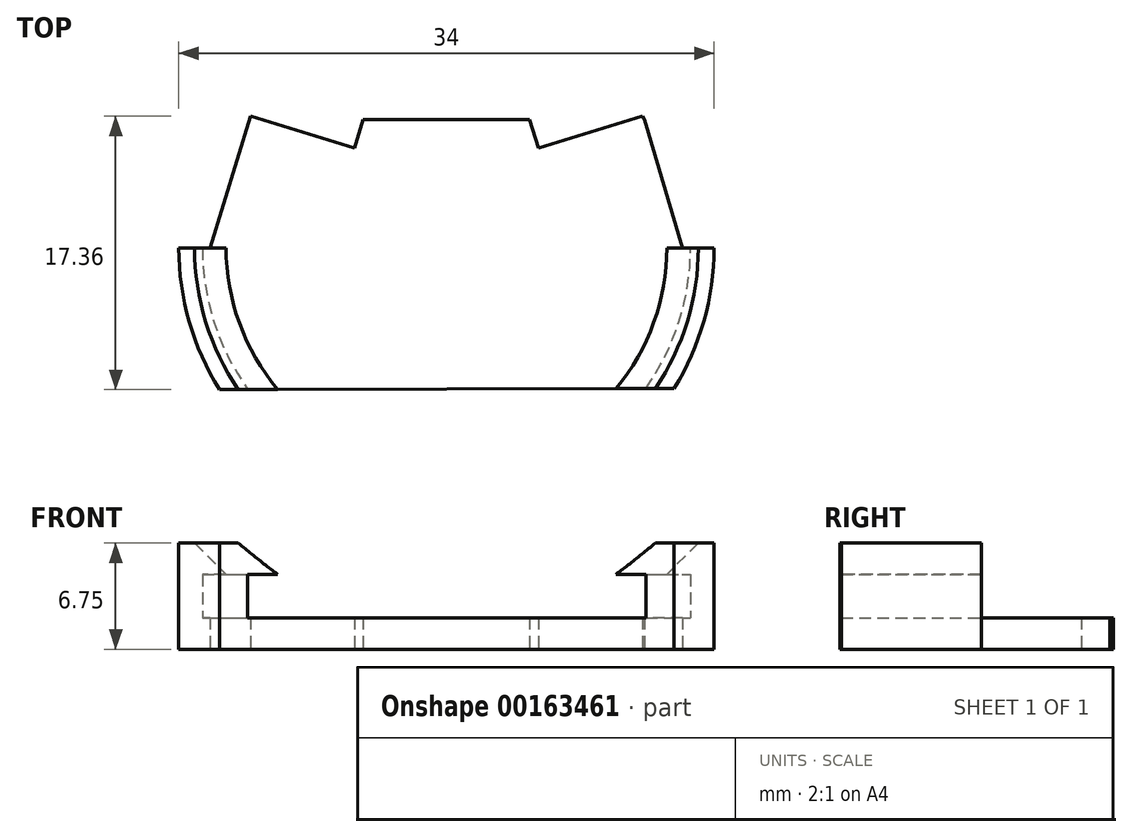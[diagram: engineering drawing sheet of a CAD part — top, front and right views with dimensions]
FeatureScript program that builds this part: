
annotation { "Feature Type Name" : "Feature", "Feature Type Description" : "" }
export const myFeature = defineFeature(function(context is Context, id is Id, definition is map)
    precondition{}
    {
        {
            var Q0;
            Q0=qCreatedBy(makeId("Top.planeOp"),FACE);
            var sketch = newSketch(context, id + "F0", { "sketchPlane" : qUnion([Q0])});
            skLineSegment(sketch, "E0", {"start": v(30.22, 5.42) * mm, "end": v(30.18, 5.6) * mm});
            skLineSegment(sketch, "E1", {"start": v(30.18, 5.6) * mm, "end": v(29.1, 8.94) * mm});
            skLineSegment(sketch, "E2", {"start": v(29.1, 8.94) * mm, "end": v(29.03, 9.1) * mm});
            skLineSegment(sketch, "E3", {"start": v(29.03, 9.1) * mm, "end": v(28.93, 9.25) * mm});
            skLineSegment(sketch, "E4", {"start": v(28.93, 9.25) * mm, "end": v(28.81, 9.38) * mm});
            skLineSegment(sketch, "E5", {"start": v(28.81, 9.38) * mm, "end": v(28.67, 9.48) * mm});
            skLineSegment(sketch, "E6", {"start": v(28.67, 9.48) * mm, "end": v(28.52, 9.56) * mm});
            skLineSegment(sketch, "E7", {"start": v(28.52, 9.56) * mm, "end": v(28.36, 9.6) * mm});
            skLineSegment(sketch, "E8", {"start": v(28.36, 9.6) * mm, "end": v(28.18, 9.63) * mm});
            skLineSegment(sketch, "E9", {"start": v(28.18, 9.63) * mm, "end": v(28, 9.62) * mm});
            skLineSegment(sketch, "E10", {"start": v(28, 9.62) * mm, "end": v(22.92, 8.87) * mm});
            skLineSegment(sketch, "E11", {"start": v(22.92, 8.87) * mm, "end": v(21.71, 8.48) * mm});
            skLineSegment(sketch, "E12", {"start": v(21.71, 8.48) * mm, "end": v(21.66, 8.46) * mm});
            skLineSegment(sketch, "E13", {"start": v(21.66, 8.46) * mm, "end": v(21.62, 8.44) * mm});
            skLineSegment(sketch, "E14", {"start": v(21.62, 8.44) * mm, "end": v(21.58, 8.4) * mm});
            skLineSegment(sketch, "E15", {"start": v(21.58, 8.4) * mm, "end": v(21.54, 8.38) * mm});
            skLineSegment(sketch, "E16", {"start": v(21.54, 8.38) * mm, "end": v(21.5, 8.34) * mm});
            skLineSegment(sketch, "E17", {"start": v(21.5, 8.34) * mm, "end": v(21.47, 8.3) * mm});
            skLineSegment(sketch, "E18", {"start": v(21.47, 8.3) * mm, "end": v(21.44, 8.26) * mm});
            skLineSegment(sketch, "E19", {"start": v(21.44, 8.26) * mm, "end": v(21.32, 8.03) * mm});
            skLineSegment(sketch, "E20", {"start": v(21.32, 8.03) * mm, "end": v(21.2, 7.86) * mm});
            skLineSegment(sketch, "E21", {"start": v(21.2, 7.86) * mm, "end": v(21.07, 7.7) * mm});
            skLineSegment(sketch, "E22", {"start": v(21.07, 7.7) * mm, "end": v(20.92, 7.56) * mm});
            skLineSegment(sketch, "E23", {"start": v(20.92, 7.56) * mm, "end": v(20.77, 7.43) * mm});
            skLineSegment(sketch, "E24", {"start": v(20.77, 7.43) * mm, "end": v(20.6, 7.32) * mm});
            skLineSegment(sketch, "E25", {"start": v(20.6, 7.32) * mm, "end": v(20.4, 7.22) * mm});
            skLineSegment(sketch, "E26", {"start": v(20.4, 7.22) * mm, "end": v(20.22, 7.15) * mm});
            skLineSegment(sketch, "E27", {"start": v(20.22, 7.15) * mm, "end": v(20.02, 7.1) * mm});
            skLineSegment(sketch, "E28", {"start": v(20.02, 7.1) * mm, "end": v(19.81, 7.06) * mm});
            skLineSegment(sketch, "E29", {"start": v(19.81, 7.06) * mm, "end": v(19.6, 7.05) * mm});
            skLineSegment(sketch, "E30", {"start": v(19.6, 7.05) * mm, "end": v(19.4, 7.06) * mm});
            skLineSegment(sketch, "E31", {"start": v(19.4, 7.06) * mm, "end": v(19.2, 7.1) * mm});
            skLineSegment(sketch, "E32", {"start": v(19.2, 7.1) * mm, "end": v(19, 7.14) * mm});
            skLineSegment(sketch, "E33", {"start": v(19, 7.14) * mm, "end": v(18.8, 7.21) * mm});
            skLineSegment(sketch, "E34", {"start": v(18.8, 7.21) * mm, "end": v(18.58, 7.33) * mm});
            skLineSegment(sketch, "E35", {"start": v(18.58, 7.33) * mm, "end": v(18.53, 7.35) * mm});
            skLineSegment(sketch, "E36", {"start": v(18.53, 7.35) * mm, "end": v(18.48, 7.36) * mm});
            skLineSegment(sketch, "E37", {"start": v(18.48, 7.36) * mm, "end": v(18.43, 7.37) * mm});
            skLineSegment(sketch, "E38", {"start": v(18.43, 7.37) * mm, "end": v(18.38, 7.37) * mm});
            skLineSegment(sketch, "E39", {"start": v(18.38, 7.37) * mm, "end": v(18.33, 7.37) * mm});
            skLineSegment(sketch, "E40", {"start": v(18.33, 7.37) * mm, "end": v(18.28, 7.36) * mm});
            skLineSegment(sketch, "E41", {"start": v(18.28, 7.36) * mm, "end": v(18.23, 7.34) * mm});
            skLineSegment(sketch, "E42", {"start": v(18.23, 7.34) * mm, "end": v(13.03, 5.66) * mm});
            skLineSegment(sketch, "E43", {"start": v(13.03, 5.66) * mm, "end": v(13, 5.65) * mm});
            skLineSegment(sketch, "E44", {"start": v(13, 5.65) * mm, "end": v(12.96, 5.65) * mm});
            skLineSegment(sketch, "E45", {"start": v(12.96, 5.65) * mm, "end": v(12.92, 5.64) * mm});
            skLineSegment(sketch, "E46", {"start": v(12.92, 5.64) * mm, "end": v(12.88, 5.64) * mm});
            skLineSegment(sketch, "E47", {"start": v(12.88, 5.64) * mm, "end": v(12.83, 5.64) * mm});
            skLineSegment(sketch, "E48", {"start": v(12.83, 5.64) * mm, "end": v(12.8, 5.64) * mm});
            skLineSegment(sketch, "E49", {"start": v(12.8, 5.64) * mm, "end": v(12.76, 5.65) * mm});
            skLineSegment(sketch, "E50", {"start": v(12.76, 5.65) * mm, "end": v(12.73, 5.66) * mm});
            skLineSegment(sketch, "E51", {"start": v(12.73, 5.66) * mm, "end": v(12.7, 5.68) * mm});
            skLineSegment(sketch, "E52", {"start": v(12.7, 5.68) * mm, "end": v(12.67, 5.7) * mm});
            skLineSegment(sketch, "E53", {"start": v(12.67, 5.7) * mm, "end": v(12.65, 5.72) * mm});
            skLineSegment(sketch, "E54", {"start": v(12.65, 5.72) * mm, "end": v(12.63, 5.74) * mm});
            skLineSegment(sketch, "E55", {"start": v(12.63, 5.74) * mm, "end": v(12.6, 5.77) * mm});
            skLineSegment(sketch, "E56", {"start": v(12.6, 5.77) * mm, "end": v(12.59, 5.8) * mm});
            skLineSegment(sketch, "E57", {"start": v(12.59, 5.8) * mm, "end": v(12.4, 6.07) * mm});
            skLineSegment(sketch, "E58", {"start": v(12.4, 6.07) * mm, "end": v(12.1, 6.48) * mm});
            skLineSegment(sketch, "E59", {"start": v(12.1, 6.48) * mm, "end": v(12.1, 6.5) * mm});
            skLineSegment(sketch, "E60", {"start": v(12.1, 6.5) * mm, "end": v(12.09, 6.52) * mm});
            skLineSegment(sketch, "E61", {"start": v(12.09, 6.52) * mm, "end": v(12.08, 6.54) * mm});
            skLineSegment(sketch, "E62", {"start": v(12.08, 6.54) * mm, "end": v(12.07, 6.56) * mm});
            skLineSegment(sketch, "E63", {"start": v(12.07, 6.56) * mm, "end": v(12.06, 6.58) * mm});
            skLineSegment(sketch, "E64", {"start": v(12.06, 6.58) * mm, "end": v(12.06, 6.6) * mm});
            skLineSegment(sketch, "E65", {"start": v(12.06, 6.6) * mm, "end": v(12.06, 6.63) * mm});
            skLineSegment(sketch, "E66", {"start": v(12.06, 6.63) * mm, "end": v(12.05, 6.65) * mm});
            skLineSegment(sketch, "E67", {"start": v(12.05, 6.65) * mm, "end": v(12.05, 6.67) * mm});
            skLineSegment(sketch, "E68", {"start": v(12.05, 6.67) * mm, "end": v(12.06, 6.7) * mm});
            skLineSegment(sketch, "E69", {"start": v(12.06, 6.7) * mm, "end": v(12.06, 6.71) * mm});
            skLineSegment(sketch, "E70", {"start": v(12.06, 6.71) * mm, "end": v(12.06, 6.73) * mm});
            skLineSegment(sketch, "E71", {"start": v(12.06, 6.73) * mm, "end": v(12.06, 6.73) * mm});
            skLineSegment(sketch, "E72", {"start": v(12.06, 6.73) * mm, "end": v(12.09, 6.78) * mm});
            skLineSegment(sketch, "E73", {"start": v(12.09, 6.78) * mm, "end": v(12.2, 7.09) * mm});
            skLineSegment(sketch, "E74", {"start": v(12.2, 7.09) * mm, "end": v(12.28, 7.42) * mm});
            skLineSegment(sketch, "E75", {"start": v(12.28, 7.42) * mm, "end": v(12.34, 7.75) * mm});
            skLineSegment(sketch, "E76", {"start": v(12.34, 7.75) * mm, "end": v(12.35, 8.1) * mm});
            skLineSegment(sketch, "E77", {"start": v(12.35, 8.1) * mm, "end": v(12.34, 8.45) * mm});
            skLineSegment(sketch, "E78", {"start": v(12.34, 8.45) * mm, "end": v(12.28, 8.79) * mm});
            skLineSegment(sketch, "E79", {"start": v(12.28, 8.79) * mm, "end": v(12.2, 9.11) * mm});
            skLineSegment(sketch, "E80", {"start": v(12.2, 9.11) * mm, "end": v(12.09, 9.42) * mm});
            skLineSegment(sketch, "E81", {"start": v(12.09, 9.42) * mm, "end": v(11.94, 9.72) * mm});
            skLineSegment(sketch, "E82", {"start": v(11.94, 9.72) * mm, "end": v(11.77, 10) * mm});
            skLineSegment(sketch, "E83", {"start": v(11.77, 10) * mm, "end": v(11.58, 10.26) * mm});
            skLineSegment(sketch, "E84", {"start": v(11.58, 10.26) * mm, "end": v(11.36, 10.5) * mm});
            skLineSegment(sketch, "E85", {"start": v(11.36, 10.5) * mm, "end": v(11.12, 10.72) * mm});
            skLineSegment(sketch, "E86", {"start": v(11.12, 10.72) * mm, "end": v(10.85, 10.92) * mm});
            skLineSegment(sketch, "E87", {"start": v(10.85, 10.92) * mm, "end": v(10.57, 11.09) * mm});
            skLineSegment(sketch, "E88", {"start": v(10.57, 11.09) * mm, "end": v(10.28, 11.23) * mm});
            skLineSegment(sketch, "E89", {"start": v(10.28, 11.23) * mm, "end": v(9.96, 11.35) * mm});
            skLineSegment(sketch, "E90", {"start": v(9.96, 11.35) * mm, "end": v(9.64, 11.43) * mm});
            skLineSegment(sketch, "E91", {"start": v(9.64, 11.43) * mm, "end": v(9.3, 11.48) * mm});
            skLineSegment(sketch, "E92", {"start": v(9.3, 11.48) * mm, "end": v(8.95, 11.5) * mm});
            skLineSegment(sketch, "E93", {"start": v(8.95, 11.5) * mm, "end": v(8.6, 11.48) * mm});
            skLineSegment(sketch, "E94", {"start": v(8.6, 11.48) * mm, "end": v(8.27, 11.43) * mm});
            skLineSegment(sketch, "E95", {"start": v(8.27, 11.43) * mm, "end": v(7.94, 11.35) * mm});
            skLineSegment(sketch, "E96", {"start": v(7.94, 11.35) * mm, "end": v(7.63, 11.23) * mm});
            skLineSegment(sketch, "E97", {"start": v(7.63, 11.23) * mm, "end": v(7.33, 11.1) * mm});
            skLineSegment(sketch, "E98", {"start": v(7.33, 11.1) * mm, "end": v(7.05, 10.92) * mm});
            skLineSegment(sketch, "E99", {"start": v(7.05, 10.92) * mm, "end": v(6.8, 10.72) * mm});
            skLineSegment(sketch, "E100", {"start": v(6.8, 10.72) * mm, "end": v(6.63, 10.58) * mm});
            skLineSegment(sketch, "E101", {"start": v(6.63, 10.58) * mm, "end": v(6.55, 10.51) * mm});
            skLineSegment(sketch, "E102", {"start": v(6.55, 10.51) * mm, "end": v(6.47, 10.47) * mm});
            skLineSegment(sketch, "E103", {"start": v(6.47, 10.47) * mm, "end": v(6.37, 10.44) * mm});
            skLineSegment(sketch, "E104", {"start": v(6.37, 10.44) * mm, "end": v(6.27, 10.43) * mm});
            skLineSegment(sketch, "E105", {"start": v(6.27, 10.43) * mm, "end": v(6.17, 10.44) * mm});
            skLineSegment(sketch, "E106", {"start": v(6.17, 10.44) * mm, "end": v(6.08, 10.47) * mm});
            skLineSegment(sketch, "E107", {"start": v(6.08, 10.47) * mm, "end": v(6.02, 10.5) * mm});
            skLineSegment(sketch, "E108", {"start": v(6.02, 10.5) * mm, "end": v(5.84, 10.58) * mm});
            skLineSegment(sketch, "E109", {"start": v(5.84, 10.58) * mm, "end": v(5.53, 10.72) * mm});
            skLineSegment(sketch, "E110", {"start": v(5.53, 10.72) * mm, "end": v(5.2, 10.85) * mm});
            skLineSegment(sketch, "E111", {"start": v(5.2, 10.85) * mm, "end": v(4.88, 10.97) * mm});
            skLineSegment(sketch, "E112", {"start": v(4.88, 10.97) * mm, "end": v(4.56, 11.1) * mm});
            skLineSegment(sketch, "E113", {"start": v(4.56, 11.1) * mm, "end": v(4.22, 11.2) * mm});
            skLineSegment(sketch, "E114", {"start": v(4.22, 11.2) * mm, "end": v(4.02, 11.26) * mm});
            skLineSegment(sketch, "E115", {"start": v(4.02, 11.26) * mm, "end": v(3.9, 11.29) * mm});
            skLineSegment(sketch, "E116", {"start": v(3.9, 11.29) * mm, "end": v(3.82, 11.34) * mm});
            skLineSegment(sketch, "E117", {"start": v(3.82, 11.34) * mm, "end": v(3.75, 11.4) * mm});
            skLineSegment(sketch, "E118", {"start": v(3.75, 11.4) * mm, "end": v(3.68, 11.47) * mm});
            skLineSegment(sketch, "E119", {"start": v(3.68, 11.47) * mm, "end": v(3.64, 11.56) * mm});
            skLineSegment(sketch, "E120", {"start": v(3.64, 11.56) * mm, "end": v(3.6, 11.65) * mm});
            skLineSegment(sketch, "E121", {"start": v(3.6, 11.65) * mm, "end": v(3.6, 11.76) * mm});
            skLineSegment(sketch, "E122", {"start": v(3.6, 11.76) * mm, "end": v(3.6, 17.97) * mm});
            skLineSegment(sketch, "E123", {"start": v(3.6, 17.97) * mm, "end": v(3.6, 18.02) * mm});
            skLineSegment(sketch, "E124", {"start": v(3.6, 18.02) * mm, "end": v(3.59, 18.07) * mm});
            skLineSegment(sketch, "E125", {"start": v(3.59, 18.07) * mm, "end": v(3.58, 18.12) * mm});
            skLineSegment(sketch, "E126", {"start": v(3.58, 18.12) * mm, "end": v(3.56, 18.17) * mm});
            skLineSegment(sketch, "E127", {"start": v(3.56, 18.17) * mm, "end": v(3.54, 18.21) * mm});
            skLineSegment(sketch, "E128", {"start": v(3.54, 18.21) * mm, "end": v(3.5, 18.26) * mm});
            skLineSegment(sketch, "E129", {"start": v(3.5, 18.26) * mm, "end": v(3.48, 18.3) * mm});
            skLineSegment(sketch, "E130", {"start": v(3.48, 18.3) * mm, "end": v(3.3, 18.48) * mm});
            skLineSegment(sketch, "E131", {"start": v(3.3, 18.48) * mm, "end": v(3.17, 18.65) * mm});
            skLineSegment(sketch, "E132", {"start": v(3.17, 18.65) * mm, "end": v(3.06, 18.82) * mm});
            skLineSegment(sketch, "E133", {"start": v(3.06, 18.82) * mm, "end": v(2.97, 19) * mm});
            skLineSegment(sketch, "E134", {"start": v(2.97, 19) * mm, "end": v(2.9, 19.2) * mm});
            skLineSegment(sketch, "E135", {"start": v(2.9, 19.2) * mm, "end": v(2.84, 19.4) * mm});
            skLineSegment(sketch, "E136", {"start": v(2.84, 19.4) * mm, "end": v(2.81, 19.6) * mm});
            skLineSegment(sketch, "E137", {"start": v(2.81, 19.6) * mm, "end": v(2.8, 19.8) * mm});
            skLineSegment(sketch, "E138", {"start": v(2.8, 19.8) * mm, "end": v(2.81, 20) * mm});
            skLineSegment(sketch, "E139", {"start": v(2.81, 20) * mm, "end": v(2.84, 20.21) * mm});
            skLineSegment(sketch, "E140", {"start": v(2.84, 20.21) * mm, "end": v(2.9, 20.41) * mm});
            skLineSegment(sketch, "E141", {"start": v(2.9, 20.41) * mm, "end": v(2.97, 20.6) * mm});
            skLineSegment(sketch, "E142", {"start": v(2.97, 20.6) * mm, "end": v(3.06, 20.78) * mm});
            skLineSegment(sketch, "E143", {"start": v(3.06, 20.78) * mm, "end": v(3.17, 20.96) * mm});
            skLineSegment(sketch, "E144", {"start": v(3.17, 20.96) * mm, "end": v(3.3, 21.12) * mm});
            skLineSegment(sketch, "E145", {"start": v(3.3, 21.12) * mm, "end": v(3.48, 21.3) * mm});
            skLineSegment(sketch, "E146", {"start": v(3.48, 21.3) * mm, "end": v(3.5, 21.35) * mm});
            skLineSegment(sketch, "E147", {"start": v(3.5, 21.35) * mm, "end": v(3.54, 21.39) * mm});
            skLineSegment(sketch, "E148", {"start": v(3.54, 21.39) * mm, "end": v(3.56, 21.44) * mm});
            skLineSegment(sketch, "E149", {"start": v(3.56, 21.44) * mm, "end": v(3.58, 21.48) * mm});
            skLineSegment(sketch, "E150", {"start": v(3.58, 21.48) * mm, "end": v(3.59, 21.53) * mm});
            skLineSegment(sketch, "E151", {"start": v(3.59, 21.53) * mm, "end": v(3.6, 21.58) * mm});
            skLineSegment(sketch, "E152", {"start": v(3.6, 21.58) * mm, "end": v(3.6, 21.63) * mm});
            skLineSegment(sketch, "E153", {"start": v(3.6, 21.63) * mm, "end": v(3.6, 22.9) * mm});
            skLineSegment(sketch, "E154", {"start": v(3.6, 22.9) * mm, "end": v(2.74, 27.97) * mm});
            skLineSegment(sketch, "E155", {"start": v(2.74, 27.97) * mm, "end": v(2.7, 28.14) * mm});
            skLineSegment(sketch, "E156", {"start": v(2.7, 28.14) * mm, "end": v(2.62, 28.3) * mm});
            skLineSegment(sketch, "E157", {"start": v(2.62, 28.3) * mm, "end": v(2.52, 28.44) * mm});
            skLineSegment(sketch, "E158", {"start": v(2.52, 28.44) * mm, "end": v(2.4, 28.57) * mm});
            skLineSegment(sketch, "E159", {"start": v(2.4, 28.57) * mm, "end": v(2.26, 28.67) * mm});
            skLineSegment(sketch, "E160", {"start": v(2.26, 28.67) * mm, "end": v(2.1, 28.74) * mm});
            skLineSegment(sketch, "E161", {"start": v(2.1, 28.74) * mm, "end": v(1.93, 28.79) * mm});
            skLineSegment(sketch, "E162", {"start": v(1.93, 28.79) * mm, "end": v(1.76, 28.8) * mm});
            skLineSegment(sketch, "E163", {"start": v(1.76, 28.8) * mm, "end": v(-1.4, 28.8) * mm});
            skLineSegment(sketch, "E164", {"start": v(-1.4, 28.8) * mm, "end": v(1.6, 28.8) * mm});
            skLineSegment(sketch, "E165", {"start": v(-1.4, 28.8) * mm, "end": v(-1.7, 28.8) * mm});
            skLineSegment(sketch, "E166", {"start": v(-1.7, 28.8) * mm, "end": v(-1.76, 28.8) * mm});
            skLineSegment(sketch, "E167", {"start": v(-1.76, 28.8) * mm, "end": v(-1.93, 28.79) * mm});
            skLineSegment(sketch, "E168", {"start": v(-1.93, 28.79) * mm, "end": v(-2.1, 28.74) * mm});
            skLineSegment(sketch, "E169", {"start": v(-2.1, 28.74) * mm, "end": v(-2.26, 28.67) * mm});
            skLineSegment(sketch, "E170", {"start": v(-2.26, 28.67) * mm, "end": v(-2.4, 28.57) * mm});
            skLineSegment(sketch, "E171", {"start": v(-2.4, 28.57) * mm, "end": v(-2.52, 28.44) * mm});
            skLineSegment(sketch, "E172", {"start": v(-2.52, 28.44) * mm, "end": v(-2.62, 28.3) * mm});
            skLineSegment(sketch, "E173", {"start": v(-2.62, 28.3) * mm, "end": v(-2.7, 28.14) * mm});
            skLineSegment(sketch, "E174", {"start": v(-2.7, 28.14) * mm, "end": v(-2.74, 27.97) * mm});
            skLineSegment(sketch, "E175", {"start": v(-2.74, 27.97) * mm, "end": v(-3.6, 22.9) * mm});
            skLineSegment(sketch, "E176", {"start": v(-3.6, 22.9) * mm, "end": v(-3.6, 21.63) * mm});
            skLineSegment(sketch, "E177", {"start": v(-3.6, 21.63) * mm, "end": v(-3.6, 21.58) * mm});
            skLineSegment(sketch, "E178", {"start": v(-3.6, 21.58) * mm, "end": v(-3.59, 21.53) * mm});
            skLineSegment(sketch, "E179", {"start": v(-3.59, 21.53) * mm, "end": v(-3.58, 21.48) * mm});
            skLineSegment(sketch, "E180", {"start": v(-3.58, 21.48) * mm, "end": v(-3.56, 21.44) * mm});
            skLineSegment(sketch, "E181", {"start": v(-3.56, 21.44) * mm, "end": v(-3.53, 21.39) * mm});
            skLineSegment(sketch, "E182", {"start": v(-3.53, 21.39) * mm, "end": v(-3.5, 21.35) * mm});
            skLineSegment(sketch, "E183", {"start": v(-3.5, 21.35) * mm, "end": v(-3.48, 21.3) * mm});
            skLineSegment(sketch, "E184", {"start": v(-3.48, 21.3) * mm, "end": v(-3.3, 21.12) * mm});
            skLineSegment(sketch, "E185", {"start": v(-3.3, 21.12) * mm, "end": v(-3.17, 20.96) * mm});
            skLineSegment(sketch, "E186", {"start": v(-3.17, 20.96) * mm, "end": v(-3.06, 20.78) * mm});
            skLineSegment(sketch, "E187", {"start": v(-3.06, 20.78) * mm, "end": v(-2.97, 20.6) * mm});
            skLineSegment(sketch, "E188", {"start": v(-2.97, 20.6) * mm, "end": v(-2.9, 20.41) * mm});
            skLineSegment(sketch, "E189", {"start": v(-2.9, 20.41) * mm, "end": v(-2.84, 20.21) * mm});
            skLineSegment(sketch, "E190", {"start": v(-2.84, 20.21) * mm, "end": v(-2.8, 20) * mm});
            skLineSegment(sketch, "E191", {"start": v(-2.8, 20) * mm, "end": v(-2.8, 19.8) * mm});
            skLineSegment(sketch, "E192", {"start": v(-2.8, 19.8) * mm, "end": v(-2.8, 19.6) * mm});
            skLineSegment(sketch, "E193", {"start": v(-2.8, 19.6) * mm, "end": v(-2.84, 19.4) * mm});
            skLineSegment(sketch, "E194", {"start": v(-2.84, 19.4) * mm, "end": v(-2.9, 19.2) * mm});
            skLineSegment(sketch, "E195", {"start": v(-2.9, 19.2) * mm, "end": v(-2.97, 19) * mm});
            skLineSegment(sketch, "E196", {"start": v(-2.97, 19) * mm, "end": v(-3.06, 18.82) * mm});
            skLineSegment(sketch, "E197", {"start": v(-3.06, 18.82) * mm, "end": v(-3.17, 18.65) * mm});
            skLineSegment(sketch, "E198", {"start": v(-3.17, 18.65) * mm, "end": v(-3.3, 18.48) * mm});
            skLineSegment(sketch, "E199", {"start": v(-3.3, 18.48) * mm, "end": v(-3.48, 18.3) * mm});
            skLineSegment(sketch, "E200", {"start": v(-3.48, 18.3) * mm, "end": v(-3.5, 18.26) * mm});
            skLineSegment(sketch, "E201", {"start": v(-3.5, 18.26) * mm, "end": v(-3.53, 18.21) * mm});
            skLineSegment(sketch, "E202", {"start": v(-3.53, 18.21) * mm, "end": v(-3.56, 18.17) * mm});
            skLineSegment(sketch, "E203", {"start": v(-3.56, 18.17) * mm, "end": v(-3.58, 18.12) * mm});
            skLineSegment(sketch, "E204", {"start": v(-3.58, 18.12) * mm, "end": v(-3.59, 18.07) * mm});
            skLineSegment(sketch, "E205", {"start": v(-3.59, 18.07) * mm, "end": v(-3.6, 18.02) * mm});
            skLineSegment(sketch, "E206", {"start": v(-3.6, 18.02) * mm, "end": v(-3.6, 17.97) * mm});
            skLineSegment(sketch, "E207", {"start": v(-3.6, 17.97) * mm, "end": v(-3.6, 11.83) * mm});
            skLineSegment(sketch, "E208", {"start": v(-3.6, 11.83) * mm, "end": v(-3.6, 11.66) * mm});
            skLineSegment(sketch, "E209", {"start": v(-3.6, 11.66) * mm, "end": v(-3.63, 11.56) * mm});
            skLineSegment(sketch, "E210", {"start": v(-3.63, 11.56) * mm, "end": v(-3.68, 11.48) * mm});
            skLineSegment(sketch, "E211", {"start": v(-3.68, 11.48) * mm, "end": v(-3.74, 11.4) * mm});
            skLineSegment(sketch, "E212", {"start": v(-3.74, 11.4) * mm, "end": v(-3.81, 11.34) * mm});
            skLineSegment(sketch, "E213", {"start": v(-3.81, 11.34) * mm, "end": v(-3.9, 11.3) * mm});
            skLineSegment(sketch, "E214", {"start": v(-3.9, 11.3) * mm, "end": v(-3.94, 11.28) * mm});
            skLineSegment(sketch, "E215", {"start": v(-3.94, 11.28) * mm, "end": v(-3.94, 11.28) * mm});
            skLineSegment(sketch, "E216", {"start": v(-3.94, 11.28) * mm, "end": v(-4, 11.27) * mm});
            skLineSegment(sketch, "E217", {"start": v(-4, 11.27) * mm, "end": v(-4.22, 11.2) * mm});
            skLineSegment(sketch, "E218", {"start": v(-4.22, 11.2) * mm, "end": v(-4.55, 11.1) * mm});
            skLineSegment(sketch, "E219", {"start": v(-4.55, 11.1) * mm, "end": v(-4.88, 10.97) * mm});
            skLineSegment(sketch, "E220", {"start": v(-4.88, 10.97) * mm, "end": v(-5.2, 10.85) * mm});
            skLineSegment(sketch, "E221", {"start": v(-5.2, 10.85) * mm, "end": v(-5.53, 10.72) * mm});
            skLineSegment(sketch, "E222", {"start": v(-5.53, 10.72) * mm, "end": v(-5.84, 10.58) * mm});
            skLineSegment(sketch, "E223", {"start": v(-5.84, 10.58) * mm, "end": v(-6.12, 10.45) * mm});
            skLineSegment(sketch, "E224", {"start": v(-6.12, 10.45) * mm, "end": v(-6.12, 10.45) * mm});
            skLineSegment(sketch, "E225", {"start": v(-6.12, 10.45) * mm, "end": v(-6.22, 10.42) * mm});
            skLineSegment(sketch, "E226", {"start": v(-6.22, 10.42) * mm, "end": v(-6.32, 10.41) * mm});
            skLineSegment(sketch, "E227", {"start": v(-6.32, 10.41) * mm, "end": v(-6.42, 10.42) * mm});
            skLineSegment(sketch, "E228", {"start": v(-6.42, 10.42) * mm, "end": v(-6.51, 10.45) * mm});
            skLineSegment(sketch, "E229", {"start": v(-6.51, 10.45) * mm, "end": v(-6.6, 10.5) * mm});
            skLineSegment(sketch, "E230", {"start": v(-6.6, 10.5) * mm, "end": v(-6.66, 10.55) * mm});
            skLineSegment(sketch, "E231", {"start": v(-6.66, 10.55) * mm, "end": v(-6.66, 10.55) * mm});
            skLineSegment(sketch, "E232", {"start": v(-6.66, 10.55) * mm, "end": v(-6.85, 10.72) * mm});
            skLineSegment(sketch, "E233", {"start": v(-6.85, 10.72) * mm, "end": v(-7.12, 10.92) * mm});
            skLineSegment(sketch, "E234", {"start": v(-7.12, 10.92) * mm, "end": v(-7.4, 11.09) * mm});
            skLineSegment(sketch, "E235", {"start": v(-7.4, 11.09) * mm, "end": v(-7.7, 11.23) * mm});
            skLineSegment(sketch, "E236", {"start": v(-7.7, 11.23) * mm, "end": v(-8, 11.35) * mm});
            skLineSegment(sketch, "E237", {"start": v(-8, 11.35) * mm, "end": v(-8.33, 11.43) * mm});
            skLineSegment(sketch, "E238", {"start": v(-8.33, 11.43) * mm, "end": v(-8.67, 11.48) * mm});
            skLineSegment(sketch, "E239", {"start": v(-8.67, 11.48) * mm, "end": v(-9.02, 11.5) * mm});
            skLineSegment(sketch, "E240", {"start": v(-9.02, 11.5) * mm, "end": v(-9.36, 11.48) * mm});
            skLineSegment(sketch, "E241", {"start": v(-9.36, 11.48) * mm, "end": v(-9.7, 11.43) * mm});
            skLineSegment(sketch, "E242", {"start": v(-9.7, 11.43) * mm, "end": v(-10.03, 11.35) * mm});
            skLineSegment(sketch, "E243", {"start": v(-10.03, 11.35) * mm, "end": v(-10.34, 11.23) * mm});
            skLineSegment(sketch, "E244", {"start": v(-10.34, 11.23) * mm, "end": v(-10.64, 11.09) * mm});
            skLineSegment(sketch, "E245", {"start": v(-10.64, 11.09) * mm, "end": v(-10.92, 10.92) * mm});
            skLineSegment(sketch, "E246", {"start": v(-10.92, 10.92) * mm, "end": v(-11.18, 10.72) * mm});
            skLineSegment(sketch, "E247", {"start": v(-11.18, 10.72) * mm, "end": v(-11.42, 10.5) * mm});
            skLineSegment(sketch, "E248", {"start": v(-11.42, 10.5) * mm, "end": v(-11.64, 10.26) * mm});
            skLineSegment(sketch, "E249", {"start": v(-11.64, 10.26) * mm, "end": v(-11.84, 10) * mm});
            skLineSegment(sketch, "E250", {"start": v(-11.84, 10) * mm, "end": v(-12, 9.72) * mm});
            skLineSegment(sketch, "E251", {"start": v(-12, 9.72) * mm, "end": v(-12.15, 9.42) * mm});
            skLineSegment(sketch, "E252", {"start": v(-12.15, 9.42) * mm, "end": v(-12.26, 9.11) * mm});
            skLineSegment(sketch, "E253", {"start": v(-12.26, 9.11) * mm, "end": v(-12.35, 8.79) * mm});
            skLineSegment(sketch, "E254", {"start": v(-12.35, 8.79) * mm, "end": v(-12.4, 8.45) * mm});
            skLineSegment(sketch, "E255", {"start": v(-12.4, 8.45) * mm, "end": v(-12.42, 8.1) * mm});
            skLineSegment(sketch, "E256", {"start": v(-12.42, 8.1) * mm, "end": v(-12.4, 7.75) * mm});
            skLineSegment(sketch, "E257", {"start": v(-12.4, 7.75) * mm, "end": v(-12.35, 7.42) * mm});
            skLineSegment(sketch, "E258", {"start": v(-12.35, 7.42) * mm, "end": v(-12.26, 7.09) * mm});
            skLineSegment(sketch, "E259", {"start": v(-12.26, 7.09) * mm, "end": v(-12.15, 6.78) * mm});
            skLineSegment(sketch, "E260", {"start": v(-12.15, 6.78) * mm, "end": v(-12.1, 6.67) * mm});
            skLineSegment(sketch, "E261", {"start": v(-12.1, 6.67) * mm, "end": v(-12.1, 6.67) * mm});
            skLineSegment(sketch, "E262", {"start": v(-12.1, 6.67) * mm, "end": v(-12.1, 6.64) * mm});
            skLineSegment(sketch, "E263", {"start": v(-12.1, 6.64) * mm, "end": v(-12.1, 6.61) * mm});
            skLineSegment(sketch, "E264", {"start": v(-12.1, 6.61) * mm, "end": v(-12.1, 6.58) * mm});
            skLineSegment(sketch, "E265", {"start": v(-12.1, 6.58) * mm, "end": v(-12.1, 6.56) * mm});
            skLineSegment(sketch, "E266", {"start": v(-12.1, 6.56) * mm, "end": v(-12.1, 6.53) * mm});
            skLineSegment(sketch, "E267", {"start": v(-12.1, 6.53) * mm, "end": v(-12.1, 6.51) * mm});
            skLineSegment(sketch, "E268", {"start": v(-12.1, 6.51) * mm, "end": v(-12.11, 6.5) * mm});
            skLineSegment(sketch, "E269", {"start": v(-12.11, 6.5) * mm, "end": v(-12.12, 6.47) * mm});
            skLineSegment(sketch, "E270", {"start": v(-12.12, 6.47) * mm, "end": v(-12.13, 6.45) * mm});
            skLineSegment(sketch, "E271", {"start": v(-12.13, 6.45) * mm, "end": v(-12.15, 6.43) * mm});
            skLineSegment(sketch, "E272", {"start": v(-12.15, 6.43) * mm, "end": v(-12.44, 6) * mm});
            skLineSegment(sketch, "E273", {"start": v(-12.44, 6) * mm, "end": v(-12.56, 5.83) * mm});
            skLineSegment(sketch, "E274", {"start": v(-12.56, 5.83) * mm, "end": v(-12.58, 5.8) * mm});
            skLineSegment(sketch, "E275", {"start": v(-12.58, 5.8) * mm, "end": v(-12.6, 5.77) * mm});
            skLineSegment(sketch, "E276", {"start": v(-12.6, 5.77) * mm, "end": v(-12.63, 5.74) * mm});
            skLineSegment(sketch, "E277", {"start": v(-12.63, 5.74) * mm, "end": v(-12.66, 5.71) * mm});
            skLineSegment(sketch, "E278", {"start": v(-12.66, 5.71) * mm, "end": v(-12.69, 5.7) * mm});
            skLineSegment(sketch, "E279", {"start": v(-12.69, 5.7) * mm, "end": v(-12.72, 5.67) * mm});
            skLineSegment(sketch, "E280", {"start": v(-12.72, 5.67) * mm, "end": v(-12.76, 5.66) * mm});
            skLineSegment(sketch, "E281", {"start": v(-12.76, 5.66) * mm, "end": v(-12.8, 5.65) * mm});
            skLineSegment(sketch, "E282", {"start": v(-12.8, 5.65) * mm, "end": v(-12.84, 5.64) * mm});
            skLineSegment(sketch, "E283", {"start": v(-12.84, 5.64) * mm, "end": v(-12.88, 5.64) * mm});
            skLineSegment(sketch, "E284", {"start": v(-12.88, 5.64) * mm, "end": v(-12.93, 5.65) * mm});
            skLineSegment(sketch, "E285", {"start": v(-12.93, 5.65) * mm, "end": v(-13, 5.65) * mm});
            skLineSegment(sketch, "E286", {"start": v(-13, 5.65) * mm, "end": v(-13.03, 5.66) * mm});
            skLineSegment(sketch, "E287", {"start": v(-13.03, 5.66) * mm, "end": v(-18.23, 7.34) * mm});
            skLineSegment(sketch, "E288", {"start": v(-18.23, 7.34) * mm, "end": v(-18.28, 7.36) * mm});
            skLineSegment(sketch, "E289", {"start": v(-18.28, 7.36) * mm, "end": v(-18.33, 7.37) * mm});
            skLineSegment(sketch, "E290", {"start": v(-18.33, 7.37) * mm, "end": v(-18.38, 7.37) * mm});
            skLineSegment(sketch, "E291", {"start": v(-18.38, 7.37) * mm, "end": v(-18.43, 7.37) * mm});
            skLineSegment(sketch, "E292", {"start": v(-18.43, 7.37) * mm, "end": v(-18.48, 7.36) * mm});
            skLineSegment(sketch, "E293", {"start": v(-18.48, 7.36) * mm, "end": v(-18.53, 7.35) * mm});
            skLineSegment(sketch, "E294", {"start": v(-18.53, 7.35) * mm, "end": v(-18.58, 7.33) * mm});
            skLineSegment(sketch, "E295", {"start": v(-18.58, 7.33) * mm, "end": v(-18.8, 7.21) * mm});
            skLineSegment(sketch, "E296", {"start": v(-18.8, 7.21) * mm, "end": v(-19, 7.14) * mm});
            skLineSegment(sketch, "E297", {"start": v(-19, 7.14) * mm, "end": v(-19.2, 7.1) * mm});
            skLineSegment(sketch, "E298", {"start": v(-19.2, 7.1) * mm, "end": v(-19.4, 7.06) * mm});
            skLineSegment(sketch, "E299", {"start": v(-19.4, 7.06) * mm, "end": v(-19.6, 7.05) * mm});
            skLineSegment(sketch, "E300", {"start": v(-19.6, 7.05) * mm, "end": v(-19.81, 7.06) * mm});
            skLineSegment(sketch, "E301", {"start": v(-19.81, 7.06) * mm, "end": v(-20.02, 7.1) * mm});
            skLineSegment(sketch, "E302", {"start": v(-20.02, 7.1) * mm, "end": v(-20.22, 7.15) * mm});
            skLineSegment(sketch, "E303", {"start": v(-20.22, 7.15) * mm, "end": v(-20.4, 7.22) * mm});
            skLineSegment(sketch, "E304", {"start": v(-20.4, 7.22) * mm, "end": v(-20.6, 7.32) * mm});
            skLineSegment(sketch, "E305", {"start": v(-20.6, 7.32) * mm, "end": v(-20.77, 7.43) * mm});
            skLineSegment(sketch, "E306", {"start": v(-20.77, 7.43) * mm, "end": v(-20.92, 7.56) * mm});
            skLineSegment(sketch, "E307", {"start": v(-20.92, 7.56) * mm, "end": v(-21.07, 7.7) * mm});
            skLineSegment(sketch, "E308", {"start": v(-21.07, 7.7) * mm, "end": v(-21.2, 7.86) * mm});
            skLineSegment(sketch, "E309", {"start": v(-21.2, 7.86) * mm, "end": v(-21.32, 8.03) * mm});
            skLineSegment(sketch, "E310", {"start": v(-21.32, 8.03) * mm, "end": v(-21.44, 8.26) * mm});
            skLineSegment(sketch, "E311", {"start": v(-21.44, 8.26) * mm, "end": v(-21.47, 8.3) * mm});
            skLineSegment(sketch, "E312", {"start": v(-21.47, 8.3) * mm, "end": v(-21.5, 8.34) * mm});
            skLineSegment(sketch, "E313", {"start": v(-21.5, 8.34) * mm, "end": v(-21.53, 8.38) * mm});
            skLineSegment(sketch, "E314", {"start": v(-21.53, 8.38) * mm, "end": v(-21.57, 8.4) * mm});
            skLineSegment(sketch, "E315", {"start": v(-21.57, 8.4) * mm, "end": v(-21.62, 8.44) * mm});
            skLineSegment(sketch, "E316", {"start": v(-21.62, 8.44) * mm, "end": v(-21.66, 8.46) * mm});
            skLineSegment(sketch, "E317", {"start": v(-21.66, 8.46) * mm, "end": v(-21.71, 8.48) * mm});
            skLineSegment(sketch, "E318", {"start": v(-21.71, 8.48) * mm, "end": v(-22.92, 8.87) * mm});
            skLineSegment(sketch, "E319", {"start": v(-22.92, 8.87) * mm, "end": v(-28, 9.62) * mm});
            skLineSegment(sketch, "E320", {"start": v(-28, 9.62) * mm, "end": v(-28.18, 9.63) * mm});
            skLineSegment(sketch, "E321", {"start": v(-28.18, 9.63) * mm, "end": v(-28.36, 9.6) * mm});
            skLineSegment(sketch, "E322", {"start": v(-28.36, 9.6) * mm, "end": v(-28.52, 9.56) * mm});
            skLineSegment(sketch, "E323", {"start": v(-28.52, 9.56) * mm, "end": v(-28.67, 9.48) * mm});
            skLineSegment(sketch, "E324", {"start": v(-28.67, 9.48) * mm, "end": v(-28.81, 9.37) * mm});
            skLineSegment(sketch, "E325", {"start": v(-28.81, 9.37) * mm, "end": v(-28.93, 9.25) * mm});
            skLineSegment(sketch, "E326", {"start": v(-28.93, 9.25) * mm, "end": v(-29.03, 9.1) * mm});
            skLineSegment(sketch, "E327", {"start": v(-29.03, 9.1) * mm, "end": v(-29.1, 8.94) * mm});
            skLineSegment(sketch, "E328", {"start": v(-29.1, 8.94) * mm, "end": v(-30.18, 5.6) * mm});
            skLineSegment(sketch, "E329", {"start": v(-30.18, 5.6) * mm, "end": v(-30.22, 5.42) * mm});
            skLineSegment(sketch, "E330", {"start": v(-30.22, 5.42) * mm, "end": v(-30.23, 5.25) * mm});
            skLineSegment(sketch, "E331", {"start": v(-30.23, 5.25) * mm, "end": v(-30.2, 5.08) * mm});
            skLineSegment(sketch, "E332", {"start": v(-30.2, 5.08) * mm, "end": v(-30.16, 4.91) * mm});
            skLineSegment(sketch, "E333", {"start": v(-30.16, 4.91) * mm, "end": v(-30.08, 4.76) * mm});
            skLineSegment(sketch, "E334", {"start": v(-30.08, 4.76) * mm, "end": v(-29.98, 4.62) * mm});
            skLineSegment(sketch, "E335", {"start": v(-29.98, 4.62) * mm, "end": v(-29.85, 4.5) * mm});
            skLineSegment(sketch, "E336", {"start": v(-29.85, 4.5) * mm, "end": v(-29.7, 4.4) * mm});
            skLineSegment(sketch, "E337", {"start": v(-29.7, 4.4) * mm, "end": v(-25.14, 2.02) * mm});
            skLineSegment(sketch, "E338", {"start": v(-25.14, 2.02) * mm, "end": v(-23.94, 1.63) * mm});
            skLineSegment(sketch, "E339", {"start": v(-23.94, 1.63) * mm, "end": v(-23.89, 1.62) * mm});
            skLineSegment(sketch, "E340", {"start": v(-23.89, 1.62) * mm, "end": v(-23.84, 1.6) * mm});
            skLineSegment(sketch, "E341", {"start": v(-23.84, 1.6) * mm, "end": v(-23.79, 1.6) * mm});
            skLineSegment(sketch, "E342", {"start": v(-23.79, 1.6) * mm, "end": v(-23.73, 1.6) * mm});
            skLineSegment(sketch, "E343", {"start": v(-23.73, 1.6) * mm, "end": v(-23.68, 1.61) * mm});
            skLineSegment(sketch, "E344", {"start": v(-23.68, 1.61) * mm, "end": v(-23.63, 1.63) * mm});
            skLineSegment(sketch, "E345", {"start": v(-23.63, 1.63) * mm, "end": v(-23.59, 1.65) * mm});
            skLineSegment(sketch, "E346", {"start": v(-23.59, 1.65) * mm, "end": v(-23.35, 1.76) * mm});
            skLineSegment(sketch, "E347", {"start": v(-23.35, 1.76) * mm, "end": v(-23.16, 1.83) * mm});
            skLineSegment(sketch, "E348", {"start": v(-23.16, 1.83) * mm, "end": v(-22.96, 1.88) * mm});
            skLineSegment(sketch, "E349", {"start": v(-22.96, 1.88) * mm, "end": v(-22.76, 1.91) * mm});
            skLineSegment(sketch, "E350", {"start": v(-22.76, 1.91) * mm, "end": v(-22.55, 1.92) * mm});
            skLineSegment(sketch, "E351", {"start": v(-22.55, 1.92) * mm, "end": v(-22.35, 1.91) * mm});
            skLineSegment(sketch, "E352", {"start": v(-22.35, 1.91) * mm, "end": v(-22.15, 1.88) * mm});
            skLineSegment(sketch, "E353", {"start": v(-22.15, 1.88) * mm, "end": v(-21.95, 1.82) * mm});
            skLineSegment(sketch, "E354", {"start": v(-21.95, 1.82) * mm, "end": v(-21.75, 1.75) * mm});
            skLineSegment(sketch, "E355", {"start": v(-21.75, 1.75) * mm, "end": v(-21.57, 1.66) * mm});
            skLineSegment(sketch, "E356", {"start": v(-21.57, 1.66) * mm, "end": v(-21.4, 1.55) * mm});
            skLineSegment(sketch, "E357", {"start": v(-21.4, 1.55) * mm, "end": v(-21.24, 1.42) * mm});
            skLineSegment(sketch, "E358", {"start": v(-21.24, 1.42) * mm, "end": v(-21.1, 1.27) * mm});
            skLineSegment(sketch, "E359", {"start": v(-21.1, 1.27) * mm, "end": v(-20.96, 1.12) * mm});
            skLineSegment(sketch, "E360", {"start": v(-20.96, 1.12) * mm, "end": v(-20.85, 0.95) * mm});
            skLineSegment(sketch, "E361", {"start": v(-20.85, 0.95) * mm, "end": v(-20.72, 0.72) * mm});
            skLineSegment(sketch, "E362", {"start": v(-20.72, 0.72) * mm, "end": v(-20.7, 0.67) * mm});
            skLineSegment(sketch, "E363", {"start": v(-20.7, 0.67) * mm, "end": v(-20.66, 0.63) * mm});
            skLineSegment(sketch, "E364", {"start": v(-20.66, 0.63) * mm, "end": v(-20.63, 0.6) * mm});
            skLineSegment(sketch, "E365", {"start": v(-20.63, 0.6) * mm, "end": v(-20.59, 0.57) * mm});
            skLineSegment(sketch, "E366", {"start": v(-20.59, 0.57) * mm, "end": v(-20.54, 0.54) * mm});
            skLineSegment(sketch, "E367", {"start": v(-20.54, 0.54) * mm, "end": v(-20.5, 0.52) * mm});
            skLineSegment(sketch, "E368", {"start": v(-20.5, 0.52) * mm, "end": v(-20.45, 0.5) * mm});
            skLineSegment(sketch, "E369", {"start": v(-20.45, 0.5) * mm, "end": v(-15.32, -1.17) * mm});
            skLineSegment(sketch, "E370", {"start": v(-15.32, -1.17) * mm, "end": v(-15.3, -1.18) * mm});
            skLineSegment(sketch, "E371", {"start": v(-15.3, -1.18) * mm, "end": v(-15.25, -1.2) * mm});
            skLineSegment(sketch, "E372", {"start": v(-15.25, -1.2) * mm, "end": v(-15.21, -1.21) * mm});
            skLineSegment(sketch, "E373", {"start": v(-15.21, -1.21) * mm, "end": v(-15.16, -1.23) * mm});
            skLineSegment(sketch, "E374", {"start": v(-15.16, -1.23) * mm, "end": v(-15.12, -1.26) * mm});
            skLineSegment(sketch, "E375", {"start": v(-15.12, -1.26) * mm, "end": v(-15.08, -1.29) * mm});
            skLineSegment(sketch, "E376", {"start": v(-15.08, -1.29) * mm, "end": v(-15.05, -1.32) * mm});
            skLineSegment(sketch, "E377", {"start": v(-15.05, -1.32) * mm, "end": v(-15.03, -1.35) * mm});
            skLineSegment(sketch, "E378", {"start": v(-15.03, -1.35) * mm, "end": v(-15.01, -1.39) * mm});
            skLineSegment(sketch, "E379", {"start": v(-15.01, -1.39) * mm, "end": v(-15, -1.43) * mm});
            skLineSegment(sketch, "E380", {"start": v(-15, -1.43) * mm, "end": v(-14.99, -1.46) * mm});
            skLineSegment(sketch, "E381", {"start": v(-14.99, -1.46) * mm, "end": v(-14.98, -1.5) * mm});
            skLineSegment(sketch, "E382", {"start": v(-14.98, -1.5) * mm, "end": v(-14.98, -1.54) * mm});
            skLineSegment(sketch, "E383", {"start": v(-14.98, -1.54) * mm, "end": v(-14.98, -1.58) * mm});
            skLineSegment(sketch, "E384", {"start": v(-14.98, -1.58) * mm, "end": v(-15, -2.18) * mm});
            skLineSegment(sketch, "E385", {"start": v(-15, -2.18) * mm, "end": v(-15, -2.36) * mm});
            skLineSegment(sketch, "E386", {"start": v(-15, -2.36) * mm, "end": v(-14.94, -3.7) * mm});
            skLineSegment(sketch, "E387", {"start": v(-14.94, -3.7) * mm, "end": v(-14.77, -5) * mm});
            skLineSegment(sketch, "E388", {"start": v(-14.77, -5) * mm, "end": v(-14.49, -6.26) * mm});
            skLineSegment(sketch, "E389", {"start": v(-14.49, -6.26) * mm, "end": v(-14.1, -7.48) * mm});
            skLineSegment(sketch, "E390", {"start": v(-14.1, -7.48) * mm, "end": v(-13.62, -8.65) * mm});
            skLineSegment(sketch, "E391", {"start": v(-13.62, -8.65) * mm, "end": v(-13.04, -9.77) * mm});
            skLineSegment(sketch, "E392", {"start": v(-13.04, -9.77) * mm, "end": v(-12.38, -10.84) * mm});
            skLineSegment(sketch, "E393", {"start": v(-12.38, -10.84) * mm, "end": v(-11.6, -11.86) * mm});
            skLineSegment(sketch, "E394", {"start": v(-11.6, -11.86) * mm, "end": v(-11.6, -11.88) * mm});
            skLineSegment(sketch, "E395", {"start": v(-11.6, -11.88) * mm, "end": v(-11.59, -11.9) * mm});
            skLineSegment(sketch, "E396", {"start": v(-11.59, -11.9) * mm, "end": v(-11.58, -11.93) * mm});
            skLineSegment(sketch, "E397", {"start": v(-11.58, -11.93) * mm, "end": v(-11.57, -11.95) * mm});
            skLineSegment(sketch, "E398", {"start": v(-11.57, -11.95) * mm, "end": v(-11.57, -11.98) * mm});
            skLineSegment(sketch, "E399", {"start": v(-11.57, -11.98) * mm, "end": v(-11.57, -12) * mm});
            skLineSegment(sketch, "E400", {"start": v(-11.57, -12) * mm, "end": v(-11.57, -12.03) * mm});
            skLineSegment(sketch, "E401", {"start": v(-11.57, -12.03) * mm, "end": v(-11.57, -12.06) * mm});
            skLineSegment(sketch, "E402", {"start": v(-11.57, -12.06) * mm, "end": v(-11.58, -12.1) * mm});
            skLineSegment(sketch, "E403", {"start": v(-11.58, -12.1) * mm, "end": v(-11.6, -12.14) * mm});
            skLineSegment(sketch, "E404", {"start": v(-11.6, -12.14) * mm, "end": v(-11.6, -12.18) * mm});
            skLineSegment(sketch, "E405", {"start": v(-11.6, -12.18) * mm, "end": v(-11.62, -12.22) * mm});
            skLineSegment(sketch, "E406", {"start": v(-11.62, -12.22) * mm, "end": v(-11.65, -12.27) * mm});
            skLineSegment(sketch, "E407", {"start": v(-11.65, -12.27) * mm, "end": v(-11.65, -12.28) * mm});
            skLineSegment(sketch, "E408", {"start": v(-11.65, -12.28) * mm, "end": v(-14.87, -16.7) * mm});
            skLineSegment(sketch, "E409", {"start": v(-14.87, -16.7) * mm, "end": v(-14.9, -16.75) * mm});
            skLineSegment(sketch, "E410", {"start": v(-14.9, -16.75) * mm, "end": v(-14.92, -16.8) * mm});
            skLineSegment(sketch, "E411", {"start": v(-14.92, -16.8) * mm, "end": v(-14.94, -16.84) * mm});
            skLineSegment(sketch, "E412", {"start": v(-14.94, -16.84) * mm, "end": v(-14.95, -16.89) * mm});
            skLineSegment(sketch, "E413", {"start": v(-14.95, -16.89) * mm, "end": v(-14.96, -16.94) * mm});
            skLineSegment(sketch, "E414", {"start": v(-14.96, -16.94) * mm, "end": v(-14.96, -16.99) * mm});
            skLineSegment(sketch, "E415", {"start": v(-14.96, -16.99) * mm, "end": v(-14.96, -17.04) * mm});
            skLineSegment(sketch, "E416", {"start": v(-14.96, -17.04) * mm, "end": v(-14.92, -17.3) * mm});
            skLineSegment(sketch, "E417", {"start": v(-14.92, -17.3) * mm, "end": v(-14.92, -17.5) * mm});
            skLineSegment(sketch, "E418", {"start": v(-14.92, -17.5) * mm, "end": v(-14.93, -17.7) * mm});
            skLineSegment(sketch, "E419", {"start": v(-14.93, -17.7) * mm, "end": v(-14.96, -17.9) * mm});
            skLineSegment(sketch, "E420", {"start": v(-14.96, -17.9) * mm, "end": v(-15.02, -18.1) * mm});
            skLineSegment(sketch, "E421", {"start": v(-15.02, -18.1) * mm, "end": v(-15.1, -18.3) * mm});
            skLineSegment(sketch, "E422", {"start": v(-15.1, -18.3) * mm, "end": v(-15.18, -18.48) * mm});
            skLineSegment(sketch, "E423", {"start": v(-15.18, -18.48) * mm, "end": v(-15.3, -18.65) * mm});
            skLineSegment(sketch, "E424", {"start": v(-15.3, -18.65) * mm, "end": v(-15.43, -18.82) * mm});
            skLineSegment(sketch, "E425", {"start": v(-15.43, -18.82) * mm, "end": v(-15.57, -18.96) * mm});
            skLineSegment(sketch, "E426", {"start": v(-15.57, -18.96) * mm, "end": v(-15.73, -19.1) * mm});
            skLineSegment(sketch, "E427", {"start": v(-15.73, -19.1) * mm, "end": v(-15.9, -19.2) * mm});
            skLineSegment(sketch, "E428", {"start": v(-15.9, -19.2) * mm, "end": v(-16.08, -19.3) * mm});
            skLineSegment(sketch, "E429", {"start": v(-16.08, -19.3) * mm, "end": v(-16.27, -19.37) * mm});
            skLineSegment(sketch, "E430", {"start": v(-16.27, -19.37) * mm, "end": v(-16.47, -19.43) * mm});
            skLineSegment(sketch, "E431", {"start": v(-16.47, -19.43) * mm, "end": v(-16.73, -19.47) * mm});
            skLineSegment(sketch, "E432", {"start": v(-16.73, -19.47) * mm, "end": v(-16.78, -19.49) * mm});
            skLineSegment(sketch, "E433", {"start": v(-16.78, -19.49) * mm, "end": v(-16.83, -19.5) * mm});
            skLineSegment(sketch, "E434", {"start": v(-16.83, -19.5) * mm, "end": v(-16.87, -19.53) * mm});
            skLineSegment(sketch, "E435", {"start": v(-16.87, -19.53) * mm, "end": v(-16.91, -19.56) * mm});
            skLineSegment(sketch, "E436", {"start": v(-16.91, -19.56) * mm, "end": v(-16.95, -19.6) * mm});
            skLineSegment(sketch, "E437", {"start": v(-16.95, -19.6) * mm, "end": v(-16.99, -19.63) * mm});
            skLineSegment(sketch, "E438", {"start": v(-16.99, -19.63) * mm, "end": v(-17.02, -19.67) * mm});
            skLineSegment(sketch, "E439", {"start": v(-17.02, -19.67) * mm, "end": v(-17.77, -20.7) * mm});
            skLineSegment(sketch, "E440", {"start": v(-17.77, -20.7) * mm, "end": v(-20.05, -25.3) * mm});
            skLineSegment(sketch, "E441", {"start": v(-20.05, -25.3) * mm, "end": v(-20.12, -25.46) * mm});
            skLineSegment(sketch, "E442", {"start": v(-20.12, -25.46) * mm, "end": v(-20.15, -25.64) * mm});
            skLineSegment(sketch, "E443", {"start": v(-20.15, -25.64) * mm, "end": v(-20.15, -25.8) * mm});
            skLineSegment(sketch, "E444", {"start": v(-20.15, -25.8) * mm, "end": v(-20.13, -25.98) * mm});
            skLineSegment(sketch, "E445", {"start": v(-20.13, -25.98) * mm, "end": v(-20.07, -26.14) * mm});
            skLineSegment(sketch, "E446", {"start": v(-20.07, -26.14) * mm, "end": v(-19.99, -26.3) * mm});
            skLineSegment(sketch, "E447", {"start": v(-19.99, -26.3) * mm, "end": v(-19.88, -26.43) * mm});
            skLineSegment(sketch, "E448", {"start": v(-19.88, -26.43) * mm, "end": v(-19.74, -26.55) * mm});
            skLineSegment(sketch, "E449", {"start": v(-19.74, -26.55) * mm, "end": v(-16.9, -28.61) * mm});
            skLineSegment(sketch, "E450", {"start": v(-16.9, -28.61) * mm, "end": v(-16.75, -28.7) * mm});
            skLineSegment(sketch, "E451", {"start": v(-16.75, -28.7) * mm, "end": v(-16.58, -28.77) * mm});
            skLineSegment(sketch, "E452", {"start": v(-16.58, -28.77) * mm, "end": v(-16.41, -28.8) * mm});
            skLineSegment(sketch, "E453", {"start": v(-16.41, -28.8) * mm, "end": v(-16.24, -28.8) * mm});
            skLineSegment(sketch, "E454", {"start": v(-16.24, -28.8) * mm, "end": v(-16.07, -28.78) * mm});
            skLineSegment(sketch, "E455", {"start": v(-16.07, -28.78) * mm, "end": v(-15.9, -28.72) * mm});
            skLineSegment(sketch, "E456", {"start": v(-15.9, -28.72) * mm, "end": v(-15.75, -28.63) * mm});
            skLineSegment(sketch, "E457", {"start": v(-15.75, -28.63) * mm, "end": v(-15.61, -28.52) * mm});
            skLineSegment(sketch, "E458", {"start": v(-15.61, -28.52) * mm, "end": v(-11.94, -24.92) * mm});
            skLineSegment(sketch, "E459", {"start": v(-11.94, -24.92) * mm, "end": v(-11.2, -23.9) * mm});
            skLineSegment(sketch, "E460", {"start": v(-11.2, -23.9) * mm, "end": v(-11.17, -23.86) * mm});
            skLineSegment(sketch, "E461", {"start": v(-11.17, -23.86) * mm, "end": v(-11.15, -23.81) * mm});
            skLineSegment(sketch, "E462", {"start": v(-11.15, -23.81) * mm, "end": v(-11.13, -23.76) * mm});
            skLineSegment(sketch, "E463", {"start": v(-11.13, -23.76) * mm, "end": v(-11.11, -23.71) * mm});
            skLineSegment(sketch, "E464", {"start": v(-11.11, -23.71) * mm, "end": v(-11.1, -23.66) * mm});
            skLineSegment(sketch, "E465", {"start": v(-11.1, -23.66) * mm, "end": v(-11.1, -23.61) * mm});
            skLineSegment(sketch, "E466", {"start": v(-11.1, -23.61) * mm, "end": v(-11.1, -23.56) * mm});
            skLineSegment(sketch, "E467", {"start": v(-11.1, -23.56) * mm, "end": v(-11.14, -23.3) * mm});
            skLineSegment(sketch, "E468", {"start": v(-11.14, -23.3) * mm, "end": v(-11.15, -23.1) * mm});
            skLineSegment(sketch, "E469", {"start": v(-11.15, -23.1) * mm, "end": v(-11.14, -22.9) * mm});
            skLineSegment(sketch, "E470", {"start": v(-11.14, -22.9) * mm, "end": v(-11.1, -22.7) * mm});
            skLineSegment(sketch, "E471", {"start": v(-11.1, -22.7) * mm, "end": v(-11.05, -22.5) * mm});
            skLineSegment(sketch, "E472", {"start": v(-11.05, -22.5) * mm, "end": v(-10.97, -22.3) * mm});
            skLineSegment(sketch, "E473", {"start": v(-10.97, -22.3) * mm, "end": v(-10.88, -22.12) * mm});
            skLineSegment(sketch, "E474", {"start": v(-10.88, -22.12) * mm, "end": v(-10.77, -21.95) * mm});
            skLineSegment(sketch, "E475", {"start": v(-10.77, -21.95) * mm, "end": v(-10.64, -21.78) * mm});
            skLineSegment(sketch, "E476", {"start": v(-10.64, -21.78) * mm, "end": v(-10.5, -21.64) * mm});
            skLineSegment(sketch, "E477", {"start": v(-10.5, -21.64) * mm, "end": v(-10.33, -21.51) * mm});
            skLineSegment(sketch, "E478", {"start": v(-10.33, -21.51) * mm, "end": v(-10.16, -21.4) * mm});
            skLineSegment(sketch, "E479", {"start": v(-10.16, -21.4) * mm, "end": v(-9.98, -21.3) * mm});
            skLineSegment(sketch, "E480", {"start": v(-9.98, -21.3) * mm, "end": v(-9.79, -21.23) * mm});
            skLineSegment(sketch, "E481", {"start": v(-9.79, -21.23) * mm, "end": v(-9.6, -21.17) * mm});
            skLineSegment(sketch, "E482", {"start": v(-9.6, -21.17) * mm, "end": v(-9.34, -21.13) * mm});
            skLineSegment(sketch, "E483", {"start": v(-9.34, -21.13) * mm, "end": v(-9.29, -21.11) * mm});
            skLineSegment(sketch, "E484", {"start": v(-9.29, -21.11) * mm, "end": v(-9.24, -21.1) * mm});
            skLineSegment(sketch, "E485", {"start": v(-9.24, -21.1) * mm, "end": v(-9.2, -21.07) * mm});
            skLineSegment(sketch, "E486", {"start": v(-9.2, -21.07) * mm, "end": v(-9.15, -21.04) * mm});
            skLineSegment(sketch, "E487", {"start": v(-9.15, -21.04) * mm, "end": v(-9.11, -21.01) * mm});
            skLineSegment(sketch, "E488", {"start": v(-9.11, -21.01) * mm, "end": v(-9.07, -20.97) * mm});
            skLineSegment(sketch, "E489", {"start": v(-9.07, -20.97) * mm, "end": v(-9.04, -20.93) * mm});
            skLineSegment(sketch, "E490", {"start": v(-9.04, -20.93) * mm, "end": v(-6.75, -17.8) * mm});
            skLineSegment(sketch, "E491", {"start": v(-6.75, -17.8) * mm, "end": v(-6.7, -17.7) * mm});
            skLineSegment(sketch, "E492", {"start": v(-6.7, -17.7) * mm, "end": v(-6.67, -17.6) * mm});
            skLineSegment(sketch, "E493", {"start": v(-6.67, -17.6) * mm, "end": v(-6.66, -17.52) * mm});
            skLineSegment(sketch, "E494", {"start": v(-6.66, -17.52) * mm, "end": v(-6.66, -17.02) * mm});
            skLineSegment(sketch, "E495", {"start": v(-6.66, -17.02) * mm, "end": v(-6.65, -16.9) * mm});
            skLineSegment(sketch, "E496", {"start": v(-6.65, -16.9) * mm, "end": v(-6.62, -16.8) * mm});
            skLineSegment(sketch, "E497", {"start": v(-6.62, -16.8) * mm, "end": v(-6.58, -16.72) * mm});
            skLineSegment(sketch, "E498", {"start": v(-6.58, -16.72) * mm, "end": v(-6.52, -16.65) * mm});
            skLineSegment(sketch, "E499", {"start": v(-6.52, -16.65) * mm, "end": v(-6.44, -16.59) * mm});
            skLineSegment(sketch, "E500", {"start": v(-6.44, -16.59) * mm, "end": v(-6.36, -16.54) * mm});
            skLineSegment(sketch, "E501", {"start": v(-6.36, -16.54) * mm, "end": v(-6.26, -16.51) * mm});
            skLineSegment(sketch, "E502", {"start": v(-6.26, -16.51) * mm, "end": v(-6.18, -16.5) * mm});
            skLineSegment(sketch, "E503", {"start": v(-6.18, -16.5) * mm, "end": v(-4.7, -16.5) * mm});
            skLineSegment(sketch, "E504", {"start": v(-4.7, -16.5) * mm, "end": v(-4.7, -16.5) * mm});
            skLineSegment(sketch, "E505", {"start": v(-4.7, -16.5) * mm, "end": v(-4.6, -16.51) * mm});
            skLineSegment(sketch, "E506", {"start": v(-4.6, -16.51) * mm, "end": v(-4.51, -16.54) * mm});
            skLineSegment(sketch, "E507", {"start": v(-4.51, -16.54) * mm, "end": v(-4.43, -16.59) * mm});
            skLineSegment(sketch, "E508", {"start": v(-4.43, -16.59) * mm, "end": v(-4.35, -16.65) * mm});
            skLineSegment(sketch, "E509", {"start": v(-4.35, -16.65) * mm, "end": v(-4.3, -16.72) * mm});
            skLineSegment(sketch, "E510", {"start": v(-4.3, -16.72) * mm, "end": v(-4.24, -16.8) * mm});
            skLineSegment(sketch, "E511", {"start": v(-4.24, -16.8) * mm, "end": v(-4.21, -16.9) * mm});
            skLineSegment(sketch, "E512", {"start": v(-4.21, -16.9) * mm, "end": v(-4.2, -17.05) * mm});
            skLineSegment(sketch, "E513", {"start": v(-4.2, -17.05) * mm, "end": v(-4.2, -17.37) * mm});
            skLineSegment(sketch, "E514", {"start": v(-4.2, -17.37) * mm, "end": v(-4.2, -17.5) * mm});
            skLineSegment(sketch, "E515", {"start": v(-4.2, -17.5) * mm, "end": v(-4.17, -17.59) * mm});
            skLineSegment(sketch, "E516", {"start": v(-4.17, -17.59) * mm, "end": v(-4.12, -17.67) * mm});
            skLineSegment(sketch, "E517", {"start": v(-4.12, -17.67) * mm, "end": v(-4.06, -17.75) * mm});
            skLineSegment(sketch, "E518", {"start": v(-4.06, -17.75) * mm, "end": v(-3.99, -17.8) * mm});
            skLineSegment(sketch, "E519", {"start": v(-3.99, -17.8) * mm, "end": v(-3.9, -17.85) * mm});
            skLineSegment(sketch, "E520", {"start": v(-3.9, -17.85) * mm, "end": v(-3.8, -17.88) * mm});
            skLineSegment(sketch, "E521", {"start": v(-3.8, -17.88) * mm, "end": v(-3.7, -17.9) * mm});
            skLineSegment(sketch, "E522", {"start": v(-3.7, -17.9) * mm, "end": v(3.71, -17.9) * mm});
            skLineSegment(sketch, "E523", {"start": v(3.71, -17.9) * mm, "end": v(3.81, -17.89) * mm});
            skLineSegment(sketch, "E524", {"start": v(3.81, -17.89) * mm, "end": v(3.9, -17.86) * mm});
            skLineSegment(sketch, "E525", {"start": v(3.9, -17.86) * mm, "end": v(4, -17.81) * mm});
            skLineSegment(sketch, "E526", {"start": v(4, -17.81) * mm, "end": v(4.06, -17.75) * mm});
            skLineSegment(sketch, "E527", {"start": v(4.06, -17.75) * mm, "end": v(4.13, -17.68) * mm});
            skLineSegment(sketch, "E528", {"start": v(4.13, -17.68) * mm, "end": v(4.17, -17.6) * mm});
            skLineSegment(sketch, "E529", {"start": v(4.17, -17.6) * mm, "end": v(4.2, -17.5) * mm});
            skLineSegment(sketch, "E530", {"start": v(4.2, -17.5) * mm, "end": v(4.21, -17.37) * mm});
            skLineSegment(sketch, "E531", {"start": v(4.21, -17.37) * mm, "end": v(4.21, -17) * mm});
            skLineSegment(sketch, "E532", {"start": v(4.21, -17) * mm, "end": v(4.22, -16.9) * mm});
            skLineSegment(sketch, "E533", {"start": v(4.22, -16.9) * mm, "end": v(4.25, -16.8) * mm});
            skLineSegment(sketch, "E534", {"start": v(4.25, -16.8) * mm, "end": v(4.3, -16.72) * mm});
            skLineSegment(sketch, "E535", {"start": v(4.3, -16.72) * mm, "end": v(4.36, -16.64) * mm});
            skLineSegment(sketch, "E536", {"start": v(4.36, -16.64) * mm, "end": v(4.43, -16.58) * mm});
            skLineSegment(sketch, "E537", {"start": v(4.43, -16.58) * mm, "end": v(4.52, -16.54) * mm});
            skLineSegment(sketch, "E538", {"start": v(4.52, -16.54) * mm, "end": v(4.6, -16.5) * mm});
            skLineSegment(sketch, "E539", {"start": v(4.6, -16.5) * mm, "end": v(4.71, -16.5) * mm});
            skLineSegment(sketch, "E540", {"start": v(4.71, -16.5) * mm, "end": v(4.71, -16.5) * mm});
            skLineSegment(sketch, "E541", {"start": v(4.71, -16.5) * mm, "end": v(6.16, -16.5) * mm});
            skLineSegment(sketch, "E542", {"start": v(6.16, -16.5) * mm, "end": v(6.16, -16.5) * mm});
            skLineSegment(sketch, "E543", {"start": v(6.16, -16.5) * mm, "end": v(6.26, -16.5) * mm});
            skLineSegment(sketch, "E544", {"start": v(6.26, -16.5) * mm, "end": v(6.35, -16.54) * mm});
            skLineSegment(sketch, "E545", {"start": v(6.35, -16.54) * mm, "end": v(6.44, -16.58) * mm});
            skLineSegment(sketch, "E546", {"start": v(6.44, -16.58) * mm, "end": v(6.51, -16.64) * mm});
            skLineSegment(sketch, "E547", {"start": v(6.51, -16.64) * mm, "end": v(6.57, -16.72) * mm});
            skLineSegment(sketch, "E548", {"start": v(6.57, -16.72) * mm, "end": v(6.62, -16.8) * mm});
            skLineSegment(sketch, "E549", {"start": v(6.62, -16.8) * mm, "end": v(6.65, -16.9) * mm});
            skLineSegment(sketch, "E550", {"start": v(6.65, -16.9) * mm, "end": v(6.66, -17) * mm});
            skLineSegment(sketch, "E551", {"start": v(6.66, -17) * mm, "end": v(6.66, -17) * mm});
            skLineSegment(sketch, "E552", {"start": v(6.66, -17) * mm, "end": v(6.66, -17.52) * mm});
            skLineSegment(sketch, "E553", {"start": v(6.66, -17.52) * mm, "end": v(6.67, -17.6) * mm});
            skLineSegment(sketch, "E554", {"start": v(6.67, -17.6) * mm, "end": v(6.7, -17.7) * mm});
            skLineSegment(sketch, "E555", {"start": v(6.7, -17.7) * mm, "end": v(6.75, -17.79) * mm});
            skLineSegment(sketch, "E556", {"start": v(6.75, -17.79) * mm, "end": v(6.76, -17.8) * mm});
            skLineSegment(sketch, "E557", {"start": v(6.76, -17.8) * mm, "end": v(9.04, -20.93) * mm});
            skLineSegment(sketch, "E558", {"start": v(9.04, -20.93) * mm, "end": v(9.07, -20.97) * mm});
            skLineSegment(sketch, "E559", {"start": v(9.07, -20.97) * mm, "end": v(9.1, -21) * mm});
            skLineSegment(sketch, "E560", {"start": v(9.1, -21) * mm, "end": v(9.15, -21.04) * mm});
            skLineSegment(sketch, "E561", {"start": v(9.15, -21.04) * mm, "end": v(9.2, -21.07) * mm});
            skLineSegment(sketch, "E562", {"start": v(9.2, -21.07) * mm, "end": v(9.24, -21.1) * mm});
            skLineSegment(sketch, "E563", {"start": v(9.24, -21.1) * mm, "end": v(9.29, -21.1) * mm});
            skLineSegment(sketch, "E564", {"start": v(9.29, -21.1) * mm, "end": v(9.33, -21.12) * mm});
            skLineSegment(sketch, "E565", {"start": v(9.33, -21.12) * mm, "end": v(9.59, -21.17) * mm});
            skLineSegment(sketch, "E566", {"start": v(9.59, -21.17) * mm, "end": v(9.79, -21.22) * mm});
            skLineSegment(sketch, "E567", {"start": v(9.79, -21.22) * mm, "end": v(9.98, -21.3) * mm});
            skLineSegment(sketch, "E568", {"start": v(9.98, -21.3) * mm, "end": v(10.16, -21.4) * mm});
            skLineSegment(sketch, "E569", {"start": v(10.16, -21.4) * mm, "end": v(10.33, -21.5) * mm});
            skLineSegment(sketch, "E570", {"start": v(10.33, -21.5) * mm, "end": v(10.49, -21.64) * mm});
            skLineSegment(sketch, "E571", {"start": v(10.49, -21.64) * mm, "end": v(10.63, -21.78) * mm});
            skLineSegment(sketch, "E572", {"start": v(10.63, -21.78) * mm, "end": v(10.77, -21.94) * mm});
            skLineSegment(sketch, "E573", {"start": v(10.77, -21.94) * mm, "end": v(10.88, -22.12) * mm});
            skLineSegment(sketch, "E574", {"start": v(10.88, -22.12) * mm, "end": v(10.97, -22.3) * mm});
            skLineSegment(sketch, "E575", {"start": v(10.97, -22.3) * mm, "end": v(11.05, -22.5) * mm});
            skLineSegment(sketch, "E576", {"start": v(11.05, -22.5) * mm, "end": v(11.1, -22.69) * mm});
            skLineSegment(sketch, "E577", {"start": v(11.1, -22.69) * mm, "end": v(11.13, -22.89) * mm});
            skLineSegment(sketch, "E578", {"start": v(11.13, -22.89) * mm, "end": v(11.15, -23.1) * mm});
            skLineSegment(sketch, "E579", {"start": v(11.15, -23.1) * mm, "end": v(11.14, -23.3) * mm});
            skLineSegment(sketch, "E580", {"start": v(11.14, -23.3) * mm, "end": v(11.1, -23.56) * mm});
            skLineSegment(sketch, "E581", {"start": v(11.1, -23.56) * mm, "end": v(11.1, -23.6) * mm});
            skLineSegment(sketch, "E582", {"start": v(11.1, -23.6) * mm, "end": v(11.1, -23.66) * mm});
            skLineSegment(sketch, "E583", {"start": v(11.1, -23.66) * mm, "end": v(11.11, -23.7) * mm});
            skLineSegment(sketch, "E584", {"start": v(11.11, -23.7) * mm, "end": v(11.13, -23.76) * mm});
            skLineSegment(sketch, "E585", {"start": v(11.13, -23.76) * mm, "end": v(11.14, -23.8) * mm});
            skLineSegment(sketch, "E586", {"start": v(11.14, -23.8) * mm, "end": v(11.17, -23.85) * mm});
            skLineSegment(sketch, "E587", {"start": v(11.17, -23.85) * mm, "end": v(11.2, -23.9) * mm});
            skLineSegment(sketch, "E588", {"start": v(11.2, -23.9) * mm, "end": v(11.94, -24.92) * mm});
            skLineSegment(sketch, "E589", {"start": v(11.94, -24.92) * mm, "end": v(15.61, -28.51) * mm});
            skLineSegment(sketch, "E590", {"start": v(15.61, -28.51) * mm, "end": v(15.75, -28.63) * mm});
            skLineSegment(sketch, "E591", {"start": v(15.75, -28.63) * mm, "end": v(15.9, -28.71) * mm});
            skLineSegment(sketch, "E592", {"start": v(15.9, -28.71) * mm, "end": v(16.07, -28.77) * mm});
            skLineSegment(sketch, "E593", {"start": v(16.07, -28.77) * mm, "end": v(16.24, -28.8) * mm});
            skLineSegment(sketch, "E594", {"start": v(16.24, -28.8) * mm, "end": v(16.41, -28.8) * mm});
            skLineSegment(sketch, "E595", {"start": v(16.41, -28.8) * mm, "end": v(16.58, -28.76) * mm});
            skLineSegment(sketch, "E596", {"start": v(16.58, -28.76) * mm, "end": v(16.75, -28.7) * mm});
            skLineSegment(sketch, "E597", {"start": v(16.75, -28.7) * mm, "end": v(16.9, -28.6) * mm});
            skLineSegment(sketch, "E598", {"start": v(16.9, -28.6) * mm, "end": v(19.74, -26.55) * mm});
            skLineSegment(sketch, "E599", {"start": v(19.74, -26.55) * mm, "end": v(19.88, -26.43) * mm});
            skLineSegment(sketch, "E600", {"start": v(19.88, -26.43) * mm, "end": v(19.99, -26.3) * mm});
            skLineSegment(sketch, "E601", {"start": v(19.99, -26.3) * mm, "end": v(20.07, -26.14) * mm});
            skLineSegment(sketch, "E602", {"start": v(20.07, -26.14) * mm, "end": v(20.12, -25.97) * mm});
            skLineSegment(sketch, "E603", {"start": v(20.12, -25.97) * mm, "end": v(20.15, -25.8) * mm});
            skLineSegment(sketch, "E604", {"start": v(20.15, -25.8) * mm, "end": v(20.15, -25.63) * mm});
            skLineSegment(sketch, "E605", {"start": v(20.15, -25.63) * mm, "end": v(20.11, -25.46) * mm});
            skLineSegment(sketch, "E606", {"start": v(20.11, -25.46) * mm, "end": v(20.05, -25.3) * mm});
            skLineSegment(sketch, "E607", {"start": v(20.05, -25.3) * mm, "end": v(17.76, -20.69) * mm});
            skLineSegment(sketch, "E608", {"start": v(17.76, -20.69) * mm, "end": v(17.02, -19.66) * mm});
            skLineSegment(sketch, "E609", {"start": v(17.02, -19.66) * mm, "end": v(16.99, -19.62) * mm});
            skLineSegment(sketch, "E610", {"start": v(16.99, -19.62) * mm, "end": v(16.95, -19.59) * mm});
            skLineSegment(sketch, "E611", {"start": v(16.95, -19.59) * mm, "end": v(16.91, -19.55) * mm});
            skLineSegment(sketch, "E612", {"start": v(16.91, -19.55) * mm, "end": v(16.87, -19.53) * mm});
            skLineSegment(sketch, "E613", {"start": v(16.87, -19.53) * mm, "end": v(16.82, -19.5) * mm});
            skLineSegment(sketch, "E614", {"start": v(16.82, -19.5) * mm, "end": v(16.78, -19.48) * mm});
            skLineSegment(sketch, "E615", {"start": v(16.78, -19.48) * mm, "end": v(16.73, -19.47) * mm});
            skLineSegment(sketch, "E616", {"start": v(16.73, -19.47) * mm, "end": v(16.47, -19.42) * mm});
            skLineSegment(sketch, "E617", {"start": v(16.47, -19.42) * mm, "end": v(16.27, -19.37) * mm});
            skLineSegment(sketch, "E618", {"start": v(16.27, -19.37) * mm, "end": v(16.08, -19.3) * mm});
            skLineSegment(sketch, "E619", {"start": v(16.08, -19.3) * mm, "end": v(15.9, -19.2) * mm});
            skLineSegment(sketch, "E620", {"start": v(15.9, -19.2) * mm, "end": v(15.73, -19.09) * mm});
            skLineSegment(sketch, "E621", {"start": v(15.73, -19.09) * mm, "end": v(15.57, -18.96) * mm});
            skLineSegment(sketch, "E622", {"start": v(15.57, -18.96) * mm, "end": v(15.43, -18.81) * mm});
            skLineSegment(sketch, "E623", {"start": v(15.43, -18.81) * mm, "end": v(15.3, -18.65) * mm});
            skLineSegment(sketch, "E624", {"start": v(15.3, -18.65) * mm, "end": v(15.18, -18.48) * mm});
            skLineSegment(sketch, "E625", {"start": v(15.18, -18.48) * mm, "end": v(15.09, -18.3) * mm});
            skLineSegment(sketch, "E626", {"start": v(15.09, -18.3) * mm, "end": v(15.01, -18.1) * mm});
            skLineSegment(sketch, "E627", {"start": v(15.01, -18.1) * mm, "end": v(14.96, -17.9) * mm});
            skLineSegment(sketch, "E628", {"start": v(14.96, -17.9) * mm, "end": v(14.93, -17.7) * mm});
            skLineSegment(sketch, "E629", {"start": v(14.93, -17.7) * mm, "end": v(14.91, -17.5) * mm});
            skLineSegment(sketch, "E630", {"start": v(14.91, -17.5) * mm, "end": v(14.92, -17.3) * mm});
            skLineSegment(sketch, "E631", {"start": v(14.92, -17.3) * mm, "end": v(14.96, -17.04) * mm});
            skLineSegment(sketch, "E632", {"start": v(14.96, -17.04) * mm, "end": v(14.96, -16.98) * mm});
            skLineSegment(sketch, "E633", {"start": v(14.96, -16.98) * mm, "end": v(14.96, -16.93) * mm});
            skLineSegment(sketch, "E634", {"start": v(14.96, -16.93) * mm, "end": v(14.95, -16.88) * mm});
            skLineSegment(sketch, "E635", {"start": v(14.95, -16.88) * mm, "end": v(14.94, -16.83) * mm});
            skLineSegment(sketch, "E636", {"start": v(14.94, -16.83) * mm, "end": v(14.92, -16.79) * mm});
            skLineSegment(sketch, "E637", {"start": v(14.92, -16.79) * mm, "end": v(14.9, -16.74) * mm});
            skLineSegment(sketch, "E638", {"start": v(14.9, -16.74) * mm, "end": v(14.87, -16.7) * mm});
            skLineSegment(sketch, "E639", {"start": v(14.87, -16.7) * mm, "end": v(11.63, -12.24) * mm});
            skLineSegment(sketch, "E640", {"start": v(11.63, -12.24) * mm, "end": v(11.6, -12.2) * mm});
            skLineSegment(sketch, "E641", {"start": v(11.6, -12.2) * mm, "end": v(11.6, -12.16) * mm});
            skLineSegment(sketch, "E642", {"start": v(11.6, -12.16) * mm, "end": v(11.58, -12.13) * mm});
            skLineSegment(sketch, "E643", {"start": v(11.58, -12.13) * mm, "end": v(11.57, -12.1) * mm});
            skLineSegment(sketch, "E644", {"start": v(11.57, -12.1) * mm, "end": v(11.57, -12.06) * mm});
            skLineSegment(sketch, "E645", {"start": v(11.57, -12.06) * mm, "end": v(11.57, -12.04) * mm});
            skLineSegment(sketch, "E646", {"start": v(11.57, -12.04) * mm, "end": v(11.57, -12) * mm});
            skLineSegment(sketch, "E647", {"start": v(11.57, -12) * mm, "end": v(11.57, -11.96) * mm});
            skLineSegment(sketch, "E648", {"start": v(11.57, -11.96) * mm, "end": v(11.58, -11.93) * mm});
            skLineSegment(sketch, "E649", {"start": v(11.58, -11.93) * mm, "end": v(11.6, -11.9) * mm});
            skLineSegment(sketch, "E650", {"start": v(11.6, -11.9) * mm, "end": v(11.6, -11.87) * mm});
            skLineSegment(sketch, "E651", {"start": v(11.6, -11.87) * mm, "end": v(11.63, -11.84) * mm});
            skLineSegment(sketch, "E652", {"start": v(11.63, -11.84) * mm, "end": v(11.65, -11.81) * mm});
            skLineSegment(sketch, "E653", {"start": v(11.65, -11.81) * mm, "end": v(11.67, -11.78) * mm});
            skLineSegment(sketch, "E654", {"start": v(11.67, -11.78) * mm, "end": v(12.41, -10.79) * mm});
            skLineSegment(sketch, "E655", {"start": v(12.41, -10.79) * mm, "end": v(13.07, -9.73) * mm});
            skLineSegment(sketch, "E656", {"start": v(13.07, -9.73) * mm, "end": v(13.64, -8.61) * mm});
            skLineSegment(sketch, "E657", {"start": v(13.64, -8.61) * mm, "end": v(14.12, -7.45) * mm});
            skLineSegment(sketch, "E658", {"start": v(14.12, -7.45) * mm, "end": v(14.5, -6.23) * mm});
            skLineSegment(sketch, "E659", {"start": v(14.5, -6.23) * mm, "end": v(14.77, -4.98) * mm});
            skLineSegment(sketch, "E660", {"start": v(14.77, -4.98) * mm, "end": v(14.94, -3.69) * mm});
            skLineSegment(sketch, "E661", {"start": v(14.94, -3.69) * mm, "end": v(15, -2.36) * mm});
            skLineSegment(sketch, "E662", {"start": v(15, -2.36) * mm, "end": v(15, -2) * mm});
            skLineSegment(sketch, "E663", {"start": v(15, -2) * mm, "end": v(14.98, -1.58) * mm});
            skLineSegment(sketch, "E664", {"start": v(14.98, -1.58) * mm, "end": v(14.98, -1.55) * mm});
            skLineSegment(sketch, "E665", {"start": v(14.98, -1.55) * mm, "end": v(14.98, -1.5) * mm});
            skLineSegment(sketch, "E666", {"start": v(14.98, -1.5) * mm, "end": v(14.99, -1.47) * mm});
            skLineSegment(sketch, "E667", {"start": v(14.99, -1.47) * mm, "end": v(15, -1.43) * mm});
            skLineSegment(sketch, "E668", {"start": v(15, -1.43) * mm, "end": v(15, -1.4) * mm});
            skLineSegment(sketch, "E669", {"start": v(15, -1.4) * mm, "end": v(15.02, -1.36) * mm});
            skLineSegment(sketch, "E670", {"start": v(15.02, -1.36) * mm, "end": v(15.04, -1.33) * mm});
            skLineSegment(sketch, "E671", {"start": v(15.04, -1.33) * mm, "end": v(15.06, -1.3) * mm});
            skLineSegment(sketch, "E672", {"start": v(15.06, -1.3) * mm, "end": v(15.1, -1.28) * mm});
            skLineSegment(sketch, "E673", {"start": v(15.1, -1.28) * mm, "end": v(15.12, -1.26) * mm});
            skLineSegment(sketch, "E674", {"start": v(15.12, -1.26) * mm, "end": v(15.15, -1.24) * mm});
            skLineSegment(sketch, "E675", {"start": v(15.15, -1.24) * mm, "end": v(15.18, -1.22) * mm});
            skLineSegment(sketch, "E676", {"start": v(15.18, -1.22) * mm, "end": v(15.2, -1.21) * mm});
            skLineSegment(sketch, "E677", {"start": v(15.2, -1.21) * mm, "end": v(15.23, -1.2) * mm});
            skLineSegment(sketch, "E678", {"start": v(15.23, -1.2) * mm, "end": v(20.45, 0.5) * mm});
            skLineSegment(sketch, "E679", {"start": v(20.45, 0.5) * mm, "end": v(20.5, 0.52) * mm});
            skLineSegment(sketch, "E680", {"start": v(20.5, 0.52) * mm, "end": v(20.54, 0.54) * mm});
            skLineSegment(sketch, "E681", {"start": v(20.54, 0.54) * mm, "end": v(20.59, 0.57) * mm});
            skLineSegment(sketch, "E682", {"start": v(20.59, 0.57) * mm, "end": v(20.63, 0.6) * mm});
            skLineSegment(sketch, "E683", {"start": v(20.63, 0.6) * mm, "end": v(20.66, 0.63) * mm});
            skLineSegment(sketch, "E684", {"start": v(20.66, 0.63) * mm, "end": v(20.7, 0.67) * mm});
            skLineSegment(sketch, "E685", {"start": v(20.7, 0.67) * mm, "end": v(20.73, 0.72) * mm});
            skLineSegment(sketch, "E686", {"start": v(20.73, 0.72) * mm, "end": v(20.85, 0.95) * mm});
            skLineSegment(sketch, "E687", {"start": v(20.85, 0.95) * mm, "end": v(20.96, 1.12) * mm});
            skLineSegment(sketch, "E688", {"start": v(20.96, 1.12) * mm, "end": v(21.1, 1.27) * mm});
            skLineSegment(sketch, "E689", {"start": v(21.1, 1.27) * mm, "end": v(21.24, 1.42) * mm});
            skLineSegment(sketch, "E690", {"start": v(21.24, 1.42) * mm, "end": v(21.4, 1.55) * mm});
            skLineSegment(sketch, "E691", {"start": v(21.4, 1.55) * mm, "end": v(21.57, 1.66) * mm});
            skLineSegment(sketch, "E692", {"start": v(21.57, 1.66) * mm, "end": v(21.75, 1.75) * mm});
            skLineSegment(sketch, "E693", {"start": v(21.75, 1.75) * mm, "end": v(21.95, 1.82) * mm});
            skLineSegment(sketch, "E694", {"start": v(21.95, 1.82) * mm, "end": v(22.15, 1.88) * mm});
            skLineSegment(sketch, "E695", {"start": v(22.15, 1.88) * mm, "end": v(22.35, 1.91) * mm});
            skLineSegment(sketch, "E696", {"start": v(22.35, 1.91) * mm, "end": v(22.55, 1.92) * mm});
            skLineSegment(sketch, "E697", {"start": v(22.55, 1.92) * mm, "end": v(22.76, 1.91) * mm});
            skLineSegment(sketch, "E698", {"start": v(22.76, 1.91) * mm, "end": v(22.96, 1.88) * mm});
            skLineSegment(sketch, "E699", {"start": v(22.96, 1.88) * mm, "end": v(23.16, 1.83) * mm});
            skLineSegment(sketch, "E700", {"start": v(23.16, 1.83) * mm, "end": v(23.35, 1.76) * mm});
            skLineSegment(sketch, "E701", {"start": v(23.35, 1.76) * mm, "end": v(23.59, 1.65) * mm});
            skLineSegment(sketch, "E702", {"start": v(23.59, 1.65) * mm, "end": v(23.63, 1.63) * mm});
            skLineSegment(sketch, "E703", {"start": v(23.63, 1.63) * mm, "end": v(23.68, 1.61) * mm});
            skLineSegment(sketch, "E704", {"start": v(23.68, 1.61) * mm, "end": v(23.73, 1.6) * mm});
            skLineSegment(sketch, "E705", {"start": v(23.73, 1.6) * mm, "end": v(23.79, 1.6) * mm});
            skLineSegment(sketch, "E706", {"start": v(23.79, 1.6) * mm, "end": v(23.84, 1.6) * mm});
            skLineSegment(sketch, "E707", {"start": v(23.84, 1.6) * mm, "end": v(23.89, 1.62) * mm});
            skLineSegment(sketch, "E708", {"start": v(23.89, 1.62) * mm, "end": v(23.94, 1.63) * mm});
            skLineSegment(sketch, "E709", {"start": v(23.94, 1.63) * mm, "end": v(25.14, 2.02) * mm});
            skLineSegment(sketch, "E710", {"start": v(25.14, 2.02) * mm, "end": v(29.7, 4.4) * mm});
            skLineSegment(sketch, "E711", {"start": v(29.7, 4.4) * mm, "end": v(29.85, 4.5) * mm});
            skLineSegment(sketch, "E712", {"start": v(29.85, 4.5) * mm, "end": v(29.98, 4.62) * mm});
            skLineSegment(sketch, "E713", {"start": v(29.98, 4.62) * mm, "end": v(30.08, 4.76) * mm});
            skLineSegment(sketch, "E714", {"start": v(30.08, 4.76) * mm, "end": v(30.16, 4.91) * mm});
            skLineSegment(sketch, "E715", {"start": v(30.16, 4.91) * mm, "end": v(30.2, 5.08) * mm});
            skLineSegment(sketch, "E716", {"start": v(30.2, 5.08) * mm, "end": v(30.23, 5.25) * mm});
            skLineSegment(sketch, "E717", {"start": v(30.23, 5.25) * mm, "end": v(30.22, 5.42) * mm});
            skLineSegment(sketch, "E718", {"start": v(-6.23, -2.28) * mm, "end": v(-6.23, -1.51) * mm});
            skArc(sketch, "E719", {"start": v(-6.23, -1.51) * mm, "mid": v(-6.26, -1.45) * mm, "end": v(-6.31, -1.43) * mm});
            skLineSegment(sketch, "E720", {"start": v(-6.31, -1.43) * mm, "end": v(-7.19, -1.43) * mm});
            skArc(sketch, "E721", {"start": v(-7.19, -1.43) * mm, "mid": v(-7.24, -1.45) * mm, "end": v(-7.27, -1.51) * mm});
            skLineSegment(sketch, "E722", {"start": v(-7.27, -1.51) * mm, "end": v(-7.27, -2.28) * mm});
            skArc(sketch, "E723", {"start": v(-7.27, -2.28) * mm, "mid": v(-7.24, -2.34) * mm, "end": v(-7.19, -2.37) * mm});
            skLineSegment(sketch, "E724", {"start": v(-7.19, -2.37) * mm, "end": v(-6.31, -2.37) * mm});
            skArc(sketch, "E725", {"start": v(-6.31, -2.37) * mm, "mid": v(-6.26, -2.34) * mm, "end": v(-6.23, -2.28) * mm});
            skLineSegment(sketch, "E726", {"start": v(-4.53, -2.28) * mm, "end": v(-4.53, -1.51) * mm});
            skArc(sketch, "E727", {"start": v(-4.53, -1.51) * mm, "mid": v(-4.56, -1.45) * mm, "end": v(-4.61, -1.43) * mm});
            skLineSegment(sketch, "E728", {"start": v(-4.61, -1.43) * mm, "end": v(-5.49, -1.43) * mm});
            skArc(sketch, "E729", {"start": v(-5.49, -1.43) * mm, "mid": v(-5.54, -1.45) * mm, "end": v(-5.57, -1.51) * mm});
            skLineSegment(sketch, "E730", {"start": v(-5.57, -1.51) * mm, "end": v(-5.57, -2.28) * mm});
            skArc(sketch, "E731", {"start": v(-5.57, -2.28) * mm, "mid": v(-5.54, -2.34) * mm, "end": v(-5.49, -2.37) * mm});
            skLineSegment(sketch, "E732", {"start": v(-5.49, -2.37) * mm, "end": v(-4.61, -2.37) * mm});
            skArc(sketch, "E733", {"start": v(-4.61, -2.37) * mm, "mid": v(-4.56, -2.34) * mm, "end": v(-4.53, -2.28) * mm});
            skLineSegment(sketch, "E734", {"start": v(-6.27, 1.37) * mm, "end": v(-6.27, 2.14) * mm});
            skArc(sketch, "E735", {"start": v(-6.27, 2.14) * mm, "mid": v(-6.3, 2.2) * mm, "end": v(-6.35, 2.22) * mm});
            skLineSegment(sketch, "E736", {"start": v(-6.35, 2.22) * mm, "end": v(-7.23, 2.22) * mm});
            skArc(sketch, "E737", {"start": v(-7.23, 2.22) * mm, "mid": v(-7.28, 2.2) * mm, "end": v(-7.3, 2.14) * mm});
            skLineSegment(sketch, "E738", {"start": v(-7.3, 2.14) * mm, "end": v(-7.3, 1.37) * mm});
            skArc(sketch, "E739", {"start": v(-7.3, 1.37) * mm, "mid": v(-7.28, 1.3) * mm, "end": v(-7.23, 1.28) * mm});
            skLineSegment(sketch, "E740", {"start": v(-7.23, 1.28) * mm, "end": v(-6.35, 1.28) * mm});
            skArc(sketch, "E741", {"start": v(-6.35, 1.28) * mm, "mid": v(-6.3, 1.3) * mm, "end": v(-6.27, 1.37) * mm});
            skLineSegment(sketch, "E742", {"start": v(-4.57, 1.37) * mm, "end": v(-4.57, 2.14) * mm});
            skArc(sketch, "E743", {"start": v(-4.57, 2.14) * mm, "mid": v(-4.6, 2.2) * mm, "end": v(-4.65, 2.22) * mm});
            skLineSegment(sketch, "E744", {"start": v(-4.65, 2.22) * mm, "end": v(-5.53, 2.22) * mm});
            skArc(sketch, "E745", {"start": v(-5.53, 2.22) * mm, "mid": v(-5.58, 2.2) * mm, "end": v(-5.6, 2.14) * mm});
            skLineSegment(sketch, "E746", {"start": v(-5.6, 2.14) * mm, "end": v(-5.6, 1.37) * mm});
            skArc(sketch, "E747", {"start": v(-5.6, 1.37) * mm, "mid": v(-5.58, 1.3) * mm, "end": v(-5.53, 1.28) * mm});
            skLineSegment(sketch, "E748", {"start": v(-5.53, 1.28) * mm, "end": v(-4.65, 1.28) * mm});
            skArc(sketch, "E749", {"start": v(-4.65, 1.28) * mm, "mid": v(-4.6, 1.3) * mm, "end": v(-4.57, 1.37) * mm});
            skLineSegment(sketch, "E750", {"start": v(8.02, -5.3) * mm, "end": v(8.02, -6.07) * mm});
            skArc(sketch, "E751", {"start": v(8.02, -6.07) * mm, "mid": v(8.05, -6.13) * mm, "end": v(8.1, -6.16) * mm});
            skLineSegment(sketch, "E752", {"start": v(8.1, -6.16) * mm, "end": v(8.98, -6.16) * mm});
            skArc(sketch, "E753", {"start": v(8.98, -6.16) * mm, "mid": v(9.03, -6.13) * mm, "end": v(9.06, -6.07) * mm});
            skLineSegment(sketch, "E754", {"start": v(9.06, -6.07) * mm, "end": v(9.06, -5.3) * mm});
            skArc(sketch, "E755", {"start": v(9.06, -5.3) * mm, "mid": v(9.03, -5.24) * mm, "end": v(8.98, -5.22) * mm});
            skLineSegment(sketch, "E756", {"start": v(8.98, -5.22) * mm, "end": v(8.1, -5.22) * mm});
            skArc(sketch, "E757", {"start": v(8.1, -5.22) * mm, "mid": v(8.05, -5.24) * mm, "end": v(8.02, -5.3) * mm});
            skLineSegment(sketch, "E758", {"start": v(6.32, -5.3) * mm, "end": v(6.32, -6.07) * mm});
            skArc(sketch, "E759", {"start": v(6.32, -6.07) * mm, "mid": v(6.35, -6.13) * mm, "end": v(6.4, -6.16) * mm});
            skLineSegment(sketch, "E760", {"start": v(6.4, -6.16) * mm, "end": v(7.28, -6.16) * mm});
            skArc(sketch, "E761", {"start": v(7.28, -6.16) * mm, "mid": v(7.33, -6.13) * mm, "end": v(7.36, -6.07) * mm});
            skLineSegment(sketch, "E762", {"start": v(7.36, -6.07) * mm, "end": v(7.36, -5.3) * mm});
            skArc(sketch, "E763", {"start": v(7.36, -5.3) * mm, "mid": v(7.33, -5.24) * mm, "end": v(7.28, -5.22) * mm});
            skLineSegment(sketch, "E764", {"start": v(7.28, -5.22) * mm, "end": v(6.4, -5.22) * mm});
            skArc(sketch, "E765", {"start": v(6.4, -5.22) * mm, "mid": v(6.35, -5.24) * mm, "end": v(6.32, -5.3) * mm});
            skLineSegment(sketch, "E766", {"start": v(-2.19, -9.57) * mm, "end": v(-1.41, -9.57) * mm});
            skArc(sketch, "E767", {"start": v(-1.41, -9.57) * mm, "mid": v(-1.36, -9.54) * mm, "end": v(-1.33, -9.48) * mm});
            skLineSegment(sketch, "E768", {"start": v(-1.33, -9.48) * mm, "end": v(-1.33, -8.61) * mm});
            skArc(sketch, "E769", {"start": v(-1.33, -8.61) * mm, "mid": v(-1.36, -8.55) * mm, "end": v(-1.41, -8.53) * mm});
            skLineSegment(sketch, "E770", {"start": v(-1.41, -8.53) * mm, "end": v(-2.19, -8.53) * mm});
            skArc(sketch, "E771", {"start": v(-2.19, -8.53) * mm, "mid": v(-2.24, -8.55) * mm, "end": v(-2.27, -8.61) * mm});
            skLineSegment(sketch, "E772", {"start": v(-2.27, -8.61) * mm, "end": v(-2.27, -9.48) * mm});
            skArc(sketch, "E773", {"start": v(-2.27, -9.48) * mm, "mid": v(-2.24, -9.54) * mm, "end": v(-2.19, -9.57) * mm});
            skLineSegment(sketch, "E774", {"start": v(-2.19, -11.27) * mm, "end": v(-1.41, -11.27) * mm});
            skArc(sketch, "E775", {"start": v(-1.41, -11.27) * mm, "mid": v(-1.36, -11.24) * mm, "end": v(-1.33, -11.18) * mm});
            skLineSegment(sketch, "E776", {"start": v(-1.33, -11.18) * mm, "end": v(-1.33, -10.31) * mm});
            skArc(sketch, "E777", {"start": v(-1.33, -10.31) * mm, "mid": v(-1.36, -10.25) * mm, "end": v(-1.41, -10.23) * mm});
            skLineSegment(sketch, "E778", {"start": v(-1.41, -10.23) * mm, "end": v(-2.19, -10.23) * mm});
            skArc(sketch, "E779", {"start": v(-2.19, -10.23) * mm, "mid": v(-2.24, -10.25) * mm, "end": v(-2.27, -10.31) * mm});
            skLineSegment(sketch, "E780", {"start": v(-2.27, -10.31) * mm, "end": v(-2.27, -11.18) * mm});
            skArc(sketch, "E781", {"start": v(-2.27, -11.18) * mm, "mid": v(-2.24, -11.24) * mm, "end": v(-2.19, -11.27) * mm});
            skLineSegment(sketch, "E782", {"start": v(-0.37, -9.59) * mm, "end": v(0.4, -9.59) * mm});
            skArc(sketch, "E783", {"start": v(0.4, -9.59) * mm, "mid": v(0.46, -9.56) * mm, "end": v(0.49, -9.5) * mm});
            skLineSegment(sketch, "E784", {"start": v(0.49, -9.5) * mm, "end": v(0.49, -8.63) * mm});
            skArc(sketch, "E785", {"start": v(0.49, -8.63) * mm, "mid": v(0.46, -8.57) * mm, "end": v(0.4, -8.55) * mm});
            skLineSegment(sketch, "E786", {"start": v(0.4, -8.55) * mm, "end": v(-0.37, -8.55) * mm});
            skArc(sketch, "E787", {"start": v(-0.37, -8.55) * mm, "mid": v(-0.42, -8.57) * mm, "end": v(-0.45, -8.63) * mm});
            skLineSegment(sketch, "E788", {"start": v(-0.45, -8.63) * mm, "end": v(-0.45, -9.5) * mm});
            skArc(sketch, "E789", {"start": v(-0.45, -9.5) * mm, "mid": v(-0.42, -9.56) * mm, "end": v(-0.37, -9.59) * mm});
            skLineSegment(sketch, "E790", {"start": v(-0.37, -11.29) * mm, "end": v(0.4, -11.29) * mm});
            skArc(sketch, "E791", {"start": v(0.4, -11.29) * mm, "mid": v(0.46, -11.26) * mm, "end": v(0.49, -11.2) * mm});
            skLineSegment(sketch, "E792", {"start": v(0.49, -11.2) * mm, "end": v(0.49, -10.33) * mm});
            skArc(sketch, "E793", {"start": v(0.49, -10.33) * mm, "mid": v(0.46, -10.27) * mm, "end": v(0.4, -10.25) * mm});
            skLineSegment(sketch, "E794", {"start": v(0.4, -10.25) * mm, "end": v(-0.37, -10.25) * mm});
            skArc(sketch, "E795", {"start": v(-0.37, -10.25) * mm, "mid": v(-0.42, -10.27) * mm, "end": v(-0.45, -10.33) * mm});
            skLineSegment(sketch, "E796", {"start": v(-0.45, -10.33) * mm, "end": v(-0.45, -11.2) * mm});
            skArc(sketch, "E797", {"start": v(-0.45, -11.2) * mm, "mid": v(-0.42, -11.26) * mm, "end": v(-0.37, -11.29) * mm});
            skLineSegment(sketch, "E798", {"start": v(-2.25, 18.36) * mm, "end": v(-2.23, 14.76) * mm});
            skArc(sketch, "E799", {"start": v(-2.36, 14.76) * mm, "mid": v(-2.23, 14.63) * mm, "end": v(-2.1, 14.76) * mm});
            skArc(sketch, "E800", {"start": v(-2.12, 18.36) * mm, "mid": v(-2.25, 18.48) * mm, "end": v(-2.37, 18.36) * mm});
            skLineSegment(sketch, "E801", {"start": v(-2.23, 14.76) * mm, "end": v(-2.2, 14.53) * mm});
            skArc(sketch, "E802", {"start": v(-2.32, 14.51) * mm, "mid": v(-2.18, 14.4) * mm, "end": v(-2.07, 14.55) * mm});
            skArc(sketch, "E803", {"start": v(-2.1, 14.78) * mm, "mid": v(-2.25, 14.88) * mm, "end": v(-2.36, 14.74) * mm});
            skLineSegment(sketch, "E804", {"start": v(-2.2, 14.53) * mm, "end": v(-2.14, 14.32) * mm});
            skArc(sketch, "E805", {"start": v(-2.26, 14.29) * mm, "mid": v(-2.11, 14.2) * mm, "end": v(-2.02, 14.35) * mm});
            skArc(sketch, "E806", {"start": v(-2.08, 14.56) * mm, "mid": v(-2.23, 14.65) * mm, "end": v(-2.32, 14.5) * mm});
            skLineSegment(sketch, "E807", {"start": v(-2.14, 14.32) * mm, "end": v(-2.06, 14.11) * mm});
            skArc(sketch, "E808", {"start": v(-2.18, 14.07) * mm, "mid": v(-2.02, 14) * mm, "end": v(-1.95, 14.16) * mm});
            skArc(sketch, "E809", {"start": v(-2.02, 14.36) * mm, "mid": v(-2.19, 14.43) * mm, "end": v(-2.26, 14.27) * mm});
            skLineSegment(sketch, "E810", {"start": v(-2.06, 14.11) * mm, "end": v(-1.97, 13.92) * mm});
            skArc(sketch, "E811", {"start": v(-2.08, 13.86) * mm, "mid": v(-1.91, 13.8) * mm, "end": v(-1.86, 13.97) * mm});
            skArc(sketch, "E812", {"start": v(-1.95, 14.17) * mm, "mid": v(-2.12, 14.22) * mm, "end": v(-2.18, 14.06) * mm});
            skLineSegment(sketch, "E813", {"start": v(-1.97, 13.92) * mm, "end": v(-1.86, 13.73) * mm});
            skArc(sketch, "E814", {"start": v(-1.96, 13.67) * mm, "mid": v(-1.8, 13.62) * mm, "end": v(-1.75, 13.8) * mm});
            skArc(sketch, "E815", {"start": v(-1.86, 13.98) * mm, "mid": v(-2.03, 14.02) * mm, "end": v(-2.08, 13.85) * mm});
            skLineSegment(sketch, "E816", {"start": v(-1.86, 13.73) * mm, "end": v(-1.72, 13.56) * mm});
            skArc(sketch, "E817", {"start": v(-1.82, 13.48) * mm, "mid": v(-1.65, 13.46) * mm, "end": v(-1.63, 13.63) * mm});
            skArc(sketch, "E818", {"start": v(-1.76, 13.8) * mm, "mid": v(-1.93, 13.83) * mm, "end": v(-1.96, 13.66) * mm});
            skLineSegment(sketch, "E819", {"start": v(-1.72, 13.56) * mm, "end": v(-1.58, 13.4) * mm});
            skArc(sketch, "E820", {"start": v(-1.67, 13.31) * mm, "mid": v(-1.5, 13.3) * mm, "end": v(-1.49, 13.48) * mm});
            skArc(sketch, "E821", {"start": v(-1.63, 13.64) * mm, "mid": v(-1.8, 13.65) * mm, "end": v(-1.82, 13.47) * mm});
            skLineSegment(sketch, "E822", {"start": v(-1.58, 13.4) * mm, "end": v(-1.42, 13.25) * mm});
            skArc(sketch, "E823", {"start": v(-1.5, 13.16) * mm, "mid": v(-1.33, 13.17) * mm, "end": v(-1.33, 13.35) * mm});
            skArc(sketch, "E824", {"start": v(-1.5, 13.5) * mm, "mid": v(-1.67, 13.48) * mm, "end": v(-1.66, 13.3) * mm});
            skLineSegment(sketch, "E825", {"start": v(-1.42, 13.25) * mm, "end": v(-1.24, 13.13) * mm});
            skArc(sketch, "E826", {"start": v(-1.32, 13.03) * mm, "mid": v(-1.14, 13.05) * mm, "end": v(-1.17, 13.23) * mm});
            skArc(sketch, "E827", {"start": v(-1.34, 13.36) * mm, "mid": v(-1.52, 13.33) * mm, "end": v(-1.5, 13.15) * mm});
            skLineSegment(sketch, "E828", {"start": v(-1.24, 13.13) * mm, "end": v(-1.06, 13.01) * mm});
            skArc(sketch, "E829", {"start": v(-1.12, 12.9) * mm, "mid": v(-0.95, 12.95) * mm, "end": v(-1, 13.12) * mm});
            skArc(sketch, "E830", {"start": v(-1.18, 13.23) * mm, "mid": v(-1.35, 13.2) * mm, "end": v(-1.3, 13.02) * mm});
            skLineSegment(sketch, "E831", {"start": v(-1.06, 13.01) * mm, "end": v(-0.86, 12.92) * mm});
            skArc(sketch, "E832", {"start": v(-0.91, 12.8) * mm, "mid": v(-0.75, 12.87) * mm, "end": v(-0.8, 13.03) * mm});
            skArc(sketch, "E833", {"start": v(-1, 13.13) * mm, "mid": v(-1.17, 13.07) * mm, "end": v(-1.11, 12.9) * mm});
            skLineSegment(sketch, "E834", {"start": v(-0.86, 12.92) * mm, "end": v(-0.65, 12.85) * mm});
            skArc(sketch, "E835", {"start": v(-0.7, 12.73) * mm, "mid": v(-0.54, 12.8) * mm, "end": v(-0.61, 12.96) * mm});
            skArc(sketch, "E836", {"start": v(-0.82, 13.04) * mm, "mid": v(-0.98, 12.96) * mm, "end": v(-0.9, 12.8) * mm});
            skLineSegment(sketch, "E837", {"start": v(-0.65, 12.85) * mm, "end": v(-0.44, 12.8) * mm});
            skArc(sketch, "E838", {"start": v(-0.47, 12.67) * mm, "mid": v(-0.32, 12.76) * mm, "end": v(-0.4, 12.91) * mm});
            skArc(sketch, "E839", {"start": v(-0.62, 12.97) * mm, "mid": v(-0.77, 12.88) * mm, "end": v(-0.68, 12.72) * mm});
            skLineSegment(sketch, "E840", {"start": v(-0.44, 12.8) * mm, "end": v(-0.21, 12.76) * mm});
            skArc(sketch, "E841", {"start": v(-0.23, 12.64) * mm, "mid": v(-0.1, 12.74) * mm, "end": v(-0.2, 12.88) * mm});
            skArc(sketch, "E842", {"start": v(-0.42, 12.92) * mm, "mid": v(-0.56, 12.8) * mm, "end": v(-0.46, 12.67) * mm});
            skLineSegment(sketch, "E843", {"start": v(-0.21, 12.76) * mm, "end": v(0, 12.75) * mm});
            skArc(sketch, "E844", {"start": v(0, 12.62) * mm, "mid": v(0.13, 12.74) * mm, "end": v(0, 12.87) * mm});
            skArc(sketch, "E845", {"start": v(-0.2, 12.88) * mm, "mid": v(-0.34, 12.76) * mm, "end": v(-0.22, 12.63) * mm});
            skLineSegment(sketch, "E846", {"start": v(0, 12.75) * mm, "end": v(0.25, 12.76) * mm});
            skArc(sketch, "E847", {"start": v(0.25, 12.64) * mm, "mid": v(0.37, 12.77) * mm, "end": v(0.24, 12.89) * mm});
            skArc(sketch, "E848", {"start": v(0, 12.87) * mm, "mid": v(-0.12, 12.74) * mm, "end": v(0, 12.62) * mm});
            skLineSegment(sketch, "E849", {"start": v(0.25, 12.76) * mm, "end": v(0.47, 12.8) * mm});
            skArc(sketch, "E850", {"start": v(0.49, 12.67) * mm, "mid": v(0.6, 12.82) * mm, "end": v(0.45, 12.92) * mm});
            skArc(sketch, "E851", {"start": v(0.23, 12.88) * mm, "mid": v(0.12, 12.74) * mm, "end": v(0.27, 12.64) * mm});
            skLineSegment(sketch, "E852", {"start": v(0.47, 12.8) * mm, "end": v(0.69, 12.85) * mm});
            skArc(sketch, "E853", {"start": v(0.72, 12.73) * mm, "mid": v(0.8, 12.88) * mm, "end": v(0.65, 12.97) * mm});
            skArc(sketch, "E854", {"start": v(0.44, 12.92) * mm, "mid": v(0.35, 12.76) * mm, "end": v(0.5, 12.68) * mm});
            skLineSegment(sketch, "E855", {"start": v(0.69, 12.85) * mm, "end": v(0.9, 12.93) * mm});
            skArc(sketch, "E856", {"start": v(0.93, 12.81) * mm, "mid": v(1, 12.97) * mm, "end": v(0.85, 13.05) * mm});
            skArc(sketch, "E857", {"start": v(0.64, 12.97) * mm, "mid": v(0.57, 12.8) * mm, "end": v(0.73, 12.74) * mm});
            skLineSegment(sketch, "E858", {"start": v(0.9, 12.93) * mm, "end": v(1.09, 13.03) * mm});
            skArc(sketch, "E859", {"start": v(1.14, 12.91) * mm, "mid": v(1.2, 13.08) * mm, "end": v(1.03, 13.14) * mm});
            skArc(sketch, "E860", {"start": v(0.84, 13.04) * mm, "mid": v(0.78, 12.88) * mm, "end": v(0.95, 12.82) * mm});
            skLineSegment(sketch, "E861", {"start": v(1.09, 13.03) * mm, "end": v(1.27, 13.14) * mm});
            skArc(sketch, "E862", {"start": v(1.34, 13.03) * mm, "mid": v(1.38, 13.2) * mm, "end": v(1.2, 13.25) * mm});
            skArc(sketch, "E863", {"start": v(1.02, 13.13) * mm, "mid": v(0.98, 12.96) * mm, "end": v(1.15, 12.92) * mm});
            skLineSegment(sketch, "E864", {"start": v(1.27, 13.14) * mm, "end": v(1.44, 13.27) * mm});
            skArc(sketch, "E865", {"start": v(1.52, 13.17) * mm, "mid": v(1.54, 13.35) * mm, "end": v(1.37, 13.37) * mm});
            skArc(sketch, "E866", {"start": v(1.2, 13.24) * mm, "mid": v(1.17, 13.06) * mm, "end": v(1.35, 13.04) * mm});
            skLineSegment(sketch, "E867", {"start": v(1.44, 13.27) * mm, "end": v(1.6, 13.42) * mm});
            skArc(sketch, "E868", {"start": v(1.69, 13.32) * mm, "mid": v(1.7, 13.5) * mm, "end": v(1.52, 13.5) * mm});
            skArc(sketch, "E869", {"start": v(1.36, 13.36) * mm, "mid": v(1.35, 13.19) * mm, "end": v(1.53, 13.18) * mm});
            skLineSegment(sketch, "E870", {"start": v(1.6, 13.42) * mm, "end": v(1.75, 13.58) * mm});
            skArc(sketch, "E871", {"start": v(1.84, 13.5) * mm, "mid": v(1.83, 13.67) * mm, "end": v(1.65, 13.66) * mm});
            skArc(sketch, "E872", {"start": v(1.51, 13.5) * mm, "mid": v(1.52, 13.32) * mm, "end": v(1.7, 13.33) * mm});
            skLineSegment(sketch, "E873", {"start": v(1.75, 13.58) * mm, "end": v(1.88, 13.75) * mm});
            skArc(sketch, "E874", {"start": v(1.98, 13.68) * mm, "mid": v(1.95, 13.85) * mm, "end": v(1.78, 13.82) * mm});
            skArc(sketch, "E875", {"start": v(1.65, 13.65) * mm, "mid": v(1.67, 13.48) * mm, "end": v(1.85, 13.5) * mm});
            skLineSegment(sketch, "E876", {"start": v(1.88, 13.75) * mm, "end": v(1.99, 13.94) * mm});
            skArc(sketch, "E877", {"start": v(2.1, 13.87) * mm, "mid": v(2.05, 14.04) * mm, "end": v(1.88, 14) * mm});
            skArc(sketch, "E878", {"start": v(1.77, 13.81) * mm, "mid": v(1.81, 13.64) * mm, "end": v(1.98, 13.69) * mm});
            skLineSegment(sketch, "E879", {"start": v(1.99, 13.94) * mm, "end": v(2.08, 14.13) * mm});
            skArc(sketch, "E880", {"start": v(2.2, 14.08) * mm, "mid": v(2.14, 14.25) * mm, "end": v(1.97, 14.19) * mm});
            skArc(sketch, "E881", {"start": v(1.88, 14) * mm, "mid": v(1.94, 13.82) * mm, "end": v(2.1, 13.88) * mm});
            skLineSegment(sketch, "E882", {"start": v(2.08, 14.13) * mm, "end": v(2.16, 14.34) * mm});
            skArc(sketch, "E883", {"start": v(2.27, 14.3) * mm, "mid": v(2.2, 14.46) * mm, "end": v(2.04, 14.38) * mm});
            skArc(sketch, "E884", {"start": v(1.96, 14.18) * mm, "mid": v(2.04, 14.02) * mm, "end": v(2.2, 14.1) * mm});
            skLineSegment(sketch, "E885", {"start": v(2.16, 14.34) * mm, "end": v(2.21, 14.56) * mm});
            skArc(sketch, "E886", {"start": v(2.33, 14.53) * mm, "mid": v(2.24, 14.68) * mm, "end": v(2.09, 14.59) * mm});
            skArc(sketch, "E887", {"start": v(2.04, 14.37) * mm, "mid": v(2.13, 14.22) * mm, "end": v(2.28, 14.31) * mm});
            skLineSegment(sketch, "E888", {"start": v(2.21, 14.56) * mm, "end": v(2.24, 14.78) * mm});
            skArc(sketch, "E889", {"start": v(2.37, 14.76) * mm, "mid": v(2.26, 14.9) * mm, "end": v(2.12, 14.8) * mm});
            skArc(sketch, "E890", {"start": v(2.09, 14.58) * mm, "mid": v(2.2, 14.43) * mm, "end": v(2.33, 14.54) * mm});
            skLineSegment(sketch, "E891", {"start": v(2.24, 14.78) * mm, "end": v(2.25, 15.03) * mm});
            skArc(sketch, "E892", {"start": v(2.38, 15.02) * mm, "mid": v(2.26, 15.15) * mm, "end": v(2.13, 15.03) * mm});
            skArc(sketch, "E893", {"start": v(2.12, 14.79) * mm, "mid": v(2.24, 14.66) * mm, "end": v(2.37, 14.78) * mm});
            skLineSegment(sketch, "E894", {"start": v(2.25, 15.03) * mm, "end": v(2.25, 18.36) * mm});
            skArc(sketch, "E895", {"start": v(2.38, 18.36) * mm, "mid": v(2.25, 18.48) * mm, "end": v(2.13, 18.36) * mm});
            skArc(sketch, "E896", {"start": v(2.13, 15.03) * mm, "mid": v(2.25, 14.9) * mm, "end": v(2.38, 15.03) * mm});
            skLineSegment(sketch, "E897", {"start": v(2.25, 18.36) * mm, "end": v(1.53, 20.57) * mm});
            skArc(sketch, "E898", {"start": v(1.65, 20.61) * mm, "mid": v(1.5, 20.7) * mm, "end": v(1.41, 20.54) * mm});
            skArc(sketch, "E899", {"start": v(2.14, 18.32) * mm, "mid": v(2.3, 18.24) * mm, "end": v(2.37, 18.4) * mm});
            skLineSegment(sketch, "E900", {"start": v(1.53, 20.57) * mm, "end": v(0.96, 21.46) * mm});
            skArc(sketch, "E901", {"start": v(1.06, 21.53) * mm, "mid": v(0.9, 21.56) * mm, "end": v(0.85, 21.4) * mm});
            skArc(sketch, "E902", {"start": v(1.43, 20.5) * mm, "mid": v(1.6, 20.47) * mm, "end": v(1.64, 20.64) * mm});
            skLineSegment(sketch, "E903", {"start": v(0.96, 21.46) * mm, "end": v(-0.95, 21.46) * mm});
            skArc(sketch, "E904", {"start": v(-0.95, 21.58) * mm, "mid": v(-1.07, 21.46) * mm, "end": v(-0.95, 21.33) * mm});
            skArc(sketch, "E905", {"start": v(0.96, 21.33) * mm, "mid": v(1.08, 21.46) * mm, "end": v(0.96, 21.58) * mm});
            skLineSegment(sketch, "E906", {"start": v(-0.95, 21.46) * mm, "end": v(-1.52, 20.57) * mm});
            skArc(sketch, "E907", {"start": v(-1.63, 20.64) * mm, "mid": v(-1.6, 20.47) * mm, "end": v(-1.42, 20.5) * mm});
            skArc(sketch, "E908", {"start": v(-0.84, 21.4) * mm, "mid": v(-0.88, 21.56) * mm, "end": v(-1.05, 21.53) * mm});
            skLineSegment(sketch, "E909", {"start": v(-1.52, 20.57) * mm, "end": v(-2.25, 18.36) * mm});
            skArc(sketch, "E910", {"start": v(-2.36, 18.4) * mm, "mid": v(-2.28, 18.24) * mm, "end": v(-2.13, 18.32) * mm});
            skArc(sketch, "E911", {"start": v(-1.4, 20.54) * mm, "mid": v(-1.49, 20.7) * mm, "end": v(-1.64, 20.61) * mm});
            skLineSegment(sketch, "E912", {"start": v(-1.03, 13) * mm, "end": v(1.03, 13) * mm});
            skArc(sketch, "E913", {"start": v(1.03, 12.87) * mm, "mid": v(1.16, 13) * mm, "end": v(1.03, 13.12) * mm});
            skArc(sketch, "E914", {"start": v(-1.03, 13.12) * mm, "mid": v(-1.15, 13) * mm, "end": v(-1.03, 12.87) * mm});
            skLineSegment(sketch, "E915", {"start": v(-1.67, 13.5) * mm, "end": v(1.68, 13.5) * mm});
            skArc(sketch, "E916", {"start": v(1.68, 13.37) * mm, "mid": v(1.8, 13.5) * mm, "end": v(1.68, 13.62) * mm});
            skArc(sketch, "E917", {"start": v(-1.67, 13.62) * mm, "mid": v(-1.8, 13.5) * mm, "end": v(-1.67, 13.37) * mm});
            skLineSegment(sketch, "E918", {"start": v(-2, 14) * mm, "end": v(2.02, 14) * mm});
            skArc(sketch, "E919", {"start": v(2.02, 13.87) * mm, "mid": v(2.14, 14) * mm, "end": v(2.02, 14.12) * mm});
            skArc(sketch, "E920", {"start": v(-2, 14.12) * mm, "mid": v(-2.13, 14) * mm, "end": v(-2, 13.87) * mm});
            skLineSegment(sketch, "E921", {"start": v(-2.19, 14.5) * mm, "end": v(2.2, 14.5) * mm});
            skArc(sketch, "E922", {"start": v(2.2, 14.37) * mm, "mid": v(2.32, 14.5) * mm, "end": v(2.2, 14.62) * mm});
            skArc(sketch, "E923", {"start": v(-2.19, 14.62) * mm, "mid": v(-2.31, 14.5) * mm, "end": v(-2.19, 14.37) * mm});
            skLineSegment(sketch, "E924", {"start": v(-2.23, 15) * mm, "end": v(2.25, 15) * mm});
            skArc(sketch, "E925", {"start": v(2.25, 14.87) * mm, "mid": v(2.38, 15) * mm, "end": v(2.25, 15.12) * mm});
            skArc(sketch, "E926", {"start": v(-2.23, 15.12) * mm, "mid": v(-2.36, 15) * mm, "end": v(-2.23, 14.87) * mm});
            skLineSegment(sketch, "E927", {"start": v(-2.24, 15.5) * mm, "end": v(2.25, 15.5) * mm});
            skArc(sketch, "E928", {"start": v(2.25, 15.37) * mm, "mid": v(2.38, 15.5) * mm, "end": v(2.25, 15.62) * mm});
            skArc(sketch, "E929", {"start": v(-2.24, 15.62) * mm, "mid": v(-2.36, 15.5) * mm, "end": v(-2.24, 15.37) * mm});
            skLineSegment(sketch, "E930", {"start": v(-2.24, 16) * mm, "end": v(2.25, 16) * mm});
            skArc(sketch, "E931", {"start": v(2.25, 15.87) * mm, "mid": v(2.38, 16) * mm, "end": v(2.25, 16.12) * mm});
            skArc(sketch, "E932", {"start": v(-2.24, 16.12) * mm, "mid": v(-2.36, 16) * mm, "end": v(-2.24, 15.87) * mm});
            skLineSegment(sketch, "E933", {"start": v(-2.24, 16.5) * mm, "end": v(2.25, 16.5) * mm});
            skArc(sketch, "E934", {"start": v(2.25, 16.37) * mm, "mid": v(2.38, 16.5) * mm, "end": v(2.25, 16.62) * mm});
            skArc(sketch, "E935", {"start": v(-2.24, 16.62) * mm, "mid": v(-2.36, 16.5) * mm, "end": v(-2.24, 16.37) * mm});
            skLineSegment(sketch, "E936", {"start": v(-2.24, 17) * mm, "end": v(2.25, 17) * mm});
            skArc(sketch, "E937", {"start": v(2.25, 16.87) * mm, "mid": v(2.38, 17) * mm, "end": v(2.25, 17.12) * mm});
            skArc(sketch, "E938", {"start": v(-2.24, 17.12) * mm, "mid": v(-2.37, 17) * mm, "end": v(-2.24, 16.87) * mm});
            skLineSegment(sketch, "E939", {"start": v(-2.24, 17.5) * mm, "end": v(2.25, 17.5) * mm});
            skArc(sketch, "E940", {"start": v(2.25, 17.37) * mm, "mid": v(2.38, 17.5) * mm, "end": v(2.25, 17.62) * mm});
            skArc(sketch, "E941", {"start": v(-2.24, 17.62) * mm, "mid": v(-2.37, 17.5) * mm, "end": v(-2.24, 17.37) * mm});
            skLineSegment(sketch, "E942", {"start": v(-2.24, 18) * mm, "end": v(2.25, 18) * mm});
            skArc(sketch, "E943", {"start": v(2.25, 17.87) * mm, "mid": v(2.38, 18) * mm, "end": v(2.25, 18.12) * mm});
            skArc(sketch, "E944", {"start": v(-2.24, 18.12) * mm, "mid": v(-2.37, 18) * mm, "end": v(-2.24, 17.87) * mm});
            skLineSegment(sketch, "E945", {"start": v(-2.2, 18.5) * mm, "end": v(2.2, 18.5) * mm});
            skArc(sketch, "E946", {"start": v(2.2, 18.37) * mm, "mid": v(2.33, 18.5) * mm, "end": v(2.2, 18.62) * mm});
            skArc(sketch, "E947", {"start": v(-2.2, 18.62) * mm, "mid": v(-2.32, 18.5) * mm, "end": v(-2.2, 18.37) * mm});
            skLineSegment(sketch, "E948", {"start": v(-2.04, 19) * mm, "end": v(2.05, 19) * mm});
            skArc(sketch, "E949", {"start": v(2.05, 18.87) * mm, "mid": v(2.17, 19) * mm, "end": v(2.05, 19.12) * mm});
            skArc(sketch, "E950", {"start": v(-2.04, 19.12) * mm, "mid": v(-2.16, 19) * mm, "end": v(-2.04, 18.87) * mm});
            skLineSegment(sketch, "E951", {"start": v(-1.87, 19.5) * mm, "end": v(1.88, 19.5) * mm});
            skArc(sketch, "E952", {"start": v(1.88, 19.37) * mm, "mid": v(2, 19.5) * mm, "end": v(1.88, 19.62) * mm});
            skArc(sketch, "E953", {"start": v(-1.87, 19.62) * mm, "mid": v(-2, 19.5) * mm, "end": v(-1.87, 19.37) * mm});
            skLineSegment(sketch, "E954", {"start": v(-1.71, 20) * mm, "end": v(1.72, 20) * mm});
            skArc(sketch, "E955", {"start": v(1.72, 19.87) * mm, "mid": v(1.85, 20) * mm, "end": v(1.72, 20.12) * mm});
            skArc(sketch, "E956", {"start": v(-1.71, 20.12) * mm, "mid": v(-1.84, 20) * mm, "end": v(-1.71, 19.87) * mm});
            skLineSegment(sketch, "E957", {"start": v(-1.55, 20.5) * mm, "end": v(1.56, 20.5) * mm});
            skArc(sketch, "E958", {"start": v(1.56, 20.37) * mm, "mid": v(1.68, 20.5) * mm, "end": v(1.56, 20.62) * mm});
            skArc(sketch, "E959", {"start": v(-1.55, 20.62) * mm, "mid": v(-1.67, 20.5) * mm, "end": v(-1.55, 20.37) * mm});
            skLineSegment(sketch, "E960", {"start": v(-1.25, 21) * mm, "end": v(1.26, 21) * mm});
            skArc(sketch, "E961", {"start": v(1.26, 20.87) * mm, "mid": v(1.38, 21) * mm, "end": v(1.26, 21.12) * mm});
            skArc(sketch, "E962", {"start": v(-1.25, 21.12) * mm, "mid": v(-1.37, 21) * mm, "end": v(-1.25, 20.87) * mm});
            skLineSegment(sketch, "E963", {"start": v(-2.43, 28.4) * mm, "end": v(-2.33, 28.3) * mm});
            skArc(sketch, "E964", {"start": v(-2.36, 28.26) * mm, "mid": v(-2.3, 28.26) * mm, "end": v(-2.3, 28.33) * mm});
            skArc(sketch, "E965", {"start": v(-2.4, 28.43) * mm, "mid": v(-2.47, 28.43) * mm, "end": v(-2.47, 28.36) * mm});
            skLineSegment(sketch, "E966", {"start": v(-2.33, 28.3) * mm, "end": v(-2.2, 28.2) * mm});
            skArc(sketch, "E967", {"start": v(-2.23, 28.16) * mm, "mid": v(-2.16, 28.18) * mm, "end": v(-2.17, 28.25) * mm});
            skArc(sketch, "E968", {"start": v(-2.3, 28.34) * mm, "mid": v(-2.37, 28.32) * mm, "end": v(-2.36, 28.25) * mm});
            skLineSegment(sketch, "E969", {"start": v(-2.2, 28.2) * mm, "end": v(-2.06, 28.14) * mm});
            skArc(sketch, "E970", {"start": v(-2.08, 28.1) * mm, "mid": v(-2.02, 28.12) * mm, "end": v(-2.04, 28.18) * mm});
            skArc(sketch, "E971", {"start": v(-2.18, 28.25) * mm, "mid": v(-2.25, 28.23) * mm, "end": v(-2.22, 28.16) * mm});
            skLineSegment(sketch, "E972", {"start": v(-2.06, 28.14) * mm, "end": v(-1.9, 28.1) * mm});
            skArc(sketch, "E973", {"start": v(-1.92, 28.05) * mm, "mid": v(-1.86, 28.09) * mm, "end": v(-1.9, 28.15) * mm});
            skArc(sketch, "E974", {"start": v(-2.05, 28.19) * mm, "mid": v(-2.11, 28.15) * mm, "end": v(-2.07, 28.1) * mm});
            skLineSegment(sketch, "E975", {"start": v(-1.9, 28.1) * mm, "end": v(-1.83, 28.09) * mm});
            skArc(sketch, "E976", {"start": v(-1.84, 28.04) * mm, "mid": v(-1.78, 28.08) * mm, "end": v(-1.82, 28.14) * mm});
            skArc(sketch, "E977", {"start": v(-1.9, 28.15) * mm, "mid": v(-1.96, 28.1) * mm, "end": v(-1.92, 28.05) * mm});
            skLineSegment(sketch, "E978", {"start": v(-1.83, 28.09) * mm, "end": v(1.92, 28.1) * mm});
            skArc(sketch, "E979", {"start": v(1.92, 28.05) * mm, "mid": v(1.97, 28.1) * mm, "end": v(1.92, 28.15) * mm});
            skArc(sketch, "E980", {"start": v(-1.83, 28.14) * mm, "mid": v(-1.88, 28.09) * mm, "end": v(-1.83, 28.04) * mm});
            skLineSegment(sketch, "E981", {"start": v(1.92, 28.1) * mm, "end": v(2.08, 28.14) * mm});
            skArc(sketch, "E982", {"start": v(2.1, 28.1) * mm, "mid": v(2.12, 28.16) * mm, "end": v(2.06, 28.2) * mm});
            skArc(sketch, "E983", {"start": v(1.91, 28.15) * mm, "mid": v(1.88, 28.09) * mm, "end": v(1.94, 28.05) * mm});
            skLineSegment(sketch, "E984", {"start": v(2.08, 28.14) * mm, "end": v(2.22, 28.2) * mm});
            skArc(sketch, "E985", {"start": v(2.24, 28.16) * mm, "mid": v(2.26, 28.23) * mm, "end": v(2.2, 28.25) * mm});
            skArc(sketch, "E986", {"start": v(2.05, 28.19) * mm, "mid": v(2.03, 28.12) * mm, "end": v(2.1, 28.1) * mm});
            skLineSegment(sketch, "E987", {"start": v(2.22, 28.2) * mm, "end": v(2.34, 28.3) * mm});
            skArc(sketch, "E988", {"start": v(2.37, 28.26) * mm, "mid": v(2.38, 28.33) * mm, "end": v(2.31, 28.34) * mm});
            skArc(sketch, "E989", {"start": v(2.19, 28.25) * mm, "mid": v(2.18, 28.18) * mm, "end": v(2.25, 28.17) * mm});
            skLineSegment(sketch, "E990", {"start": v(2.34, 28.3) * mm, "end": v(2.44, 28.4) * mm});
            skArc(sketch, "E991", {"start": v(2.47, 28.36) * mm, "mid": v(2.47, 28.43) * mm, "end": v(2.4, 28.43) * mm});
            skArc(sketch, "E992", {"start": v(2.3, 28.34) * mm, "mid": v(2.3, 28.26) * mm, "end": v(2.38, 28.26) * mm});
            skLineSegment(sketch, "E993", {"start": v(2.44, 28.4) * mm, "end": v(2.34, 28.5) * mm});
            skArc(sketch, "E994", {"start": v(2.37, 28.53) * mm, "mid": v(2.3, 28.53) * mm, "end": v(2.3, 28.46) * mm});
            skArc(sketch, "E995", {"start": v(2.4, 28.36) * mm, "mid": v(2.47, 28.36) * mm, "end": v(2.47, 28.43) * mm});
            skLineSegment(sketch, "E996", {"start": v(2.34, 28.5) * mm, "end": v(2.2, 28.58) * mm});
            skArc(sketch, "E997", {"start": v(2.24, 28.62) * mm, "mid": v(2.17, 28.6) * mm, "end": v(2.18, 28.54) * mm});
            skArc(sketch, "E998", {"start": v(2.3, 28.45) * mm, "mid": v(2.38, 28.46) * mm, "end": v(2.36, 28.53) * mm});
            skLineSegment(sketch, "E999", {"start": v(2.2, 28.58) * mm, "end": v(2.07, 28.65) * mm});
            skArc(sketch, "E1000", {"start": v(2.09, 28.7) * mm, "mid": v(2.02, 28.67) * mm, "end": v(2.05, 28.6) * mm});
            skArc(sketch, "E1001", {"start": v(2.19, 28.54) * mm, "mid": v(2.25, 28.56) * mm, "end": v(2.23, 28.63) * mm});
            skLineSegment(sketch, "E1002", {"start": v(2.07, 28.65) * mm, "end": v(1.91, 28.69) * mm});
            skArc(sketch, "E1003", {"start": v(1.93, 28.74) * mm, "mid": v(1.87, 28.7) * mm, "end": v(1.9, 28.64) * mm});
            skArc(sketch, "E1004", {"start": v(2.05, 28.6) * mm, "mid": v(2.12, 28.63) * mm, "end": v(2.08, 28.7) * mm});
            skLineSegment(sketch, "E1005", {"start": v(1.91, 28.69) * mm, "end": v(1.84, 28.7) * mm});
            skArc(sketch, "E1006", {"start": v(1.84, 28.75) * mm, "mid": v(1.79, 28.7) * mm, "end": v(1.83, 28.65) * mm});
            skArc(sketch, "E1007", {"start": v(1.9, 28.64) * mm, "mid": v(1.96, 28.68) * mm, "end": v(1.92, 28.74) * mm});
            skLineSegment(sketch, "E1008", {"start": v(1.84, 28.7) * mm, "end": v(-1.92, 28.69) * mm});
            skArc(sketch, "E1009", {"start": v(-1.92, 28.74) * mm, "mid": v(-1.97, 28.69) * mm, "end": v(-1.92, 28.64) * mm});
            skArc(sketch, "E1010", {"start": v(1.84, 28.65) * mm, "mid": v(1.88, 28.7) * mm, "end": v(1.83, 28.75) * mm});
            skLineSegment(sketch, "E1011", {"start": v(-1.92, 28.69) * mm, "end": v(-2.07, 28.64) * mm});
            skArc(sketch, "E1012", {"start": v(-2.08, 28.7) * mm, "mid": v(-2.12, 28.63) * mm, "end": v(-2.06, 28.6) * mm});
            skArc(sketch, "E1013", {"start": v(-1.9, 28.64) * mm, "mid": v(-1.87, 28.7) * mm, "end": v(-1.93, 28.74) * mm});
            skLineSegment(sketch, "E1014", {"start": v(-2.07, 28.64) * mm, "end": v(-2.21, 28.58) * mm});
            skArc(sketch, "E1015", {"start": v(-2.23, 28.62) * mm, "mid": v(-2.26, 28.56) * mm, "end": v(-2.19, 28.53) * mm});
            skArc(sketch, "E1016", {"start": v(-2.05, 28.6) * mm, "mid": v(-2.03, 28.67) * mm, "end": v(-2.1, 28.69) * mm});
            skLineSegment(sketch, "E1017", {"start": v(-2.21, 28.58) * mm, "end": v(-2.34, 28.49) * mm});
            skArc(sketch, "E1018", {"start": v(-2.37, 28.53) * mm, "mid": v(-2.38, 28.46) * mm, "end": v(-2.3, 28.45) * mm});
            skArc(sketch, "E1019", {"start": v(-2.18, 28.54) * mm, "mid": v(-2.17, 28.6) * mm, "end": v(-2.24, 28.62) * mm});
            skLineSegment(sketch, "E1020", {"start": v(-2.34, 28.49) * mm, "end": v(-2.43, 28.4) * mm});
            skArc(sketch, "E1021", {"start": v(-2.47, 28.43) * mm, "mid": v(-2.47, 28.36) * mm, "end": v(-2.4, 28.36) * mm});
            skArc(sketch, "E1022", {"start": v(-2.3, 28.45) * mm, "mid": v(-2.3, 28.52) * mm, "end": v(-2.37, 28.52) * mm});
            skLineSegment(sketch, "E1023", {"start": v(-2.19, 28.2) * mm, "end": v(2.2, 28.2) * mm});
            skArc(sketch, "E1024", {"start": v(2.2, 28.15) * mm, "mid": v(2.24, 28.2) * mm, "end": v(2.2, 28.25) * mm});
            skArc(sketch, "E1025", {"start": v(-2.19, 28.25) * mm, "mid": v(-2.24, 28.2) * mm, "end": v(-2.19, 28.15) * mm});
            skLineSegment(sketch, "E1026", {"start": v(-2.43, 28.4) * mm, "end": v(2.43, 28.4) * mm});
            skArc(sketch, "E1027", {"start": v(2.43, 28.35) * mm, "mid": v(2.48, 28.4) * mm, "end": v(2.43, 28.45) * mm});
            skArc(sketch, "E1028", {"start": v(-2.43, 28.45) * mm, "mid": v(-2.48, 28.4) * mm, "end": v(-2.43, 28.35) * mm});
            skLineSegment(sketch, "E1029", {"start": v(-2.17, 28.6) * mm, "end": v(2.17, 28.6) * mm});
            skArc(sketch, "E1030", {"start": v(2.17, 28.55) * mm, "mid": v(2.22, 28.6) * mm, "end": v(2.17, 28.65) * mm});
            skArc(sketch, "E1031", {"start": v(-2.17, 28.65) * mm, "mid": v(-2.22, 28.6) * mm, "end": v(-2.17, 28.55) * mm});
            skCircle(sketch, "E1032", {"center": v(0, 15) * mm, "radius": 1.7 * mm});
            skArc(sketch, "E1033", {"start": v(0, 14.12) * mm, "mid": v(0.88, 15) * mm, "end": v(0, 15.87) * mm});
            skArc(sketch, "E1034", {"start": v(0, 15.87) * mm, "mid": v(-0.87, 15) * mm, "end": v(0, 14.12) * mm});
            skCircle(sketch, "E1035", {"center": v(0, 25) * mm, "radius": 1.7 * mm});
            skArc(sketch, "E1036", {"start": v(0, 24.12) * mm, "mid": v(0.88, 25) * mm, "end": v(0, 25.87) * mm});
            skArc(sketch, "E1037", {"start": v(0, 25.87) * mm, "mid": v(-0.87, 25) * mm, "end": v(0, 24.12) * mm});
            skLineSegment(sketch, "E1038", {"start": v(-3.8, 0.7) * mm, "end": v(-3.8, 0.5) * mm});
            skArc(sketch, "E1039", {"start": v(-3.8, 0.5) * mm, "mid": v(-3.78, 0.47) * mm, "end": v(-3.75, 0.45) * mm});
            skLineSegment(sketch, "E1040", {"start": v(-3.75, 0.45) * mm, "end": v(-3.05, 0.45) * mm});
            skArc(sketch, "E1041", {"start": v(-3.05, 0.45) * mm, "mid": v(-3.02, 0.47) * mm, "end": v(-3, 0.5) * mm});
            skLineSegment(sketch, "E1042", {"start": v(-3, 0.5) * mm, "end": v(-3, 0.7) * mm});
            skArc(sketch, "E1043", {"start": v(-3, 0.7) * mm, "mid": v(-3.02, 0.74) * mm, "end": v(-3.05, 0.75) * mm});
            skLineSegment(sketch, "E1044", {"start": v(-3.05, 0.75) * mm, "end": v(-3.75, 0.75) * mm});
            skArc(sketch, "E1045", {"start": v(-3.75, 0.75) * mm, "mid": v(-3.78, 0.74) * mm, "end": v(-3.8, 0.7) * mm});
            skLineSegment(sketch, "E1046", {"start": v(-3.8, 0.2) * mm, "end": v(-3.8, 0) * mm});
            skArc(sketch, "E1047", {"start": v(-3.8, 0) * mm, "mid": v(-3.78, -0.03) * mm, "end": v(-3.75, -0.05) * mm});
            skLineSegment(sketch, "E1048", {"start": v(-3.75, -0.05) * mm, "end": v(-3.05, -0.05) * mm});
            skArc(sketch, "E1049", {"start": v(-3.05, -0.05) * mm, "mid": v(-3.02, -0.03) * mm, "end": v(-3, 0) * mm});
            skLineSegment(sketch, "E1050", {"start": v(-3, 0) * mm, "end": v(-3, 0.2) * mm});
            skArc(sketch, "E1051", {"start": v(-3, 0.2) * mm, "mid": v(-3.02, 0.24) * mm, "end": v(-3.05, 0.25) * mm});
            skLineSegment(sketch, "E1052", {"start": v(-3.05, 0.25) * mm, "end": v(-3.75, 0.25) * mm});
            skArc(sketch, "E1053", {"start": v(-3.75, 0.25) * mm, "mid": v(-3.78, 0.24) * mm, "end": v(-3.8, 0.2) * mm});
            skLineSegment(sketch, "E1054", {"start": v(-3.8, -0.3) * mm, "end": v(-3.8, -0.5) * mm});
            skArc(sketch, "E1055", {"start": v(-3.8, -0.5) * mm, "mid": v(-3.78, -0.53) * mm, "end": v(-3.75, -0.55) * mm});
            skLineSegment(sketch, "E1056", {"start": v(-3.75, -0.55) * mm, "end": v(-3.05, -0.55) * mm});
            skArc(sketch, "E1057", {"start": v(-3.05, -0.55) * mm, "mid": v(-3.02, -0.53) * mm, "end": v(-3, -0.5) * mm});
            skLineSegment(sketch, "E1058", {"start": v(-3, -0.5) * mm, "end": v(-3, -0.3) * mm});
            skArc(sketch, "E1059", {"start": v(-3, -0.3) * mm, "mid": v(-3.02, -0.26) * mm, "end": v(-3.05, -0.25) * mm});
            skLineSegment(sketch, "E1060", {"start": v(-3.05, -0.25) * mm, "end": v(-3.75, -0.25) * mm});
            skArc(sketch, "E1061", {"start": v(-3.75, -0.25) * mm, "mid": v(-3.78, -0.26) * mm, "end": v(-3.8, -0.3) * mm});
            skLineSegment(sketch, "E1062", {"start": v(-3.8, -0.8) * mm, "end": v(-3.8, -1) * mm});
            skArc(sketch, "E1063", {"start": v(-3.8, -1) * mm, "mid": v(-3.78, -1.03) * mm, "end": v(-3.75, -1.05) * mm});
            skLineSegment(sketch, "E1064", {"start": v(-3.75, -1.05) * mm, "end": v(-3.05, -1.05) * mm});
            skArc(sketch, "E1065", {"start": v(-3.05, -1.05) * mm, "mid": v(-3.02, -1.03) * mm, "end": v(-3, -1) * mm});
            skLineSegment(sketch, "E1066", {"start": v(-3, -1) * mm, "end": v(-3, -0.8) * mm});
            skArc(sketch, "E1067", {"start": v(-3, -0.8) * mm, "mid": v(-3.02, -0.76) * mm, "end": v(-3.05, -0.75) * mm});
            skLineSegment(sketch, "E1068", {"start": v(-3.05, -0.75) * mm, "end": v(-3.75, -0.75) * mm});
            skArc(sketch, "E1069", {"start": v(-3.75, -0.75) * mm, "mid": v(-3.78, -0.76) * mm, "end": v(-3.8, -0.8) * mm});
            skLineSegment(sketch, "E1070", {"start": v(-3.8, -1.3) * mm, "end": v(-3.8, -1.5) * mm});
            skArc(sketch, "E1071", {"start": v(-3.8, -1.5) * mm, "mid": v(-3.78, -1.53) * mm, "end": v(-3.75, -1.55) * mm});
            skLineSegment(sketch, "E1072", {"start": v(-3.75, -1.55) * mm, "end": v(-3.05, -1.55) * mm});
            skArc(sketch, "E1073", {"start": v(-3.05, -1.55) * mm, "mid": v(-3.02, -1.53) * mm, "end": v(-3, -1.5) * mm});
            skLineSegment(sketch, "E1074", {"start": v(-3, -1.5) * mm, "end": v(-3, -1.3) * mm});
            skArc(sketch, "E1075", {"start": v(-3, -1.3) * mm, "mid": v(-3.02, -1.26) * mm, "end": v(-3.05, -1.25) * mm});
            skLineSegment(sketch, "E1076", {"start": v(-3.05, -1.25) * mm, "end": v(-3.75, -1.25) * mm});
            skArc(sketch, "E1077", {"start": v(-3.75, -1.25) * mm, "mid": v(-3.78, -1.26) * mm, "end": v(-3.8, -1.3) * mm});
            skLineSegment(sketch, "E1078", {"start": v(-3.8, -1.8) * mm, "end": v(-3.8, -2) * mm});
            skArc(sketch, "E1079", {"start": v(-3.8, -2) * mm, "mid": v(-3.78, -2.03) * mm, "end": v(-3.75, -2.05) * mm});
            skLineSegment(sketch, "E1080", {"start": v(-3.75, -2.05) * mm, "end": v(-3.05, -2.05) * mm});
            skArc(sketch, "E1081", {"start": v(-3.05, -2.05) * mm, "mid": v(-3.02, -2.03) * mm, "end": v(-3, -2) * mm});
            skLineSegment(sketch, "E1082", {"start": v(-3, -2) * mm, "end": v(-3, -1.8) * mm});
            skArc(sketch, "E1083", {"start": v(-3, -1.8) * mm, "mid": v(-3.02, -1.76) * mm, "end": v(-3.05, -1.75) * mm});
            skLineSegment(sketch, "E1084", {"start": v(-3.05, -1.75) * mm, "end": v(-3.75, -1.75) * mm});
            skArc(sketch, "E1085", {"start": v(-3.75, -1.75) * mm, "mid": v(-3.78, -1.76) * mm, "end": v(-3.8, -1.8) * mm});
            skLineSegment(sketch, "E1086", {"start": v(-3, -2.5) * mm, "end": v(-3, -2.3) * mm});
            skArc(sketch, "E1087", {"start": v(-3, -2.3) * mm, "mid": v(-3.02, -2.26) * mm, "end": v(-3.05, -2.25) * mm});
            skLineSegment(sketch, "E1088", {"start": v(-3.05, -2.25) * mm, "end": v(-3.75, -2.25) * mm});
            skArc(sketch, "E1089", {"start": v(-3.75, -2.25) * mm, "mid": v(-3.78, -2.26) * mm, "end": v(-3.8, -2.3) * mm});
            skLineSegment(sketch, "E1090", {"start": v(-3.8, -2.3) * mm, "end": v(-3.8, -2.5) * mm});
            skArc(sketch, "E1091", {"start": v(-3.8, -2.5) * mm, "mid": v(-3.78, -2.53) * mm, "end": v(-3.75, -2.55) * mm});
            skLineSegment(sketch, "E1092", {"start": v(-3.75, -2.55) * mm, "end": v(-3.05, -2.55) * mm});
            skArc(sketch, "E1093", {"start": v(-3.05, -2.55) * mm, "mid": v(-3.02, -2.53) * mm, "end": v(-3, -2.5) * mm});
            skLineSegment(sketch, "E1094", {"start": v(-3, -3) * mm, "end": v(-3, -2.8) * mm});
            skArc(sketch, "E1095", {"start": v(-3, -2.8) * mm, "mid": v(-3.02, -2.76) * mm, "end": v(-3.05, -2.75) * mm});
            skLineSegment(sketch, "E1096", {"start": v(-3.05, -2.75) * mm, "end": v(-3.75, -2.75) * mm});
            skArc(sketch, "E1097", {"start": v(-3.75, -2.75) * mm, "mid": v(-3.78, -2.76) * mm, "end": v(-3.8, -2.8) * mm});
            skLineSegment(sketch, "E1098", {"start": v(-3.8, -2.8) * mm, "end": v(-3.8, -3) * mm});
            skArc(sketch, "E1099", {"start": v(-3.8, -3) * mm, "mid": v(-3.78, -3.03) * mm, "end": v(-3.75, -3.05) * mm});
            skLineSegment(sketch, "E1100", {"start": v(-3.75, -3.05) * mm, "end": v(-3.05, -3.05) * mm});
            skArc(sketch, "E1101", {"start": v(-3.05, -3.05) * mm, "mid": v(-3.02, -3.03) * mm, "end": v(-3, -3) * mm});
            skLineSegment(sketch, "E1102", {"start": v(-3, -3.5) * mm, "end": v(-3, -3.3) * mm});
            skArc(sketch, "E1103", {"start": v(-3, -3.3) * mm, "mid": v(-3.02, -3.26) * mm, "end": v(-3.05, -3.25) * mm});
            skLineSegment(sketch, "E1104", {"start": v(-3.05, -3.25) * mm, "end": v(-3.75, -3.25) * mm});
            skArc(sketch, "E1105", {"start": v(-3.75, -3.25) * mm, "mid": v(-3.78, -3.26) * mm, "end": v(-3.8, -3.3) * mm});
            skLineSegment(sketch, "E1106", {"start": v(-3.8, -3.3) * mm, "end": v(-3.8, -3.5) * mm});
            skArc(sketch, "E1107", {"start": v(-3.8, -3.5) * mm, "mid": v(-3.78, -3.53) * mm, "end": v(-3.75, -3.55) * mm});
            skLineSegment(sketch, "E1108", {"start": v(-3.75, -3.55) * mm, "end": v(-3.05, -3.55) * mm});
            skArc(sketch, "E1109", {"start": v(-3.05, -3.55) * mm, "mid": v(-3.02, -3.53) * mm, "end": v(-3, -3.5) * mm});
            skLineSegment(sketch, "E1110", {"start": v(-3, -4) * mm, "end": v(-3, -3.8) * mm});
            skArc(sketch, "E1111", {"start": v(-3, -3.8) * mm, "mid": v(-3.02, -3.76) * mm, "end": v(-3.05, -3.75) * mm});
            skLineSegment(sketch, "E1112", {"start": v(-3.05, -3.75) * mm, "end": v(-3.75, -3.75) * mm});
            skArc(sketch, "E1113", {"start": v(-3.75, -3.75) * mm, "mid": v(-3.78, -3.76) * mm, "end": v(-3.8, -3.8) * mm});
            skLineSegment(sketch, "E1114", {"start": v(-3.8, -3.8) * mm, "end": v(-3.8, -4) * mm});
            skArc(sketch, "E1115", {"start": v(-3.8, -4) * mm, "mid": v(-3.78, -4.03) * mm, "end": v(-3.75, -4.05) * mm});
            skLineSegment(sketch, "E1116", {"start": v(-3.75, -4.05) * mm, "end": v(-3.05, -4.05) * mm});
            skArc(sketch, "E1117", {"start": v(-3.05, -4.05) * mm, "mid": v(-3.02, -4.03) * mm, "end": v(-3, -4) * mm});
            skLineSegment(sketch, "E1118", {"start": v(-3, -4.5) * mm, "end": v(-3, -4.3) * mm});
            skArc(sketch, "E1119", {"start": v(-3, -4.3) * mm, "mid": v(-3.02, -4.26) * mm, "end": v(-3.05, -4.25) * mm});
            skLineSegment(sketch, "E1120", {"start": v(-3.05, -4.25) * mm, "end": v(-3.75, -4.25) * mm});
            skArc(sketch, "E1121", {"start": v(-3.75, -4.25) * mm, "mid": v(-3.78, -4.26) * mm, "end": v(-3.8, -4.3) * mm});
            skLineSegment(sketch, "E1122", {"start": v(-3.8, -4.3) * mm, "end": v(-3.8, -4.5) * mm});
            skArc(sketch, "E1123", {"start": v(-3.8, -4.5) * mm, "mid": v(-3.78, -4.53) * mm, "end": v(-3.75, -4.55) * mm});
            skLineSegment(sketch, "E1124", {"start": v(-3.75, -4.55) * mm, "end": v(-3.05, -4.55) * mm});
            skArc(sketch, "E1125", {"start": v(-3.05, -4.55) * mm, "mid": v(-3.02, -4.53) * mm, "end": v(-3, -4.5) * mm});
            skLineSegment(sketch, "E1126", {"start": v(-2.6, -5.7) * mm, "end": v(-2.4, -5.7) * mm});
            skArc(sketch, "E1127", {"start": v(-2.4, -5.7) * mm, "mid": v(-2.37, -5.68) * mm, "end": v(-2.35, -5.65) * mm});
            skLineSegment(sketch, "E1128", {"start": v(-2.35, -5.65) * mm, "end": v(-2.35, -4.95) * mm});
            skArc(sketch, "E1129", {"start": v(-2.35, -4.95) * mm, "mid": v(-2.37, -4.91) * mm, "end": v(-2.4, -4.9) * mm});
            skLineSegment(sketch, "E1130", {"start": v(-2.4, -4.9) * mm, "end": v(-2.6, -4.9) * mm});
            skArc(sketch, "E1131", {"start": v(-2.6, -4.9) * mm, "mid": v(-2.63, -4.91) * mm, "end": v(-2.65, -4.95) * mm});
            skLineSegment(sketch, "E1132", {"start": v(-2.65, -4.95) * mm, "end": v(-2.65, -5.65) * mm});
            skArc(sketch, "E1133", {"start": v(-2.65, -5.65) * mm, "mid": v(-2.63, -5.68) * mm, "end": v(-2.6, -5.7) * mm});
            skLineSegment(sketch, "E1134", {"start": v(-2.1, -5.7) * mm, "end": v(-1.9, -5.7) * mm});
            skArc(sketch, "E1135", {"start": v(-1.9, -5.7) * mm, "mid": v(-1.87, -5.68) * mm, "end": v(-1.85, -5.65) * mm});
            skLineSegment(sketch, "E1136", {"start": v(-1.85, -5.65) * mm, "end": v(-1.85, -4.95) * mm});
            skArc(sketch, "E1137", {"start": v(-1.85, -4.95) * mm, "mid": v(-1.87, -4.91) * mm, "end": v(-1.9, -4.9) * mm});
            skLineSegment(sketch, "E1138", {"start": v(-1.9, -4.9) * mm, "end": v(-2.1, -4.9) * mm});
            skArc(sketch, "E1139", {"start": v(-2.1, -4.9) * mm, "mid": v(-2.13, -4.91) * mm, "end": v(-2.15, -4.95) * mm});
            skLineSegment(sketch, "E1140", {"start": v(-2.15, -4.95) * mm, "end": v(-2.15, -5.65) * mm});
            skArc(sketch, "E1141", {"start": v(-2.15, -5.65) * mm, "mid": v(-2.13, -5.68) * mm, "end": v(-2.1, -5.7) * mm});
            skLineSegment(sketch, "E1142", {"start": v(-1.6, -5.7) * mm, "end": v(-1.4, -5.7) * mm});
            skArc(sketch, "E1143", {"start": v(-1.4, -5.7) * mm, "mid": v(-1.37, -5.68) * mm, "end": v(-1.35, -5.65) * mm});
            skLineSegment(sketch, "E1144", {"start": v(-1.35, -5.65) * mm, "end": v(-1.35, -4.95) * mm});
            skArc(sketch, "E1145", {"start": v(-1.35, -4.95) * mm, "mid": v(-1.37, -4.91) * mm, "end": v(-1.4, -4.9) * mm});
            skLineSegment(sketch, "E1146", {"start": v(-1.4, -4.9) * mm, "end": v(-1.6, -4.9) * mm});
            skArc(sketch, "E1147", {"start": v(-1.6, -4.9) * mm, "mid": v(-1.63, -4.91) * mm, "end": v(-1.65, -4.95) * mm});
            skLineSegment(sketch, "E1148", {"start": v(-1.65, -4.95) * mm, "end": v(-1.65, -5.65) * mm});
            skArc(sketch, "E1149", {"start": v(-1.65, -5.65) * mm, "mid": v(-1.63, -5.68) * mm, "end": v(-1.6, -5.7) * mm});
            skLineSegment(sketch, "E1150", {"start": v(-1.1, -5.7) * mm, "end": v(-0.9, -5.7) * mm});
            skArc(sketch, "E1151", {"start": v(-0.9, -5.7) * mm, "mid": v(-0.87, -5.68) * mm, "end": v(-0.85, -5.65) * mm});
            skLineSegment(sketch, "E1152", {"start": v(-0.85, -5.65) * mm, "end": v(-0.85, -4.95) * mm});
            skArc(sketch, "E1153", {"start": v(-0.85, -4.95) * mm, "mid": v(-0.87, -4.91) * mm, "end": v(-0.9, -4.9) * mm});
            skLineSegment(sketch, "E1154", {"start": v(-0.9, -4.9) * mm, "end": v(-1.1, -4.9) * mm});
            skArc(sketch, "E1155", {"start": v(-1.1, -4.9) * mm, "mid": v(-1.13, -4.91) * mm, "end": v(-1.15, -4.95) * mm});
            skLineSegment(sketch, "E1156", {"start": v(-1.15, -4.95) * mm, "end": v(-1.15, -5.65) * mm});
            skArc(sketch, "E1157", {"start": v(-1.15, -5.65) * mm, "mid": v(-1.13, -5.68) * mm, "end": v(-1.1, -5.7) * mm});
            skLineSegment(sketch, "E1158", {"start": v(-0.6, -5.7) * mm, "end": v(-0.4, -5.7) * mm});
            skArc(sketch, "E1159", {"start": v(-0.4, -5.7) * mm, "mid": v(-0.37, -5.68) * mm, "end": v(-0.35, -5.65) * mm});
            skLineSegment(sketch, "E1160", {"start": v(-0.35, -5.65) * mm, "end": v(-0.35, -4.95) * mm});
            skArc(sketch, "E1161", {"start": v(-0.35, -4.95) * mm, "mid": v(-0.37, -4.91) * mm, "end": v(-0.4, -4.9) * mm});
            skLineSegment(sketch, "E1162", {"start": v(-0.4, -4.9) * mm, "end": v(-0.6, -4.9) * mm});
            skArc(sketch, "E1163", {"start": v(-0.6, -4.9) * mm, "mid": v(-0.63, -4.91) * mm, "end": v(-0.65, -4.95) * mm});
            skLineSegment(sketch, "E1164", {"start": v(-0.65, -4.95) * mm, "end": v(-0.65, -5.65) * mm});
            skArc(sketch, "E1165", {"start": v(-0.65, -5.65) * mm, "mid": v(-0.63, -5.68) * mm, "end": v(-0.6, -5.7) * mm});
            skLineSegment(sketch, "E1166", {"start": v(-0.1, -5.7) * mm, "end": v(0.1, -5.7) * mm});
            skArc(sketch, "E1167", {"start": v(0.1, -5.7) * mm, "mid": v(0.13, -5.68) * mm, "end": v(0.15, -5.65) * mm});
            skLineSegment(sketch, "E1168", {"start": v(0.15, -5.65) * mm, "end": v(0.15, -4.95) * mm});
            skArc(sketch, "E1169", {"start": v(0.15, -4.95) * mm, "mid": v(0.13, -4.91) * mm, "end": v(0.1, -4.9) * mm});
            skLineSegment(sketch, "E1170", {"start": v(0.1, -4.9) * mm, "end": v(-0.1, -4.9) * mm});
            skArc(sketch, "E1171", {"start": v(-0.1, -4.9) * mm, "mid": v(-0.13, -4.91) * mm, "end": v(-0.15, -4.95) * mm});
            skLineSegment(sketch, "E1172", {"start": v(-0.15, -4.95) * mm, "end": v(-0.15, -5.65) * mm});
            skArc(sketch, "E1173", {"start": v(-0.15, -5.65) * mm, "mid": v(-0.13, -5.68) * mm, "end": v(-0.1, -5.7) * mm});
            skLineSegment(sketch, "E1174", {"start": v(0.6, -4.9) * mm, "end": v(0.4, -4.9) * mm});
            skArc(sketch, "E1175", {"start": v(0.4, -4.9) * mm, "mid": v(0.37, -4.91) * mm, "end": v(0.35, -4.95) * mm});
            skLineSegment(sketch, "E1176", {"start": v(0.35, -4.95) * mm, "end": v(0.35, -5.65) * mm});
            skArc(sketch, "E1177", {"start": v(0.35, -5.65) * mm, "mid": v(0.37, -5.68) * mm, "end": v(0.4, -5.7) * mm});
            skLineSegment(sketch, "E1178", {"start": v(0.4, -5.7) * mm, "end": v(0.6, -5.7) * mm});
            skArc(sketch, "E1179", {"start": v(0.6, -5.7) * mm, "mid": v(0.63, -5.68) * mm, "end": v(0.65, -5.65) * mm});
            skLineSegment(sketch, "E1180", {"start": v(0.65, -5.65) * mm, "end": v(0.65, -4.95) * mm});
            skArc(sketch, "E1181", {"start": v(0.65, -4.95) * mm, "mid": v(0.63, -4.91) * mm, "end": v(0.6, -4.9) * mm});
            skLineSegment(sketch, "E1182", {"start": v(1.1, -4.9) * mm, "end": v(0.9, -4.9) * mm});
            skArc(sketch, "E1183", {"start": v(0.9, -4.9) * mm, "mid": v(0.87, -4.91) * mm, "end": v(0.85, -4.95) * mm});
            skLineSegment(sketch, "E1184", {"start": v(0.85, -4.95) * mm, "end": v(0.85, -5.65) * mm});
            skArc(sketch, "E1185", {"start": v(0.85, -5.65) * mm, "mid": v(0.87, -5.68) * mm, "end": v(0.9, -5.7) * mm});
            skLineSegment(sketch, "E1186", {"start": v(0.9, -5.7) * mm, "end": v(1.1, -5.7) * mm});
            skArc(sketch, "E1187", {"start": v(1.1, -5.7) * mm, "mid": v(1.13, -5.68) * mm, "end": v(1.15, -5.65) * mm});
            skLineSegment(sketch, "E1188", {"start": v(1.15, -5.65) * mm, "end": v(1.15, -4.95) * mm});
            skArc(sketch, "E1189", {"start": v(1.15, -4.95) * mm, "mid": v(1.13, -4.91) * mm, "end": v(1.1, -4.9) * mm});
            skLineSegment(sketch, "E1190", {"start": v(1.6, -4.9) * mm, "end": v(1.4, -4.9) * mm});
            skArc(sketch, "E1191", {"start": v(1.4, -4.9) * mm, "mid": v(1.37, -4.91) * mm, "end": v(1.35, -4.95) * mm});
            skLineSegment(sketch, "E1192", {"start": v(1.35, -4.95) * mm, "end": v(1.35, -5.65) * mm});
            skArc(sketch, "E1193", {"start": v(1.35, -5.65) * mm, "mid": v(1.37, -5.68) * mm, "end": v(1.4, -5.7) * mm});
            skLineSegment(sketch, "E1194", {"start": v(1.4, -5.7) * mm, "end": v(1.6, -5.7) * mm});
            skArc(sketch, "E1195", {"start": v(1.6, -5.7) * mm, "mid": v(1.63, -5.68) * mm, "end": v(1.65, -5.65) * mm});
            skLineSegment(sketch, "E1196", {"start": v(1.65, -5.65) * mm, "end": v(1.65, -4.95) * mm});
            skArc(sketch, "E1197", {"start": v(1.65, -4.95) * mm, "mid": v(1.63, -4.91) * mm, "end": v(1.6, -4.9) * mm});
            skLineSegment(sketch, "E1198", {"start": v(2.1, -4.9) * mm, "end": v(1.9, -4.9) * mm});
            skArc(sketch, "E1199", {"start": v(1.9, -4.9) * mm, "mid": v(1.87, -4.91) * mm, "end": v(1.85, -4.95) * mm});
            skLineSegment(sketch, "E1200", {"start": v(1.85, -4.95) * mm, "end": v(1.85, -5.65) * mm});
            skArc(sketch, "E1201", {"start": v(1.85, -5.65) * mm, "mid": v(1.87, -5.68) * mm, "end": v(1.9, -5.7) * mm});
            skLineSegment(sketch, "E1202", {"start": v(1.9, -5.7) * mm, "end": v(2.1, -5.7) * mm});
            skArc(sketch, "E1203", {"start": v(2.1, -5.7) * mm, "mid": v(2.13, -5.68) * mm, "end": v(2.15, -5.65) * mm});
            skLineSegment(sketch, "E1204", {"start": v(2.15, -5.65) * mm, "end": v(2.15, -4.95) * mm});
            skArc(sketch, "E1205", {"start": v(2.15, -4.95) * mm, "mid": v(2.13, -4.91) * mm, "end": v(2.1, -4.9) * mm});
            skLineSegment(sketch, "E1206", {"start": v(2.6, -4.9) * mm, "end": v(2.4, -4.9) * mm});
            skArc(sketch, "E1207", {"start": v(2.4, -4.9) * mm, "mid": v(2.37, -4.91) * mm, "end": v(2.35, -4.95) * mm});
            skLineSegment(sketch, "E1208", {"start": v(2.35, -4.95) * mm, "end": v(2.35, -5.65) * mm});
            skArc(sketch, "E1209", {"start": v(2.35, -5.65) * mm, "mid": v(2.37, -5.68) * mm, "end": v(2.4, -5.7) * mm});
            skLineSegment(sketch, "E1210", {"start": v(2.4, -5.7) * mm, "end": v(2.6, -5.7) * mm});
            skArc(sketch, "E1211", {"start": v(2.6, -5.7) * mm, "mid": v(2.63, -5.68) * mm, "end": v(2.65, -5.65) * mm});
            skLineSegment(sketch, "E1212", {"start": v(2.65, -5.65) * mm, "end": v(2.65, -4.95) * mm});
            skArc(sketch, "E1213", {"start": v(2.65, -4.95) * mm, "mid": v(2.63, -4.91) * mm, "end": v(2.6, -4.9) * mm});
            skLineSegment(sketch, "E1214", {"start": v(3.8, -4.5) * mm, "end": v(3.8, -4.3) * mm});
            skArc(sketch, "E1215", {"start": v(3.8, -4.3) * mm, "mid": v(3.78, -4.26) * mm, "end": v(3.75, -4.25) * mm});
            skLineSegment(sketch, "E1216", {"start": v(3.75, -4.25) * mm, "end": v(3.05, -4.25) * mm});
            skArc(sketch, "E1217", {"start": v(3.05, -4.25) * mm, "mid": v(3.02, -4.26) * mm, "end": v(3, -4.3) * mm});
            skLineSegment(sketch, "E1218", {"start": v(3, -4.3) * mm, "end": v(3, -4.5) * mm});
            skArc(sketch, "E1219", {"start": v(3, -4.5) * mm, "mid": v(3.02, -4.53) * mm, "end": v(3.05, -4.55) * mm});
            skLineSegment(sketch, "E1220", {"start": v(3.05, -4.55) * mm, "end": v(3.75, -4.55) * mm});
            skArc(sketch, "E1221", {"start": v(3.75, -4.55) * mm, "mid": v(3.78, -4.53) * mm, "end": v(3.8, -4.5) * mm});
            skLineSegment(sketch, "E1222", {"start": v(3.8, -4) * mm, "end": v(3.8, -3.8) * mm});
            skArc(sketch, "E1223", {"start": v(3.8, -3.8) * mm, "mid": v(3.78, -3.76) * mm, "end": v(3.75, -3.75) * mm});
            skLineSegment(sketch, "E1224", {"start": v(3.75, -3.75) * mm, "end": v(3.05, -3.75) * mm});
            skArc(sketch, "E1225", {"start": v(3.05, -3.75) * mm, "mid": v(3.02, -3.76) * mm, "end": v(3, -3.8) * mm});
            skLineSegment(sketch, "E1226", {"start": v(3, -3.8) * mm, "end": v(3, -4) * mm});
            skArc(sketch, "E1227", {"start": v(3, -4) * mm, "mid": v(3.02, -4.03) * mm, "end": v(3.05, -4.05) * mm});
            skLineSegment(sketch, "E1228", {"start": v(3.05, -4.05) * mm, "end": v(3.75, -4.05) * mm});
            skArc(sketch, "E1229", {"start": v(3.75, -4.05) * mm, "mid": v(3.78, -4.03) * mm, "end": v(3.8, -4) * mm});
            skLineSegment(sketch, "E1230", {"start": v(3.8, -3.5) * mm, "end": v(3.8, -3.3) * mm});
            skArc(sketch, "E1231", {"start": v(3.8, -3.3) * mm, "mid": v(3.78, -3.26) * mm, "end": v(3.75, -3.25) * mm});
            skLineSegment(sketch, "E1232", {"start": v(3.75, -3.25) * mm, "end": v(3.05, -3.25) * mm});
            skArc(sketch, "E1233", {"start": v(3.05, -3.25) * mm, "mid": v(3.02, -3.26) * mm, "end": v(3, -3.3) * mm});
            skLineSegment(sketch, "E1234", {"start": v(3, -3.3) * mm, "end": v(3, -3.5) * mm});
            skArc(sketch, "E1235", {"start": v(3, -3.5) * mm, "mid": v(3.02, -3.53) * mm, "end": v(3.05, -3.55) * mm});
            skLineSegment(sketch, "E1236", {"start": v(3.05, -3.55) * mm, "end": v(3.75, -3.55) * mm});
            skArc(sketch, "E1237", {"start": v(3.75, -3.55) * mm, "mid": v(3.78, -3.53) * mm, "end": v(3.8, -3.5) * mm});
            skLineSegment(sketch, "E1238", {"start": v(3.8, -3) * mm, "end": v(3.8, -2.8) * mm});
            skArc(sketch, "E1239", {"start": v(3.8, -2.8) * mm, "mid": v(3.78, -2.76) * mm, "end": v(3.75, -2.75) * mm});
            skLineSegment(sketch, "E1240", {"start": v(3.75, -2.75) * mm, "end": v(3.05, -2.75) * mm});
            skArc(sketch, "E1241", {"start": v(3.05, -2.75) * mm, "mid": v(3.02, -2.76) * mm, "end": v(3, -2.8) * mm});
            skLineSegment(sketch, "E1242", {"start": v(3, -2.8) * mm, "end": v(3, -3) * mm});
            skArc(sketch, "E1243", {"start": v(3, -3) * mm, "mid": v(3.02, -3.03) * mm, "end": v(3.05, -3.05) * mm});
            skLineSegment(sketch, "E1244", {"start": v(3.05, -3.05) * mm, "end": v(3.75, -3.05) * mm});
            skArc(sketch, "E1245", {"start": v(3.75, -3.05) * mm, "mid": v(3.78, -3.03) * mm, "end": v(3.8, -3) * mm});
            skLineSegment(sketch, "E1246", {"start": v(3.8, -2.5) * mm, "end": v(3.8, -2.3) * mm});
            skArc(sketch, "E1247", {"start": v(3.8, -2.3) * mm, "mid": v(3.78, -2.26) * mm, "end": v(3.75, -2.25) * mm});
            skLineSegment(sketch, "E1248", {"start": v(3.75, -2.25) * mm, "end": v(3.05, -2.25) * mm});
            skArc(sketch, "E1249", {"start": v(3.05, -2.25) * mm, "mid": v(3.02, -2.26) * mm, "end": v(3, -2.3) * mm});
            skLineSegment(sketch, "E1250", {"start": v(3, -2.3) * mm, "end": v(3, -2.5) * mm});
            skArc(sketch, "E1251", {"start": v(3, -2.5) * mm, "mid": v(3.02, -2.53) * mm, "end": v(3.05, -2.55) * mm});
            skLineSegment(sketch, "E1252", {"start": v(3.05, -2.55) * mm, "end": v(3.75, -2.55) * mm});
            skArc(sketch, "E1253", {"start": v(3.75, -2.55) * mm, "mid": v(3.78, -2.53) * mm, "end": v(3.8, -2.5) * mm});
            skLineSegment(sketch, "E1254", {"start": v(3.8, -2) * mm, "end": v(3.8, -1.8) * mm});
            skArc(sketch, "E1255", {"start": v(3.8, -1.8) * mm, "mid": v(3.78, -1.76) * mm, "end": v(3.75, -1.75) * mm});
            skLineSegment(sketch, "E1256", {"start": v(3.75, -1.75) * mm, "end": v(3.05, -1.75) * mm});
            skArc(sketch, "E1257", {"start": v(3.05, -1.75) * mm, "mid": v(3.02, -1.76) * mm, "end": v(3, -1.8) * mm});
            skLineSegment(sketch, "E1258", {"start": v(3, -1.8) * mm, "end": v(3, -2) * mm});
            skArc(sketch, "E1259", {"start": v(3, -2) * mm, "mid": v(3.02, -2.03) * mm, "end": v(3.05, -2.05) * mm});
            skLineSegment(sketch, "E1260", {"start": v(3.05, -2.05) * mm, "end": v(3.75, -2.05) * mm});
            skArc(sketch, "E1261", {"start": v(3.75, -2.05) * mm, "mid": v(3.78, -2.03) * mm, "end": v(3.8, -2) * mm});
            skLineSegment(sketch, "E1262", {"start": v(3, -1.3) * mm, "end": v(3, -1.5) * mm});
            skArc(sketch, "E1263", {"start": v(3, -1.5) * mm, "mid": v(3.02, -1.53) * mm, "end": v(3.05, -1.55) * mm});
            skLineSegment(sketch, "E1264", {"start": v(3.05, -1.55) * mm, "end": v(3.75, -1.55) * mm});
            skArc(sketch, "E1265", {"start": v(3.75, -1.55) * mm, "mid": v(3.78, -1.53) * mm, "end": v(3.8, -1.5) * mm});
            skLineSegment(sketch, "E1266", {"start": v(3.8, -1.5) * mm, "end": v(3.8, -1.3) * mm});
            skArc(sketch, "E1267", {"start": v(3.8, -1.3) * mm, "mid": v(3.78, -1.26) * mm, "end": v(3.75, -1.25) * mm});
            skLineSegment(sketch, "E1268", {"start": v(3.75, -1.25) * mm, "end": v(3.05, -1.25) * mm});
            skArc(sketch, "E1269", {"start": v(3.05, -1.25) * mm, "mid": v(3.02, -1.26) * mm, "end": v(3, -1.3) * mm});
            skLineSegment(sketch, "E1270", {"start": v(3, -0.8) * mm, "end": v(3, -1) * mm});
            skArc(sketch, "E1271", {"start": v(3, -1) * mm, "mid": v(3.02, -1.03) * mm, "end": v(3.05, -1.05) * mm});
            skLineSegment(sketch, "E1272", {"start": v(3.05, -1.05) * mm, "end": v(3.75, -1.05) * mm});
            skArc(sketch, "E1273", {"start": v(3.75, -1.05) * mm, "mid": v(3.78, -1.03) * mm, "end": v(3.8, -1) * mm});
            skLineSegment(sketch, "E1274", {"start": v(3.8, -1) * mm, "end": v(3.8, -0.8) * mm});
            skArc(sketch, "E1275", {"start": v(3.8, -0.8) * mm, "mid": v(3.78, -0.76) * mm, "end": v(3.75, -0.75) * mm});
            skLineSegment(sketch, "E1276", {"start": v(3.75, -0.75) * mm, "end": v(3.05, -0.75) * mm});
            skArc(sketch, "E1277", {"start": v(3.05, -0.75) * mm, "mid": v(3.02, -0.76) * mm, "end": v(3, -0.8) * mm});
            skLineSegment(sketch, "E1278", {"start": v(3, -0.3) * mm, "end": v(3, -0.5) * mm});
            skArc(sketch, "E1279", {"start": v(3, -0.5) * mm, "mid": v(3.02, -0.53) * mm, "end": v(3.05, -0.55) * mm});
            skLineSegment(sketch, "E1280", {"start": v(3.05, -0.55) * mm, "end": v(3.75, -0.55) * mm});
            skArc(sketch, "E1281", {"start": v(3.75, -0.55) * mm, "mid": v(3.78, -0.53) * mm, "end": v(3.8, -0.5) * mm});
            skLineSegment(sketch, "E1282", {"start": v(3.8, -0.5) * mm, "end": v(3.8, -0.3) * mm});
            skArc(sketch, "E1283", {"start": v(3.8, -0.3) * mm, "mid": v(3.78, -0.26) * mm, "end": v(3.75, -0.25) * mm});
            skLineSegment(sketch, "E1284", {"start": v(3.75, -0.25) * mm, "end": v(3.05, -0.25) * mm});
            skArc(sketch, "E1285", {"start": v(3.05, -0.25) * mm, "mid": v(3.02, -0.26) * mm, "end": v(3, -0.3) * mm});
            skLineSegment(sketch, "E1286", {"start": v(3, 0.2) * mm, "end": v(3, 0) * mm});
            skArc(sketch, "E1287", {"start": v(3, 0) * mm, "mid": v(3.02, -0.03) * mm, "end": v(3.05, -0.05) * mm});
            skLineSegment(sketch, "E1288", {"start": v(3.05, -0.05) * mm, "end": v(3.75, -0.05) * mm});
            skArc(sketch, "E1289", {"start": v(3.75, -0.05) * mm, "mid": v(3.78, -0.03) * mm, "end": v(3.8, 0) * mm});
            skLineSegment(sketch, "E1290", {"start": v(3.8, 0) * mm, "end": v(3.8, 0.2) * mm});
            skArc(sketch, "E1291", {"start": v(3.8, 0.2) * mm, "mid": v(3.78, 0.24) * mm, "end": v(3.75, 0.25) * mm});
            skLineSegment(sketch, "E1292", {"start": v(3.75, 0.25) * mm, "end": v(3.05, 0.25) * mm});
            skArc(sketch, "E1293", {"start": v(3.05, 0.25) * mm, "mid": v(3.02, 0.24) * mm, "end": v(3, 0.2) * mm});
            skLineSegment(sketch, "E1294", {"start": v(3, 0.7) * mm, "end": v(3, 0.5) * mm});
            skArc(sketch, "E1295", {"start": v(3, 0.5) * mm, "mid": v(3.02, 0.47) * mm, "end": v(3.05, 0.45) * mm});
            skLineSegment(sketch, "E1296", {"start": v(3.05, 0.45) * mm, "end": v(3.75, 0.45) * mm});
            skArc(sketch, "E1297", {"start": v(3.75, 0.45) * mm, "mid": v(3.78, 0.47) * mm, "end": v(3.8, 0.5) * mm});
            skLineSegment(sketch, "E1298", {"start": v(3.8, 0.5) * mm, "end": v(3.8, 0.7) * mm});
            skArc(sketch, "E1299", {"start": v(3.8, 0.7) * mm, "mid": v(3.78, 0.74) * mm, "end": v(3.75, 0.75) * mm});
            skLineSegment(sketch, "E1300", {"start": v(3.75, 0.75) * mm, "end": v(3.05, 0.75) * mm});
            skArc(sketch, "E1301", {"start": v(3.05, 0.75) * mm, "mid": v(3.02, 0.74) * mm, "end": v(3, 0.7) * mm});
            skLineSegment(sketch, "E1302", {"start": v(2.6, 1.9) * mm, "end": v(2.4, 1.9) * mm});
            skArc(sketch, "E1303", {"start": v(2.4, 1.9) * mm, "mid": v(2.37, 1.89) * mm, "end": v(2.35, 1.85) * mm});
            skLineSegment(sketch, "E1304", {"start": v(2.35, 1.85) * mm, "end": v(2.35, 1.15) * mm});
            skArc(sketch, "E1305", {"start": v(2.35, 1.15) * mm, "mid": v(2.37, 1.12) * mm, "end": v(2.4, 1.1) * mm});
            skLineSegment(sketch, "E1306", {"start": v(2.4, 1.1) * mm, "end": v(2.6, 1.1) * mm});
            skArc(sketch, "E1307", {"start": v(2.6, 1.1) * mm, "mid": v(2.63, 1.12) * mm, "end": v(2.65, 1.15) * mm});
            skLineSegment(sketch, "E1308", {"start": v(2.65, 1.15) * mm, "end": v(2.65, 1.85) * mm});
            skArc(sketch, "E1309", {"start": v(2.65, 1.85) * mm, "mid": v(2.63, 1.89) * mm, "end": v(2.6, 1.9) * mm});
            skLineSegment(sketch, "E1310", {"start": v(2.1, 1.9) * mm, "end": v(1.9, 1.9) * mm});
            skArc(sketch, "E1311", {"start": v(1.9, 1.9) * mm, "mid": v(1.87, 1.89) * mm, "end": v(1.85, 1.85) * mm});
            skLineSegment(sketch, "E1312", {"start": v(1.85, 1.85) * mm, "end": v(1.85, 1.15) * mm});
            skArc(sketch, "E1313", {"start": v(1.85, 1.15) * mm, "mid": v(1.87, 1.12) * mm, "end": v(1.9, 1.1) * mm});
            skLineSegment(sketch, "E1314", {"start": v(1.9, 1.1) * mm, "end": v(2.1, 1.1) * mm});
            skArc(sketch, "E1315", {"start": v(2.1, 1.1) * mm, "mid": v(2.13, 1.12) * mm, "end": v(2.15, 1.15) * mm});
            skLineSegment(sketch, "E1316", {"start": v(2.15, 1.15) * mm, "end": v(2.15, 1.85) * mm});
            skArc(sketch, "E1317", {"start": v(2.15, 1.85) * mm, "mid": v(2.13, 1.89) * mm, "end": v(2.1, 1.9) * mm});
            skLineSegment(sketch, "E1318", {"start": v(1.6, 1.9) * mm, "end": v(1.4, 1.9) * mm});
            skArc(sketch, "E1319", {"start": v(1.4, 1.9) * mm, "mid": v(1.37, 1.89) * mm, "end": v(1.35, 1.85) * mm});
            skLineSegment(sketch, "E1320", {"start": v(1.35, 1.85) * mm, "end": v(1.35, 1.15) * mm});
            skArc(sketch, "E1321", {"start": v(1.35, 1.15) * mm, "mid": v(1.37, 1.12) * mm, "end": v(1.4, 1.1) * mm});
            skLineSegment(sketch, "E1322", {"start": v(1.4, 1.1) * mm, "end": v(1.6, 1.1) * mm});
            skArc(sketch, "E1323", {"start": v(1.6, 1.1) * mm, "mid": v(1.63, 1.12) * mm, "end": v(1.65, 1.15) * mm});
            skLineSegment(sketch, "E1324", {"start": v(1.65, 1.15) * mm, "end": v(1.65, 1.85) * mm});
            skArc(sketch, "E1325", {"start": v(1.65, 1.85) * mm, "mid": v(1.63, 1.89) * mm, "end": v(1.6, 1.9) * mm});
            skLineSegment(sketch, "E1326", {"start": v(1.1, 1.9) * mm, "end": v(0.9, 1.9) * mm});
            skArc(sketch, "E1327", {"start": v(0.9, 1.9) * mm, "mid": v(0.87, 1.89) * mm, "end": v(0.85, 1.85) * mm});
            skLineSegment(sketch, "E1328", {"start": v(0.85, 1.85) * mm, "end": v(0.85, 1.15) * mm});
            skArc(sketch, "E1329", {"start": v(0.85, 1.15) * mm, "mid": v(0.87, 1.12) * mm, "end": v(0.9, 1.1) * mm});
            skLineSegment(sketch, "E1330", {"start": v(0.9, 1.1) * mm, "end": v(1.1, 1.1) * mm});
            skArc(sketch, "E1331", {"start": v(1.1, 1.1) * mm, "mid": v(1.13, 1.12) * mm, "end": v(1.15, 1.15) * mm});
            skLineSegment(sketch, "E1332", {"start": v(1.15, 1.15) * mm, "end": v(1.15, 1.85) * mm});
            skArc(sketch, "E1333", {"start": v(1.15, 1.85) * mm, "mid": v(1.13, 1.89) * mm, "end": v(1.1, 1.9) * mm});
            skLineSegment(sketch, "E1334", {"start": v(0.6, 1.9) * mm, "end": v(0.4, 1.9) * mm});
            skArc(sketch, "E1335", {"start": v(0.4, 1.9) * mm, "mid": v(0.37, 1.89) * mm, "end": v(0.35, 1.85) * mm});
            skLineSegment(sketch, "E1336", {"start": v(0.35, 1.85) * mm, "end": v(0.35, 1.15) * mm});
            skArc(sketch, "E1337", {"start": v(0.35, 1.15) * mm, "mid": v(0.37, 1.12) * mm, "end": v(0.4, 1.1) * mm});
            skLineSegment(sketch, "E1338", {"start": v(0.4, 1.1) * mm, "end": v(0.6, 1.1) * mm});
            skArc(sketch, "E1339", {"start": v(0.6, 1.1) * mm, "mid": v(0.63, 1.12) * mm, "end": v(0.65, 1.15) * mm});
            skLineSegment(sketch, "E1340", {"start": v(0.65, 1.15) * mm, "end": v(0.65, 1.85) * mm});
            skArc(sketch, "E1341", {"start": v(0.65, 1.85) * mm, "mid": v(0.63, 1.89) * mm, "end": v(0.6, 1.9) * mm});
            skLineSegment(sketch, "E1342", {"start": v(0.1, 1.9) * mm, "end": v(-0.1, 1.9) * mm});
            skArc(sketch, "E1343", {"start": v(-0.1, 1.9) * mm, "mid": v(-0.13, 1.89) * mm, "end": v(-0.15, 1.85) * mm});
            skLineSegment(sketch, "E1344", {"start": v(-0.15, 1.85) * mm, "end": v(-0.15, 1.15) * mm});
            skArc(sketch, "E1345", {"start": v(-0.15, 1.15) * mm, "mid": v(-0.13, 1.12) * mm, "end": v(-0.1, 1.1) * mm});
            skLineSegment(sketch, "E1346", {"start": v(-0.1, 1.1) * mm, "end": v(0.1, 1.1) * mm});
            skArc(sketch, "E1347", {"start": v(0.1, 1.1) * mm, "mid": v(0.13, 1.12) * mm, "end": v(0.15, 1.15) * mm});
            skLineSegment(sketch, "E1348", {"start": v(0.15, 1.15) * mm, "end": v(0.15, 1.85) * mm});
            skArc(sketch, "E1349", {"start": v(0.15, 1.85) * mm, "mid": v(0.13, 1.89) * mm, "end": v(0.1, 1.9) * mm});
            skLineSegment(sketch, "E1350", {"start": v(-0.6, 1.1) * mm, "end": v(-0.4, 1.1) * mm});
            skArc(sketch, "E1351", {"start": v(-0.4, 1.1) * mm, "mid": v(-0.37, 1.12) * mm, "end": v(-0.35, 1.15) * mm});
            skLineSegment(sketch, "E1352", {"start": v(-0.35, 1.15) * mm, "end": v(-0.35, 1.85) * mm});
            skArc(sketch, "E1353", {"start": v(-0.35, 1.85) * mm, "mid": v(-0.37, 1.89) * mm, "end": v(-0.4, 1.9) * mm});
            skLineSegment(sketch, "E1354", {"start": v(-0.4, 1.9) * mm, "end": v(-0.6, 1.9) * mm});
            skArc(sketch, "E1355", {"start": v(-0.6, 1.9) * mm, "mid": v(-0.63, 1.89) * mm, "end": v(-0.65, 1.85) * mm});
            skLineSegment(sketch, "E1356", {"start": v(-0.65, 1.85) * mm, "end": v(-0.65, 1.15) * mm});
            skArc(sketch, "E1357", {"start": v(-0.65, 1.15) * mm, "mid": v(-0.63, 1.12) * mm, "end": v(-0.6, 1.1) * mm});
            skLineSegment(sketch, "E1358", {"start": v(-1.1, 1.1) * mm, "end": v(-0.9, 1.1) * mm});
            skArc(sketch, "E1359", {"start": v(-0.9, 1.1) * mm, "mid": v(-0.87, 1.12) * mm, "end": v(-0.85, 1.15) * mm});
            skLineSegment(sketch, "E1360", {"start": v(-0.85, 1.15) * mm, "end": v(-0.85, 1.85) * mm});
            skArc(sketch, "E1361", {"start": v(-0.85, 1.85) * mm, "mid": v(-0.87, 1.89) * mm, "end": v(-0.9, 1.9) * mm});
            skLineSegment(sketch, "E1362", {"start": v(-0.9, 1.9) * mm, "end": v(-1.1, 1.9) * mm});
            skArc(sketch, "E1363", {"start": v(-1.1, 1.9) * mm, "mid": v(-1.13, 1.89) * mm, "end": v(-1.15, 1.85) * mm});
            skLineSegment(sketch, "E1364", {"start": v(-1.15, 1.85) * mm, "end": v(-1.15, 1.15) * mm});
            skArc(sketch, "E1365", {"start": v(-1.15, 1.15) * mm, "mid": v(-1.13, 1.12) * mm, "end": v(-1.1, 1.1) * mm});
            skLineSegment(sketch, "E1366", {"start": v(-1.6, 1.1) * mm, "end": v(-1.4, 1.1) * mm});
            skArc(sketch, "E1367", {"start": v(-1.4, 1.1) * mm, "mid": v(-1.37, 1.12) * mm, "end": v(-1.35, 1.15) * mm});
            skLineSegment(sketch, "E1368", {"start": v(-1.35, 1.15) * mm, "end": v(-1.35, 1.85) * mm});
            skArc(sketch, "E1369", {"start": v(-1.35, 1.85) * mm, "mid": v(-1.37, 1.89) * mm, "end": v(-1.4, 1.9) * mm});
            skLineSegment(sketch, "E1370", {"start": v(-1.4, 1.9) * mm, "end": v(-1.6, 1.9) * mm});
            skArc(sketch, "E1371", {"start": v(-1.6, 1.9) * mm, "mid": v(-1.63, 1.89) * mm, "end": v(-1.65, 1.85) * mm});
            skLineSegment(sketch, "E1372", {"start": v(-1.65, 1.85) * mm, "end": v(-1.65, 1.15) * mm});
            skArc(sketch, "E1373", {"start": v(-1.65, 1.15) * mm, "mid": v(-1.63, 1.12) * mm, "end": v(-1.6, 1.1) * mm});
            skLineSegment(sketch, "E1374", {"start": v(-2.1, 1.1) * mm, "end": v(-1.9, 1.1) * mm});
            skArc(sketch, "E1375", {"start": v(-1.9, 1.1) * mm, "mid": v(-1.87, 1.12) * mm, "end": v(-1.85, 1.15) * mm});
            skLineSegment(sketch, "E1376", {"start": v(-1.85, 1.15) * mm, "end": v(-1.85, 1.85) * mm});
            skArc(sketch, "E1377", {"start": v(-1.85, 1.85) * mm, "mid": v(-1.87, 1.89) * mm, "end": v(-1.9, 1.9) * mm});
            skLineSegment(sketch, "E1378", {"start": v(-1.9, 1.9) * mm, "end": v(-2.1, 1.9) * mm});
            skArc(sketch, "E1379", {"start": v(-2.1, 1.9) * mm, "mid": v(-2.13, 1.89) * mm, "end": v(-2.15, 1.85) * mm});
            skLineSegment(sketch, "E1380", {"start": v(-2.15, 1.85) * mm, "end": v(-2.15, 1.15) * mm});
            skArc(sketch, "E1381", {"start": v(-2.15, 1.15) * mm, "mid": v(-2.13, 1.12) * mm, "end": v(-2.1, 1.1) * mm});
            skLineSegment(sketch, "E1382", {"start": v(-2.6, 1.1) * mm, "end": v(-2.4, 1.1) * mm});
            skArc(sketch, "E1383", {"start": v(-2.4, 1.1) * mm, "mid": v(-2.37, 1.12) * mm, "end": v(-2.35, 1.15) * mm});
            skLineSegment(sketch, "E1384", {"start": v(-2.35, 1.15) * mm, "end": v(-2.35, 1.85) * mm});
            skArc(sketch, "E1385", {"start": v(-2.35, 1.85) * mm, "mid": v(-2.37, 1.89) * mm, "end": v(-2.4, 1.9) * mm});
            skLineSegment(sketch, "E1386", {"start": v(-2.4, 1.9) * mm, "end": v(-2.6, 1.9) * mm});
            skArc(sketch, "E1387", {"start": v(-2.6, 1.9) * mm, "mid": v(-2.63, 1.89) * mm, "end": v(-2.65, 1.85) * mm});
            skLineSegment(sketch, "E1388", {"start": v(-2.65, 1.85) * mm, "end": v(-2.65, 1.15) * mm});
            skArc(sketch, "E1389", {"start": v(-2.65, 1.15) * mm, "mid": v(-2.63, 1.12) * mm, "end": v(-2.6, 1.1) * mm});
            skLineSegment(sketch, "E1390", {"start": v(2.94, -8.5) * mm, "end": v(2.94, -9.6) * mm});
            skArc(sketch, "E1391", {"start": v(2.94, -9.6) * mm, "mid": v(2.96, -9.64) * mm, "end": v(3, -9.65) * mm});
            skLineSegment(sketch, "E1392", {"start": v(3, -9.65) * mm, "end": v(3.45, -9.65) * mm});
            skArc(sketch, "E1393", {"start": v(3.45, -9.65) * mm, "mid": v(3.48, -9.64) * mm, "end": v(3.5, -9.6) * mm});
            skLineSegment(sketch, "E1394", {"start": v(3.5, -9.6) * mm, "end": v(3.5, -8.5) * mm});
            skArc(sketch, "E1395", {"start": v(3.5, -8.5) * mm, "mid": v(3.48, -8.46) * mm, "end": v(3.45, -8.45) * mm});
            skLineSegment(sketch, "E1396", {"start": v(3.45, -8.45) * mm, "end": v(3, -8.45) * mm});
            skArc(sketch, "E1397", {"start": v(3, -8.45) * mm, "mid": v(2.96, -8.46) * mm, "end": v(2.94, -8.5) * mm});
            skLineSegment(sketch, "E1398", {"start": v(2, -8.5) * mm, "end": v(2, -9.6) * mm});
            skArc(sketch, "E1399", {"start": v(2, -9.6) * mm, "mid": v(2, -9.64) * mm, "end": v(2.04, -9.65) * mm});
            skLineSegment(sketch, "E1400", {"start": v(2.04, -9.65) * mm, "end": v(2.5, -9.65) * mm});
            skArc(sketch, "E1401", {"start": v(2.5, -9.65) * mm, "mid": v(2.53, -9.64) * mm, "end": v(2.55, -9.6) * mm});
            skLineSegment(sketch, "E1402", {"start": v(2.55, -9.6) * mm, "end": v(2.55, -8.5) * mm});
            skArc(sketch, "E1403", {"start": v(2.55, -8.5) * mm, "mid": v(2.53, -8.46) * mm, "end": v(2.5, -8.45) * mm});
            skLineSegment(sketch, "E1404", {"start": v(2.5, -8.45) * mm, "end": v(2.04, -8.45) * mm});
            skArc(sketch, "E1405", {"start": v(2.04, -8.45) * mm, "mid": v(2, -8.46) * mm, "end": v(2, -8.5) * mm});
            skLineSegment(sketch, "E1406", {"start": v(1.04, -8.5) * mm, "end": v(1.04, -9.6) * mm});
            skArc(sketch, "E1407", {"start": v(1.04, -9.6) * mm, "mid": v(1.06, -9.64) * mm, "end": v(1.1, -9.65) * mm});
            skLineSegment(sketch, "E1408", {"start": v(1.1, -9.65) * mm, "end": v(1.55, -9.65) * mm});
            skArc(sketch, "E1409", {"start": v(1.55, -9.65) * mm, "mid": v(1.58, -9.64) * mm, "end": v(1.6, -9.6) * mm});
            skLineSegment(sketch, "E1410", {"start": v(1.6, -9.6) * mm, "end": v(1.6, -8.5) * mm});
            skArc(sketch, "E1411", {"start": v(1.6, -8.5) * mm, "mid": v(1.58, -8.46) * mm, "end": v(1.55, -8.45) * mm});
            skLineSegment(sketch, "E1412", {"start": v(1.55, -8.45) * mm, "end": v(1.1, -8.45) * mm});
            skArc(sketch, "E1413", {"start": v(1.1, -8.45) * mm, "mid": v(1.06, -8.46) * mm, "end": v(1.04, -8.5) * mm});
            skLineSegment(sketch, "E1414", {"start": v(1.04, -11.1) * mm, "end": v(1.04, -12.2) * mm});
            skArc(sketch, "E1415", {"start": v(1.04, -12.2) * mm, "mid": v(1.06, -12.24) * mm, "end": v(1.1, -12.25) * mm});
            skLineSegment(sketch, "E1416", {"start": v(1.1, -12.25) * mm, "end": v(1.55, -12.25) * mm});
            skArc(sketch, "E1417", {"start": v(1.55, -12.25) * mm, "mid": v(1.58, -12.24) * mm, "end": v(1.6, -12.2) * mm});
            skLineSegment(sketch, "E1418", {"start": v(1.6, -12.2) * mm, "end": v(1.6, -11.1) * mm});
            skArc(sketch, "E1419", {"start": v(1.6, -11.1) * mm, "mid": v(1.58, -11.06) * mm, "end": v(1.55, -11.05) * mm});
            skLineSegment(sketch, "E1420", {"start": v(1.55, -11.05) * mm, "end": v(1.1, -11.05) * mm});
            skArc(sketch, "E1421", {"start": v(1.1, -11.05) * mm, "mid": v(1.06, -11.06) * mm, "end": v(1.04, -11.1) * mm});
            skLineSegment(sketch, "E1422", {"start": v(2.94, -11.1) * mm, "end": v(2.94, -12.2) * mm});
            skArc(sketch, "E1423", {"start": v(2.94, -12.2) * mm, "mid": v(2.96, -12.24) * mm, "end": v(3, -12.25) * mm});
            skLineSegment(sketch, "E1424", {"start": v(3, -12.25) * mm, "end": v(3.45, -12.25) * mm});
            skArc(sketch, "E1425", {"start": v(3.45, -12.25) * mm, "mid": v(3.48, -12.24) * mm, "end": v(3.5, -12.2) * mm});
            skLineSegment(sketch, "E1426", {"start": v(3.5, -12.2) * mm, "end": v(3.5, -11.1) * mm});
            skArc(sketch, "E1427", {"start": v(3.5, -11.1) * mm, "mid": v(3.48, -11.06) * mm, "end": v(3.45, -11.05) * mm});
            skLineSegment(sketch, "E1428", {"start": v(3.45, -11.05) * mm, "end": v(3, -11.05) * mm});
            skArc(sketch, "E1429", {"start": v(3, -11.05) * mm, "mid": v(2.96, -11.06) * mm, "end": v(2.94, -11.1) * mm});
            skLineSegment(sketch, "E1430", {"start": v(6.07, -8.91) * mm, "end": v(5.43, -8.91) * mm});
            skArc(sketch, "E1431", {"start": v(5.43, -8.91) * mm, "mid": v(5.39, -8.93) * mm, "end": v(5.37, -8.98) * mm});
            skLineSegment(sketch, "E1432", {"start": v(5.37, -8.98) * mm, "end": v(5.37, -9.61) * mm});
            skArc(sketch, "E1433", {"start": v(5.37, -9.61) * mm, "mid": v(5.39, -9.66) * mm, "end": v(5.43, -9.68) * mm});
            skLineSegment(sketch, "E1434", {"start": v(5.43, -9.68) * mm, "end": v(6.07, -9.68) * mm});
            skArc(sketch, "E1435", {"start": v(6.07, -9.68) * mm, "mid": v(6.11, -9.66) * mm, "end": v(6.13, -9.61) * mm});
            skLineSegment(sketch, "E1436", {"start": v(6.13, -9.61) * mm, "end": v(6.13, -8.98) * mm});
            skArc(sketch, "E1437", {"start": v(6.13, -8.98) * mm, "mid": v(6.11, -8.93) * mm, "end": v(6.07, -8.91) * mm});
            skLineSegment(sketch, "E1438", {"start": v(4.57, -8.91) * mm, "end": v(3.93, -8.91) * mm});
            skArc(sketch, "E1439", {"start": v(3.93, -8.91) * mm, "mid": v(3.89, -8.93) * mm, "end": v(3.87, -8.98) * mm});
            skLineSegment(sketch, "E1440", {"start": v(3.87, -8.98) * mm, "end": v(3.87, -9.61) * mm});
            skArc(sketch, "E1441", {"start": v(3.87, -9.61) * mm, "mid": v(3.89, -9.66) * mm, "end": v(3.93, -9.68) * mm});
            skLineSegment(sketch, "E1442", {"start": v(3.93, -9.68) * mm, "end": v(4.57, -9.68) * mm});
            skArc(sketch, "E1443", {"start": v(4.57, -9.68) * mm, "mid": v(4.61, -9.66) * mm, "end": v(4.63, -9.61) * mm});
            skLineSegment(sketch, "E1444", {"start": v(4.63, -9.61) * mm, "end": v(4.63, -8.98) * mm});
            skArc(sketch, "E1445", {"start": v(4.63, -8.98) * mm, "mid": v(4.61, -8.93) * mm, "end": v(4.57, -8.91) * mm});
            skLineSegment(sketch, "E1446", {"start": v(4.27, -7.21) * mm, "end": v(3.63, -7.21) * mm});
            skArc(sketch, "E1447", {"start": v(3.63, -7.21) * mm, "mid": v(3.59, -7.23) * mm, "end": v(3.57, -7.28) * mm});
            skLineSegment(sketch, "E1448", {"start": v(3.57, -7.28) * mm, "end": v(3.57, -7.91) * mm});
            skArc(sketch, "E1449", {"start": v(3.57, -7.91) * mm, "mid": v(3.59, -7.96) * mm, "end": v(3.63, -7.98) * mm});
            skLineSegment(sketch, "E1450", {"start": v(3.63, -7.98) * mm, "end": v(4.27, -7.98) * mm});
            skArc(sketch, "E1451", {"start": v(4.27, -7.98) * mm, "mid": v(4.31, -7.96) * mm, "end": v(4.33, -7.91) * mm});
            skLineSegment(sketch, "E1452", {"start": v(4.33, -7.91) * mm, "end": v(4.33, -7.28) * mm});
            skArc(sketch, "E1453", {"start": v(4.33, -7.28) * mm, "mid": v(4.31, -7.23) * mm, "end": v(4.27, -7.21) * mm});
            skLineSegment(sketch, "E1454", {"start": v(2.77, -7.21) * mm, "end": v(2.13, -7.21) * mm});
            skArc(sketch, "E1455", {"start": v(2.13, -7.21) * mm, "mid": v(2.09, -7.23) * mm, "end": v(2.07, -7.28) * mm});
            skLineSegment(sketch, "E1456", {"start": v(2.07, -7.28) * mm, "end": v(2.07, -7.91) * mm});
            skArc(sketch, "E1457", {"start": v(2.07, -7.91) * mm, "mid": v(2.09, -7.96) * mm, "end": v(2.13, -7.98) * mm});
            skLineSegment(sketch, "E1458", {"start": v(2.13, -7.98) * mm, "end": v(2.77, -7.98) * mm});
            skArc(sketch, "E1459", {"start": v(2.77, -7.98) * mm, "mid": v(2.81, -7.96) * mm, "end": v(2.83, -7.91) * mm});
            skLineSegment(sketch, "E1460", {"start": v(2.83, -7.91) * mm, "end": v(2.83, -7.28) * mm});
            skArc(sketch, "E1461", {"start": v(2.83, -7.28) * mm, "mid": v(2.81, -7.23) * mm, "end": v(2.77, -7.21) * mm});
            skLineSegment(sketch, "E1462", {"start": v(-4.27, -7.98) * mm, "end": v(-3.63, -7.98) * mm});
            skArc(sketch, "E1463", {"start": v(-3.63, -7.98) * mm, "mid": v(-3.59, -7.96) * mm, "end": v(-3.57, -7.91) * mm});
            skLineSegment(sketch, "E1464", {"start": v(-3.57, -7.91) * mm, "end": v(-3.57, -7.28) * mm});
            skArc(sketch, "E1465", {"start": v(-3.57, -7.28) * mm, "mid": v(-3.59, -7.23) * mm, "end": v(-3.63, -7.21) * mm});
            skLineSegment(sketch, "E1466", {"start": v(-3.63, -7.21) * mm, "end": v(-4.27, -7.21) * mm});
            skArc(sketch, "E1467", {"start": v(-4.27, -7.21) * mm, "mid": v(-4.31, -7.23) * mm, "end": v(-4.33, -7.28) * mm});
            skLineSegment(sketch, "E1468", {"start": v(-4.33, -7.28) * mm, "end": v(-4.33, -7.91) * mm});
            skArc(sketch, "E1469", {"start": v(-4.33, -7.91) * mm, "mid": v(-4.31, -7.96) * mm, "end": v(-4.27, -7.98) * mm});
            skLineSegment(sketch, "E1470", {"start": v(-2.77, -7.98) * mm, "end": v(-2.13, -7.98) * mm});
            skArc(sketch, "E1471", {"start": v(-2.13, -7.98) * mm, "mid": v(-2.09, -7.96) * mm, "end": v(-2.07, -7.91) * mm});
            skLineSegment(sketch, "E1472", {"start": v(-2.07, -7.91) * mm, "end": v(-2.07, -7.28) * mm});
            skArc(sketch, "E1473", {"start": v(-2.07, -7.28) * mm, "mid": v(-2.09, -7.23) * mm, "end": v(-2.13, -7.21) * mm});
            skLineSegment(sketch, "E1474", {"start": v(-2.13, -7.21) * mm, "end": v(-2.77, -7.21) * mm});
            skArc(sketch, "E1475", {"start": v(-2.77, -7.21) * mm, "mid": v(-2.81, -7.23) * mm, "end": v(-2.83, -7.28) * mm});
            skLineSegment(sketch, "E1476", {"start": v(-2.83, -7.28) * mm, "end": v(-2.83, -7.91) * mm});
            skArc(sketch, "E1477", {"start": v(-2.83, -7.91) * mm, "mid": v(-2.81, -7.96) * mm, "end": v(-2.77, -7.98) * mm});
            skLineSegment(sketch, "E1478", {"start": v(-5.8, 7.32) * mm, "end": v(-6.11, 6.77) * mm});
            skArc(sketch, "E1479", {"start": v(-6.11, 6.77) * mm, "mid": v(-6.12, 6.72) * mm, "end": v(-6.09, 6.68) * mm});
            skLineSegment(sketch, "E1480", {"start": v(-6.09, 6.68) * mm, "end": v(-5.54, 6.36) * mm});
            skArc(sketch, "E1481", {"start": v(-5.54, 6.36) * mm, "mid": v(-5.5, 6.36) * mm, "end": v(-5.45, 6.39) * mm});
            skLineSegment(sketch, "E1482", {"start": v(-5.45, 6.39) * mm, "end": v(-5.14, 6.93) * mm});
            skArc(sketch, "E1483", {"start": v(-5.14, 6.93) * mm, "mid": v(-5.13, 6.98) * mm, "end": v(-5.16, 7.03) * mm});
            skLineSegment(sketch, "E1484", {"start": v(-5.16, 7.03) * mm, "end": v(-5.7, 7.34) * mm});
            skArc(sketch, "E1485", {"start": v(-5.7, 7.34) * mm, "mid": v(-5.76, 7.35) * mm, "end": v(-5.8, 7.32) * mm});
            skLineSegment(sketch, "E1486", {"start": v(-6.55, 6.02) * mm, "end": v(-6.86, 5.47) * mm});
            skArc(sketch, "E1487", {"start": v(-6.86, 5.47) * mm, "mid": v(-6.87, 5.42) * mm, "end": v(-6.84, 5.38) * mm});
            skLineSegment(sketch, "E1488", {"start": v(-6.84, 5.38) * mm, "end": v(-6.3, 5.06) * mm});
            skArc(sketch, "E1489", {"start": v(-6.3, 5.06) * mm, "mid": v(-6.24, 5.06) * mm, "end": v(-6.2, 5.09) * mm});
            skLineSegment(sketch, "E1490", {"start": v(-6.2, 5.09) * mm, "end": v(-5.89, 5.63) * mm});
            skArc(sketch, "E1491", {"start": v(-5.89, 5.63) * mm, "mid": v(-5.88, 5.69) * mm, "end": v(-5.91, 5.73) * mm});
            skLineSegment(sketch, "E1492", {"start": v(-5.91, 5.73) * mm, "end": v(-6.46, 6.04) * mm});
            skArc(sketch, "E1493", {"start": v(-6.46, 6.04) * mm, "mid": v(-6.5, 6.05) * mm, "end": v(-6.55, 6.02) * mm});
            skLineSegment(sketch, "E1494", {"start": v(6.86, 5.47) * mm, "end": v(6.55, 6.02) * mm});
            skArc(sketch, "E1495", {"start": v(6.55, 6.02) * mm, "mid": v(6.5, 6.05) * mm, "end": v(6.46, 6.04) * mm});
            skLineSegment(sketch, "E1496", {"start": v(6.46, 6.04) * mm, "end": v(5.91, 5.73) * mm});
            skArc(sketch, "E1497", {"start": v(5.91, 5.73) * mm, "mid": v(5.88, 5.69) * mm, "end": v(5.89, 5.63) * mm});
            skLineSegment(sketch, "E1498", {"start": v(5.89, 5.63) * mm, "end": v(6.2, 5.09) * mm});
            skArc(sketch, "E1499", {"start": v(6.2, 5.09) * mm, "mid": v(6.24, 5.06) * mm, "end": v(6.3, 5.06) * mm});
            skLineSegment(sketch, "E1500", {"start": v(6.3, 5.06) * mm, "end": v(6.84, 5.38) * mm});
            skArc(sketch, "E1501", {"start": v(6.84, 5.38) * mm, "mid": v(6.87, 5.42) * mm, "end": v(6.86, 5.47) * mm});
            skLineSegment(sketch, "E1502", {"start": v(6.11, 6.77) * mm, "end": v(5.8, 7.32) * mm});
            skArc(sketch, "E1503", {"start": v(5.8, 7.32) * mm, "mid": v(5.76, 7.35) * mm, "end": v(5.7, 7.34) * mm});
            skLineSegment(sketch, "E1504", {"start": v(5.7, 7.34) * mm, "end": v(5.16, 7.03) * mm});
            skArc(sketch, "E1505", {"start": v(5.16, 7.03) * mm, "mid": v(5.13, 6.98) * mm, "end": v(5.14, 6.93) * mm});
            skLineSegment(sketch, "E1506", {"start": v(5.14, 6.93) * mm, "end": v(5.45, 6.39) * mm});
            skArc(sketch, "E1507", {"start": v(5.45, 6.39) * mm, "mid": v(5.5, 6.36) * mm, "end": v(5.54, 6.36) * mm});
            skLineSegment(sketch, "E1508", {"start": v(5.54, 6.36) * mm, "end": v(6.09, 6.68) * mm});
            skArc(sketch, "E1509", {"start": v(6.09, 6.68) * mm, "mid": v(6.12, 6.72) * mm, "end": v(6.11, 6.77) * mm});
            skLineSegment(sketch, "E1510", {"start": v(19.02, 6.17) * mm, "end": v(15.6, 5.05) * mm});
            skArc(sketch, "E1511", {"start": v(15.56, 5.17) * mm, "mid": v(15.48, 5) * mm, "end": v(15.64, 4.93) * mm});
            skArc(sketch, "E1512", {"start": v(19.06, 6.05) * mm, "mid": v(19.14, 6.21) * mm, "end": v(18.98, 6.3) * mm});
            skLineSegment(sketch, "E1513", {"start": v(15.6, 5.05) * mm, "end": v(15.4, 4.95) * mm});
            skArc(sketch, "E1514", {"start": v(15.34, 5.06) * mm, "mid": v(15.29, 4.89) * mm, "end": v(15.46, 4.83) * mm});
            skArc(sketch, "E1515", {"start": v(15.66, 4.94) * mm, "mid": v(15.71, 5.1) * mm, "end": v(15.55, 5.16) * mm});
            skLineSegment(sketch, "E1516", {"start": v(15.4, 4.95) * mm, "end": v(15.21, 4.83) * mm});
            skArc(sketch, "E1517", {"start": v(15.15, 4.93) * mm, "mid": v(15.1, 4.76) * mm, "end": v(15.28, 4.72) * mm});
            skArc(sketch, "E1518", {"start": v(15.47, 4.84) * mm, "mid": v(15.5, 5.01) * mm, "end": v(15.33, 5.05) * mm});
            skLineSegment(sketch, "E1519", {"start": v(15.21, 4.83) * mm, "end": v(15.04, 4.69) * mm});
            skArc(sketch, "E1520", {"start": v(14.96, 4.79) * mm, "mid": v(14.94, 4.61) * mm, "end": v(15.12, 4.6) * mm});
            skArc(sketch, "E1521", {"start": v(15.3, 4.73) * mm, "mid": v(15.31, 4.9) * mm, "end": v(15.14, 4.92) * mm});
            skLineSegment(sketch, "E1522", {"start": v(15.04, 4.69) * mm, "end": v(14.88, 4.54) * mm});
            skArc(sketch, "E1523", {"start": v(14.8, 4.63) * mm, "mid": v(14.8, 4.45) * mm, "end": v(14.97, 4.45) * mm});
            skArc(sketch, "E1524", {"start": v(15.13, 4.6) * mm, "mid": v(15.13, 4.78) * mm, "end": v(14.95, 4.78) * mm});
            skLineSegment(sketch, "E1525", {"start": v(14.88, 4.54) * mm, "end": v(14.74, 4.37) * mm});
            skArc(sketch, "E1526", {"start": v(14.65, 4.45) * mm, "mid": v(14.66, 4.28) * mm, "end": v(14.84, 4.3) * mm});
            skArc(sketch, "E1527", {"start": v(14.98, 4.46) * mm, "mid": v(14.97, 4.63) * mm, "end": v(14.79, 4.62) * mm});
            skLineSegment(sketch, "E1528", {"start": v(14.74, 4.37) * mm, "end": v(14.62, 4.2) * mm});
            skArc(sketch, "E1529", {"start": v(14.52, 4.27) * mm, "mid": v(14.55, 4.1) * mm, "end": v(14.72, 4.12) * mm});
            skArc(sketch, "E1530", {"start": v(14.85, 4.3) * mm, "mid": v(14.82, 4.47) * mm, "end": v(14.64, 4.44) * mm});
            skLineSegment(sketch, "E1531", {"start": v(14.62, 4.2) * mm, "end": v(14.51, 4) * mm});
            skArc(sketch, "E1532", {"start": v(14.4, 4.07) * mm, "mid": v(14.45, 3.9) * mm, "end": v(14.62, 3.94) * mm});
            skArc(sketch, "E1533", {"start": v(14.73, 4.13) * mm, "mid": v(14.68, 4.3) * mm, "end": v(14.51, 4.26) * mm});
            skLineSegment(sketch, "E1534", {"start": v(14.51, 4) * mm, "end": v(14.43, 3.8) * mm});
            skArc(sketch, "E1535", {"start": v(14.31, 3.86) * mm, "mid": v(14.38, 3.7) * mm, "end": v(14.54, 3.76) * mm});
            skArc(sketch, "E1536", {"start": v(14.63, 3.96) * mm, "mid": v(14.56, 4.12) * mm, "end": v(14.4, 4.06) * mm});
            skLineSegment(sketch, "E1537", {"start": v(14.43, 3.8) * mm, "end": v(14.36, 3.6) * mm});
            skArc(sketch, "E1538", {"start": v(14.24, 3.64) * mm, "mid": v(14.32, 3.48) * mm, "end": v(14.48, 3.56) * mm});
            skArc(sketch, "E1539", {"start": v(14.54, 3.77) * mm, "mid": v(14.47, 3.93) * mm, "end": v(14.3, 3.85) * mm});
            skLineSegment(sketch, "E1540", {"start": v(14.36, 3.6) * mm, "end": v(14.3, 3.4) * mm});
            skArc(sketch, "E1541", {"start": v(14.19, 3.42) * mm, "mid": v(14.28, 3.27) * mm, "end": v(14.43, 3.36) * mm});
            skArc(sketch, "E1542", {"start": v(14.48, 3.57) * mm, "mid": v(14.39, 3.72) * mm, "end": v(14.24, 3.63) * mm});
            skLineSegment(sketch, "E1543", {"start": v(14.3, 3.4) * mm, "end": v(14.28, 3.18) * mm});
            skArc(sketch, "E1544", {"start": v(14.16, 3.2) * mm, "mid": v(14.26, 3.05) * mm, "end": v(14.4, 3.16) * mm});
            skArc(sketch, "E1545", {"start": v(14.43, 3.38) * mm, "mid": v(14.32, 3.52) * mm, "end": v(14.18, 3.4) * mm});
            skLineSegment(sketch, "E1546", {"start": v(14.28, 3.18) * mm, "end": v(14.27, 2.95) * mm});
            skArc(sketch, "E1547", {"start": v(14.15, 2.96) * mm, "mid": v(14.27, 2.83) * mm, "end": v(14.4, 2.95) * mm});
            skArc(sketch, "E1548", {"start": v(14.4, 3.17) * mm, "mid": v(14.28, 3.3) * mm, "end": v(14.16, 3.18) * mm});
            skLineSegment(sketch, "E1549", {"start": v(14.27, 2.95) * mm, "end": v(14.29, 2.73) * mm});
            skArc(sketch, "E1550", {"start": v(14.16, 2.72) * mm, "mid": v(14.3, 2.6) * mm, "end": v(14.41, 2.74) * mm});
            skArc(sketch, "E1551", {"start": v(14.4, 2.96) * mm, "mid": v(14.27, 3.08) * mm, "end": v(14.15, 2.95) * mm});
            skLineSegment(sketch, "E1552", {"start": v(14.29, 2.73) * mm, "end": v(14.33, 2.5) * mm});
            skArc(sketch, "E1553", {"start": v(14.2, 2.49) * mm, "mid": v(14.35, 2.39) * mm, "end": v(14.45, 2.53) * mm});
            skArc(sketch, "E1554", {"start": v(14.41, 2.75) * mm, "mid": v(14.27, 2.86) * mm, "end": v(14.17, 2.71) * mm});
            skLineSegment(sketch, "E1555", {"start": v(14.33, 2.5) * mm, "end": v(14.38, 2.3) * mm});
            skArc(sketch, "E1556", {"start": v(14.26, 2.27) * mm, "mid": v(14.42, 2.18) * mm, "end": v(14.5, 2.33) * mm});
            skArc(sketch, "E1557", {"start": v(14.45, 2.54) * mm, "mid": v(14.3, 2.63) * mm, "end": v(14.2, 2.48) * mm});
            skLineSegment(sketch, "E1558", {"start": v(14.38, 2.3) * mm, "end": v(14.47, 2.07) * mm});
            skArc(sketch, "E1559", {"start": v(14.35, 2.03) * mm, "mid": v(14.52, 1.96) * mm, "end": v(14.59, 2.12) * mm});
            skArc(sketch, "E1560", {"start": v(14.5, 2.35) * mm, "mid": v(14.34, 2.42) * mm, "end": v(14.27, 2.26) * mm});
            skLineSegment(sketch, "E1561", {"start": v(14.47, 2.07) * mm, "end": v(14.57, 1.87) * mm});
            skArc(sketch, "E1562", {"start": v(14.46, 1.81) * mm, "mid": v(14.63, 1.76) * mm, "end": v(14.69, 1.93) * mm});
            skArc(sketch, "E1563", {"start": v(14.58, 2.13) * mm, "mid": v(14.41, 2.18) * mm, "end": v(14.36, 2.02) * mm});
            skLineSegment(sketch, "E1564", {"start": v(14.57, 1.87) * mm, "end": v(14.7, 1.68) * mm});
            skArc(sketch, "E1565", {"start": v(14.59, 1.62) * mm, "mid": v(14.76, 1.58) * mm, "end": v(14.8, 1.75) * mm});
            skArc(sketch, "E1566", {"start": v(14.68, 1.94) * mm, "mid": v(14.5, 1.98) * mm, "end": v(14.47, 1.8) * mm});
            skLineSegment(sketch, "E1567", {"start": v(14.7, 1.68) * mm, "end": v(14.83, 1.51) * mm});
            skArc(sketch, "E1568", {"start": v(14.73, 1.43) * mm, "mid": v(14.9, 1.41) * mm, "end": v(14.93, 1.6) * mm});
            skArc(sketch, "E1569", {"start": v(14.8, 1.76) * mm, "mid": v(14.62, 1.78) * mm, "end": v(14.6, 1.6) * mm});
            skLineSegment(sketch, "E1570", {"start": v(14.83, 1.51) * mm, "end": v(14.98, 1.36) * mm});
            skArc(sketch, "E1571", {"start": v(14.9, 1.27) * mm, "mid": v(15.07, 1.27) * mm, "end": v(15.07, 1.44) * mm});
            skArc(sketch, "E1572", {"start": v(14.92, 1.6) * mm, "mid": v(14.74, 1.6) * mm, "end": v(14.74, 1.43) * mm});
            skLineSegment(sketch, "E1573", {"start": v(14.98, 1.36) * mm, "end": v(15.15, 1.21) * mm});
            skArc(sketch, "E1574", {"start": v(15.07, 1.12) * mm, "mid": v(15.24, 1.13) * mm, "end": v(15.23, 1.3) * mm});
            skArc(sketch, "E1575", {"start": v(15.06, 1.45) * mm, "mid": v(14.89, 1.44) * mm, "end": v(14.9, 1.26) * mm});
            skLineSegment(sketch, "E1576", {"start": v(15.15, 1.21) * mm, "end": v(15.33, 1.1) * mm});
            skArc(sketch, "E1577", {"start": v(15.25, 0.99) * mm, "mid": v(15.43, 1.02) * mm, "end": v(15.4, 1.2) * mm});
            skArc(sketch, "E1578", {"start": v(15.22, 1.32) * mm, "mid": v(15.05, 1.29) * mm, "end": v(15.08, 1.11) * mm});
            skLineSegment(sketch, "E1579", {"start": v(15.33, 1.1) * mm, "end": v(15.51, 0.98) * mm});
            skArc(sketch, "E1580", {"start": v(15.45, 0.88) * mm, "mid": v(15.62, 0.92) * mm, "end": v(15.57, 1.1) * mm});
            skArc(sketch, "E1581", {"start": v(15.39, 1.2) * mm, "mid": v(15.22, 1.15) * mm, "end": v(15.26, 0.98) * mm});
            skLineSegment(sketch, "E1582", {"start": v(15.51, 0.98) * mm, "end": v(15.71, 0.9) * mm});
            skArc(sketch, "E1583", {"start": v(15.66, 0.78) * mm, "mid": v(15.83, 0.85) * mm, "end": v(15.76, 1.01) * mm});
            skArc(sketch, "E1584", {"start": v(15.56, 1.1) * mm, "mid": v(15.4, 1.04) * mm, "end": v(15.46, 0.87) * mm});
            skLineSegment(sketch, "E1585", {"start": v(15.71, 0.9) * mm, "end": v(15.92, 0.83) * mm});
            skArc(sketch, "E1586", {"start": v(15.88, 0.7) * mm, "mid": v(16.03, 0.79) * mm, "end": v(15.96, 0.95) * mm});
            skArc(sketch, "E1587", {"start": v(15.75, 1.02) * mm, "mid": v(15.6, 0.94) * mm, "end": v(15.67, 0.78) * mm});
            skLineSegment(sketch, "E1588", {"start": v(15.92, 0.83) * mm, "end": v(16.13, 0.78) * mm});
            skArc(sketch, "E1589", {"start": v(16.1, 0.66) * mm, "mid": v(16.25, 0.75) * mm, "end": v(16.16, 0.9) * mm});
            skArc(sketch, "E1590", {"start": v(15.94, 0.95) * mm, "mid": v(15.8, 0.86) * mm, "end": v(15.89, 0.7) * mm});
            skLineSegment(sketch, "E1591", {"start": v(16.13, 0.78) * mm, "end": v(16.34, 0.75) * mm});
            skArc(sketch, "E1592", {"start": v(16.33, 0.63) * mm, "mid": v(16.47, 0.74) * mm, "end": v(16.36, 0.88) * mm});
            skArc(sketch, "E1593", {"start": v(16.14, 0.9) * mm, "mid": v(16, 0.8) * mm, "end": v(16.11, 0.66) * mm});
            skLineSegment(sketch, "E1594", {"start": v(16.34, 0.75) * mm, "end": v(16.56, 0.74) * mm});
            skArc(sketch, "E1595", {"start": v(16.56, 0.62) * mm, "mid": v(16.69, 0.74) * mm, "end": v(16.57, 0.87) * mm});
            skArc(sketch, "E1596", {"start": v(16.35, 0.88) * mm, "mid": v(16.22, 0.76) * mm, "end": v(16.34, 0.63) * mm});
            skLineSegment(sketch, "E1597", {"start": v(16.56, 0.74) * mm, "end": v(16.79, 0.76) * mm});
            skArc(sketch, "E1598", {"start": v(16.8, 0.63) * mm, "mid": v(16.91, 0.77) * mm, "end": v(16.78, 0.88) * mm});
            skArc(sketch, "E1599", {"start": v(16.56, 0.87) * mm, "mid": v(16.44, 0.74) * mm, "end": v(16.57, 0.62) * mm});
            skLineSegment(sketch, "E1600", {"start": v(16.79, 0.76) * mm, "end": v(17, 0.8) * mm});
            skArc(sketch, "E1601", {"start": v(17.03, 0.67) * mm, "mid": v(17.13, 0.82) * mm, "end": v(16.99, 0.92) * mm});
            skArc(sketch, "E1602", {"start": v(16.77, 0.88) * mm, "mid": v(16.66, 0.74) * mm, "end": v(16.8, 0.64) * mm});
            skLineSegment(sketch, "E1603", {"start": v(17, 0.8) * mm, "end": v(17.25, 0.86) * mm});
            skArc(sketch, "E1604", {"start": v(17.28, 0.74) * mm, "mid": v(17.37, 0.9) * mm, "end": v(17.22, 0.98) * mm});
            skArc(sketch, "E1605", {"start": v(16.98, 0.92) * mm, "mid": v(16.89, 0.76) * mm, "end": v(17.04, 0.68) * mm});
            skLineSegment(sketch, "E1606", {"start": v(17.25, 0.86) * mm, "end": v(20.41, 1.9) * mm});
            skArc(sketch, "E1607", {"start": v(20.45, 1.77) * mm, "mid": v(20.53, 1.93) * mm, "end": v(20.38, 2.01) * mm});
            skArc(sketch, "E1608", {"start": v(17.2, 0.98) * mm, "mid": v(17.13, 0.82) * mm, "end": v(17.29, 0.74) * mm});
            skLineSegment(sketch, "E1609", {"start": v(20.41, 1.9) * mm, "end": v(22.3, 3.26) * mm});
            skArc(sketch, "E1610", {"start": v(22.37, 3.16) * mm, "mid": v(22.4, 3.34) * mm, "end": v(22.23, 3.36) * mm});
            skArc(sketch, "E1611", {"start": v(20.34, 2) * mm, "mid": v(20.31, 1.82) * mm, "end": v(20.49, 1.8) * mm});
            skLineSegment(sketch, "E1612", {"start": v(22.3, 3.26) * mm, "end": v(22.96, 4.08) * mm});
            skArc(sketch, "E1613", {"start": v(23.06, 4) * mm, "mid": v(23.04, 4.18) * mm, "end": v(22.87, 4.16) * mm});
            skArc(sketch, "E1614", {"start": v(22.2, 3.34) * mm, "mid": v(22.22, 3.17) * mm, "end": v(22.4, 3.18) * mm});
            skLineSegment(sketch, "E1615", {"start": v(22.96, 4.08) * mm, "end": v(22.38, 5.9) * mm});
            skArc(sketch, "E1616", {"start": v(22.5, 5.94) * mm, "mid": v(22.34, 6.02) * mm, "end": v(22.26, 5.86) * mm});
            skArc(sketch, "E1617", {"start": v(22.85, 4.05) * mm, "mid": v(23, 3.97) * mm, "end": v(23.08, 4.12) * mm});
            skLineSegment(sketch, "E1618", {"start": v(22.38, 5.9) * mm, "end": v(21.35, 6.17) * mm});
            skArc(sketch, "E1619", {"start": v(21.39, 6.3) * mm, "mid": v(21.23, 6.2) * mm, "end": v(21.32, 6.05) * mm});
            skArc(sketch, "E1620", {"start": v(22.34, 5.78) * mm, "mid": v(22.5, 5.86) * mm, "end": v(22.4, 6.02) * mm});
            skLineSegment(sketch, "E1621", {"start": v(21.35, 6.17) * mm, "end": v(19.02, 6.17) * mm});
            skArc(sketch, "E1622", {"start": v(19.02, 6.3) * mm, "mid": v(18.9, 6.17) * mm, "end": v(19.02, 6.05) * mm});
            skArc(sketch, "E1623", {"start": v(21.35, 6.05) * mm, "mid": v(21.48, 6.17) * mm, "end": v(21.35, 6.3) * mm});
            skLineSegment(sketch, "E1624", {"start": v(14.3, 3.36) * mm, "end": v(14.94, 1.4) * mm});
            skArc(sketch, "E1625", {"start": v(14.82, 1.36) * mm, "mid": v(14.98, 1.28) * mm, "end": v(15.06, 1.44) * mm});
            skArc(sketch, "E1626", {"start": v(14.42, 3.4) * mm, "mid": v(14.27, 3.48) * mm, "end": v(14.19, 3.32) * mm});
            skLineSegment(sketch, "E1627", {"start": v(14.58, 4.12) * mm, "end": v(15.62, 0.94) * mm});
            skArc(sketch, "E1628", {"start": v(15.5, 0.9) * mm, "mid": v(15.65, 0.82) * mm, "end": v(15.73, 0.98) * mm});
            skArc(sketch, "E1629", {"start": v(14.7, 4.16) * mm, "mid": v(14.54, 4.24) * mm, "end": v(14.46, 4.09) * mm});
            skLineSegment(sketch, "E1630", {"start": v(14.95, 4.6) * mm, "end": v(16.2, 0.77) * mm});
            skArc(sketch, "E1631", {"start": v(16.08, 0.73) * mm, "mid": v(16.23, 0.65) * mm, "end": v(16.32, 0.8) * mm});
            skArc(sketch, "E1632", {"start": v(15.07, 4.64) * mm, "mid": v(14.91, 4.72) * mm, "end": v(14.83, 4.56) * mm});
            skLineSegment(sketch, "E1633", {"start": v(15.37, 4.93) * mm, "end": v(16.73, 0.76) * mm});
            skArc(sketch, "E1634", {"start": v(16.6, 0.72) * mm, "mid": v(16.77, 0.64) * mm, "end": v(16.85, 0.8) * mm});
            skArc(sketch, "E1635", {"start": v(15.5, 4.97) * mm, "mid": v(15.33, 5.05) * mm, "end": v(15.25, 4.89) * mm});
            skLineSegment(sketch, "E1636", {"start": v(15.83, 5.12) * mm, "end": v(17.22, 0.86) * mm});
            skArc(sketch, "E1637", {"start": v(17.1, 0.82) * mm, "mid": v(17.26, 0.74) * mm, "end": v(17.34, 0.9) * mm});
            skArc(sketch, "E1638", {"start": v(15.95, 5.16) * mm, "mid": v(15.8, 5.24) * mm, "end": v(15.71, 5.09) * mm});
            skLineSegment(sketch, "E1639", {"start": v(16.3, 5.28) * mm, "end": v(17.7, 1) * mm});
            skArc(sketch, "E1640", {"start": v(17.58, 0.97) * mm, "mid": v(17.73, 0.89) * mm, "end": v(17.81, 1.05) * mm});
            skArc(sketch, "E1641", {"start": v(16.43, 5.32) * mm, "mid": v(16.27, 5.4) * mm, "end": v(16.19, 5.24) * mm});
            skLineSegment(sketch, "E1642", {"start": v(16.78, 5.44) * mm, "end": v(18.17, 1.16) * mm});
            skArc(sketch, "E1643", {"start": v(18.05, 1.12) * mm, "mid": v(18.21, 1.04) * mm, "end": v(18.3, 1.2) * mm});
            skArc(sketch, "E1644", {"start": v(16.9, 5.47) * mm, "mid": v(16.74, 5.55) * mm, "end": v(16.66, 5.4) * mm});
            skLineSegment(sketch, "E1645", {"start": v(17.26, 5.6) * mm, "end": v(18.65, 1.32) * mm});
            skArc(sketch, "E1646", {"start": v(18.53, 1.28) * mm, "mid": v(18.69, 1.2) * mm, "end": v(18.77, 1.36) * mm});
            skArc(sketch, "E1647", {"start": v(17.38, 5.63) * mm, "mid": v(17.22, 5.71) * mm, "end": v(17.14, 5.55) * mm});
            skLineSegment(sketch, "E1648", {"start": v(17.73, 5.75) * mm, "end": v(19.12, 1.47) * mm});
            skArc(sketch, "E1649", {"start": v(19, 1.43) * mm, "mid": v(19.16, 1.35) * mm, "end": v(19.24, 1.51) * mm});
            skArc(sketch, "E1650", {"start": v(17.85, 5.79) * mm, "mid": v(17.7, 5.87) * mm, "end": v(17.61, 5.7) * mm});
            skLineSegment(sketch, "E1651", {"start": v(18.2, 5.9) * mm, "end": v(19.6, 1.63) * mm});
            skArc(sketch, "E1652", {"start": v(19.48, 1.59) * mm, "mid": v(19.64, 1.5) * mm, "end": v(19.72, 1.67) * mm});
            skArc(sketch, "E1653", {"start": v(18.33, 5.94) * mm, "mid": v(18.17, 6.02) * mm, "end": v(18.09, 5.87) * mm});
            skLineSegment(sketch, "E1654", {"start": v(18.68, 6.06) * mm, "end": v(20.07, 1.78) * mm});
            skArc(sketch, "E1655", {"start": v(19.95, 1.74) * mm, "mid": v(20.11, 1.66) * mm, "end": v(20.2, 1.82) * mm});
            skArc(sketch, "E1656", {"start": v(18.8, 6.1) * mm, "mid": v(18.64, 6.18) * mm, "end": v(18.56, 6.02) * mm});
            skLineSegment(sketch, "E1657", {"start": v(19.17, 6.17) * mm, "end": v(20.53, 1.98) * mm});
            skArc(sketch, "E1658", {"start": v(20.42, 1.94) * mm, "mid": v(20.57, 1.86) * mm, "end": v(20.65, 2.02) * mm});
            skArc(sketch, "E1659", {"start": v(19.3, 6.21) * mm, "mid": v(19.13, 6.3) * mm, "end": v(19.05, 6.13) * mm});
            skLineSegment(sketch, "E1660", {"start": v(19.7, 6.17) * mm, "end": v(20.96, 2.29) * mm});
            skArc(sketch, "E1661", {"start": v(20.84, 2.25) * mm, "mid": v(21, 2.17) * mm, "end": v(21.08, 2.33) * mm});
            skArc(sketch, "E1662", {"start": v(19.82, 6.21) * mm, "mid": v(19.66, 6.3) * mm, "end": v(19.58, 6.13) * mm});
            skLineSegment(sketch, "E1663", {"start": v(20.22, 6.17) * mm, "end": v(21.39, 2.6) * mm});
            skArc(sketch, "E1664", {"start": v(21.27, 2.56) * mm, "mid": v(21.42, 2.48) * mm, "end": v(21.5, 2.64) * mm});
            skArc(sketch, "E1665", {"start": v(20.34, 6.2) * mm, "mid": v(20.19, 6.3) * mm, "end": v(20.1, 6.13) * mm});
            skLineSegment(sketch, "E1666", {"start": v(20.75, 6.17) * mm, "end": v(21.81, 2.9) * mm});
            skArc(sketch, "E1667", {"start": v(21.7, 2.87) * mm, "mid": v(21.85, 2.79) * mm, "end": v(21.93, 2.95) * mm});
            skArc(sketch, "E1668", {"start": v(20.87, 6.2) * mm, "mid": v(20.71, 6.29) * mm, "end": v(20.63, 6.13) * mm});
            skLineSegment(sketch, "E1669", {"start": v(21.28, 6.17) * mm, "end": v(22.24, 3.22) * mm});
            skArc(sketch, "E1670", {"start": v(22.12, 3.18) * mm, "mid": v(22.27, 3.1) * mm, "end": v(22.35, 3.26) * mm});
            skArc(sketch, "E1671", {"start": v(21.4, 6.2) * mm, "mid": v(21.24, 6.29) * mm, "end": v(21.16, 6.13) * mm});
            skLineSegment(sketch, "E1672", {"start": v(21.84, 6.04) * mm, "end": v(22.62, 3.66) * mm});
            skArc(sketch, "E1673", {"start": v(22.5, 3.62) * mm, "mid": v(22.66, 3.54) * mm, "end": v(22.74, 3.7) * mm});
            skArc(sketch, "E1674", {"start": v(21.96, 6.08) * mm, "mid": v(21.8, 6.16) * mm, "end": v(21.73, 6) * mm});
            skLineSegment(sketch, "E1675", {"start": v(28.51, 9.45) * mm, "end": v(28.45, 9.32) * mm});
            skArc(sketch, "E1676", {"start": v(28.4, 9.35) * mm, "mid": v(28.43, 9.28) * mm, "end": v(28.5, 9.3) * mm});
            skArc(sketch, "E1677", {"start": v(28.56, 9.43) * mm, "mid": v(28.53, 9.5) * mm, "end": v(28.47, 9.47) * mm});
            skLineSegment(sketch, "E1678", {"start": v(28.45, 9.32) * mm, "end": v(28.4, 9.18) * mm});
            skArc(sketch, "E1679", {"start": v(28.36, 9.19) * mm, "mid": v(28.39, 9.13) * mm, "end": v(28.45, 9.16) * mm});
            skArc(sketch, "E1680", {"start": v(28.5, 9.3) * mm, "mid": v(28.46, 9.37) * mm, "end": v(28.4, 9.34) * mm});
            skLineSegment(sketch, "E1681", {"start": v(28.4, 9.18) * mm, "end": v(28.38, 9.02) * mm});
            skArc(sketch, "E1682", {"start": v(28.33, 9.03) * mm, "mid": v(28.38, 8.97) * mm, "end": v(28.43, 9.01) * mm});
            skArc(sketch, "E1683", {"start": v(28.45, 9.17) * mm, "mid": v(28.4, 9.22) * mm, "end": v(28.35, 9.18) * mm});
            skLineSegment(sketch, "E1684", {"start": v(28.38, 9.02) * mm, "end": v(28.4, 8.86) * mm});
            skArc(sketch, "E1685", {"start": v(28.34, 8.86) * mm, "mid": v(28.4, 8.81) * mm, "end": v(28.44, 8.86) * mm});
            skArc(sketch, "E1686", {"start": v(28.43, 9.02) * mm, "mid": v(28.38, 9.07) * mm, "end": v(28.33, 9.02) * mm});
            skLineSegment(sketch, "E1687", {"start": v(28.4, 8.86) * mm, "end": v(28.4, 8.78) * mm});
            skArc(sketch, "E1688", {"start": v(28.36, 8.77) * mm, "mid": v(28.42, 8.73) * mm, "end": v(28.46, 8.8) * mm});
            skArc(sketch, "E1689", {"start": v(28.44, 8.87) * mm, "mid": v(28.38, 8.91) * mm, "end": v(28.34, 8.85) * mm});
            skLineSegment(sketch, "E1690", {"start": v(28.4, 8.78) * mm, "end": v(29.58, 5.22) * mm});
            skArc(sketch, "E1691", {"start": v(29.53, 5.2) * mm, "mid": v(29.6, 5.17) * mm, "end": v(29.63, 5.23) * mm});
            skArc(sketch, "E1692", {"start": v(28.45, 8.8) * mm, "mid": v(28.4, 8.83) * mm, "end": v(28.36, 8.77) * mm});
            skLineSegment(sketch, "E1693", {"start": v(29.58, 5.22) * mm, "end": v(29.67, 5.09) * mm});
            skArc(sketch, "E1694", {"start": v(29.62, 5.06) * mm, "mid": v(29.7, 5.04) * mm, "end": v(29.7, 5.11) * mm});
            skArc(sketch, "E1695", {"start": v(29.62, 5.24) * mm, "mid": v(29.55, 5.26) * mm, "end": v(29.54, 5.19) * mm});
            skLineSegment(sketch, "E1696", {"start": v(29.67, 5.09) * mm, "end": v(29.77, 4.97) * mm});
            skArc(sketch, "E1697", {"start": v(29.74, 4.94) * mm, "mid": v(29.8, 4.94) * mm, "end": v(29.8, 5) * mm});
            skArc(sketch, "E1698", {"start": v(29.7, 5.12) * mm, "mid": v(29.63, 5.12) * mm, "end": v(29.63, 5.05) * mm});
            skLineSegment(sketch, "E1699", {"start": v(29.77, 4.97) * mm, "end": v(29.9, 4.88) * mm});
            skArc(sketch, "E1700", {"start": v(29.87, 4.84) * mm, "mid": v(29.94, 4.85) * mm, "end": v(29.93, 4.92) * mm});
            skArc(sketch, "E1701", {"start": v(29.8, 5.01) * mm, "mid": v(29.73, 5) * mm, "end": v(29.74, 4.93) * mm});
            skLineSegment(sketch, "E1702", {"start": v(29.9, 4.88) * mm, "end": v(30.01, 4.82) * mm});
            skArc(sketch, "E1703", {"start": v(30, 4.78) * mm, "mid": v(30.06, 4.8) * mm, "end": v(30.04, 4.87) * mm});
            skArc(sketch, "E1704", {"start": v(29.92, 4.93) * mm, "mid": v(29.85, 4.9) * mm, "end": v(29.87, 4.84) * mm});
            skLineSegment(sketch, "E1705", {"start": v(30.01, 4.82) * mm, "end": v(30.08, 4.95) * mm});
            skArc(sketch, "E1706", {"start": v(30.12, 4.92) * mm, "mid": v(30.1, 5) * mm, "end": v(30.03, 4.97) * mm});
            skArc(sketch, "E1707", {"start": v(29.97, 4.84) * mm, "mid": v(30, 4.78) * mm, "end": v(30.06, 4.8) * mm});
            skLineSegment(sketch, "E1708", {"start": v(30.08, 4.95) * mm, "end": v(30.12, 5.1) * mm});
            skArc(sketch, "E1709", {"start": v(30.17, 5.08) * mm, "mid": v(30.14, 5.14) * mm, "end": v(30.08, 5.11) * mm});
            skArc(sketch, "E1710", {"start": v(30.03, 4.96) * mm, "mid": v(30.06, 4.9) * mm, "end": v(30.13, 4.93) * mm});
            skLineSegment(sketch, "E1711", {"start": v(30.12, 5.1) * mm, "end": v(30.14, 5.25) * mm});
            skArc(sketch, "E1712", {"start": v(30.2, 5.24) * mm, "mid": v(30.15, 5.3) * mm, "end": v(30.1, 5.26) * mm});
            skArc(sketch, "E1713", {"start": v(30.07, 5.1) * mm, "mid": v(30.12, 5.05) * mm, "end": v(30.17, 5.09) * mm});
            skLineSegment(sketch, "E1714", {"start": v(30.14, 5.25) * mm, "end": v(30.13, 5.4) * mm});
            skArc(sketch, "E1715", {"start": v(30.18, 5.41) * mm, "mid": v(30.13, 5.46) * mm, "end": v(30.08, 5.4) * mm});
            skArc(sketch, "E1716", {"start": v(30.1, 5.25) * mm, "mid": v(30.15, 5.2) * mm, "end": v(30.2, 5.25) * mm});
            skLineSegment(sketch, "E1717", {"start": v(30.13, 5.4) * mm, "end": v(30.12, 5.49) * mm});
            skArc(sketch, "E1718", {"start": v(30.17, 5.5) * mm, "mid": v(30.11, 5.54) * mm, "end": v(30.07, 5.48) * mm});
            skArc(sketch, "E1719", {"start": v(30.09, 5.4) * mm, "mid": v(30.14, 5.36) * mm, "end": v(30.18, 5.42) * mm});
            skLineSegment(sketch, "E1720", {"start": v(30.12, 5.49) * mm, "end": v(28.95, 9.05) * mm});
            skArc(sketch, "E1721", {"start": v(29, 9.07) * mm, "mid": v(28.93, 9.1) * mm, "end": v(28.9, 9.04) * mm});
            skArc(sketch, "E1722", {"start": v(30.07, 5.47) * mm, "mid": v(30.14, 5.44) * mm, "end": v(30.17, 5.5) * mm});
            skLineSegment(sketch, "E1723", {"start": v(28.95, 9.05) * mm, "end": v(28.86, 9.19) * mm});
            skArc(sketch, "E1724", {"start": v(28.9, 9.21) * mm, "mid": v(28.83, 9.23) * mm, "end": v(28.82, 9.16) * mm});
            skArc(sketch, "E1725", {"start": v(28.9, 9.03) * mm, "mid": v(28.98, 9.01) * mm, "end": v(29, 9.08) * mm});
            skLineSegment(sketch, "E1726", {"start": v(28.86, 9.19) * mm, "end": v(28.75, 9.3) * mm});
            skArc(sketch, "E1727", {"start": v(28.79, 9.33) * mm, "mid": v(28.72, 9.33) * mm, "end": v(28.72, 9.26) * mm});
            skArc(sketch, "E1728", {"start": v(28.82, 9.15) * mm, "mid": v(28.9, 9.15) * mm, "end": v(28.9, 9.22) * mm});
            skLineSegment(sketch, "E1729", {"start": v(28.75, 9.3) * mm, "end": v(28.63, 9.39) * mm});
            skArc(sketch, "E1730", {"start": v(28.66, 9.43) * mm, "mid": v(28.59, 9.42) * mm, "end": v(28.6, 9.35) * mm});
            skArc(sketch, "E1731", {"start": v(28.72, 9.26) * mm, "mid": v(28.8, 9.27) * mm, "end": v(28.78, 9.34) * mm});
            skLineSegment(sketch, "E1732", {"start": v(28.63, 9.39) * mm, "end": v(28.51, 9.45) * mm});
            skArc(sketch, "E1733", {"start": v(28.53, 9.5) * mm, "mid": v(28.47, 9.47) * mm, "end": v(28.49, 9.4) * mm});
            skArc(sketch, "E1734", {"start": v(28.6, 9.35) * mm, "mid": v(28.67, 9.37) * mm, "end": v(28.65, 9.43) * mm});
            skLineSegment(sketch, "E1735", {"start": v(28.4, 9.16) * mm, "end": v(29.76, 5) * mm});
            skArc(sketch, "E1736", {"start": v(29.7, 4.98) * mm, "mid": v(29.77, 4.94) * mm, "end": v(29.8, 5) * mm});
            skArc(sketch, "E1737", {"start": v(28.45, 9.18) * mm, "mid": v(28.39, 9.2) * mm, "end": v(28.35, 9.14) * mm});
            skLineSegment(sketch, "E1738", {"start": v(28.52, 9.45) * mm, "end": v(30.02, 4.83) * mm});
            skArc(sketch, "E1739", {"start": v(29.97, 4.81) * mm, "mid": v(30.03, 4.78) * mm, "end": v(30.07, 4.84) * mm});
            skArc(sketch, "E1740", {"start": v(28.57, 9.46) * mm, "mid": v(28.5, 9.5) * mm, "end": v(28.47, 9.43) * mm});
            skLineSegment(sketch, "E1741", {"start": v(28.79, 9.26) * mm, "end": v(30.13, 5.14) * mm});
            skArc(sketch, "E1742", {"start": v(30.08, 5.12) * mm, "mid": v(30.14, 5.09) * mm, "end": v(30.18, 5.15) * mm});
            skArc(sketch, "E1743", {"start": v(28.84, 9.28) * mm, "mid": v(28.77, 9.3) * mm, "end": v(28.74, 9.25) * mm});
            skCircle(sketch, "E1744", {"center": v(16.52, 3) * mm, "radius": 1.7 * mm});
            skArc(sketch, "E1745", {"start": v(16.52, 2.12) * mm, "mid": v(17.4, 3) * mm, "end": v(16.52, 3.87) * mm});
            skArc(sketch, "E1746", {"start": v(16.52, 3.87) * mm, "mid": v(15.65, 3) * mm, "end": v(16.52, 2.12) * mm});
            skCircle(sketch, "E1747", {"center": v(26.03, 6.09) * mm, "radius": 1.7 * mm});
            skArc(sketch, "E1748", {"start": v(26.03, 5.21) * mm, "mid": v(26.91, 6.09) * mm, "end": v(26.03, 6.96) * mm});
            skArc(sketch, "E1749", {"start": v(26.03, 6.96) * mm, "mid": v(25.16, 6.09) * mm, "end": v(26.03, 5.21) * mm});
            skLineSegment(sketch, "E1750", {"start": v(14.01, -17.8) * mm, "end": v(11.89, -14.9) * mm});
            skArc(sketch, "E1751", {"start": v(11.99, -14.83) * mm, "mid": v(11.81, -14.8) * mm, "end": v(11.79, -14.97) * mm});
            skArc(sketch, "E1752", {"start": v(13.91, -17.88) * mm, "mid": v(14.09, -17.9) * mm, "end": v(14.12, -17.73) * mm});
            skLineSegment(sketch, "E1753", {"start": v(11.89, -14.9) * mm, "end": v(11.73, -14.74) * mm});
            skArc(sketch, "E1754", {"start": v(11.82, -14.65) * mm, "mid": v(11.64, -14.65) * mm, "end": v(11.64, -14.83) * mm});
            skArc(sketch, "E1755", {"start": v(11.8, -14.99) * mm, "mid": v(11.98, -14.99) * mm, "end": v(11.98, -14.81) * mm});
            skLineSegment(sketch, "E1756", {"start": v(11.73, -14.74) * mm, "end": v(11.56, -14.6) * mm});
            skArc(sketch, "E1757", {"start": v(11.64, -14.5) * mm, "mid": v(11.46, -14.52) * mm, "end": v(11.48, -14.7) * mm});
            skArc(sketch, "E1758", {"start": v(11.65, -14.84) * mm, "mid": v(11.83, -14.82) * mm, "end": v(11.8, -14.64) * mm});
            skLineSegment(sketch, "E1759", {"start": v(11.56, -14.6) * mm, "end": v(11.37, -14.48) * mm});
            skArc(sketch, "E1760", {"start": v(11.44, -14.37) * mm, "mid": v(11.27, -14.4) * mm, "end": v(11.3, -14.58) * mm});
            skArc(sketch, "E1761", {"start": v(11.49, -14.7) * mm, "mid": v(11.66, -14.67) * mm, "end": v(11.63, -14.5) * mm});
            skLineSegment(sketch, "E1762", {"start": v(11.37, -14.48) * mm, "end": v(11.18, -14.38) * mm});
            skArc(sketch, "E1763", {"start": v(11.24, -14.27) * mm, "mid": v(11.07, -14.32) * mm, "end": v(11.12, -14.49) * mm});
            skArc(sketch, "E1764", {"start": v(11.31, -14.59) * mm, "mid": v(11.48, -14.54) * mm, "end": v(11.43, -14.37) * mm});
            skLineSegment(sketch, "E1765", {"start": v(11.18, -14.38) * mm, "end": v(10.98, -14.3) * mm});
            skArc(sketch, "E1766", {"start": v(11.03, -14.18) * mm, "mid": v(10.86, -14.25) * mm, "end": v(10.93, -14.4) * mm});
            skArc(sketch, "E1767", {"start": v(11.13, -14.5) * mm, "mid": v(11.3, -14.42) * mm, "end": v(11.23, -14.26) * mm});
            skLineSegment(sketch, "E1768", {"start": v(10.98, -14.3) * mm, "end": v(10.77, -14.23) * mm});
            skArc(sketch, "E1769", {"start": v(10.8, -14.11) * mm, "mid": v(10.65, -14.2) * mm, "end": v(10.74, -14.35) * mm});
            skArc(sketch, "E1770", {"start": v(10.94, -14.41) * mm, "mid": v(11.1, -14.33) * mm, "end": v(11.02, -14.17) * mm});
            skLineSegment(sketch, "E1771", {"start": v(10.77, -14.23) * mm, "end": v(10.56, -14.19) * mm});
            skArc(sketch, "E1772", {"start": v(10.59, -14.06) * mm, "mid": v(10.44, -14.16) * mm, "end": v(10.54, -14.3) * mm});
            skArc(sketch, "E1773", {"start": v(10.75, -14.35) * mm, "mid": v(10.9, -14.25) * mm, "end": v(10.8, -14.1) * mm});
            skLineSegment(sketch, "E1774", {"start": v(10.56, -14.19) * mm, "end": v(10.35, -14.16) * mm});
            skArc(sketch, "E1775", {"start": v(10.36, -14.04) * mm, "mid": v(10.22, -14.15) * mm, "end": v(10.33, -14.29) * mm});
            skArc(sketch, "E1776", {"start": v(10.55, -14.31) * mm, "mid": v(10.69, -14.2) * mm, "end": v(10.57, -14.06) * mm});
            skLineSegment(sketch, "E1777", {"start": v(10.35, -14.16) * mm, "end": v(10.13, -14.16) * mm});
            skArc(sketch, "E1778", {"start": v(10.13, -14.04) * mm, "mid": v(10, -14.16) * mm, "end": v(10.13, -14.29) * mm});
            skArc(sketch, "E1779", {"start": v(10.35, -14.29) * mm, "mid": v(10.47, -14.17) * mm, "end": v(10.35, -14.04) * mm});
            skLineSegment(sketch, "E1780", {"start": v(10.13, -14.16) * mm, "end": v(9.91, -14.18) * mm});
            skArc(sketch, "E1781", {"start": v(9.9, -14.06) * mm, "mid": v(9.79, -14.2) * mm, "end": v(9.92, -14.3) * mm});
            skArc(sketch, "E1782", {"start": v(10.14, -14.29) * mm, "mid": v(10.25, -14.15) * mm, "end": v(10.12, -14.04) * mm});
            skLineSegment(sketch, "E1783", {"start": v(9.91, -14.18) * mm, "end": v(9.7, -14.22) * mm});
            skArc(sketch, "E1784", {"start": v(9.68, -14.1) * mm, "mid": v(9.58, -14.25) * mm, "end": v(9.72, -14.34) * mm});
            skArc(sketch, "E1785", {"start": v(9.94, -14.3) * mm, "mid": v(10.04, -14.16) * mm, "end": v(9.9, -14.06) * mm});
            skLineSegment(sketch, "E1786", {"start": v(9.7, -14.22) * mm, "end": v(9.49, -14.28) * mm});
            skArc(sketch, "E1787", {"start": v(9.45, -14.16) * mm, "mid": v(9.37, -14.32) * mm, "end": v(9.52, -14.4) * mm});
            skArc(sketch, "E1788", {"start": v(9.73, -14.34) * mm, "mid": v(9.82, -14.19) * mm, "end": v(9.66, -14.1) * mm});
            skLineSegment(sketch, "E1789", {"start": v(9.49, -14.28) * mm, "end": v(9.28, -14.37) * mm});
            skArc(sketch, "E1790", {"start": v(9.23, -14.25) * mm, "mid": v(9.16, -14.41) * mm, "end": v(9.33, -14.48) * mm});
            skArc(sketch, "E1791", {"start": v(9.53, -14.4) * mm, "mid": v(9.6, -14.24) * mm, "end": v(9.44, -14.17) * mm});
            skLineSegment(sketch, "E1792", {"start": v(9.28, -14.37) * mm, "end": v(9.08, -14.47) * mm});
            skArc(sketch, "E1793", {"start": v(9.02, -14.36) * mm, "mid": v(8.97, -14.53) * mm, "end": v(9.14, -14.58) * mm});
            skArc(sketch, "E1794", {"start": v(9.34, -14.48) * mm, "mid": v(9.4, -14.3) * mm, "end": v(9.22, -14.26) * mm});
            skLineSegment(sketch, "E1795", {"start": v(9.08, -14.47) * mm, "end": v(8.9, -14.6) * mm});
            skArc(sketch, "E1796", {"start": v(8.83, -14.49) * mm, "mid": v(8.8, -14.66) * mm, "end": v(8.97, -14.7) * mm});
            skArc(sketch, "E1797", {"start": v(9.15, -14.58) * mm, "mid": v(9.18, -14.4) * mm, "end": v(9.01, -14.37) * mm});
            skLineSegment(sketch, "E1798", {"start": v(8.9, -14.6) * mm, "end": v(8.7, -14.74) * mm});
            skArc(sketch, "E1799", {"start": v(8.63, -14.65) * mm, "mid": v(8.61, -14.82) * mm, "end": v(8.79, -14.84) * mm});
            skArc(sketch, "E1800", {"start": v(8.98, -14.69) * mm, "mid": v(9, -14.51) * mm, "end": v(8.82, -14.5) * mm});
            skLineSegment(sketch, "E1801", {"start": v(8.7, -14.74) * mm, "end": v(8.55, -14.9) * mm});
            skArc(sketch, "E1802", {"start": v(8.46, -14.82) * mm, "mid": v(8.46, -15) * mm, "end": v(8.64, -15) * mm});
            skArc(sketch, "E1803", {"start": v(8.8, -14.83) * mm, "mid": v(8.8, -14.66) * mm, "end": v(8.62, -14.66) * mm});
            skLineSegment(sketch, "E1804", {"start": v(8.55, -14.9) * mm, "end": v(8.4, -15.08) * mm});
            skArc(sketch, "E1805", {"start": v(8.31, -15) * mm, "mid": v(8.33, -15.17) * mm, "end": v(8.5, -15.16) * mm});
            skArc(sketch, "E1806", {"start": v(8.65, -14.98) * mm, "mid": v(8.63, -14.8) * mm, "end": v(8.45, -14.82) * mm});
            skLineSegment(sketch, "E1807", {"start": v(8.4, -15.08) * mm, "end": v(8.29, -15.26) * mm});
            skArc(sketch, "E1808", {"start": v(8.18, -15.2) * mm, "mid": v(8.22, -15.36) * mm, "end": v(8.4, -15.33) * mm});
            skArc(sketch, "E1809", {"start": v(8.51, -15.15) * mm, "mid": v(8.48, -14.97) * mm, "end": v(8.3, -15) * mm});
            skLineSegment(sketch, "E1810", {"start": v(8.29, -15.26) * mm, "end": v(8.18, -15.45) * mm});
            skArc(sketch, "E1811", {"start": v(8.07, -15.4) * mm, "mid": v(8.13, -15.56) * mm, "end": v(8.3, -15.51) * mm});
            skArc(sketch, "E1812", {"start": v(8.4, -15.32) * mm, "mid": v(8.35, -15.15) * mm, "end": v(8.18, -15.2) * mm});
            skLineSegment(sketch, "E1813", {"start": v(8.18, -15.45) * mm, "end": v(8.1, -15.65) * mm});
            skArc(sketch, "E1814", {"start": v(7.99, -15.6) * mm, "mid": v(8.05, -15.77) * mm, "end": v(8.22, -15.7) * mm});
            skArc(sketch, "E1815", {"start": v(8.3, -15.5) * mm, "mid": v(8.23, -15.34) * mm, "end": v(8.07, -15.4) * mm});
            skLineSegment(sketch, "E1816", {"start": v(8.1, -15.65) * mm, "end": v(8.04, -15.86) * mm});
            skArc(sketch, "E1817", {"start": v(7.92, -15.82) * mm, "mid": v(8, -15.98) * mm, "end": v(8.16, -15.9) * mm});
            skArc(sketch, "E1818", {"start": v(8.22, -15.69) * mm, "mid": v(8.14, -15.53) * mm, "end": v(7.98, -15.62) * mm});
            skLineSegment(sketch, "E1819", {"start": v(8.04, -15.86) * mm, "end": v(8, -16.07) * mm});
            skArc(sketch, "E1820", {"start": v(7.87, -16.05) * mm, "mid": v(7.97, -16.2) * mm, "end": v(8.12, -16.1) * mm});
            skArc(sketch, "E1821", {"start": v(8.16, -15.88) * mm, "mid": v(8.06, -15.74) * mm, "end": v(7.92, -15.84) * mm});
            skLineSegment(sketch, "E1822", {"start": v(8, -16.07) * mm, "end": v(7.97, -16.29) * mm});
            skArc(sketch, "E1823", {"start": v(7.85, -16.27) * mm, "mid": v(7.96, -16.41) * mm, "end": v(8.1, -16.3) * mm});
            skArc(sketch, "E1824", {"start": v(8.12, -16.08) * mm, "mid": v(8, -15.95) * mm, "end": v(7.87, -16.06) * mm});
            skLineSegment(sketch, "E1825", {"start": v(7.97, -16.29) * mm, "end": v(7.97, -16.5) * mm});
            skArc(sketch, "E1826", {"start": v(7.85, -16.5) * mm, "mid": v(7.97, -16.63) * mm, "end": v(8.1, -16.5) * mm});
            skArc(sketch, "E1827", {"start": v(8.1, -16.29) * mm, "mid": v(7.98, -16.16) * mm, "end": v(7.85, -16.29) * mm});
            skLineSegment(sketch, "E1828", {"start": v(7.97, -16.5) * mm, "end": v(8, -16.72) * mm});
            skArc(sketch, "E1829", {"start": v(7.87, -16.73) * mm, "mid": v(8, -16.84) * mm, "end": v(8.12, -16.7) * mm});
            skArc(sketch, "E1830", {"start": v(8.1, -16.5) * mm, "mid": v(7.96, -16.38) * mm, "end": v(7.85, -16.51) * mm});
            skLineSegment(sketch, "E1831", {"start": v(8, -16.72) * mm, "end": v(8.03, -16.93) * mm});
            skArc(sketch, "E1832", {"start": v(7.9, -16.96) * mm, "mid": v(8.05, -17.06) * mm, "end": v(8.15, -16.91) * mm});
            skArc(sketch, "E1833", {"start": v(8.11, -16.7) * mm, "mid": v(7.97, -16.6) * mm, "end": v(7.87, -16.74) * mm});
            skLineSegment(sketch, "E1834", {"start": v(8.03, -16.93) * mm, "end": v(8.1, -17.15) * mm});
            skArc(sketch, "E1835", {"start": v(7.97, -17.18) * mm, "mid": v(8.13, -17.27) * mm, "end": v(8.21, -17.11) * mm});
            skArc(sketch, "E1836", {"start": v(8.15, -16.9) * mm, "mid": v(8, -16.81) * mm, "end": v(7.91, -16.97) * mm});
            skLineSegment(sketch, "E1837", {"start": v(8.1, -17.15) * mm, "end": v(8.18, -17.35) * mm});
            skArc(sketch, "E1838", {"start": v(8.06, -17.4) * mm, "mid": v(8.22, -17.47) * mm, "end": v(8.3, -17.3) * mm});
            skArc(sketch, "E1839", {"start": v(8.2, -17.1) * mm, "mid": v(8.05, -17.03) * mm, "end": v(7.98, -17.2) * mm});
            skLineSegment(sketch, "E1840", {"start": v(8.18, -17.35) * mm, "end": v(8.28, -17.55) * mm});
            skArc(sketch, "E1841", {"start": v(8.17, -17.6) * mm, "mid": v(8.34, -17.66) * mm, "end": v(8.4, -17.5) * mm});
            skArc(sketch, "E1842", {"start": v(8.29, -17.3) * mm, "mid": v(8.12, -17.24) * mm, "end": v(8.06, -17.4) * mm});
            skLineSegment(sketch, "E1843", {"start": v(8.28, -17.55) * mm, "end": v(8.42, -17.76) * mm});
            skArc(sketch, "E1844", {"start": v(8.31, -17.83) * mm, "mid": v(8.49, -17.86) * mm, "end": v(8.52, -17.7) * mm});
            skArc(sketch, "E1845", {"start": v(8.38, -17.48) * mm, "mid": v(8.21, -17.45) * mm, "end": v(8.18, -17.62) * mm});
            skLineSegment(sketch, "E1846", {"start": v(8.42, -17.76) * mm, "end": v(10.37, -20.45) * mm});
            skArc(sketch, "E1847", {"start": v(10.27, -20.53) * mm, "mid": v(10.45, -20.55) * mm, "end": v(10.48, -20.38) * mm});
            skArc(sketch, "E1848", {"start": v(8.52, -17.69) * mm, "mid": v(8.34, -17.66) * mm, "end": v(8.32, -17.83) * mm});
            skLineSegment(sketch, "E1849", {"start": v(10.37, -20.45) * mm, "end": v(12.26, -21.82) * mm});
            skArc(sketch, "E1850", {"start": v(12.19, -21.92) * mm, "mid": v(12.36, -21.9) * mm, "end": v(12.33, -21.72) * mm});
            skArc(sketch, "E1851", {"start": v(10.45, -20.35) * mm, "mid": v(10.27, -20.38) * mm, "end": v(10.3, -20.55) * mm});
            skLineSegment(sketch, "E1852", {"start": v(12.26, -21.82) * mm, "end": v(13.25, -22.2) * mm});
            skArc(sketch, "E1853", {"start": v(13.2, -22.32) * mm, "mid": v(13.36, -22.24) * mm, "end": v(13.3, -22.08) * mm});
            skArc(sketch, "E1854", {"start": v(12.3, -21.7) * mm, "mid": v(12.14, -21.78) * mm, "end": v(12.22, -21.94) * mm});
            skLineSegment(sketch, "E1855", {"start": v(13.25, -22.2) * mm, "end": v(14.79, -21.08) * mm});
            skArc(sketch, "E1856", {"start": v(14.86, -21.18) * mm, "mid": v(14.89, -21) * mm, "end": v(14.72, -20.98) * mm});
            skArc(sketch, "E1857", {"start": v(13.17, -22.1) * mm, "mid": v(13.15, -22.27) * mm, "end": v(13.32, -22.3) * mm});
            skLineSegment(sketch, "E1858", {"start": v(14.79, -21.08) * mm, "end": v(14.73, -20.02) * mm});
            skArc(sketch, "E1859", {"start": v(14.86, -20.02) * mm, "mid": v(14.73, -19.9) * mm, "end": v(14.6, -20.03) * mm});
            skArc(sketch, "E1860", {"start": v(14.66, -21.09) * mm, "mid": v(14.8, -21.2) * mm, "end": v(14.91, -21.07) * mm});
            skLineSegment(sketch, "E1861", {"start": v(14.73, -20.02) * mm, "end": v(14.01, -17.8) * mm});
            skArc(sketch, "E1862", {"start": v(14.13, -17.77) * mm, "mid": v(13.98, -17.69) * mm, "end": v(13.9, -17.85) * mm});
            skArc(sketch, "E1863", {"start": v(14.61, -20.06) * mm, "mid": v(14.77, -20.14) * mm, "end": v(14.85, -19.99) * mm});
            skLineSegment(sketch, "E1864", {"start": v(9.88, -14.19) * mm, "end": v(8.21, -15.4) * mm});
            skArc(sketch, "E1865", {"start": v(8.14, -15.3) * mm, "mid": v(8.11, -15.47) * mm, "end": v(8.29, -15.5) * mm});
            skArc(sketch, "E1866", {"start": v(9.95, -14.29) * mm, "mid": v(9.98, -14.11) * mm, "end": v(9.8, -14.09) * mm});
            skLineSegment(sketch, "E1867", {"start": v(10.7, -14.21) * mm, "end": v(7.98, -16.18) * mm});
            skArc(sketch, "E1868", {"start": v(7.91, -16.08) * mm, "mid": v(7.88, -16.26) * mm, "end": v(8.06, -16.28) * mm});
            skArc(sketch, "E1869", {"start": v(10.77, -14.32) * mm, "mid": v(10.8, -14.14) * mm, "end": v(10.62, -14.11) * mm});
            skLineSegment(sketch, "E1870", {"start": v(11.26, -14.42) * mm, "end": v(8, -16.79) * mm});
            skArc(sketch, "E1871", {"start": v(7.93, -16.69) * mm, "mid": v(7.9, -16.86) * mm, "end": v(8.08, -16.89) * mm});
            skArc(sketch, "E1872", {"start": v(11.34, -14.52) * mm, "mid": v(11.36, -14.35) * mm, "end": v(11.19, -14.32) * mm});
            skLineSegment(sketch, "E1873", {"start": v(11.7, -14.72) * mm, "end": v(8.15, -17.3) * mm});
            skArc(sketch, "E1874", {"start": v(8.08, -17.2) * mm, "mid": v(8.05, -17.37) * mm, "end": v(8.23, -17.4) * mm});
            skArc(sketch, "E1875", {"start": v(11.77, -14.82) * mm, "mid": v(11.8, -14.64) * mm, "end": v(11.63, -14.62) * mm});
            skLineSegment(sketch, "E1876", {"start": v(12.03, -15.1) * mm, "end": v(8.4, -17.73) * mm});
            skArc(sketch, "E1877", {"start": v(8.33, -17.63) * mm, "mid": v(8.3, -17.8) * mm, "end": v(8.47, -17.84) * mm});
            skArc(sketch, "E1878", {"start": v(12.1, -15.2) * mm, "mid": v(12.13, -15.02) * mm, "end": v(11.96, -15) * mm});
            skLineSegment(sketch, "E1879", {"start": v(12.33, -15.5) * mm, "end": v(8.7, -18.14) * mm});
            skArc(sketch, "E1880", {"start": v(8.62, -18.04) * mm, "mid": v(8.6, -18.21) * mm, "end": v(8.77, -18.24) * mm});
            skArc(sketch, "E1881", {"start": v(12.4, -15.6) * mm, "mid": v(12.43, -15.43) * mm, "end": v(12.25, -15.4) * mm});
            skLineSegment(sketch, "E1882", {"start": v(12.62, -15.9) * mm, "end": v(8.99, -18.54) * mm});
            skArc(sketch, "E1883", {"start": v(8.91, -18.44) * mm, "mid": v(8.89, -18.62) * mm, "end": v(9.06, -18.65) * mm});
            skArc(sketch, "E1884", {"start": v(12.7, -16) * mm, "mid": v(12.72, -15.83) * mm, "end": v(12.55, -15.8) * mm});
            skLineSegment(sketch, "E1885", {"start": v(12.92, -16.3) * mm, "end": v(9.28, -18.95) * mm});
            skArc(sketch, "E1886", {"start": v(9.2, -18.85) * mm, "mid": v(9.18, -19.02) * mm, "end": v(9.35, -19.05) * mm});
            skArc(sketch, "E1887", {"start": v(13, -16.4) * mm, "mid": v(13.02, -16.23) * mm, "end": v(12.84, -16.2) * mm});
            skLineSegment(sketch, "E1888", {"start": v(13.21, -16.71) * mm, "end": v(9.58, -19.35) * mm});
            skArc(sketch, "E1889", {"start": v(9.5, -19.25) * mm, "mid": v(9.47, -19.43) * mm, "end": v(9.65, -19.45) * mm});
            skArc(sketch, "E1890", {"start": v(13.29, -16.81) * mm, "mid": v(13.31, -16.64) * mm, "end": v(13.14, -16.6) * mm});
            skLineSegment(sketch, "E1891", {"start": v(13.5, -17.11) * mm, "end": v(9.87, -19.76) * mm});
            skArc(sketch, "E1892", {"start": v(9.8, -19.66) * mm, "mid": v(9.77, -19.83) * mm, "end": v(9.94, -19.86) * mm});
            skArc(sketch, "E1893", {"start": v(13.58, -17.22) * mm, "mid": v(13.6, -17.04) * mm, "end": v(13.43, -17.01) * mm});
            skLineSegment(sketch, "E1894", {"start": v(13.8, -17.52) * mm, "end": v(10.16, -20.16) * mm});
            skArc(sketch, "E1895", {"start": v(10.09, -20.06) * mm, "mid": v(10.06, -20.24) * mm, "end": v(10.24, -20.26) * mm});
            skArc(sketch, "E1896", {"start": v(13.88, -17.62) * mm, "mid": v(13.9, -17.44) * mm, "end": v(13.73, -17.42) * mm});
            skLineSegment(sketch, "E1897", {"start": v(14.06, -17.95) * mm, "end": v(10.5, -20.54) * mm});
            skArc(sketch, "E1898", {"start": v(10.42, -20.44) * mm, "mid": v(10.4, -20.61) * mm, "end": v(10.57, -20.64) * mm});
            skArc(sketch, "E1899", {"start": v(14.13, -18.05) * mm, "mid": v(14.16, -17.88) * mm, "end": v(13.99, -17.85) * mm});
            skLineSegment(sketch, "E1900", {"start": v(14.22, -18.45) * mm, "end": v(10.92, -20.85) * mm});
            skArc(sketch, "E1901", {"start": v(10.85, -20.75) * mm, "mid": v(10.82, -20.92) * mm, "end": v(11, -20.95) * mm});
            skArc(sketch, "E1902", {"start": v(14.3, -18.55) * mm, "mid": v(14.32, -18.38) * mm, "end": v(14.15, -18.35) * mm});
            skLineSegment(sketch, "E1903", {"start": v(14.38, -18.95) * mm, "end": v(11.35, -21.16) * mm});
            skArc(sketch, "E1904", {"start": v(11.27, -21.06) * mm, "mid": v(11.24, -21.23) * mm, "end": v(11.42, -21.26) * mm});
            skArc(sketch, "E1905", {"start": v(14.46, -19.05) * mm, "mid": v(14.49, -18.88) * mm, "end": v(14.31, -18.85) * mm});
            skLineSegment(sketch, "E1906", {"start": v(14.55, -19.45) * mm, "end": v(11.77, -21.47) * mm});
            skArc(sketch, "E1907", {"start": v(11.7, -21.36) * mm, "mid": v(11.67, -21.54) * mm, "end": v(11.84, -21.57) * mm});
            skArc(sketch, "E1908", {"start": v(14.62, -19.55) * mm, "mid": v(14.65, -19.38) * mm, "end": v(14.47, -19.35) * mm});
            skLineSegment(sketch, "E1909", {"start": v(14.7, -19.95) * mm, "end": v(12.2, -21.77) * mm});
            skArc(sketch, "E1910", {"start": v(12.12, -21.67) * mm, "mid": v(12.1, -21.85) * mm, "end": v(12.27, -21.88) * mm});
            skArc(sketch, "E1911", {"start": v(14.78, -20.05) * mm, "mid": v(14.81, -19.88) * mm, "end": v(14.64, -19.85) * mm});
            skLineSegment(sketch, "E1912", {"start": v(14.76, -20.53) * mm, "end": v(12.73, -22) * mm});
            skArc(sketch, "E1913", {"start": v(12.66, -21.9) * mm, "mid": v(12.63, -22.08) * mm, "end": v(12.8, -22.1) * mm});
            skArc(sketch, "E1914", {"start": v(14.83, -20.63) * mm, "mid": v(14.86, -20.46) * mm, "end": v(14.69, -20.43) * mm});
            skLineSegment(sketch, "E1915", {"start": v(20.06, -25.82) * mm, "end": v(19.92, -25.8) * mm});
            skArc(sketch, "E1916", {"start": v(19.93, -25.75) * mm, "mid": v(19.87, -25.79) * mm, "end": v(19.92, -25.85) * mm});
            skArc(sketch, "E1917", {"start": v(20.06, -25.87) * mm, "mid": v(20.11, -25.83) * mm, "end": v(20.07, -25.77) * mm});
            skLineSegment(sketch, "E1918", {"start": v(19.92, -25.8) * mm, "end": v(19.77, -25.8) * mm});
            skArc(sketch, "E1919", {"start": v(19.77, -25.75) * mm, "mid": v(19.72, -25.8) * mm, "end": v(19.77, -25.85) * mm});
            skArc(sketch, "E1920", {"start": v(19.92, -25.85) * mm, "mid": v(19.97, -25.8) * mm, "end": v(19.92, -25.75) * mm});
            skLineSegment(sketch, "E1921", {"start": v(19.77, -25.8) * mm, "end": v(19.62, -25.83) * mm});
            skArc(sketch, "E1922", {"start": v(19.6, -25.78) * mm, "mid": v(19.57, -25.84) * mm, "end": v(19.63, -25.88) * mm});
            skArc(sketch, "E1923", {"start": v(19.78, -25.85) * mm, "mid": v(19.82, -25.79) * mm, "end": v(19.76, -25.75) * mm});
            skLineSegment(sketch, "E1924", {"start": v(19.62, -25.83) * mm, "end": v(19.47, -25.88) * mm});
            skArc(sketch, "E1925", {"start": v(19.45, -25.84) * mm, "mid": v(19.42, -25.9) * mm, "end": v(19.49, -25.93) * mm});
            skArc(sketch, "E1926", {"start": v(19.63, -25.88) * mm, "mid": v(19.66, -25.81) * mm, "end": v(19.6, -25.78) * mm});
            skLineSegment(sketch, "E1927", {"start": v(19.47, -25.88) * mm, "end": v(19.4, -25.92) * mm});
            skArc(sketch, "E1928", {"start": v(19.37, -25.88) * mm, "mid": v(19.35, -25.95) * mm, "end": v(19.42, -25.97) * mm});
            skArc(sketch, "E1929", {"start": v(19.5, -25.93) * mm, "mid": v(19.51, -25.86) * mm, "end": v(19.44, -25.84) * mm});
            skLineSegment(sketch, "E1930", {"start": v(19.4, -25.92) * mm, "end": v(16.37, -28.14) * mm});
            skArc(sketch, "E1931", {"start": v(16.34, -28.1) * mm, "mid": v(16.33, -28.17) * mm, "end": v(16.4, -28.18) * mm});
            skArc(sketch, "E1932", {"start": v(19.43, -25.96) * mm, "mid": v(19.44, -25.9) * mm, "end": v(19.37, -25.88) * mm});
            skLineSegment(sketch, "E1933", {"start": v(16.37, -28.14) * mm, "end": v(16.27, -28.26) * mm});
            skArc(sketch, "E1934", {"start": v(16.23, -28.23) * mm, "mid": v(16.24, -28.3) * mm, "end": v(16.3, -28.3) * mm});
            skArc(sketch, "E1935", {"start": v(16.4, -28.17) * mm, "mid": v(16.4, -28.1) * mm, "end": v(16.33, -28.1) * mm});
            skLineSegment(sketch, "E1936", {"start": v(16.27, -28.26) * mm, "end": v(16.2, -28.4) * mm});
            skArc(sketch, "E1937", {"start": v(16.15, -28.38) * mm, "mid": v(16.17, -28.44) * mm, "end": v(16.24, -28.42) * mm});
            skArc(sketch, "E1938", {"start": v(16.31, -28.29) * mm, "mid": v(16.3, -28.22) * mm, "end": v(16.23, -28.24) * mm});
            skLineSegment(sketch, "E1939", {"start": v(16.2, -28.4) * mm, "end": v(16.15, -28.55) * mm});
            skArc(sketch, "E1940", {"start": v(16.1, -28.53) * mm, "mid": v(16.13, -28.6) * mm, "end": v(16.2, -28.56) * mm});
            skArc(sketch, "E1941", {"start": v(16.24, -28.42) * mm, "mid": v(16.21, -28.35) * mm, "end": v(16.15, -28.38) * mm});
            skLineSegment(sketch, "E1942", {"start": v(16.15, -28.55) * mm, "end": v(16.13, -28.68) * mm});
            skArc(sketch, "E1943", {"start": v(16.08, -28.67) * mm, "mid": v(16.12, -28.73) * mm, "end": v(16.18, -28.69) * mm});
            skArc(sketch, "E1944", {"start": v(16.2, -28.56) * mm, "mid": v(16.15, -28.5) * mm, "end": v(16.1, -28.54) * mm});
            skLineSegment(sketch, "E1945", {"start": v(16.13, -28.68) * mm, "end": v(16.27, -28.7) * mm});
            skArc(sketch, "E1946", {"start": v(16.26, -28.75) * mm, "mid": v(16.32, -28.7) * mm, "end": v(16.27, -28.65) * mm});
            skArc(sketch, "E1947", {"start": v(16.13, -28.63) * mm, "mid": v(16.08, -28.67) * mm, "end": v(16.12, -28.73) * mm});
            skLineSegment(sketch, "E1948", {"start": v(16.27, -28.7) * mm, "end": v(16.42, -28.7) * mm});
            skArc(sketch, "E1949", {"start": v(16.42, -28.75) * mm, "mid": v(16.47, -28.7) * mm, "end": v(16.42, -28.65) * mm});
            skArc(sketch, "E1950", {"start": v(16.26, -28.65) * mm, "mid": v(16.22, -28.7) * mm, "end": v(16.27, -28.75) * mm});
            skLineSegment(sketch, "E1951", {"start": v(16.42, -28.7) * mm, "end": v(16.57, -28.67) * mm});
            skArc(sketch, "E1952", {"start": v(16.58, -28.72) * mm, "mid": v(16.62, -28.66) * mm, "end": v(16.56, -28.62) * mm});
            skArc(sketch, "E1953", {"start": v(16.41, -28.65) * mm, "mid": v(16.37, -28.7) * mm, "end": v(16.43, -28.75) * mm});
            skLineSegment(sketch, "E1954", {"start": v(16.57, -28.67) * mm, "end": v(16.72, -28.61) * mm});
            skArc(sketch, "E1955", {"start": v(16.74, -28.66) * mm, "mid": v(16.77, -28.6) * mm, "end": v(16.7, -28.56) * mm});
            skArc(sketch, "E1956", {"start": v(16.56, -28.62) * mm, "mid": v(16.53, -28.68) * mm, "end": v(16.6, -28.71) * mm});
            skLineSegment(sketch, "E1957", {"start": v(16.72, -28.61) * mm, "end": v(16.8, -28.57) * mm});
            skArc(sketch, "E1958", {"start": v(16.82, -28.62) * mm, "mid": v(16.84, -28.55) * mm, "end": v(16.77, -28.53) * mm});
            skArc(sketch, "E1959", {"start": v(16.7, -28.57) * mm, "mid": v(16.68, -28.63) * mm, "end": v(16.75, -28.65) * mm});
            skLineSegment(sketch, "E1960", {"start": v(16.8, -28.57) * mm, "end": v(19.82, -26.36) * mm});
            skArc(sketch, "E1961", {"start": v(19.85, -26.4) * mm, "mid": v(19.86, -26.33) * mm, "end": v(19.8, -26.32) * mm});
            skArc(sketch, "E1962", {"start": v(16.76, -28.53) * mm, "mid": v(16.75, -28.6) * mm, "end": v(16.82, -28.61) * mm});
            skLineSegment(sketch, "E1963", {"start": v(19.82, -26.36) * mm, "end": v(19.92, -26.23) * mm});
            skArc(sketch, "E1964", {"start": v(19.96, -26.26) * mm, "mid": v(19.95, -26.2) * mm, "end": v(19.88, -26.2) * mm});
            skArc(sketch, "E1965", {"start": v(19.78, -26.32) * mm, "mid": v(19.8, -26.4) * mm, "end": v(19.86, -26.39) * mm});
            skLineSegment(sketch, "E1966", {"start": v(19.92, -26.23) * mm, "end": v(20, -26.1) * mm});
            skArc(sketch, "E1967", {"start": v(20.04, -26.12) * mm, "mid": v(20.02, -26.05) * mm, "end": v(19.95, -26.07) * mm});
            skArc(sketch, "E1968", {"start": v(19.88, -26.2) * mm, "mid": v(19.9, -26.28) * mm, "end": v(19.96, -26.26) * mm});
            skLineSegment(sketch, "E1969", {"start": v(20, -26.1) * mm, "end": v(20.04, -25.95) * mm});
            skArc(sketch, "E1970", {"start": v(20.1, -25.96) * mm, "mid": v(20.06, -25.9) * mm, "end": v(20, -25.93) * mm});
            skArc(sketch, "E1971", {"start": v(19.95, -26.08) * mm, "mid": v(19.98, -26.14) * mm, "end": v(20.04, -26.11) * mm});
            skLineSegment(sketch, "E1972", {"start": v(20.04, -25.95) * mm, "end": v(20.06, -25.82) * mm});
            skArc(sketch, "E1973", {"start": v(20.11, -25.83) * mm, "mid": v(20.07, -25.77) * mm, "end": v(20.01, -25.8) * mm});
            skArc(sketch, "E1974", {"start": v(20, -25.94) * mm, "mid": v(20.04, -26) * mm, "end": v(20.1, -25.96) * mm});
            skLineSegment(sketch, "E1975", {"start": v(19.75, -25.8) * mm, "end": v(16.2, -28.38) * mm});
            skArc(sketch, "E1976", {"start": v(16.18, -28.34) * mm, "mid": v(16.17, -28.4) * mm, "end": v(16.24, -28.42) * mm});
            skArc(sketch, "E1977", {"start": v(19.78, -25.84) * mm, "mid": v(19.8, -25.77) * mm, "end": v(19.72, -25.76) * mm});
            skLineSegment(sketch, "E1978", {"start": v(20.06, -25.82) * mm, "end": v(16.13, -28.68) * mm});
            skArc(sketch, "E1979", {"start": v(16.1, -28.64) * mm, "mid": v(16.1, -28.7) * mm, "end": v(16.16, -28.72) * mm});
            skArc(sketch, "E1980", {"start": v(20.1, -25.87) * mm, "mid": v(20.1, -25.8) * mm, "end": v(20.03, -25.78) * mm});
            skLineSegment(sketch, "E1981", {"start": v(19.97, -26.14) * mm, "end": v(16.46, -28.69) * mm});
            skArc(sketch, "E1982", {"start": v(16.43, -28.65) * mm, "mid": v(16.42, -28.72) * mm, "end": v(16.5, -28.73) * mm});
            skArc(sketch, "E1983", {"start": v(20, -26.18) * mm, "mid": v(20.01, -26.11) * mm, "end": v(19.94, -26.1) * mm});
            skCircle(sketch, "E1984", {"center": v(10.22, -16.41) * mm, "radius": 1.7 * mm});
            skArc(sketch, "E1985", {"start": v(10.22, -17.29) * mm, "mid": v(11.1, -16.41) * mm, "end": v(10.22, -15.54) * mm});
            skArc(sketch, "E1986", {"start": v(10.22, -15.54) * mm, "mid": v(9.35, -16.41) * mm, "end": v(10.22, -17.29) * mm});
            skCircle(sketch, "E1987", {"center": v(16.1, -24.5) * mm, "radius": 1.7 * mm});
            skArc(sketch, "E1988", {"start": v(16.1, -25.38) * mm, "mid": v(16.98, -24.5) * mm, "end": v(16.1, -23.63) * mm});
            skArc(sketch, "E1989", {"start": v(16.1, -23.63) * mm, "mid": v(15.22, -24.5) * mm, "end": v(16.1, -25.38) * mm});
            skLineSegment(sketch, "E1990", {"start": v(-4.8, -10.73) * mm, "end": v(-4.8, -10.27) * mm});
            skArc(sketch, "E1991", {"start": v(-4.8, -10.27) * mm, "mid": v(-4.8, -10.23) * mm, "end": v(-4.84, -10.22) * mm});
            skLineSegment(sketch, "E1992", {"start": v(-4.84, -10.22) * mm, "end": v(-5.24, -10.22) * mm});
            skArc(sketch, "E1993", {"start": v(-5.24, -10.22) * mm, "mid": v(-5.27, -10.23) * mm, "end": v(-5.28, -10.27) * mm});
            skLineSegment(sketch, "E1994", {"start": v(-5.28, -10.27) * mm, "end": v(-5.28, -10.73) * mm});
            skArc(sketch, "E1995", {"start": v(-5.28, -10.73) * mm, "mid": v(-5.27, -10.76) * mm, "end": v(-5.24, -10.78) * mm});
            skLineSegment(sketch, "E1996", {"start": v(-5.24, -10.78) * mm, "end": v(-4.84, -10.78) * mm});
            skArc(sketch, "E1997", {"start": v(-4.84, -10.78) * mm, "mid": v(-4.8, -10.76) * mm, "end": v(-4.8, -10.73) * mm});
            skLineSegment(sketch, "E1998", {"start": v(-3.92, -10.73) * mm, "end": v(-3.92, -10.27) * mm});
            skArc(sketch, "E1999", {"start": v(-3.92, -10.27) * mm, "mid": v(-3.93, -10.23) * mm, "end": v(-3.96, -10.22) * mm});
            skLineSegment(sketch, "E2000", {"start": v(-3.96, -10.22) * mm, "end": v(-4.36, -10.22) * mm});
            skArc(sketch, "E2001", {"start": v(-4.36, -10.22) * mm, "mid": v(-4.4, -10.23) * mm, "end": v(-4.4, -10.27) * mm});
            skLineSegment(sketch, "E2002", {"start": v(-4.4, -10.27) * mm, "end": v(-4.4, -10.73) * mm});
            skArc(sketch, "E2003", {"start": v(-4.4, -10.73) * mm, "mid": v(-4.4, -10.76) * mm, "end": v(-4.36, -10.78) * mm});
            skLineSegment(sketch, "E2004", {"start": v(-4.36, -10.78) * mm, "end": v(-3.96, -10.78) * mm});
            skArc(sketch, "E2005", {"start": v(-3.96, -10.78) * mm, "mid": v(-3.93, -10.76) * mm, "end": v(-3.92, -10.73) * mm});
            skLineSegment(sketch, "E2006", {"start": v(-4.8, -11.93) * mm, "end": v(-4.8, -11.47) * mm});
            skArc(sketch, "E2007", {"start": v(-4.8, -11.47) * mm, "mid": v(-4.8, -11.43) * mm, "end": v(-4.84, -11.42) * mm});
            skLineSegment(sketch, "E2008", {"start": v(-4.84, -11.42) * mm, "end": v(-5.24, -11.42) * mm});
            skArc(sketch, "E2009", {"start": v(-5.24, -11.42) * mm, "mid": v(-5.27, -11.43) * mm, "end": v(-5.28, -11.47) * mm});
            skLineSegment(sketch, "E2010", {"start": v(-5.28, -11.47) * mm, "end": v(-5.28, -11.93) * mm});
            skArc(sketch, "E2011", {"start": v(-5.28, -11.93) * mm, "mid": v(-5.27, -11.96) * mm, "end": v(-5.24, -11.98) * mm});
            skLineSegment(sketch, "E2012", {"start": v(-5.24, -11.98) * mm, "end": v(-4.84, -11.98) * mm});
            skArc(sketch, "E2013", {"start": v(-4.84, -11.98) * mm, "mid": v(-4.8, -11.96) * mm, "end": v(-4.8, -11.93) * mm});
            skLineSegment(sketch, "E2014", {"start": v(-3.92, -11.93) * mm, "end": v(-3.92, -11.47) * mm});
            skArc(sketch, "E2015", {"start": v(-3.92, -11.47) * mm, "mid": v(-3.93, -11.43) * mm, "end": v(-3.96, -11.42) * mm});
            skLineSegment(sketch, "E2016", {"start": v(-3.96, -11.42) * mm, "end": v(-4.36, -11.42) * mm});
            skArc(sketch, "E2017", {"start": v(-4.36, -11.42) * mm, "mid": v(-4.4, -11.43) * mm, "end": v(-4.4, -11.47) * mm});
            skLineSegment(sketch, "E2018", {"start": v(-4.4, -11.47) * mm, "end": v(-4.4, -11.93) * mm});
            skArc(sketch, "E2019", {"start": v(-4.4, -11.93) * mm, "mid": v(-4.4, -11.96) * mm, "end": v(-4.36, -11.98) * mm});
            skLineSegment(sketch, "E2020", {"start": v(-4.36, -11.98) * mm, "end": v(-3.96, -11.98) * mm});
            skArc(sketch, "E2021", {"start": v(-3.96, -11.98) * mm, "mid": v(-3.93, -11.96) * mm, "end": v(-3.92, -11.93) * mm});
            skLineSegment(sketch, "E2022", {"start": v(9.92, -10.64) * mm, "end": v(10.2, -11.02) * mm});
            skArc(sketch, "E2023", {"start": v(10.2, -11.02) * mm, "mid": v(10.23, -11.04) * mm, "end": v(10.26, -11.03) * mm});
            skLineSegment(sketch, "E2024", {"start": v(10.26, -11.03) * mm, "end": v(10.58, -10.8) * mm});
            skArc(sketch, "E2025", {"start": v(10.58, -10.8) * mm, "mid": v(10.6, -10.77) * mm, "end": v(10.6, -10.73) * mm});
            skLineSegment(sketch, "E2026", {"start": v(10.6, -10.73) * mm, "end": v(10.32, -10.36) * mm});
            skArc(sketch, "E2027", {"start": v(10.32, -10.36) * mm, "mid": v(10.29, -10.34) * mm, "end": v(10.25, -10.35) * mm});
            skLineSegment(sketch, "E2028", {"start": v(10.25, -10.35) * mm, "end": v(9.93, -10.58) * mm});
            skArc(sketch, "E2029", {"start": v(9.93, -10.58) * mm, "mid": v(9.91, -10.6) * mm, "end": v(9.92, -10.64) * mm});
            skLineSegment(sketch, "E2030", {"start": v(9.2, -11.16) * mm, "end": v(9.48, -11.54) * mm});
            skArc(sketch, "E2031", {"start": v(9.48, -11.54) * mm, "mid": v(9.51, -11.56) * mm, "end": v(9.55, -11.55) * mm});
            skLineSegment(sketch, "E2032", {"start": v(9.55, -11.55) * mm, "end": v(9.87, -11.32) * mm});
            skArc(sketch, "E2033", {"start": v(9.87, -11.32) * mm, "mid": v(9.89, -11.29) * mm, "end": v(9.88, -11.25) * mm});
            skLineSegment(sketch, "E2034", {"start": v(9.88, -11.25) * mm, "end": v(9.6, -10.87) * mm});
            skArc(sketch, "E2035", {"start": v(9.6, -10.87) * mm, "mid": v(9.57, -10.86) * mm, "end": v(9.54, -10.86) * mm});
            skLineSegment(sketch, "E2036", {"start": v(9.54, -10.86) * mm, "end": v(9.22, -11.1) * mm});
            skArc(sketch, "E2037", {"start": v(9.22, -11.1) * mm, "mid": v(9.2, -11.13) * mm, "end": v(9.2, -11.16) * mm});
            skLineSegment(sketch, "E2038", {"start": v(11.02, 4.12) * mm, "end": v(11.46, 4.26) * mm});
            skArc(sketch, "E2039", {"start": v(11.46, 4.26) * mm, "mid": v(11.49, 4.28) * mm, "end": v(11.5, 4.32) * mm});
            skLineSegment(sketch, "E2040", {"start": v(11.5, 4.32) * mm, "end": v(11.37, 4.7) * mm});
            skArc(sketch, "E2041", {"start": v(11.37, 4.7) * mm, "mid": v(11.35, 4.72) * mm, "end": v(11.3, 4.73) * mm});
            skLineSegment(sketch, "E2042", {"start": v(11.3, 4.73) * mm, "end": v(10.87, 4.58) * mm});
            skArc(sketch, "E2043", {"start": v(10.87, 4.58) * mm, "mid": v(10.84, 4.56) * mm, "end": v(10.84, 4.52) * mm});
            skLineSegment(sketch, "E2044", {"start": v(10.84, 4.52) * mm, "end": v(10.96, 4.15) * mm});
            skArc(sketch, "E2045", {"start": v(10.96, 4.15) * mm, "mid": v(10.98, 4.12) * mm, "end": v(11.02, 4.12) * mm});
            skLineSegment(sketch, "E2046", {"start": v(11.3, 3.28) * mm, "end": v(11.73, 3.42) * mm});
            skArc(sketch, "E2047", {"start": v(11.73, 3.42) * mm, "mid": v(11.76, 3.45) * mm, "end": v(11.76, 3.48) * mm});
            skLineSegment(sketch, "E2048", {"start": v(11.76, 3.48) * mm, "end": v(11.64, 3.86) * mm});
            skArc(sketch, "E2049", {"start": v(11.64, 3.86) * mm, "mid": v(11.62, 3.89) * mm, "end": v(11.58, 3.89) * mm});
            skLineSegment(sketch, "E2050", {"start": v(11.58, 3.89) * mm, "end": v(11.14, 3.74) * mm});
            skArc(sketch, "E2051", {"start": v(11.14, 3.74) * mm, "mid": v(11.11, 3.72) * mm, "end": v(11.1, 3.69) * mm});
            skLineSegment(sketch, "E2052", {"start": v(11.1, 3.69) * mm, "end": v(11.23, 3.3) * mm});
            skArc(sketch, "E2053", {"start": v(11.23, 3.3) * mm, "mid": v(11.25, 3.28) * mm, "end": v(11.3, 3.28) * mm});
            skLineSegment(sketch, "E2054", {"start": v(1.7, 5.33) * mm, "end": v(1.7, 4.87) * mm});
            skArc(sketch, "E2055", {"start": v(1.7, 4.87) * mm, "mid": v(1.7, 4.83) * mm, "end": v(1.74, 4.82) * mm});
            skLineSegment(sketch, "E2056", {"start": v(1.74, 4.82) * mm, "end": v(2.14, 4.82) * mm});
            skArc(sketch, "E2057", {"start": v(2.14, 4.82) * mm, "mid": v(2.17, 4.83) * mm, "end": v(2.18, 4.87) * mm});
            skLineSegment(sketch, "E2058", {"start": v(2.18, 4.87) * mm, "end": v(2.18, 5.33) * mm});
            skArc(sketch, "E2059", {"start": v(2.18, 5.33) * mm, "mid": v(2.17, 5.36) * mm, "end": v(2.14, 5.38) * mm});
            skLineSegment(sketch, "E2060", {"start": v(2.14, 5.38) * mm, "end": v(1.74, 5.38) * mm});
            skArc(sketch, "E2061", {"start": v(1.74, 5.38) * mm, "mid": v(1.7, 5.36) * mm, "end": v(1.7, 5.33) * mm});
            skLineSegment(sketch, "E2062", {"start": v(0.82, 5.33) * mm, "end": v(0.82, 4.87) * mm});
            skArc(sketch, "E2063", {"start": v(0.82, 4.87) * mm, "mid": v(0.83, 4.83) * mm, "end": v(0.86, 4.82) * mm});
            skLineSegment(sketch, "E2064", {"start": v(0.86, 4.82) * mm, "end": v(1.26, 4.82) * mm});
            skArc(sketch, "E2065", {"start": v(1.26, 4.82) * mm, "mid": v(1.3, 4.83) * mm, "end": v(1.3, 4.87) * mm});
            skLineSegment(sketch, "E2066", {"start": v(1.3, 4.87) * mm, "end": v(1.3, 5.33) * mm});
            skArc(sketch, "E2067", {"start": v(1.3, 5.33) * mm, "mid": v(1.3, 5.36) * mm, "end": v(1.26, 5.38) * mm});
            skLineSegment(sketch, "E2068", {"start": v(1.26, 5.38) * mm, "end": v(0.86, 5.38) * mm});
            skArc(sketch, "E2069", {"start": v(0.86, 5.38) * mm, "mid": v(0.83, 5.36) * mm, "end": v(0.82, 5.33) * mm});
            skLineSegment(sketch, "E2070", {"start": v(-11.42, 4.25) * mm, "end": v(-10.98, 4.1) * mm});
            skArc(sketch, "E2071", {"start": v(-10.98, 4.1) * mm, "mid": v(-10.94, 4.1) * mm, "end": v(-10.92, 4.14) * mm});
            skLineSegment(sketch, "E2072", {"start": v(-10.92, 4.14) * mm, "end": v(-10.8, 4.51) * mm});
            skArc(sketch, "E2073", {"start": v(-10.8, 4.51) * mm, "mid": v(-10.8, 4.55) * mm, "end": v(-10.83, 4.57) * mm});
            skLineSegment(sketch, "E2074", {"start": v(-10.83, 4.57) * mm, "end": v(-11.27, 4.72) * mm});
            skArc(sketch, "E2075", {"start": v(-11.27, 4.72) * mm, "mid": v(-11.3, 4.71) * mm, "end": v(-11.33, 4.69) * mm});
            skLineSegment(sketch, "E2076", {"start": v(-11.33, 4.69) * mm, "end": v(-11.45, 4.3) * mm});
            skArc(sketch, "E2077", {"start": v(-11.45, 4.3) * mm, "mid": v(-11.45, 4.27) * mm, "end": v(-11.42, 4.25) * mm});
            skLineSegment(sketch, "E2078", {"start": v(-11.7, 3.41) * mm, "end": v(-11.25, 3.27) * mm});
            skArc(sketch, "E2079", {"start": v(-11.25, 3.27) * mm, "mid": v(-11.21, 3.27) * mm, "end": v(-11.2, 3.3) * mm});
            skLineSegment(sketch, "E2080", {"start": v(-11.2, 3.3) * mm, "end": v(-11.07, 3.68) * mm});
            skArc(sketch, "E2081", {"start": v(-11.07, 3.68) * mm, "mid": v(-11.07, 3.71) * mm, "end": v(-11.1, 3.73) * mm});
            skLineSegment(sketch, "E2082", {"start": v(-11.1, 3.73) * mm, "end": v(-11.54, 3.88) * mm});
            skArc(sketch, "E2083", {"start": v(-11.54, 3.88) * mm, "mid": v(-11.58, 3.88) * mm, "end": v(-11.6, 3.85) * mm});
            skLineSegment(sketch, "E2084", {"start": v(-11.6, 3.85) * mm, "end": v(-11.72, 3.47) * mm});
            skArc(sketch, "E2085", {"start": v(-11.72, 3.47) * mm, "mid": v(-11.72, 3.44) * mm, "end": v(-11.7, 3.41) * mm});
            skLineSegment(sketch, "E2086", {"start": v(-10.05, -11.12) * mm, "end": v(-9.77, -10.74) * mm});
            skArc(sketch, "E2087", {"start": v(-9.77, -10.74) * mm, "mid": v(-9.76, -10.7) * mm, "end": v(-9.78, -10.68) * mm});
            skLineSegment(sketch, "E2088", {"start": v(-9.78, -10.68) * mm, "end": v(-10.1, -10.45) * mm});
            skArc(sketch, "E2089", {"start": v(-10.1, -10.45) * mm, "mid": v(-10.14, -10.44) * mm, "end": v(-10.17, -10.46) * mm});
            skLineSegment(sketch, "E2090", {"start": v(-10.17, -10.46) * mm, "end": v(-10.44, -10.83) * mm});
            skArc(sketch, "E2091", {"start": v(-10.44, -10.83) * mm, "mid": v(-10.45, -10.87) * mm, "end": v(-10.43, -10.9) * mm});
            skLineSegment(sketch, "E2092", {"start": v(-10.43, -10.9) * mm, "end": v(-10.11, -11.13) * mm});
            skArc(sketch, "E2093", {"start": v(-10.11, -11.13) * mm, "mid": v(-10.08, -11.14) * mm, "end": v(-10.05, -11.12) * mm});
            skLineSegment(sketch, "E2094", {"start": v(-9.33, -11.64) * mm, "end": v(-9.06, -11.26) * mm});
            skArc(sketch, "E2095", {"start": v(-9.06, -11.26) * mm, "mid": v(-9.05, -11.23) * mm, "end": v(-9.07, -11.2) * mm});
            skLineSegment(sketch, "E2096", {"start": v(-9.07, -11.2) * mm, "end": v(-9.39, -10.96) * mm});
            skArc(sketch, "E2097", {"start": v(-9.39, -10.96) * mm, "mid": v(-9.42, -10.96) * mm, "end": v(-9.45, -10.97) * mm});
            skLineSegment(sketch, "E2098", {"start": v(-9.45, -10.97) * mm, "end": v(-9.73, -11.35) * mm});
            skArc(sketch, "E2099", {"start": v(-9.73, -11.35) * mm, "mid": v(-9.74, -11.39) * mm, "end": v(-9.72, -11.42) * mm});
            skLineSegment(sketch, "E2100", {"start": v(-9.72, -11.42) * mm, "end": v(-9.4, -11.65) * mm});
            skArc(sketch, "E2101", {"start": v(-9.4, -11.65) * mm, "mid": v(-9.36, -11.66) * mm, "end": v(-9.33, -11.64) * mm});
            skLineSegment(sketch, "E2102", {"start": v(7.82, -12.14) * mm, "end": v(8.1, -12.52) * mm});
            skArc(sketch, "E2103", {"start": v(8.1, -12.52) * mm, "mid": v(8.13, -12.54) * mm, "end": v(8.16, -12.53) * mm});
            skLineSegment(sketch, "E2104", {"start": v(8.16, -12.53) * mm, "end": v(8.48, -12.3) * mm});
            skArc(sketch, "E2105", {"start": v(8.48, -12.3) * mm, "mid": v(8.5, -12.27) * mm, "end": v(8.5, -12.23) * mm});
            skLineSegment(sketch, "E2106", {"start": v(8.5, -12.23) * mm, "end": v(8.22, -11.86) * mm});
            skArc(sketch, "E2107", {"start": v(8.22, -11.86) * mm, "mid": v(8.19, -11.84) * mm, "end": v(8.15, -11.85) * mm});
            skLineSegment(sketch, "E2108", {"start": v(8.15, -11.85) * mm, "end": v(7.83, -12.08) * mm});
            skArc(sketch, "E2109", {"start": v(7.83, -12.08) * mm, "mid": v(7.81, -12.1) * mm, "end": v(7.82, -12.14) * mm});
            skLineSegment(sketch, "E2110", {"start": v(7.1, -12.66) * mm, "end": v(7.38, -13.04) * mm});
            skArc(sketch, "E2111", {"start": v(7.38, -13.04) * mm, "mid": v(7.41, -13.06) * mm, "end": v(7.45, -13.05) * mm});
            skLineSegment(sketch, "E2112", {"start": v(7.45, -13.05) * mm, "end": v(7.77, -12.82) * mm});
            skArc(sketch, "E2113", {"start": v(7.77, -12.82) * mm, "mid": v(7.79, -12.79) * mm, "end": v(7.78, -12.75) * mm});
            skLineSegment(sketch, "E2114", {"start": v(7.78, -12.75) * mm, "end": v(7.5, -12.37) * mm});
            skArc(sketch, "E2115", {"start": v(7.5, -12.37) * mm, "mid": v(7.47, -12.36) * mm, "end": v(7.44, -12.36) * mm});
            skLineSegment(sketch, "E2116", {"start": v(7.44, -12.36) * mm, "end": v(7.12, -12.6) * mm});
            skArc(sketch, "E2117", {"start": v(7.12, -12.6) * mm, "mid": v(7.1, -12.63) * mm, "end": v(7.1, -12.66) * mm});
            skLineSegment(sketch, "E2118", {"start": v(11.85, 1.72) * mm, "end": v(12.3, 1.86) * mm});
            skArc(sketch, "E2119", {"start": v(12.3, 1.86) * mm, "mid": v(12.32, 1.88) * mm, "end": v(12.32, 1.92) * mm});
            skLineSegment(sketch, "E2120", {"start": v(12.32, 1.92) * mm, "end": v(12.2, 2.3) * mm});
            skArc(sketch, "E2121", {"start": v(12.2, 2.3) * mm, "mid": v(12.18, 2.32) * mm, "end": v(12.14, 2.33) * mm});
            skLineSegment(sketch, "E2122", {"start": v(12.14, 2.33) * mm, "end": v(11.7, 2.18) * mm});
            skArc(sketch, "E2123", {"start": v(11.7, 2.18) * mm, "mid": v(11.67, 2.16) * mm, "end": v(11.67, 2.12) * mm});
            skLineSegment(sketch, "E2124", {"start": v(11.67, 2.12) * mm, "end": v(11.79, 1.75) * mm});
            skArc(sketch, "E2125", {"start": v(11.79, 1.75) * mm, "mid": v(11.81, 1.72) * mm, "end": v(11.85, 1.72) * mm});
            skLineSegment(sketch, "E2126", {"start": v(12.12, 0.88) * mm, "end": v(12.56, 1.02) * mm});
            skArc(sketch, "E2127", {"start": v(12.56, 1.02) * mm, "mid": v(12.59, 1.05) * mm, "end": v(12.6, 1.08) * mm});
            skLineSegment(sketch, "E2128", {"start": v(12.6, 1.08) * mm, "end": v(12.47, 1.46) * mm});
            skArc(sketch, "E2129", {"start": v(12.47, 1.46) * mm, "mid": v(12.45, 1.49) * mm, "end": v(12.41, 1.49) * mm});
            skLineSegment(sketch, "E2130", {"start": v(12.41, 1.49) * mm, "end": v(11.97, 1.34) * mm});
            skArc(sketch, "E2131", {"start": v(11.97, 1.34) * mm, "mid": v(11.94, 1.32) * mm, "end": v(11.94, 1.29) * mm});
            skLineSegment(sketch, "E2132", {"start": v(11.94, 1.29) * mm, "end": v(12.06, 0.9) * mm});
            skArc(sketch, "E2133", {"start": v(12.06, 0.9) * mm, "mid": v(12.08, 0.88) * mm, "end": v(12.12, 0.88) * mm});
            skLineSegment(sketch, "E2134", {"start": v(-1.3, 5.33) * mm, "end": v(-1.3, 4.87) * mm});
            skArc(sketch, "E2135", {"start": v(-1.3, 4.87) * mm, "mid": v(-1.3, 4.83) * mm, "end": v(-1.26, 4.82) * mm});
            skLineSegment(sketch, "E2136", {"start": v(-1.26, 4.82) * mm, "end": v(-0.86, 4.82) * mm});
            skArc(sketch, "E2137", {"start": v(-0.86, 4.82) * mm, "mid": v(-0.83, 4.83) * mm, "end": v(-0.82, 4.87) * mm});
            skLineSegment(sketch, "E2138", {"start": v(-0.82, 4.87) * mm, "end": v(-0.82, 5.33) * mm});
            skArc(sketch, "E2139", {"start": v(-0.82, 5.33) * mm, "mid": v(-0.83, 5.36) * mm, "end": v(-0.86, 5.38) * mm});
            skLineSegment(sketch, "E2140", {"start": v(-0.86, 5.38) * mm, "end": v(-1.26, 5.38) * mm});
            skArc(sketch, "E2141", {"start": v(-1.26, 5.38) * mm, "mid": v(-1.3, 5.36) * mm, "end": v(-1.3, 5.33) * mm});
            skLineSegment(sketch, "E2142", {"start": v(-2.18, 5.33) * mm, "end": v(-2.18, 4.87) * mm});
            skArc(sketch, "E2143", {"start": v(-2.18, 4.87) * mm, "mid": v(-2.17, 4.83) * mm, "end": v(-2.14, 4.82) * mm});
            skLineSegment(sketch, "E2144", {"start": v(-2.14, 4.82) * mm, "end": v(-1.74, 4.82) * mm});
            skArc(sketch, "E2145", {"start": v(-1.74, 4.82) * mm, "mid": v(-1.7, 4.83) * mm, "end": v(-1.7, 4.87) * mm});
            skLineSegment(sketch, "E2146", {"start": v(-1.7, 4.87) * mm, "end": v(-1.7, 5.33) * mm});
            skArc(sketch, "E2147", {"start": v(-1.7, 5.33) * mm, "mid": v(-1.7, 5.36) * mm, "end": v(-1.74, 5.38) * mm});
            skLineSegment(sketch, "E2148", {"start": v(-1.74, 5.38) * mm, "end": v(-2.14, 5.38) * mm});
            skArc(sketch, "E2149", {"start": v(-2.14, 5.38) * mm, "mid": v(-2.17, 5.36) * mm, "end": v(-2.18, 5.33) * mm});
            skLineSegment(sketch, "E2150", {"start": v(-12.16, 1.86) * mm, "end": v(-11.72, 1.72) * mm});
            skArc(sketch, "E2151", {"start": v(-11.72, 1.72) * mm, "mid": v(-11.68, 1.72) * mm, "end": v(-11.66, 1.75) * mm});
            skLineSegment(sketch, "E2152", {"start": v(-11.66, 1.75) * mm, "end": v(-11.54, 2.12) * mm});
            skArc(sketch, "E2153", {"start": v(-11.54, 2.12) * mm, "mid": v(-11.54, 2.16) * mm, "end": v(-11.57, 2.18) * mm});
            skLineSegment(sketch, "E2154", {"start": v(-11.57, 2.18) * mm, "end": v(-12, 2.33) * mm});
            skArc(sketch, "E2155", {"start": v(-12, 2.33) * mm, "mid": v(-12.05, 2.32) * mm, "end": v(-12.07, 2.3) * mm});
            skLineSegment(sketch, "E2156", {"start": v(-12.07, 2.3) * mm, "end": v(-12.2, 1.92) * mm});
            skArc(sketch, "E2157", {"start": v(-12.2, 1.92) * mm, "mid": v(-12.19, 1.88) * mm, "end": v(-12.16, 1.86) * mm});
            skLineSegment(sketch, "E2158", {"start": v(-12.43, 1.02) * mm, "end": v(-12, 0.88) * mm});
            skArc(sketch, "E2159", {"start": v(-12, 0.88) * mm, "mid": v(-11.95, 0.88) * mm, "end": v(-11.93, 0.9) * mm});
            skLineSegment(sketch, "E2160", {"start": v(-11.93, 0.9) * mm, "end": v(-11.8, 1.29) * mm});
            skArc(sketch, "E2161", {"start": v(-11.8, 1.29) * mm, "mid": v(-11.81, 1.32) * mm, "end": v(-11.84, 1.34) * mm});
            skLineSegment(sketch, "E2162", {"start": v(-11.84, 1.34) * mm, "end": v(-12.28, 1.49) * mm});
            skArc(sketch, "E2163", {"start": v(-12.28, 1.49) * mm, "mid": v(-12.32, 1.49) * mm, "end": v(-12.34, 1.46) * mm});
            skLineSegment(sketch, "E2164", {"start": v(-12.34, 1.46) * mm, "end": v(-12.46, 1.08) * mm});
            skArc(sketch, "E2165", {"start": v(-12.46, 1.08) * mm, "mid": v(-12.46, 1.05) * mm, "end": v(-12.43, 1.02) * mm});
            skLineSegment(sketch, "E2166", {"start": v(-8.05, -12.52) * mm, "end": v(-7.77, -12.14) * mm});
            skArc(sketch, "E2167", {"start": v(-7.77, -12.14) * mm, "mid": v(-7.76, -12.1) * mm, "end": v(-7.78, -12.08) * mm});
            skLineSegment(sketch, "E2168", {"start": v(-7.78, -12.08) * mm, "end": v(-8.1, -11.85) * mm});
            skArc(sketch, "E2169", {"start": v(-8.1, -11.85) * mm, "mid": v(-8.14, -11.84) * mm, "end": v(-8.17, -11.86) * mm});
            skLineSegment(sketch, "E2170", {"start": v(-8.17, -11.86) * mm, "end": v(-8.44, -12.23) * mm});
            skArc(sketch, "E2171", {"start": v(-8.44, -12.23) * mm, "mid": v(-8.45, -12.27) * mm, "end": v(-8.43, -12.3) * mm});
            skLineSegment(sketch, "E2172", {"start": v(-8.43, -12.3) * mm, "end": v(-8.11, -12.53) * mm});
            skArc(sketch, "E2173", {"start": v(-8.11, -12.53) * mm, "mid": v(-8.08, -12.54) * mm, "end": v(-8.05, -12.52) * mm});
            skLineSegment(sketch, "E2174", {"start": v(-7.33, -13.04) * mm, "end": v(-7.06, -12.66) * mm});
            skArc(sketch, "E2175", {"start": v(-7.06, -12.66) * mm, "mid": v(-7.05, -12.63) * mm, "end": v(-7.07, -12.6) * mm});
            skLineSegment(sketch, "E2176", {"start": v(-7.07, -12.6) * mm, "end": v(-7.39, -12.36) * mm});
            skArc(sketch, "E2177", {"start": v(-7.39, -12.36) * mm, "mid": v(-7.42, -12.36) * mm, "end": v(-7.45, -12.37) * mm});
            skLineSegment(sketch, "E2178", {"start": v(-7.45, -12.37) * mm, "end": v(-7.73, -12.75) * mm});
            skArc(sketch, "E2179", {"start": v(-7.73, -12.75) * mm, "mid": v(-7.74, -12.79) * mm, "end": v(-7.72, -12.82) * mm});
            skLineSegment(sketch, "E2180", {"start": v(-7.72, -12.82) * mm, "end": v(-7.4, -13.05) * mm});
            skArc(sketch, "E2181", {"start": v(-7.4, -13.05) * mm, "mid": v(-7.36, -13.06) * mm, "end": v(-7.33, -13.04) * mm});
            skLineSegment(sketch, "E2182", {"start": v(4.6, -10.73) * mm, "end": v(4.6, -10.27) * mm});
            skArc(sketch, "E2183", {"start": v(4.6, -10.27) * mm, "mid": v(4.6, -10.23) * mm, "end": v(4.56, -10.22) * mm});
            skLineSegment(sketch, "E2184", {"start": v(4.56, -10.22) * mm, "end": v(4.16, -10.22) * mm});
            skArc(sketch, "E2185", {"start": v(4.16, -10.22) * mm, "mid": v(4.13, -10.23) * mm, "end": v(4.12, -10.27) * mm});
            skLineSegment(sketch, "E2186", {"start": v(4.12, -10.27) * mm, "end": v(4.12, -10.73) * mm});
            skArc(sketch, "E2187", {"start": v(4.12, -10.73) * mm, "mid": v(4.13, -10.76) * mm, "end": v(4.16, -10.78) * mm});
            skLineSegment(sketch, "E2188", {"start": v(4.16, -10.78) * mm, "end": v(4.56, -10.78) * mm});
            skArc(sketch, "E2189", {"start": v(4.56, -10.78) * mm, "mid": v(4.6, -10.76) * mm, "end": v(4.6, -10.73) * mm});
            skLineSegment(sketch, "E2190", {"start": v(5.48, -10.73) * mm, "end": v(5.48, -10.27) * mm});
            skArc(sketch, "E2191", {"start": v(5.48, -10.27) * mm, "mid": v(5.47, -10.23) * mm, "end": v(5.44, -10.22) * mm});
            skLineSegment(sketch, "E2192", {"start": v(5.44, -10.22) * mm, "end": v(5.04, -10.22) * mm});
            skArc(sketch, "E2193", {"start": v(5.04, -10.22) * mm, "mid": v(5, -10.23) * mm, "end": v(5, -10.27) * mm});
            skLineSegment(sketch, "E2194", {"start": v(5, -10.27) * mm, "end": v(5, -10.73) * mm});
            skArc(sketch, "E2195", {"start": v(5, -10.73) * mm, "mid": v(5, -10.76) * mm, "end": v(5.04, -10.78) * mm});
            skLineSegment(sketch, "E2196", {"start": v(5.04, -10.78) * mm, "end": v(5.44, -10.78) * mm});
            skArc(sketch, "E2197", {"start": v(5.44, -10.78) * mm, "mid": v(5.47, -10.76) * mm, "end": v(5.48, -10.73) * mm});
            skLineSegment(sketch, "E2198", {"start": v(4.97, -7.4) * mm, "end": v(5.43, -7.4) * mm});
            skArc(sketch, "E2199", {"start": v(5.43, -7.4) * mm, "mid": v(5.47, -7.39) * mm, "end": v(5.48, -7.36) * mm});
            skLineSegment(sketch, "E2200", {"start": v(5.48, -7.36) * mm, "end": v(5.48, -6.96) * mm});
            skArc(sketch, "E2201", {"start": v(5.48, -6.96) * mm, "mid": v(5.47, -6.93) * mm, "end": v(5.43, -6.91) * mm});
            skLineSegment(sketch, "E2202", {"start": v(5.43, -6.91) * mm, "end": v(4.97, -6.91) * mm});
            skArc(sketch, "E2203", {"start": v(4.97, -6.91) * mm, "mid": v(4.93, -6.93) * mm, "end": v(4.92, -6.96) * mm});
            skLineSegment(sketch, "E2204", {"start": v(4.92, -6.96) * mm, "end": v(4.92, -7.36) * mm});
            skArc(sketch, "E2205", {"start": v(4.92, -7.36) * mm, "mid": v(4.93, -7.39) * mm, "end": v(4.97, -7.4) * mm});
            skLineSegment(sketch, "E2206", {"start": v(4.97, -8.28) * mm, "end": v(5.43, -8.28) * mm});
            skArc(sketch, "E2207", {"start": v(5.43, -8.28) * mm, "mid": v(5.47, -8.27) * mm, "end": v(5.48, -8.24) * mm});
            skLineSegment(sketch, "E2208", {"start": v(5.48, -8.24) * mm, "end": v(5.48, -7.84) * mm});
            skArc(sketch, "E2209", {"start": v(5.48, -7.84) * mm, "mid": v(5.47, -7.8) * mm, "end": v(5.43, -7.8) * mm});
            skLineSegment(sketch, "E2210", {"start": v(5.43, -7.8) * mm, "end": v(4.97, -7.8) * mm});
            skArc(sketch, "E2211", {"start": v(4.97, -7.8) * mm, "mid": v(4.93, -7.8) * mm, "end": v(4.92, -7.84) * mm});
            skLineSegment(sketch, "E2212", {"start": v(4.92, -7.84) * mm, "end": v(4.92, -8.24) * mm});
            skArc(sketch, "E2213", {"start": v(4.92, -8.24) * mm, "mid": v(4.93, -8.27) * mm, "end": v(4.97, -8.28) * mm});
            skLineSegment(sketch, "E2214", {"start": v(-7.87, -1.6) * mm, "end": v(-8.33, -1.6) * mm});
            skArc(sketch, "E2215", {"start": v(-8.33, -1.6) * mm, "mid": v(-8.37, -1.6) * mm, "end": v(-8.38, -1.64) * mm});
            skLineSegment(sketch, "E2216", {"start": v(-8.38, -1.64) * mm, "end": v(-8.38, -2.04) * mm});
            skArc(sketch, "E2217", {"start": v(-8.38, -2.04) * mm, "mid": v(-8.37, -2.07) * mm, "end": v(-8.33, -2.08) * mm});
            skLineSegment(sketch, "E2218", {"start": v(-8.33, -2.08) * mm, "end": v(-7.87, -2.08) * mm});
            skArc(sketch, "E2219", {"start": v(-7.87, -2.08) * mm, "mid": v(-7.83, -2.07) * mm, "end": v(-7.82, -2.04) * mm});
            skLineSegment(sketch, "E2220", {"start": v(-7.82, -2.04) * mm, "end": v(-7.82, -1.64) * mm});
            skArc(sketch, "E2221", {"start": v(-7.82, -1.64) * mm, "mid": v(-7.83, -1.6) * mm, "end": v(-7.87, -1.6) * mm});
            skLineSegment(sketch, "E2222", {"start": v(-7.87, -0.71) * mm, "end": v(-8.33, -0.71) * mm});
            skArc(sketch, "E2223", {"start": v(-8.33, -0.71) * mm, "mid": v(-8.37, -0.73) * mm, "end": v(-8.38, -0.76) * mm});
            skLineSegment(sketch, "E2224", {"start": v(-8.38, -0.76) * mm, "end": v(-8.38, -1.16) * mm});
            skArc(sketch, "E2225", {"start": v(-8.38, -1.16) * mm, "mid": v(-8.37, -1.19) * mm, "end": v(-8.33, -1.2) * mm});
            skLineSegment(sketch, "E2226", {"start": v(-8.33, -1.2) * mm, "end": v(-7.87, -1.2) * mm});
            skArc(sketch, "E2227", {"start": v(-7.87, -1.2) * mm, "mid": v(-7.83, -1.19) * mm, "end": v(-7.82, -1.16) * mm});
            skLineSegment(sketch, "E2228", {"start": v(-7.82, -1.16) * mm, "end": v(-7.82, -0.76) * mm});
            skArc(sketch, "E2229", {"start": v(-7.82, -0.76) * mm, "mid": v(-7.83, -0.73) * mm, "end": v(-7.87, -0.71) * mm});
            skLineSegment(sketch, "E2230", {"start": v(-5.13, 8.8) * mm, "end": v(-4.67, 8.8) * mm});
            skArc(sketch, "E2231", {"start": v(-4.67, 8.8) * mm, "mid": v(-4.63, 8.81) * mm, "end": v(-4.62, 8.84) * mm});
            skLineSegment(sketch, "E2232", {"start": v(-4.62, 8.84) * mm, "end": v(-4.62, 9.24) * mm});
            skArc(sketch, "E2233", {"start": v(-4.62, 9.24) * mm, "mid": v(-4.63, 9.27) * mm, "end": v(-4.67, 9.29) * mm});
            skLineSegment(sketch, "E2234", {"start": v(-4.67, 9.29) * mm, "end": v(-5.13, 9.29) * mm});
            skArc(sketch, "E2235", {"start": v(-5.13, 9.29) * mm, "mid": v(-5.17, 9.27) * mm, "end": v(-5.18, 9.24) * mm});
            skLineSegment(sketch, "E2236", {"start": v(-5.18, 9.24) * mm, "end": v(-5.18, 8.84) * mm});
            skArc(sketch, "E2237", {"start": v(-5.18, 8.84) * mm, "mid": v(-5.17, 8.81) * mm, "end": v(-5.13, 8.8) * mm});
            skLineSegment(sketch, "E2238", {"start": v(-5.13, 7.92) * mm, "end": v(-4.67, 7.92) * mm});
            skArc(sketch, "E2239", {"start": v(-4.67, 7.92) * mm, "mid": v(-4.63, 7.93) * mm, "end": v(-4.62, 7.96) * mm});
            skLineSegment(sketch, "E2240", {"start": v(-4.62, 7.96) * mm, "end": v(-4.62, 8.36) * mm});
            skArc(sketch, "E2241", {"start": v(-4.62, 8.36) * mm, "mid": v(-4.63, 8.4) * mm, "end": v(-4.67, 8.4) * mm});
            skLineSegment(sketch, "E2242", {"start": v(-4.67, 8.4) * mm, "end": v(-5.13, 8.4) * mm});
            skArc(sketch, "E2243", {"start": v(-5.13, 8.4) * mm, "mid": v(-5.17, 8.4) * mm, "end": v(-5.18, 8.36) * mm});
            skLineSegment(sketch, "E2244", {"start": v(-5.18, 8.36) * mm, "end": v(-5.18, 7.96) * mm});
            skArc(sketch, "E2245", {"start": v(-5.18, 7.96) * mm, "mid": v(-5.17, 7.93) * mm, "end": v(-5.13, 7.92) * mm});
            skLineSegment(sketch, "E2246", {"start": v(5.13, 8.4) * mm, "end": v(4.67, 8.4) * mm});
            skArc(sketch, "E2247", {"start": v(4.67, 8.4) * mm, "mid": v(4.63, 8.4) * mm, "end": v(4.62, 8.36) * mm});
            skLineSegment(sketch, "E2248", {"start": v(4.62, 8.36) * mm, "end": v(4.62, 7.96) * mm});
            skArc(sketch, "E2249", {"start": v(4.62, 7.96) * mm, "mid": v(4.63, 7.93) * mm, "end": v(4.67, 7.92) * mm});
            skLineSegment(sketch, "E2250", {"start": v(4.67, 7.92) * mm, "end": v(5.13, 7.92) * mm});
            skArc(sketch, "E2251", {"start": v(5.13, 7.92) * mm, "mid": v(5.17, 7.93) * mm, "end": v(5.18, 7.96) * mm});
            skLineSegment(sketch, "E2252", {"start": v(5.18, 7.96) * mm, "end": v(5.18, 8.36) * mm});
            skArc(sketch, "E2253", {"start": v(5.18, 8.36) * mm, "mid": v(5.17, 8.4) * mm, "end": v(5.13, 8.4) * mm});
            skLineSegment(sketch, "E2254", {"start": v(5.13, 9.29) * mm, "end": v(4.67, 9.29) * mm});
            skArc(sketch, "E2255", {"start": v(4.67, 9.29) * mm, "mid": v(4.63, 9.27) * mm, "end": v(4.62, 9.24) * mm});
            skLineSegment(sketch, "E2256", {"start": v(4.62, 9.24) * mm, "end": v(4.62, 8.84) * mm});
            skArc(sketch, "E2257", {"start": v(4.62, 8.84) * mm, "mid": v(4.63, 8.81) * mm, "end": v(4.67, 8.8) * mm});
            skLineSegment(sketch, "E2258", {"start": v(4.67, 8.8) * mm, "end": v(5.13, 8.8) * mm});
            skArc(sketch, "E2259", {"start": v(5.13, 8.8) * mm, "mid": v(5.17, 8.81) * mm, "end": v(5.18, 8.84) * mm});
            skLineSegment(sketch, "E2260", {"start": v(5.18, 8.84) * mm, "end": v(5.18, 9.24) * mm});
            skArc(sketch, "E2261", {"start": v(5.18, 9.24) * mm, "mid": v(5.17, 9.27) * mm, "end": v(5.13, 9.29) * mm});
            skLineSegment(sketch, "E2262", {"start": v(5, -11.47) * mm, "end": v(5, -11.93) * mm});
            skArc(sketch, "E2263", {"start": v(5, -11.93) * mm, "mid": v(5, -11.96) * mm, "end": v(5.04, -11.98) * mm});
            skLineSegment(sketch, "E2264", {"start": v(5.04, -11.98) * mm, "end": v(5.44, -11.98) * mm});
            skArc(sketch, "E2265", {"start": v(5.44, -11.98) * mm, "mid": v(5.47, -11.96) * mm, "end": v(5.48, -11.93) * mm});
            skLineSegment(sketch, "E2266", {"start": v(5.48, -11.93) * mm, "end": v(5.48, -11.47) * mm});
            skArc(sketch, "E2267", {"start": v(5.48, -11.47) * mm, "mid": v(5.47, -11.43) * mm, "end": v(5.44, -11.42) * mm});
            skLineSegment(sketch, "E2268", {"start": v(5.44, -11.42) * mm, "end": v(5.04, -11.42) * mm});
            skArc(sketch, "E2269", {"start": v(5.04, -11.42) * mm, "mid": v(5, -11.43) * mm, "end": v(5, -11.47) * mm});
            skLineSegment(sketch, "E2270", {"start": v(4.12, -11.47) * mm, "end": v(4.12, -11.93) * mm});
            skArc(sketch, "E2271", {"start": v(4.12, -11.93) * mm, "mid": v(4.13, -11.96) * mm, "end": v(4.16, -11.98) * mm});
            skLineSegment(sketch, "E2272", {"start": v(4.16, -11.98) * mm, "end": v(4.56, -11.98) * mm});
            skArc(sketch, "E2273", {"start": v(4.56, -11.98) * mm, "mid": v(4.6, -11.96) * mm, "end": v(4.6, -11.93) * mm});
            skLineSegment(sketch, "E2274", {"start": v(4.6, -11.93) * mm, "end": v(4.6, -11.47) * mm});
            skArc(sketch, "E2275", {"start": v(4.6, -11.47) * mm, "mid": v(4.6, -11.43) * mm, "end": v(4.56, -11.42) * mm});
            skLineSegment(sketch, "E2276", {"start": v(4.56, -11.42) * mm, "end": v(4.16, -11.42) * mm});
            skArc(sketch, "E2277", {"start": v(4.16, -11.42) * mm, "mid": v(4.13, -11.43) * mm, "end": v(4.12, -11.47) * mm});
            skLineSegment(sketch, "E2278", {"start": v(-5.43, -7.4) * mm, "end": v(-4.97, -7.4) * mm});
            skArc(sketch, "E2279", {"start": v(-4.97, -7.4) * mm, "mid": v(-4.93, -7.39) * mm, "end": v(-4.92, -7.36) * mm});
            skLineSegment(sketch, "E2280", {"start": v(-4.92, -7.36) * mm, "end": v(-4.92, -6.96) * mm});
            skArc(sketch, "E2281", {"start": v(-4.92, -6.96) * mm, "mid": v(-4.93, -6.93) * mm, "end": v(-4.97, -6.91) * mm});
            skLineSegment(sketch, "E2282", {"start": v(-4.97, -6.91) * mm, "end": v(-5.43, -6.91) * mm});
            skArc(sketch, "E2283", {"start": v(-5.43, -6.91) * mm, "mid": v(-5.47, -6.93) * mm, "end": v(-5.48, -6.96) * mm});
            skLineSegment(sketch, "E2284", {"start": v(-5.48, -6.96) * mm, "end": v(-5.48, -7.36) * mm});
            skArc(sketch, "E2285", {"start": v(-5.48, -7.36) * mm, "mid": v(-5.47, -7.39) * mm, "end": v(-5.43, -7.4) * mm});
            skLineSegment(sketch, "E2286", {"start": v(-5.43, -8.28) * mm, "end": v(-4.97, -8.28) * mm});
            skArc(sketch, "E2287", {"start": v(-4.97, -8.28) * mm, "mid": v(-4.93, -8.27) * mm, "end": v(-4.92, -8.24) * mm});
            skLineSegment(sketch, "E2288", {"start": v(-4.92, -8.24) * mm, "end": v(-4.92, -7.84) * mm});
            skArc(sketch, "E2289", {"start": v(-4.92, -7.84) * mm, "mid": v(-4.93, -7.8) * mm, "end": v(-4.97, -7.8) * mm});
            skLineSegment(sketch, "E2290", {"start": v(-4.97, -7.8) * mm, "end": v(-5.43, -7.8) * mm});
            skArc(sketch, "E2291", {"start": v(-5.43, -7.8) * mm, "mid": v(-5.47, -7.8) * mm, "end": v(-5.48, -7.84) * mm});
            skLineSegment(sketch, "E2292", {"start": v(-5.48, -7.84) * mm, "end": v(-5.48, -8.24) * mm});
            skArc(sketch, "E2293", {"start": v(-5.48, -8.24) * mm, "mid": v(-5.47, -8.27) * mm, "end": v(-5.43, -8.28) * mm});
            skLineSegment(sketch, "E2294", {"start": v(5.87, -13.6) * mm, "end": v(6.15, -13.97) * mm});
            skArc(sketch, "E2295", {"start": v(6.15, -13.97) * mm, "mid": v(6.18, -13.99) * mm, "end": v(6.21, -13.98) * mm});
            skLineSegment(sketch, "E2296", {"start": v(6.21, -13.98) * mm, "end": v(6.53, -13.75) * mm});
            skArc(sketch, "E2297", {"start": v(6.53, -13.75) * mm, "mid": v(6.55, -13.72) * mm, "end": v(6.54, -13.68) * mm});
            skLineSegment(sketch, "E2298", {"start": v(6.54, -13.68) * mm, "end": v(6.27, -13.3) * mm});
            skArc(sketch, "E2299", {"start": v(6.27, -13.3) * mm, "mid": v(6.24, -13.29) * mm, "end": v(6.2, -13.3) * mm});
            skLineSegment(sketch, "E2300", {"start": v(6.2, -13.3) * mm, "end": v(5.88, -13.53) * mm});
            skArc(sketch, "E2301", {"start": v(5.88, -13.53) * mm, "mid": v(5.86, -13.56) * mm, "end": v(5.87, -13.6) * mm});
            skLineSegment(sketch, "E2302", {"start": v(5.16, -14.11) * mm, "end": v(5.43, -14.49) * mm});
            skArc(sketch, "E2303", {"start": v(5.43, -14.49) * mm, "mid": v(5.46, -14.5) * mm, "end": v(5.5, -14.5) * mm});
            skLineSegment(sketch, "E2304", {"start": v(5.5, -14.5) * mm, "end": v(5.82, -14.27) * mm});
            skArc(sketch, "E2305", {"start": v(5.82, -14.27) * mm, "mid": v(5.84, -14.24) * mm, "end": v(5.83, -14.2) * mm});
            skLineSegment(sketch, "E2306", {"start": v(5.83, -14.2) * mm, "end": v(5.55, -13.82) * mm});
            skArc(sketch, "E2307", {"start": v(5.55, -13.82) * mm, "mid": v(5.52, -13.8) * mm, "end": v(5.49, -13.81) * mm});
            skLineSegment(sketch, "E2308", {"start": v(5.49, -13.81) * mm, "end": v(5.17, -14.05) * mm});
            skArc(sketch, "E2309", {"start": v(5.17, -14.05) * mm, "mid": v(5.15, -14.08) * mm, "end": v(5.16, -14.11) * mm});
            skLineSegment(sketch, "E2310", {"start": v(12.6, -0.61) * mm, "end": v(13.04, -0.47) * mm});
            skArc(sketch, "E2311", {"start": v(13.04, -0.47) * mm, "mid": v(13.07, -0.45) * mm, "end": v(13.07, -0.41) * mm});
            skLineSegment(sketch, "E2312", {"start": v(13.07, -0.41) * mm, "end": v(12.95, -0.03) * mm});
            skArc(sketch, "E2313", {"start": v(12.95, -0.03) * mm, "mid": v(12.93, 0) * mm, "end": v(12.89, 0) * mm});
            skLineSegment(sketch, "E2314", {"start": v(12.89, 0) * mm, "end": v(12.45, -0.15) * mm});
            skArc(sketch, "E2315", {"start": v(12.45, -0.15) * mm, "mid": v(12.42, -0.17) * mm, "end": v(12.42, -0.2) * mm});
            skLineSegment(sketch, "E2316", {"start": v(12.42, -0.2) * mm, "end": v(12.54, -0.58) * mm});
            skArc(sketch, "E2317", {"start": v(12.54, -0.58) * mm, "mid": v(12.56, -0.61) * mm, "end": v(12.6, -0.61) * mm});
            skLineSegment(sketch, "E2318", {"start": v(12.87, -1.45) * mm, "end": v(13.31, -1.3) * mm});
            skArc(sketch, "E2319", {"start": v(13.31, -1.3) * mm, "mid": v(13.34, -1.28) * mm, "end": v(13.34, -1.25) * mm});
            skLineSegment(sketch, "E2320", {"start": v(13.34, -1.25) * mm, "end": v(13.22, -0.87) * mm});
            skArc(sketch, "E2321", {"start": v(13.22, -0.87) * mm, "mid": v(13.2, -0.84) * mm, "end": v(13.16, -0.84) * mm});
            skLineSegment(sketch, "E2322", {"start": v(13.16, -0.84) * mm, "end": v(12.72, -0.99) * mm});
            skArc(sketch, "E2323", {"start": v(12.72, -0.99) * mm, "mid": v(12.7, -1) * mm, "end": v(12.69, -1.04) * mm});
            skLineSegment(sketch, "E2324", {"start": v(12.69, -1.04) * mm, "end": v(12.81, -1.42) * mm});
            skArc(sketch, "E2325", {"start": v(12.81, -1.42) * mm, "mid": v(12.83, -1.45) * mm, "end": v(12.87, -1.45) * mm});
            skLineSegment(sketch, "E2326", {"start": v(-3.7, 5.33) * mm, "end": v(-3.7, 4.87) * mm});
            skArc(sketch, "E2327", {"start": v(-3.7, 4.87) * mm, "mid": v(-3.7, 4.83) * mm, "end": v(-3.66, 4.82) * mm});
            skLineSegment(sketch, "E2328", {"start": v(-3.66, 4.82) * mm, "end": v(-3.26, 4.82) * mm});
            skArc(sketch, "E2329", {"start": v(-3.26, 4.82) * mm, "mid": v(-3.23, 4.83) * mm, "end": v(-3.22, 4.87) * mm});
            skLineSegment(sketch, "E2330", {"start": v(-3.22, 4.87) * mm, "end": v(-3.22, 5.33) * mm});
            skArc(sketch, "E2331", {"start": v(-3.22, 5.33) * mm, "mid": v(-3.23, 5.36) * mm, "end": v(-3.26, 5.38) * mm});
            skLineSegment(sketch, "E2332", {"start": v(-3.26, 5.38) * mm, "end": v(-3.66, 5.38) * mm});
            skArc(sketch, "E2333", {"start": v(-3.66, 5.38) * mm, "mid": v(-3.7, 5.36) * mm, "end": v(-3.7, 5.33) * mm});
            skLineSegment(sketch, "E2334", {"start": v(-4.58, 5.33) * mm, "end": v(-4.58, 4.87) * mm});
            skArc(sketch, "E2335", {"start": v(-4.58, 4.87) * mm, "mid": v(-4.57, 4.83) * mm, "end": v(-4.54, 4.82) * mm});
            skLineSegment(sketch, "E2336", {"start": v(-4.54, 4.82) * mm, "end": v(-4.14, 4.82) * mm});
            skArc(sketch, "E2337", {"start": v(-4.14, 4.82) * mm, "mid": v(-4.1, 4.83) * mm, "end": v(-4.1, 4.87) * mm});
            skLineSegment(sketch, "E2338", {"start": v(-4.1, 4.87) * mm, "end": v(-4.1, 5.33) * mm});
            skArc(sketch, "E2339", {"start": v(-4.1, 5.33) * mm, "mid": v(-4.1, 5.36) * mm, "end": v(-4.14, 5.38) * mm});
            skLineSegment(sketch, "E2340", {"start": v(-4.14, 5.38) * mm, "end": v(-4.54, 5.38) * mm});
            skArc(sketch, "E2341", {"start": v(-4.54, 5.38) * mm, "mid": v(-4.57, 5.36) * mm, "end": v(-4.58, 5.33) * mm});
            skLineSegment(sketch, "E2342", {"start": v(-12.96, -0.54) * mm, "end": v(-12.52, -0.68) * mm});
            skArc(sketch, "E2343", {"start": v(-12.52, -0.68) * mm, "mid": v(-12.48, -0.68) * mm, "end": v(-12.46, -0.65) * mm});
            skLineSegment(sketch, "E2344", {"start": v(-12.46, -0.65) * mm, "end": v(-12.34, -0.28) * mm});
            skArc(sketch, "E2345", {"start": v(-12.34, -0.28) * mm, "mid": v(-12.34, -0.24) * mm, "end": v(-12.37, -0.22) * mm});
            skLineSegment(sketch, "E2346", {"start": v(-12.37, -0.22) * mm, "end": v(-12.8, -0.07) * mm});
            skArc(sketch, "E2347", {"start": v(-12.8, -0.07) * mm, "mid": v(-12.85, -0.08) * mm, "end": v(-12.87, -0.1) * mm});
            skLineSegment(sketch, "E2348", {"start": v(-12.87, -0.1) * mm, "end": v(-13, -0.48) * mm});
            skArc(sketch, "E2349", {"start": v(-13, -0.48) * mm, "mid": v(-12.99, -0.52) * mm, "end": v(-12.96, -0.54) * mm});
            skLineSegment(sketch, "E2350", {"start": v(-13.23, -1.38) * mm, "end": v(-12.8, -1.52) * mm});
            skArc(sketch, "E2351", {"start": v(-12.8, -1.52) * mm, "mid": v(-12.75, -1.52) * mm, "end": v(-12.73, -1.5) * mm});
            skLineSegment(sketch, "E2352", {"start": v(-12.73, -1.5) * mm, "end": v(-12.6, -1.11) * mm});
            skArc(sketch, "E2353", {"start": v(-12.6, -1.11) * mm, "mid": v(-12.61, -1.08) * mm, "end": v(-12.64, -1.06) * mm});
            skLineSegment(sketch, "E2354", {"start": v(-12.64, -1.06) * mm, "end": v(-13.08, -0.91) * mm});
            skArc(sketch, "E2355", {"start": v(-13.08, -0.91) * mm, "mid": v(-13.12, -0.91) * mm, "end": v(-13.14, -0.94) * mm});
            skLineSegment(sketch, "E2356", {"start": v(-13.14, -0.94) * mm, "end": v(-13.26, -1.32) * mm});
            skArc(sketch, "E2357", {"start": v(-13.26, -1.32) * mm, "mid": v(-13.26, -1.35) * mm, "end": v(-13.23, -1.38) * mm});
            skLineSegment(sketch, "E2358", {"start": v(-6.13, -13.94) * mm, "end": v(-5.85, -13.56) * mm});
            skArc(sketch, "E2359", {"start": v(-5.85, -13.56) * mm, "mid": v(-5.84, -13.53) * mm, "end": v(-5.86, -13.5) * mm});
            skLineSegment(sketch, "E2360", {"start": v(-5.86, -13.5) * mm, "end": v(-6.18, -13.27) * mm});
            skArc(sketch, "E2361", {"start": v(-6.18, -13.27) * mm, "mid": v(-6.22, -13.26) * mm, "end": v(-6.25, -13.28) * mm});
            skLineSegment(sketch, "E2362", {"start": v(-6.25, -13.28) * mm, "end": v(-6.52, -13.65) * mm});
            skArc(sketch, "E2363", {"start": v(-6.52, -13.65) * mm, "mid": v(-6.53, -13.69) * mm, "end": v(-6.51, -13.72) * mm});
            skLineSegment(sketch, "E2364", {"start": v(-6.51, -13.72) * mm, "end": v(-6.2, -13.95) * mm});
            skArc(sketch, "E2365", {"start": v(-6.2, -13.95) * mm, "mid": v(-6.16, -13.96) * mm, "end": v(-6.13, -13.94) * mm});
            skLineSegment(sketch, "E2366", {"start": v(-5.41, -14.46) * mm, "end": v(-5.14, -14.08) * mm});
            skArc(sketch, "E2367", {"start": v(-5.14, -14.08) * mm, "mid": v(-5.13, -14.05) * mm, "end": v(-5.15, -14.02) * mm});
            skLineSegment(sketch, "E2368", {"start": v(-5.15, -14.02) * mm, "end": v(-5.47, -13.78) * mm});
            skArc(sketch, "E2369", {"start": v(-5.47, -13.78) * mm, "mid": v(-5.5, -13.78) * mm, "end": v(-5.53, -13.8) * mm});
            skLineSegment(sketch, "E2370", {"start": v(-5.53, -13.8) * mm, "end": v(-5.8, -14.17) * mm});
            skArc(sketch, "E2371", {"start": v(-5.8, -14.17) * mm, "mid": v(-5.82, -14.2) * mm, "end": v(-5.8, -14.24) * mm});
            skLineSegment(sketch, "E2372", {"start": v(-5.8, -14.24) * mm, "end": v(-5.48, -14.47) * mm});
            skArc(sketch, "E2373", {"start": v(-5.48, -14.47) * mm, "mid": v(-5.44, -14.48) * mm, "end": v(-5.41, -14.46) * mm});
            skLineSegment(sketch, "E2374", {"start": v(8.3, -2.97) * mm, "end": v(8.3, -3.43) * mm});
            skArc(sketch, "E2375", {"start": v(8.3, -3.43) * mm, "mid": v(8.3, -3.46) * mm, "end": v(8.34, -3.48) * mm});
            skLineSegment(sketch, "E2376", {"start": v(8.34, -3.48) * mm, "end": v(8.74, -3.48) * mm});
            skArc(sketch, "E2377", {"start": v(8.74, -3.48) * mm, "mid": v(8.77, -3.46) * mm, "end": v(8.78, -3.43) * mm});
            skLineSegment(sketch, "E2378", {"start": v(8.78, -3.43) * mm, "end": v(8.78, -2.97) * mm});
            skArc(sketch, "E2379", {"start": v(8.78, -2.97) * mm, "mid": v(8.77, -2.93) * mm, "end": v(8.74, -2.92) * mm});
            skLineSegment(sketch, "E2380", {"start": v(8.74, -2.92) * mm, "end": v(8.34, -2.92) * mm});
            skArc(sketch, "E2381", {"start": v(8.34, -2.92) * mm, "mid": v(8.3, -2.93) * mm, "end": v(8.3, -2.97) * mm});
            skLineSegment(sketch, "E2382", {"start": v(7.42, -2.97) * mm, "end": v(7.42, -3.43) * mm});
            skArc(sketch, "E2383", {"start": v(7.42, -3.43) * mm, "mid": v(7.43, -3.46) * mm, "end": v(7.46, -3.48) * mm});
            skLineSegment(sketch, "E2384", {"start": v(7.46, -3.48) * mm, "end": v(7.86, -3.48) * mm});
            skArc(sketch, "E2385", {"start": v(7.86, -3.48) * mm, "mid": v(7.9, -3.46) * mm, "end": v(7.9, -3.43) * mm});
            skLineSegment(sketch, "E2386", {"start": v(7.9, -3.43) * mm, "end": v(7.9, -2.97) * mm});
            skArc(sketch, "E2387", {"start": v(7.9, -2.97) * mm, "mid": v(7.9, -2.93) * mm, "end": v(7.86, -2.92) * mm});
            skLineSegment(sketch, "E2388", {"start": v(7.86, -2.92) * mm, "end": v(7.46, -2.92) * mm});
            skArc(sketch, "E2389", {"start": v(7.46, -2.92) * mm, "mid": v(7.43, -2.93) * mm, "end": v(7.42, -2.97) * mm});
            skLineSegment(sketch, "E2390", {"start": v(7.4, 1.67) * mm, "end": v(7.4, 2.13) * mm});
            skArc(sketch, "E2391", {"start": v(7.4, 2.13) * mm, "mid": v(7.4, 2.17) * mm, "end": v(7.36, 2.18) * mm});
            skLineSegment(sketch, "E2392", {"start": v(7.36, 2.18) * mm, "end": v(6.96, 2.18) * mm});
            skArc(sketch, "E2393", {"start": v(6.96, 2.18) * mm, "mid": v(6.93, 2.17) * mm, "end": v(6.92, 2.13) * mm});
            skLineSegment(sketch, "E2394", {"start": v(6.92, 2.13) * mm, "end": v(6.92, 1.67) * mm});
            skArc(sketch, "E2395", {"start": v(6.92, 1.67) * mm, "mid": v(6.93, 1.64) * mm, "end": v(6.96, 1.62) * mm});
            skLineSegment(sketch, "E2396", {"start": v(6.96, 1.62) * mm, "end": v(7.36, 1.62) * mm});
            skArc(sketch, "E2397", {"start": v(7.36, 1.62) * mm, "mid": v(7.4, 1.64) * mm, "end": v(7.4, 1.67) * mm});
            skLineSegment(sketch, "E2398", {"start": v(8.28, 1.67) * mm, "end": v(8.28, 2.13) * mm});
            skArc(sketch, "E2399", {"start": v(8.28, 2.13) * mm, "mid": v(8.27, 2.17) * mm, "end": v(8.24, 2.18) * mm});
            skLineSegment(sketch, "E2400", {"start": v(8.24, 2.18) * mm, "end": v(7.84, 2.18) * mm});
            skArc(sketch, "E2401", {"start": v(7.84, 2.18) * mm, "mid": v(7.8, 2.17) * mm, "end": v(7.8, 2.13) * mm});
            skLineSegment(sketch, "E2402", {"start": v(7.8, 2.13) * mm, "end": v(7.8, 1.67) * mm});
            skArc(sketch, "E2403", {"start": v(7.8, 1.67) * mm, "mid": v(7.8, 1.64) * mm, "end": v(7.84, 1.62) * mm});
            skLineSegment(sketch, "E2404", {"start": v(7.84, 1.62) * mm, "end": v(8.24, 1.62) * mm});
            skArc(sketch, "E2405", {"start": v(8.24, 1.62) * mm, "mid": v(8.27, 1.64) * mm, "end": v(8.28, 1.67) * mm});
            skLineSegment(sketch, "E2406", {"start": v(8.3, -1.77) * mm, "end": v(8.3, -2.23) * mm});
            skArc(sketch, "E2407", {"start": v(8.3, -2.23) * mm, "mid": v(8.3, -2.26) * mm, "end": v(8.34, -2.28) * mm});
            skLineSegment(sketch, "E2408", {"start": v(8.34, -2.28) * mm, "end": v(8.74, -2.28) * mm});
            skArc(sketch, "E2409", {"start": v(8.74, -2.28) * mm, "mid": v(8.77, -2.26) * mm, "end": v(8.78, -2.23) * mm});
            skLineSegment(sketch, "E2410", {"start": v(8.78, -2.23) * mm, "end": v(8.78, -1.77) * mm});
            skArc(sketch, "E2411", {"start": v(8.78, -1.77) * mm, "mid": v(8.77, -1.73) * mm, "end": v(8.74, -1.72) * mm});
            skLineSegment(sketch, "E2412", {"start": v(8.74, -1.72) * mm, "end": v(8.34, -1.72) * mm});
            skArc(sketch, "E2413", {"start": v(8.34, -1.72) * mm, "mid": v(8.3, -1.73) * mm, "end": v(8.3, -1.77) * mm});
            skLineSegment(sketch, "E2414", {"start": v(7.42, -1.77) * mm, "end": v(7.42, -2.23) * mm});
            skArc(sketch, "E2415", {"start": v(7.42, -2.23) * mm, "mid": v(7.43, -2.26) * mm, "end": v(7.46, -2.28) * mm});
            skLineSegment(sketch, "E2416", {"start": v(7.46, -2.28) * mm, "end": v(7.86, -2.28) * mm});
            skArc(sketch, "E2417", {"start": v(7.86, -2.28) * mm, "mid": v(7.9, -2.26) * mm, "end": v(7.9, -2.23) * mm});
            skLineSegment(sketch, "E2418", {"start": v(7.9, -2.23) * mm, "end": v(7.9, -1.77) * mm});
            skArc(sketch, "E2419", {"start": v(7.9, -1.77) * mm, "mid": v(7.9, -1.73) * mm, "end": v(7.86, -1.72) * mm});
            skLineSegment(sketch, "E2420", {"start": v(7.86, -1.72) * mm, "end": v(7.46, -1.72) * mm});
            skArc(sketch, "E2421", {"start": v(7.46, -1.72) * mm, "mid": v(7.43, -1.73) * mm, "end": v(7.42, -1.77) * mm});
            skLineSegment(sketch, "E2422", {"start": v(3.7, 4.87) * mm, "end": v(3.7, 5.33) * mm});
            skArc(sketch, "E2423", {"start": v(3.7, 5.33) * mm, "mid": v(3.7, 5.36) * mm, "end": v(3.66, 5.38) * mm});
            skLineSegment(sketch, "E2424", {"start": v(3.66, 5.38) * mm, "end": v(3.26, 5.38) * mm});
            skArc(sketch, "E2425", {"start": v(3.26, 5.38) * mm, "mid": v(3.23, 5.36) * mm, "end": v(3.22, 5.33) * mm});
            skLineSegment(sketch, "E2426", {"start": v(3.22, 5.33) * mm, "end": v(3.22, 4.87) * mm});
            skArc(sketch, "E2427", {"start": v(3.22, 4.87) * mm, "mid": v(3.23, 4.83) * mm, "end": v(3.26, 4.82) * mm});
            skLineSegment(sketch, "E2428", {"start": v(3.26, 4.82) * mm, "end": v(3.66, 4.82) * mm});
            skArc(sketch, "E2429", {"start": v(3.66, 4.82) * mm, "mid": v(3.7, 4.83) * mm, "end": v(3.7, 4.87) * mm});
            skLineSegment(sketch, "E2430", {"start": v(4.58, 4.87) * mm, "end": v(4.58, 5.33) * mm});
            skArc(sketch, "E2431", {"start": v(4.58, 5.33) * mm, "mid": v(4.57, 5.36) * mm, "end": v(4.54, 5.38) * mm});
            skLineSegment(sketch, "E2432", {"start": v(4.54, 5.38) * mm, "end": v(4.14, 5.38) * mm});
            skArc(sketch, "E2433", {"start": v(4.14, 5.38) * mm, "mid": v(4.1, 5.36) * mm, "end": v(4.1, 5.33) * mm});
            skLineSegment(sketch, "E2434", {"start": v(4.1, 5.33) * mm, "end": v(4.1, 4.87) * mm});
            skArc(sketch, "E2435", {"start": v(4.1, 4.87) * mm, "mid": v(4.1, 4.83) * mm, "end": v(4.14, 4.82) * mm});
            skLineSegment(sketch, "E2436", {"start": v(4.14, 4.82) * mm, "end": v(4.54, 4.82) * mm});
            skArc(sketch, "E2437", {"start": v(4.54, 4.82) * mm, "mid": v(4.57, 4.83) * mm, "end": v(4.58, 4.87) * mm});
            skLineSegment(sketch, "E2438", {"start": v(8.3, -4.17) * mm, "end": v(8.3, -4.63) * mm});
            skArc(sketch, "E2439", {"start": v(8.3, -4.63) * mm, "mid": v(8.3, -4.66) * mm, "end": v(8.34, -4.68) * mm});
            skLineSegment(sketch, "E2440", {"start": v(8.34, -4.68) * mm, "end": v(8.74, -4.68) * mm});
            skArc(sketch, "E2441", {"start": v(8.74, -4.68) * mm, "mid": v(8.77, -4.66) * mm, "end": v(8.78, -4.63) * mm});
            skLineSegment(sketch, "E2442", {"start": v(8.78, -4.63) * mm, "end": v(8.78, -4.17) * mm});
            skArc(sketch, "E2443", {"start": v(8.78, -4.17) * mm, "mid": v(8.77, -4.13) * mm, "end": v(8.74, -4.12) * mm});
            skLineSegment(sketch, "E2444", {"start": v(8.74, -4.12) * mm, "end": v(8.34, -4.12) * mm});
            skArc(sketch, "E2445", {"start": v(8.34, -4.12) * mm, "mid": v(8.3, -4.13) * mm, "end": v(8.3, -4.17) * mm});
            skLineSegment(sketch, "E2446", {"start": v(7.42, -4.17) * mm, "end": v(7.42, -4.63) * mm});
            skArc(sketch, "E2447", {"start": v(7.42, -4.63) * mm, "mid": v(7.43, -4.66) * mm, "end": v(7.46, -4.68) * mm});
            skLineSegment(sketch, "E2448", {"start": v(7.46, -4.68) * mm, "end": v(7.86, -4.68) * mm});
            skArc(sketch, "E2449", {"start": v(7.86, -4.68) * mm, "mid": v(7.9, -4.66) * mm, "end": v(7.9, -4.63) * mm});
            skLineSegment(sketch, "E2450", {"start": v(7.9, -4.63) * mm, "end": v(7.9, -4.17) * mm});
            skArc(sketch, "E2451", {"start": v(7.9, -4.17) * mm, "mid": v(7.9, -4.13) * mm, "end": v(7.86, -4.12) * mm});
            skLineSegment(sketch, "E2452", {"start": v(7.86, -4.12) * mm, "end": v(7.46, -4.12) * mm});
            skArc(sketch, "E2453", {"start": v(7.46, -4.12) * mm, "mid": v(7.43, -4.13) * mm, "end": v(7.42, -4.17) * mm});
            skLineSegment(sketch, "E2454", {"start": v(-20.4, 1.89) * mm, "end": v(-16.97, 0.79) * mm});
            skArc(sketch, "E2455", {"start": v(-17.01, 0.67) * mm, "mid": v(-16.85, 0.75) * mm, "end": v(-16.93, 0.9) * mm});
            skArc(sketch, "E2456", {"start": v(-20.36, 2) * mm, "mid": v(-20.52, 1.93) * mm, "end": v(-20.44, 1.77) * mm});
            skLineSegment(sketch, "E2457", {"start": v(-16.97, 0.79) * mm, "end": v(-16.75, 0.75) * mm});
            skArc(sketch, "E2458", {"start": v(-16.77, 0.63) * mm, "mid": v(-16.63, 0.73) * mm, "end": v(-16.73, 0.87) * mm});
            skArc(sketch, "E2459", {"start": v(-16.95, 0.9) * mm, "mid": v(-17.1, 0.8) * mm, "end": v(-17, 0.66) * mm});
            skLineSegment(sketch, "E2460", {"start": v(-16.75, 0.75) * mm, "end": v(-16.53, 0.74) * mm});
            skArc(sketch, "E2461", {"start": v(-16.53, 0.61) * mm, "mid": v(-16.4, 0.73) * mm, "end": v(-16.52, 0.86) * mm});
            skArc(sketch, "E2462", {"start": v(-16.74, 0.88) * mm, "mid": v(-16.87, 0.76) * mm, "end": v(-16.76, 0.63) * mm});
            skLineSegment(sketch, "E2463", {"start": v(-16.53, 0.74) * mm, "end": v(-16.3, 0.75) * mm});
            skArc(sketch, "E2464", {"start": v(-16.3, 0.62) * mm, "mid": v(-16.18, 0.75) * mm, "end": v(-16.31, 0.87) * mm});
            skArc(sketch, "E2465", {"start": v(-16.53, 0.86) * mm, "mid": v(-16.65, 0.73) * mm, "end": v(-16.52, 0.61) * mm});
            skLineSegment(sketch, "E2466", {"start": v(-16.3, 0.75) * mm, "end": v(-16.1, 0.78) * mm});
            skArc(sketch, "E2467", {"start": v(-16.07, 0.65) * mm, "mid": v(-15.97, 0.8) * mm, "end": v(-16.1, 0.9) * mm});
            skArc(sketch, "E2468", {"start": v(-16.32, 0.87) * mm, "mid": v(-16.43, 0.73) * mm, "end": v(-16.3, 0.62) * mm});
            skLineSegment(sketch, "E2469", {"start": v(-16.1, 0.78) * mm, "end": v(-15.88, 0.83) * mm});
            skArc(sketch, "E2470", {"start": v(-15.85, 0.7) * mm, "mid": v(-15.76, 0.86) * mm, "end": v(-15.91, 0.95) * mm});
            skArc(sketch, "E2471", {"start": v(-16.12, 0.9) * mm, "mid": v(-16.21, 0.75) * mm, "end": v(-16.06, 0.66) * mm});
            skLineSegment(sketch, "E2472", {"start": v(-15.88, 0.83) * mm, "end": v(-15.68, 0.9) * mm});
            skArc(sketch, "E2473", {"start": v(-15.64, 0.78) * mm, "mid": v(-15.56, 0.94) * mm, "end": v(-15.72, 1.02) * mm});
            skArc(sketch, "E2474", {"start": v(-15.92, 0.95) * mm, "mid": v(-16, 0.79) * mm, "end": v(-15.84, 0.71) * mm});
            skLineSegment(sketch, "E2475", {"start": v(-15.68, 0.9) * mm, "end": v(-15.48, 0.99) * mm});
            skArc(sketch, "E2476", {"start": v(-15.43, 0.88) * mm, "mid": v(-15.37, 1.04) * mm, "end": v(-15.53, 1.1) * mm});
            skArc(sketch, "E2477", {"start": v(-15.73, 1.01) * mm, "mid": v(-15.79, 0.85) * mm, "end": v(-15.62, 0.79) * mm});
            skLineSegment(sketch, "E2478", {"start": v(-15.48, 0.99) * mm, "end": v(-15.3, 1.1) * mm});
            skArc(sketch, "E2479", {"start": v(-15.23, 0.99) * mm, "mid": v(-15.18, 1.16) * mm, "end": v(-15.36, 1.2) * mm});
            skArc(sketch, "E2480", {"start": v(-15.54, 1.1) * mm, "mid": v(-15.59, 0.93) * mm, "end": v(-15.42, 0.88) * mm});
            skLineSegment(sketch, "E2481", {"start": v(-15.3, 1.1) * mm, "end": v(-15.12, 1.22) * mm});
            skArc(sketch, "E2482", {"start": v(-15.04, 1.12) * mm, "mid": v(-15.01, 1.3) * mm, "end": v(-15.19, 1.33) * mm});
            skArc(sketch, "E2483", {"start": v(-15.37, 1.2) * mm, "mid": v(-15.4, 1.02) * mm, "end": v(-15.22, 1) * mm});
            skLineSegment(sketch, "E2484", {"start": v(-15.12, 1.22) * mm, "end": v(-14.95, 1.37) * mm});
            skArc(sketch, "E2485", {"start": v(-14.87, 1.27) * mm, "mid": v(-14.86, 1.45) * mm, "end": v(-15.03, 1.46) * mm});
            skArc(sketch, "E2486", {"start": v(-15.2, 1.32) * mm, "mid": v(-15.21, 1.14) * mm, "end": v(-15.03, 1.13) * mm});
            skLineSegment(sketch, "E2487", {"start": v(-14.95, 1.37) * mm, "end": v(-14.8, 1.52) * mm});
            skArc(sketch, "E2488", {"start": v(-14.71, 1.44) * mm, "mid": v(-14.72, 1.62) * mm, "end": v(-14.9, 1.61) * mm});
            skArc(sketch, "E2489", {"start": v(-15.04, 1.45) * mm, "mid": v(-15.04, 1.27) * mm, "end": v(-14.86, 1.28) * mm});
            skLineSegment(sketch, "E2490", {"start": v(-14.8, 1.52) * mm, "end": v(-14.67, 1.7) * mm});
            skArc(sketch, "E2491", {"start": v(-14.57, 1.62) * mm, "mid": v(-14.6, 1.8) * mm, "end": v(-14.77, 1.77) * mm});
            skArc(sketch, "E2492", {"start": v(-14.9, 1.6) * mm, "mid": v(-14.88, 1.43) * mm, "end": v(-14.7, 1.45) * mm});
            skLineSegment(sketch, "E2493", {"start": v(-14.67, 1.7) * mm, "end": v(-14.55, 1.89) * mm});
            skArc(sketch, "E2494", {"start": v(-14.44, 1.82) * mm, "mid": v(-14.48, 2) * mm, "end": v(-14.66, 1.95) * mm});
            skArc(sketch, "E2495", {"start": v(-14.77, 1.76) * mm, "mid": v(-14.73, 1.6) * mm, "end": v(-14.56, 1.63) * mm});
            skLineSegment(sketch, "E2496", {"start": v(-14.55, 1.89) * mm, "end": v(-14.45, 2.09) * mm});
            skArc(sketch, "E2497", {"start": v(-14.34, 2.03) * mm, "mid": v(-14.4, 2.2) * mm, "end": v(-14.56, 2.15) * mm});
            skArc(sketch, "E2498", {"start": v(-14.66, 1.94) * mm, "mid": v(-14.6, 1.77) * mm, "end": v(-14.44, 1.83) * mm});
            skLineSegment(sketch, "E2499", {"start": v(-14.45, 2.09) * mm, "end": v(-14.37, 2.3) * mm});
            skArc(sketch, "E2500", {"start": v(-14.26, 2.25) * mm, "mid": v(-14.33, 2.4) * mm, "end": v(-14.49, 2.34) * mm});
            skArc(sketch, "E2501", {"start": v(-14.57, 2.13) * mm, "mid": v(-14.5, 1.97) * mm, "end": v(-14.33, 2.05) * mm});
            skLineSegment(sketch, "E2502", {"start": v(-14.37, 2.3) * mm, "end": v(-14.3, 2.53) * mm});
            skArc(sketch, "E2503", {"start": v(-14.19, 2.5) * mm, "mid": v(-14.28, 2.65) * mm, "end": v(-14.43, 2.56) * mm});
            skArc(sketch, "E2504", {"start": v(-14.5, 2.33) * mm, "mid": v(-14.4, 2.17) * mm, "end": v(-14.25, 2.26) * mm});
            skLineSegment(sketch, "E2505", {"start": v(-14.3, 2.53) * mm, "end": v(-14.27, 2.75) * mm});
            skArc(sketch, "E2506", {"start": v(-14.15, 2.73) * mm, "mid": v(-14.25, 2.88) * mm, "end": v(-14.4, 2.77) * mm});
            skArc(sketch, "E2507", {"start": v(-14.43, 2.55) * mm, "mid": v(-14.33, 2.4) * mm, "end": v(-14.19, 2.5) * mm});
            skLineSegment(sketch, "E2508", {"start": v(-14.27, 2.75) * mm, "end": v(-14.26, 2.97) * mm});
            skArc(sketch, "E2509", {"start": v(-14.14, 2.97) * mm, "mid": v(-14.25, 3.1) * mm, "end": v(-14.39, 2.98) * mm});
            skArc(sketch, "E2510", {"start": v(-14.4, 2.76) * mm, "mid": v(-14.28, 2.63) * mm, "end": v(-14.15, 2.74) * mm});
            skLineSegment(sketch, "E2511", {"start": v(-14.26, 2.97) * mm, "end": v(-14.27, 3.2) * mm});
            skArc(sketch, "E2512", {"start": v(-14.15, 3.2) * mm, "mid": v(-14.28, 3.32) * mm, "end": v(-14.4, 3.19) * mm});
            skArc(sketch, "E2513", {"start": v(-14.39, 2.97) * mm, "mid": v(-14.26, 2.85) * mm, "end": v(-14.14, 2.98) * mm});
            skLineSegment(sketch, "E2514", {"start": v(-14.27, 3.2) * mm, "end": v(-14.3, 3.4) * mm});
            skArc(sketch, "E2515", {"start": v(-14.18, 3.43) * mm, "mid": v(-14.32, 3.53) * mm, "end": v(-14.42, 3.4) * mm});
            skArc(sketch, "E2516", {"start": v(-14.4, 3.18) * mm, "mid": v(-14.25, 3.07) * mm, "end": v(-14.15, 3.21) * mm});
            skLineSegment(sketch, "E2517", {"start": v(-14.3, 3.4) * mm, "end": v(-14.35, 3.62) * mm});
            skArc(sketch, "E2518", {"start": v(-14.23, 3.65) * mm, "mid": v(-14.38, 3.74) * mm, "end": v(-14.47, 3.6) * mm});
            skArc(sketch, "E2519", {"start": v(-14.42, 3.38) * mm, "mid": v(-14.27, 3.29) * mm, "end": v(-14.18, 3.44) * mm});
            skLineSegment(sketch, "E2520", {"start": v(-14.35, 3.62) * mm, "end": v(-14.42, 3.82) * mm});
            skArc(sketch, "E2521", {"start": v(-14.3, 3.87) * mm, "mid": v(-14.46, 3.94) * mm, "end": v(-14.54, 3.78) * mm});
            skArc(sketch, "E2522", {"start": v(-14.47, 3.58) * mm, "mid": v(-14.31, 3.5) * mm, "end": v(-14.23, 3.66) * mm});
            skLineSegment(sketch, "E2523", {"start": v(-14.42, 3.82) * mm, "end": v(-14.51, 4.02) * mm});
            skArc(sketch, "E2524", {"start": v(-14.4, 4.07) * mm, "mid": v(-14.56, 4.13) * mm, "end": v(-14.63, 3.97) * mm});
            skArc(sketch, "E2525", {"start": v(-14.54, 3.77) * mm, "mid": v(-14.37, 3.71) * mm, "end": v(-14.3, 3.88) * mm});
            skLineSegment(sketch, "E2526", {"start": v(-14.51, 4.02) * mm, "end": v(-14.62, 4.2) * mm});
            skArc(sketch, "E2527", {"start": v(-14.51, 4.27) * mm, "mid": v(-14.68, 4.32) * mm, "end": v(-14.73, 4.15) * mm});
            skArc(sketch, "E2528", {"start": v(-14.62, 3.96) * mm, "mid": v(-14.45, 3.91) * mm, "end": v(-14.4, 4.08) * mm});
            skLineSegment(sketch, "E2529", {"start": v(-14.62, 4.2) * mm, "end": v(-14.75, 4.38) * mm});
            skArc(sketch, "E2530", {"start": v(-14.64, 4.46) * mm, "mid": v(-14.82, 4.49) * mm, "end": v(-14.85, 4.31) * mm});
            skArc(sketch, "E2531", {"start": v(-14.72, 4.14) * mm, "mid": v(-14.55, 4.1) * mm, "end": v(-14.52, 4.28) * mm});
            skLineSegment(sketch, "E2532", {"start": v(-14.75, 4.38) * mm, "end": v(-14.89, 4.55) * mm});
            skArc(sketch, "E2533", {"start": v(-14.8, 4.63) * mm, "mid": v(-14.97, 4.64) * mm, "end": v(-14.98, 4.47) * mm});
            skArc(sketch, "E2534", {"start": v(-14.84, 4.3) * mm, "mid": v(-14.66, 4.29) * mm, "end": v(-14.65, 4.47) * mm});
            skLineSegment(sketch, "E2535", {"start": v(-14.89, 4.55) * mm, "end": v(-15.05, 4.7) * mm});
            skArc(sketch, "E2536", {"start": v(-14.96, 4.79) * mm, "mid": v(-15.14, 4.78) * mm, "end": v(-15.13, 4.6) * mm});
            skArc(sketch, "E2537", {"start": v(-14.97, 4.46) * mm, "mid": v(-14.8, 4.46) * mm, "end": v(-14.8, 4.64) * mm});
            skLineSegment(sketch, "E2538", {"start": v(-15.05, 4.7) * mm, "end": v(-15.22, 4.83) * mm});
            skArc(sketch, "E2539", {"start": v(-15.14, 4.93) * mm, "mid": v(-15.32, 4.9) * mm, "end": v(-15.3, 4.73) * mm});
            skArc(sketch, "E2540", {"start": v(-15.12, 4.6) * mm, "mid": v(-14.95, 4.62) * mm, "end": v(-14.97, 4.8) * mm});
            skLineSegment(sketch, "E2541", {"start": v(-15.22, 4.83) * mm, "end": v(-15.41, 4.95) * mm});
            skArc(sketch, "E2542", {"start": v(-15.34, 5.06) * mm, "mid": v(-15.52, 5.02) * mm, "end": v(-15.48, 4.85) * mm});
            skArc(sketch, "E2543", {"start": v(-15.29, 4.73) * mm, "mid": v(-15.12, 4.77) * mm, "end": v(-15.16, 4.94) * mm});
            skLineSegment(sketch, "E2544", {"start": v(-15.41, 4.95) * mm, "end": v(-15.61, 5.05) * mm});
            skArc(sketch, "E2545", {"start": v(-15.56, 5.16) * mm, "mid": v(-15.72, 5.1) * mm, "end": v(-15.67, 4.94) * mm});
            skArc(sketch, "E2546", {"start": v(-15.47, 4.84) * mm, "mid": v(-15.3, 4.9) * mm, "end": v(-15.35, 5.06) * mm});
            skLineSegment(sketch, "E2547", {"start": v(-15.61, 5.05) * mm, "end": v(-15.84, 5.14) * mm});
            skArc(sketch, "E2548", {"start": v(-15.8, 5.26) * mm, "mid": v(-15.96, 5.18) * mm, "end": v(-15.89, 5.02) * mm});
            skArc(sketch, "E2549", {"start": v(-15.66, 4.93) * mm, "mid": v(-15.5, 5) * mm, "end": v(-15.57, 5.17) * mm});
            skLineSegment(sketch, "E2550", {"start": v(-15.84, 5.14) * mm, "end": v(-19.01, 6.17) * mm});
            skArc(sketch, "E2551", {"start": v(-18.97, 6.29) * mm, "mid": v(-19.13, 6.2) * mm, "end": v(-19.05, 6.05) * mm});
            skArc(sketch, "E2552", {"start": v(-15.88, 5.02) * mm, "mid": v(-15.73, 5.1) * mm, "end": v(-15.8, 5.26) * mm});
            skLineSegment(sketch, "E2553", {"start": v(-19.01, 6.17) * mm, "end": v(-21.34, 6.17) * mm});
            skArc(sketch, "E2554", {"start": v(-21.34, 6.3) * mm, "mid": v(-21.47, 6.17) * mm, "end": v(-21.34, 6.04) * mm});
            skArc(sketch, "E2555", {"start": v(-19.01, 6.04) * mm, "mid": v(-18.89, 6.17) * mm, "end": v(-19.01, 6.3) * mm});
            skLineSegment(sketch, "E2556", {"start": v(-21.34, 6.17) * mm, "end": v(-22.36, 5.9) * mm});
            skArc(sketch, "E2557", {"start": v(-22.4, 6.01) * mm, "mid": v(-22.48, 5.86) * mm, "end": v(-22.33, 5.77) * mm});
            skArc(sketch, "E2558", {"start": v(-21.3, 6.05) * mm, "mid": v(-21.22, 6.2) * mm, "end": v(-21.37, 6.29) * mm});
            skLineSegment(sketch, "E2559", {"start": v(-22.36, 5.9) * mm, "end": v(-22.95, 4.08) * mm});
            skArc(sketch, "E2560", {"start": v(-23.07, 4.12) * mm, "mid": v(-22.99, 3.96) * mm, "end": v(-22.83, 4.04) * mm});
            skArc(sketch, "E2561", {"start": v(-22.24, 5.85) * mm, "mid": v(-22.32, 6.01) * mm, "end": v(-22.48, 5.93) * mm});
            skLineSegment(sketch, "E2562", {"start": v(-22.95, 4.08) * mm, "end": v(-22.29, 3.26) * mm});
            skArc(sketch, "E2563", {"start": v(-22.38, 3.18) * mm, "mid": v(-22.2, 3.16) * mm, "end": v(-22.19, 3.34) * mm});
            skArc(sketch, "E2564", {"start": v(-22.85, 4.16) * mm, "mid": v(-23.03, 4.18) * mm, "end": v(-23.05, 4) * mm});
            skLineSegment(sketch, "E2565", {"start": v(-22.29, 3.26) * mm, "end": v(-20.4, 1.89) * mm});
            skArc(sketch, "E2566", {"start": v(-20.47, 1.79) * mm, "mid": v(-20.3, 1.81) * mm, "end": v(-20.33, 1.99) * mm});
            skArc(sketch, "E2567", {"start": v(-22.21, 3.36) * mm, "mid": v(-22.39, 3.33) * mm, "end": v(-22.36, 3.16) * mm});
            skLineSegment(sketch, "E2568", {"start": v(-14.93, 1.4) * mm, "end": v(-14.3, 3.35) * mm});
            skArc(sketch, "E2569", {"start": v(-14.17, 3.31) * mm, "mid": v(-14.25, 3.47) * mm, "end": v(-14.41, 3.39) * mm});
            skArc(sketch, "E2570", {"start": v(-15.05, 1.43) * mm, "mid": v(-14.97, 1.27) * mm, "end": v(-14.8, 1.35) * mm});
            skLineSegment(sketch, "E2571", {"start": v(-15.6, 0.93) * mm, "end": v(-14.57, 4.12) * mm});
            skArc(sketch, "E2572", {"start": v(-14.45, 4.08) * mm, "mid": v(-14.53, 4.24) * mm, "end": v(-14.69, 4.16) * mm});
            skArc(sketch, "E2573", {"start": v(-15.72, 0.97) * mm, "mid": v(-15.64, 0.81) * mm, "end": v(-15.48, 0.9) * mm});
            skLineSegment(sketch, "E2574", {"start": v(-16.18, 0.76) * mm, "end": v(-14.94, 4.6) * mm});
            skArc(sketch, "E2575", {"start": v(-14.82, 4.56) * mm, "mid": v(-14.9, 4.71) * mm, "end": v(-15.06, 4.63) * mm});
            skArc(sketch, "E2576", {"start": v(-16.3, 0.8) * mm, "mid": v(-16.22, 0.65) * mm, "end": v(-16.06, 0.73) * mm});
            skLineSegment(sketch, "E2577", {"start": v(-16.71, 0.75) * mm, "end": v(-15.36, 4.92) * mm});
            skArc(sketch, "E2578", {"start": v(-15.24, 4.88) * mm, "mid": v(-15.32, 5.04) * mm, "end": v(-15.48, 4.96) * mm});
            skArc(sketch, "E2579", {"start": v(-16.83, 0.79) * mm, "mid": v(-16.75, 0.63) * mm, "end": v(-16.6, 0.7) * mm});
            skLineSegment(sketch, "E2580", {"start": v(-17.2, 0.86) * mm, "end": v(-15.82, 5.13) * mm});
            skArc(sketch, "E2581", {"start": v(-15.7, 5.09) * mm, "mid": v(-15.78, 5.25) * mm, "end": v(-15.94, 5.17) * mm});
            skArc(sketch, "E2582", {"start": v(-17.32, 0.9) * mm, "mid": v(-17.24, 0.74) * mm, "end": v(-17.09, 0.82) * mm});
            skLineSegment(sketch, "E2583", {"start": v(-17.68, 1.01) * mm, "end": v(-16.3, 5.28) * mm});
            skArc(sketch, "E2584", {"start": v(-16.17, 5.25) * mm, "mid": v(-16.25, 5.4) * mm, "end": v(-16.41, 5.32) * mm});
            skArc(sketch, "E2585", {"start": v(-17.8, 1.05) * mm, "mid": v(-17.72, 0.9) * mm, "end": v(-17.56, 0.97) * mm});
            skLineSegment(sketch, "E2586", {"start": v(-18.16, 1.17) * mm, "end": v(-16.77, 5.44) * mm});
            skArc(sketch, "E2587", {"start": v(-16.65, 5.4) * mm, "mid": v(-16.73, 5.56) * mm, "end": v(-16.89, 5.48) * mm});
            skArc(sketch, "E2588", {"start": v(-18.27, 1.2) * mm, "mid": v(-18.2, 1.05) * mm, "end": v(-18.04, 1.13) * mm});
            skLineSegment(sketch, "E2589", {"start": v(-18.63, 1.32) * mm, "end": v(-17.24, 5.6) * mm});
            skArc(sketch, "E2590", {"start": v(-17.12, 5.55) * mm, "mid": v(-17.2, 5.71) * mm, "end": v(-17.36, 5.63) * mm});
            skArc(sketch, "E2591", {"start": v(-18.75, 1.36) * mm, "mid": v(-18.67, 1.2) * mm, "end": v(-18.51, 1.28) * mm});
            skLineSegment(sketch, "E2592", {"start": v(-19.1, 1.47) * mm, "end": v(-17.72, 5.75) * mm});
            skArc(sketch, "E2593", {"start": v(-17.6, 5.7) * mm, "mid": v(-17.68, 5.87) * mm, "end": v(-17.84, 5.79) * mm});
            skArc(sketch, "E2594", {"start": v(-19.23, 1.51) * mm, "mid": v(-19.15, 1.35) * mm, "end": v(-18.99, 1.43) * mm});
            skLineSegment(sketch, "E2595", {"start": v(-19.58, 1.63) * mm, "end": v(-18.2, 5.9) * mm});
            skArc(sketch, "E2596", {"start": v(-18.08, 5.86) * mm, "mid": v(-18.16, 6.02) * mm, "end": v(-18.31, 5.94) * mm});
            skArc(sketch, "E2597", {"start": v(-19.7, 1.66) * mm, "mid": v(-19.62, 1.5) * mm, "end": v(-19.47, 1.59) * mm});
            skLineSegment(sketch, "E2598", {"start": v(-20.06, 1.78) * mm, "end": v(-18.67, 6.06) * mm});
            skArc(sketch, "E2599", {"start": v(-18.55, 6.02) * mm, "mid": v(-18.63, 6.18) * mm, "end": v(-18.79, 6.1) * mm});
            skArc(sketch, "E2600", {"start": v(-20.18, 1.82) * mm, "mid": v(-20.1, 1.66) * mm, "end": v(-19.94, 1.74) * mm});
            skLineSegment(sketch, "E2601", {"start": v(-20.52, 1.98) * mm, "end": v(-19.16, 6.17) * mm});
            skArc(sketch, "E2602", {"start": v(-19.04, 6.13) * mm, "mid": v(-19.12, 6.29) * mm, "end": v(-19.28, 6.2) * mm});
            skArc(sketch, "E2603", {"start": v(-20.64, 2.01) * mm, "mid": v(-20.56, 1.86) * mm, "end": v(-20.4, 1.94) * mm});
            skLineSegment(sketch, "E2604", {"start": v(-20.95, 2.28) * mm, "end": v(-19.69, 6.17) * mm});
            skArc(sketch, "E2605", {"start": v(-19.57, 6.13) * mm, "mid": v(-19.65, 6.29) * mm, "end": v(-19.8, 6.2) * mm});
            skArc(sketch, "E2606", {"start": v(-21.07, 2.32) * mm, "mid": v(-20.99, 2.17) * mm, "end": v(-20.83, 2.25) * mm});
            skLineSegment(sketch, "E2607", {"start": v(-21.37, 2.6) * mm, "end": v(-20.21, 6.17) * mm});
            skArc(sketch, "E2608", {"start": v(-20.1, 6.13) * mm, "mid": v(-20.17, 6.29) * mm, "end": v(-20.33, 6.2) * mm});
            skArc(sketch, "E2609", {"start": v(-21.5, 2.63) * mm, "mid": v(-21.41, 2.48) * mm, "end": v(-21.25, 2.56) * mm});
            skLineSegment(sketch, "E2610", {"start": v(-21.8, 2.9) * mm, "end": v(-20.74, 6.17) * mm});
            skArc(sketch, "E2611", {"start": v(-20.62, 6.13) * mm, "mid": v(-20.7, 6.29) * mm, "end": v(-20.86, 6.2) * mm});
            skArc(sketch, "E2612", {"start": v(-21.92, 2.94) * mm, "mid": v(-21.84, 2.78) * mm, "end": v(-21.68, 2.86) * mm});
            skLineSegment(sketch, "E2613", {"start": v(-22.22, 3.21) * mm, "end": v(-21.26, 6.17) * mm});
            skArc(sketch, "E2614", {"start": v(-21.14, 6.13) * mm, "mid": v(-21.22, 6.29) * mm, "end": v(-21.38, 6.2) * mm});
            skArc(sketch, "E2615", {"start": v(-22.34, 3.25) * mm, "mid": v(-22.26, 3.1) * mm, "end": v(-22.1, 3.17) * mm});
            skLineSegment(sketch, "E2616", {"start": v(-22.6, 3.65) * mm, "end": v(-21.83, 6.04) * mm});
            skArc(sketch, "E2617", {"start": v(-21.71, 6) * mm, "mid": v(-21.8, 6.15) * mm, "end": v(-21.95, 6.07) * mm});
            skArc(sketch, "E2618", {"start": v(-22.72, 3.7) * mm, "mid": v(-22.64, 3.53) * mm, "end": v(-22.49, 3.61) * mm});
            skLineSegment(sketch, "E2619", {"start": v(-30, 4.81) * mm, "end": v(-29.88, 4.88) * mm});
            skArc(sketch, "E2620", {"start": v(-29.86, 4.83) * mm, "mid": v(-29.83, 4.9) * mm, "end": v(-29.9, 4.92) * mm});
            skArc(sketch, "E2621", {"start": v(-30.03, 4.86) * mm, "mid": v(-30.05, 4.79) * mm, "end": v(-29.98, 4.77) * mm});
            skLineSegment(sketch, "E2622", {"start": v(-29.88, 4.88) * mm, "end": v(-29.75, 4.97) * mm});
            skArc(sketch, "E2623", {"start": v(-29.72, 4.93) * mm, "mid": v(-29.71, 5) * mm, "end": v(-29.78, 5.01) * mm});
            skArc(sketch, "E2624", {"start": v(-29.9, 4.92) * mm, "mid": v(-29.92, 4.85) * mm, "end": v(-29.85, 4.84) * mm});
            skLineSegment(sketch, "E2625", {"start": v(-29.75, 4.97) * mm, "end": v(-29.65, 5.08) * mm});
            skArc(sketch, "E2626", {"start": v(-29.61, 5.05) * mm, "mid": v(-29.61, 5.12) * mm, "end": v(-29.68, 5.12) * mm});
            skArc(sketch, "E2627", {"start": v(-29.8, 5) * mm, "mid": v(-29.79, 4.93) * mm, "end": v(-29.72, 4.94) * mm});
            skLineSegment(sketch, "E2628", {"start": v(-29.65, 5.08) * mm, "end": v(-29.56, 5.22) * mm});
            skArc(sketch, "E2629", {"start": v(-29.52, 5.2) * mm, "mid": v(-29.53, 5.26) * mm, "end": v(-29.6, 5.24) * mm});
            skArc(sketch, "E2630", {"start": v(-29.69, 5.11) * mm, "mid": v(-29.68, 5.04) * mm, "end": v(-29.6, 5.06) * mm});
            skLineSegment(sketch, "E2631", {"start": v(-29.56, 5.22) * mm, "end": v(-29.53, 5.29) * mm});
            skArc(sketch, "E2632", {"start": v(-29.48, 5.27) * mm, "mid": v(-29.5, 5.34) * mm, "end": v(-29.57, 5.31) * mm});
            skArc(sketch, "E2633", {"start": v(-29.6, 5.24) * mm, "mid": v(-29.58, 5.17) * mm, "end": v(-29.52, 5.2) * mm});
            skLineSegment(sketch, "E2634", {"start": v(-29.53, 5.29) * mm, "end": v(-28.38, 8.86) * mm});
            skArc(sketch, "E2635", {"start": v(-28.33, 8.85) * mm, "mid": v(-28.36, 8.91) * mm, "end": v(-28.43, 8.88) * mm});
            skArc(sketch, "E2636", {"start": v(-29.57, 5.3) * mm, "mid": v(-29.54, 5.24) * mm, "end": v(-29.48, 5.27) * mm});
            skLineSegment(sketch, "E2637", {"start": v(-28.38, 8.86) * mm, "end": v(-28.37, 9.02) * mm});
            skArc(sketch, "E2638", {"start": v(-28.32, 9.02) * mm, "mid": v(-28.37, 9.07) * mm, "end": v(-28.42, 9.02) * mm});
            skArc(sketch, "E2639", {"start": v(-28.43, 8.87) * mm, "mid": v(-28.38, 8.81) * mm, "end": v(-28.33, 8.86) * mm});
            skLineSegment(sketch, "E2640", {"start": v(-28.37, 9.02) * mm, "end": v(-28.4, 9.18) * mm});
            skArc(sketch, "E2641", {"start": v(-28.34, 9.18) * mm, "mid": v(-28.4, 9.23) * mm, "end": v(-28.44, 9.17) * mm});
            skArc(sketch, "E2642", {"start": v(-28.42, 9.01) * mm, "mid": v(-28.37, 8.97) * mm, "end": v(-28.32, 9.03) * mm});
            skLineSegment(sketch, "E2643", {"start": v(-28.4, 9.18) * mm, "end": v(-28.44, 9.32) * mm});
            skArc(sketch, "E2644", {"start": v(-28.4, 9.34) * mm, "mid": v(-28.45, 9.37) * mm, "end": v(-28.49, 9.3) * mm});
            skArc(sketch, "E2645", {"start": v(-28.44, 9.16) * mm, "mid": v(-28.38, 9.13) * mm, "end": v(-28.35, 9.2) * mm});
            skLineSegment(sketch, "E2646", {"start": v(-28.44, 9.32) * mm, "end": v(-28.5, 9.44) * mm});
            skArc(sketch, "E2647", {"start": v(-28.45, 9.46) * mm, "mid": v(-28.52, 9.49) * mm, "end": v(-28.54, 9.42) * mm});
            skArc(sketch, "E2648", {"start": v(-28.48, 9.3) * mm, "mid": v(-28.42, 9.28) * mm, "end": v(-28.4, 9.35) * mm});
            skLineSegment(sketch, "E2649", {"start": v(-28.5, 9.44) * mm, "end": v(-28.62, 9.38) * mm});
            skArc(sketch, "E2650", {"start": v(-28.65, 9.42) * mm, "mid": v(-28.67, 9.35) * mm, "end": v(-28.6, 9.33) * mm});
            skArc(sketch, "E2651", {"start": v(-28.48, 9.4) * mm, "mid": v(-28.45, 9.46) * mm, "end": v(-28.52, 9.49) * mm});
            skLineSegment(sketch, "E2652", {"start": v(-28.62, 9.38) * mm, "end": v(-28.75, 9.28) * mm});
            skArc(sketch, "E2653", {"start": v(-28.78, 9.32) * mm, "mid": v(-28.79, 9.25) * mm, "end": v(-28.72, 9.24) * mm});
            skArc(sketch, "E2654", {"start": v(-28.6, 9.34) * mm, "mid": v(-28.58, 9.4) * mm, "end": v(-28.65, 9.42) * mm});
            skLineSegment(sketch, "E2655", {"start": v(-28.75, 9.28) * mm, "end": v(-28.86, 9.17) * mm});
            skArc(sketch, "E2656", {"start": v(-28.9, 9.2) * mm, "mid": v(-28.89, 9.13) * mm, "end": v(-28.82, 9.13) * mm});
            skArc(sketch, "E2657", {"start": v(-28.71, 9.25) * mm, "mid": v(-28.71, 9.32) * mm, "end": v(-28.79, 9.32) * mm});
            skLineSegment(sketch, "E2658", {"start": v(-28.86, 9.17) * mm, "end": v(-28.94, 9.04) * mm});
            skArc(sketch, "E2659", {"start": v(-28.98, 9.06) * mm, "mid": v(-28.97, 9) * mm, "end": v(-28.9, 9) * mm});
            skArc(sketch, "E2660", {"start": v(-28.81, 9.14) * mm, "mid": v(-28.83, 9.21) * mm, "end": v(-28.9, 9.2) * mm});
            skLineSegment(sketch, "E2661", {"start": v(-28.94, 9.04) * mm, "end": v(-28.98, 8.96) * mm});
            skArc(sketch, "E2662", {"start": v(-29.02, 8.99) * mm, "mid": v(-29, 8.92) * mm, "end": v(-28.93, 8.94) * mm});
            skArc(sketch, "E2663", {"start": v(-28.9, 9.01) * mm, "mid": v(-28.92, 9.08) * mm, "end": v(-28.99, 9.06) * mm});
            skLineSegment(sketch, "E2664", {"start": v(-28.98, 8.96) * mm, "end": v(-30.12, 5.39) * mm});
            skArc(sketch, "E2665", {"start": v(-30.17, 5.4) * mm, "mid": v(-30.14, 5.34) * mm, "end": v(-30.08, 5.37) * mm});
            skArc(sketch, "E2666", {"start": v(-28.93, 8.95) * mm, "mid": v(-28.96, 9.01) * mm, "end": v(-29.02, 8.98) * mm});
            skLineSegment(sketch, "E2667", {"start": v(-30.12, 5.39) * mm, "end": v(-30.13, 5.23) * mm});
            skArc(sketch, "E2668", {"start": v(-30.18, 5.23) * mm, "mid": v(-30.13, 5.18) * mm, "end": v(-30.08, 5.23) * mm});
            skArc(sketch, "E2669", {"start": v(-30.07, 5.39) * mm, "mid": v(-30.12, 5.44) * mm, "end": v(-30.17, 5.4) * mm});
            skLineSegment(sketch, "E2670", {"start": v(-30.13, 5.23) * mm, "end": v(-30.11, 5.08) * mm});
            skArc(sketch, "E2671", {"start": v(-30.16, 5.07) * mm, "mid": v(-30.1, 5.03) * mm, "end": v(-30.06, 5.08) * mm});
            skArc(sketch, "E2672", {"start": v(-30.08, 5.24) * mm, "mid": v(-30.14, 5.28) * mm, "end": v(-30.18, 5.23) * mm});
            skLineSegment(sketch, "E2673", {"start": v(-30.11, 5.08) * mm, "end": v(-30.06, 4.93) * mm});
            skArc(sketch, "E2674", {"start": v(-30.11, 4.92) * mm, "mid": v(-30.05, 4.88) * mm, "end": v(-30.02, 4.95) * mm});
            skArc(sketch, "E2675", {"start": v(-30.06, 5.1) * mm, "mid": v(-30.13, 5.13) * mm, "end": v(-30.16, 5.06) * mm});
            skLineSegment(sketch, "E2676", {"start": v(-30.06, 4.93) * mm, "end": v(-30, 4.81) * mm});
            skArc(sketch, "E2677", {"start": v(-30.05, 4.8) * mm, "mid": v(-29.98, 4.77) * mm, "end": v(-29.96, 4.84) * mm});
            skArc(sketch, "E2678", {"start": v(-30.02, 4.95) * mm, "mid": v(-30.09, 4.97) * mm, "end": v(-30.1, 4.9) * mm});
            skLineSegment(sketch, "E2679", {"start": v(-29.74, 4.98) * mm, "end": v(-28.39, 9.15) * mm});
            skArc(sketch, "E2680", {"start": v(-28.34, 9.14) * mm, "mid": v(-28.37, 9.2) * mm, "end": v(-28.44, 9.17) * mm});
            skArc(sketch, "E2681", {"start": v(-29.8, 5) * mm, "mid": v(-29.76, 4.93) * mm, "end": v(-29.7, 4.97) * mm});
            skLineSegment(sketch, "E2682", {"start": v(-30, 4.82) * mm, "end": v(-28.5, 9.44) * mm});
            skArc(sketch, "E2683", {"start": v(-28.46, 9.42) * mm, "mid": v(-28.5, 9.48) * mm, "end": v(-28.55, 9.45) * mm});
            skArc(sketch, "E2684", {"start": v(-30.05, 4.83) * mm, "mid": v(-30.02, 4.77) * mm, "end": v(-29.96, 4.8) * mm});
            skLineSegment(sketch, "E2685", {"start": v(-30.12, 5.13) * mm, "end": v(-28.78, 9.25) * mm});
            skArc(sketch, "E2686", {"start": v(-28.73, 9.24) * mm, "mid": v(-28.76, 9.3) * mm, "end": v(-28.82, 9.27) * mm});
            skArc(sketch, "E2687", {"start": v(-30.16, 5.14) * mm, "mid": v(-30.13, 5.08) * mm, "end": v(-30.07, 5.11) * mm});
            skCircle(sketch, "E2688", {"center": v(-16.51, 2.99) * mm, "radius": 1.7 * mm});
            skArc(sketch, "E2689", {"start": v(-16.51, 2.11) * mm, "mid": v(-15.64, 2.99) * mm, "end": v(-16.51, 3.86) * mm});
            skArc(sketch, "E2690", {"start": v(-16.51, 3.86) * mm, "mid": v(-17.39, 2.99) * mm, "end": v(-16.51, 2.11) * mm});
            skCircle(sketch, "E2691", {"center": v(-26.02, 6.08) * mm, "radius": 1.7 * mm});
            skArc(sketch, "E2692", {"start": v(-26.02, 5.2) * mm, "mid": v(-25.15, 6.08) * mm, "end": v(-26.02, 6.95) * mm});
            skArc(sketch, "E2693", {"start": v(-26.02, 6.95) * mm, "mid": v(-26.9, 6.08) * mm, "end": v(-26.02, 5.2) * mm});
            skLineSegment(sketch, "E2694", {"start": v(-10.35, -20.46) * mm, "end": v(-8.24, -17.54) * mm});
            skArc(sketch, "E2695", {"start": v(-8.14, -17.62) * mm, "mid": v(-8.17, -17.44) * mm, "end": v(-8.34, -17.47) * mm});
            skArc(sketch, "E2696", {"start": v(-10.45, -20.39) * mm, "mid": v(-10.42, -20.56) * mm, "end": v(-10.25, -20.54) * mm});
            skLineSegment(sketch, "E2697", {"start": v(-8.24, -17.54) * mm, "end": v(-8.14, -17.34) * mm});
            skArc(sketch, "E2698", {"start": v(-8.03, -17.4) * mm, "mid": v(-8.08, -17.23) * mm, "end": v(-8.25, -17.28) * mm});
            skArc(sketch, "E2699", {"start": v(-8.35, -17.49) * mm, "mid": v(-8.3, -17.65) * mm, "end": v(-8.13, -17.6) * mm});
            skLineSegment(sketch, "E2700", {"start": v(-8.14, -17.34) * mm, "end": v(-8.06, -17.13) * mm});
            skArc(sketch, "E2701", {"start": v(-7.94, -17.18) * mm, "mid": v(-8.01, -17.02) * mm, "end": v(-8.18, -17.09) * mm});
            skArc(sketch, "E2702", {"start": v(-8.26, -17.3) * mm, "mid": v(-8.19, -17.46) * mm, "end": v(-8.02, -17.39) * mm});
            skLineSegment(sketch, "E2703", {"start": v(-8.06, -17.13) * mm, "end": v(-8, -16.92) * mm});
            skArc(sketch, "E2704", {"start": v(-7.88, -16.96) * mm, "mid": v(-7.97, -16.8) * mm, "end": v(-8.12, -16.89) * mm});
            skArc(sketch, "E2705", {"start": v(-8.18, -17.1) * mm, "mid": v(-8.1, -17.25) * mm, "end": v(-7.94, -17.17) * mm});
            skLineSegment(sketch, "E2706", {"start": v(-8, -16.92) * mm, "end": v(-7.96, -16.7) * mm});
            skArc(sketch, "E2707", {"start": v(-7.84, -16.73) * mm, "mid": v(-7.94, -16.58) * mm, "end": v(-8.09, -16.69) * mm});
            skArc(sketch, "E2708", {"start": v(-8.12, -16.9) * mm, "mid": v(-8.02, -17.05) * mm, "end": v(-7.88, -16.94) * mm});
            skLineSegment(sketch, "E2709", {"start": v(-7.96, -16.7) * mm, "end": v(-7.95, -16.5) * mm});
            skArc(sketch, "E2710", {"start": v(-7.82, -16.5) * mm, "mid": v(-7.94, -16.37) * mm, "end": v(-8.07, -16.48) * mm});
            skArc(sketch, "E2711", {"start": v(-8.09, -16.7) * mm, "mid": v(-7.97, -16.83) * mm, "end": v(-7.84, -16.72) * mm});
            skLineSegment(sketch, "E2712", {"start": v(-7.95, -16.5) * mm, "end": v(-7.95, -16.27) * mm});
            skArc(sketch, "E2713", {"start": v(-7.82, -16.27) * mm, "mid": v(-7.95, -16.15) * mm, "end": v(-8.07, -16.28) * mm});
            skArc(sketch, "E2714", {"start": v(-8.07, -16.5) * mm, "mid": v(-7.94, -16.62) * mm, "end": v(-7.82, -16.49) * mm});
            skLineSegment(sketch, "E2715", {"start": v(-7.95, -16.27) * mm, "end": v(-7.97, -16.06) * mm});
            skArc(sketch, "E2716", {"start": v(-7.85, -16.05) * mm, "mid": v(-7.99, -15.94) * mm, "end": v(-8.1, -16.07) * mm});
            skArc(sketch, "E2717", {"start": v(-8.07, -16.29) * mm, "mid": v(-7.94, -16.4) * mm, "end": v(-7.83, -16.26) * mm});
            skLineSegment(sketch, "E2718", {"start": v(-7.97, -16.06) * mm, "end": v(-8.02, -15.85) * mm});
            skArc(sketch, "E2719", {"start": v(-7.9, -15.82) * mm, "mid": v(-8.05, -15.73) * mm, "end": v(-8.14, -15.87) * mm});
            skArc(sketch, "E2720", {"start": v(-8.1, -16.09) * mm, "mid": v(-7.95, -16.18) * mm, "end": v(-7.85, -16.03) * mm});
            skLineSegment(sketch, "E2721", {"start": v(-8.02, -15.85) * mm, "end": v(-8.08, -15.64) * mm});
            skArc(sketch, "E2722", {"start": v(-7.97, -15.6) * mm, "mid": v(-8.12, -15.52) * mm, "end": v(-8.2, -15.68) * mm});
            skArc(sketch, "E2723", {"start": v(-8.14, -15.89) * mm, "mid": v(-7.98, -15.97) * mm, "end": v(-7.9, -15.81) * mm});
            skLineSegment(sketch, "E2724", {"start": v(-8.08, -15.64) * mm, "end": v(-8.17, -15.44) * mm});
            skArc(sketch, "E2725", {"start": v(-8.05, -15.4) * mm, "mid": v(-8.22, -15.33) * mm, "end": v(-8.28, -15.5) * mm});
            skArc(sketch, "E2726", {"start": v(-8.2, -15.7) * mm, "mid": v(-8.04, -15.76) * mm, "end": v(-7.97, -15.6) * mm});
            skLineSegment(sketch, "E2727", {"start": v(-8.17, -15.44) * mm, "end": v(-8.27, -15.25) * mm});
            skArc(sketch, "E2728", {"start": v(-8.16, -15.2) * mm, "mid": v(-8.33, -15.14) * mm, "end": v(-8.38, -15.31) * mm});
            skArc(sketch, "E2729", {"start": v(-8.28, -15.5) * mm, "mid": v(-8.1, -15.55) * mm, "end": v(-8.06, -15.38) * mm});
            skLineSegment(sketch, "E2730", {"start": v(-8.27, -15.25) * mm, "end": v(-8.4, -15.07) * mm});
            skArc(sketch, "E2731", {"start": v(-8.3, -15) * mm, "mid": v(-8.47, -14.96) * mm, "end": v(-8.5, -15.14) * mm});
            skArc(sketch, "E2732", {"start": v(-8.38, -15.32) * mm, "mid": v(-8.2, -15.35) * mm, "end": v(-8.17, -15.18) * mm});
            skLineSegment(sketch, "E2733", {"start": v(-8.4, -15.07) * mm, "end": v(-8.54, -14.9) * mm});
            skArc(sketch, "E2734", {"start": v(-8.44, -14.82) * mm, "mid": v(-8.62, -14.8) * mm, "end": v(-8.64, -14.98) * mm});
            skArc(sketch, "E2735", {"start": v(-8.5, -15.15) * mm, "mid": v(-8.32, -15.16) * mm, "end": v(-8.3, -14.99) * mm});
            skLineSegment(sketch, "E2736", {"start": v(-8.54, -14.9) * mm, "end": v(-8.7, -14.74) * mm});
            skArc(sketch, "E2737", {"start": v(-8.62, -14.65) * mm, "mid": v(-8.8, -14.65) * mm, "end": v(-8.79, -14.83) * mm});
            skArc(sketch, "E2738", {"start": v(-8.63, -14.99) * mm, "mid": v(-8.45, -14.99) * mm, "end": v(-8.45, -14.8) * mm});
            skLineSegment(sketch, "E2739", {"start": v(-8.7, -14.74) * mm, "end": v(-8.87, -14.6) * mm});
            skArc(sketch, "E2740", {"start": v(-8.8, -14.5) * mm, "mid": v(-8.97, -14.53) * mm, "end": v(-8.95, -14.7) * mm});
            skArc(sketch, "E2741", {"start": v(-8.78, -14.84) * mm, "mid": v(-8.6, -14.82) * mm, "end": v(-8.62, -14.64) * mm});
            skLineSegment(sketch, "E2742", {"start": v(-8.87, -14.6) * mm, "end": v(-9.08, -14.47) * mm});
            skArc(sketch, "E2743", {"start": v(-9, -14.37) * mm, "mid": v(-9.18, -14.4) * mm, "end": v(-9.15, -14.58) * mm});
            skArc(sketch, "E2744", {"start": v(-8.94, -14.7) * mm, "mid": v(-8.77, -14.67) * mm, "end": v(-8.8, -14.5) * mm});
            skLineSegment(sketch, "E2745", {"start": v(-9.08, -14.47) * mm, "end": v(-9.28, -14.37) * mm});
            skArc(sketch, "E2746", {"start": v(-9.22, -14.26) * mm, "mid": v(-9.39, -14.31) * mm, "end": v(-9.33, -14.48) * mm});
            skArc(sketch, "E2747", {"start": v(-9.13, -14.58) * mm, "mid": v(-8.97, -14.53) * mm, "end": v(-9.02, -14.36) * mm});
            skLineSegment(sketch, "E2748", {"start": v(-9.28, -14.37) * mm, "end": v(-9.49, -14.29) * mm});
            skArc(sketch, "E2749", {"start": v(-9.44, -14.17) * mm, "mid": v(-9.6, -14.24) * mm, "end": v(-9.53, -14.4) * mm});
            skArc(sketch, "E2750", {"start": v(-9.32, -14.48) * mm, "mid": v(-9.16, -14.41) * mm, "end": v(-9.23, -14.25) * mm});
            skLineSegment(sketch, "E2751", {"start": v(-9.49, -14.29) * mm, "end": v(-9.7, -14.23) * mm});
            skArc(sketch, "E2752", {"start": v(-9.66, -14.1) * mm, "mid": v(-9.82, -14.2) * mm, "end": v(-9.73, -14.35) * mm});
            skArc(sketch, "E2753", {"start": v(-9.52, -14.4) * mm, "mid": v(-9.36, -14.32) * mm, "end": v(-9.45, -14.17) * mm});
            skLineSegment(sketch, "E2754", {"start": v(-9.7, -14.23) * mm, "end": v(-9.91, -14.2) * mm});
            skArc(sketch, "E2755", {"start": v(-9.9, -14.07) * mm, "mid": v(-10.03, -14.17) * mm, "end": v(-9.93, -14.31) * mm});
            skArc(sketch, "E2756", {"start": v(-9.72, -14.35) * mm, "mid": v(-9.57, -14.25) * mm, "end": v(-9.67, -14.1) * mm});
            skLineSegment(sketch, "E2757", {"start": v(-9.91, -14.2) * mm, "end": v(-10.13, -14.17) * mm});
            skArc(sketch, "E2758", {"start": v(-10.12, -14.05) * mm, "mid": v(-10.25, -14.16) * mm, "end": v(-10.14, -14.3) * mm});
            skArc(sketch, "E2759", {"start": v(-9.92, -14.32) * mm, "mid": v(-9.79, -14.2) * mm, "end": v(-9.9, -14.07) * mm});
            skLineSegment(sketch, "E2760", {"start": v(-10.13, -14.17) * mm, "end": v(-10.34, -14.18) * mm});
            skArc(sketch, "E2761", {"start": v(-10.35, -14.05) * mm, "mid": v(-10.47, -14.18) * mm, "end": v(-10.34, -14.3) * mm});
            skArc(sketch, "E2762", {"start": v(-10.13, -14.3) * mm, "mid": v(-10, -14.17) * mm, "end": v(-10.13, -14.05) * mm});
            skLineSegment(sketch, "E2763", {"start": v(-10.34, -14.18) * mm, "end": v(-10.56, -14.2) * mm});
            skArc(sketch, "E2764", {"start": v(-10.57, -14.08) * mm, "mid": v(-10.68, -14.22) * mm, "end": v(-10.54, -14.33) * mm});
            skArc(sketch, "E2765", {"start": v(-10.33, -14.3) * mm, "mid": v(-10.22, -14.16) * mm, "end": v(-10.36, -14.05) * mm});
            skLineSegment(sketch, "E2766", {"start": v(-10.56, -14.2) * mm, "end": v(-10.77, -14.25) * mm});
            skArc(sketch, "E2767", {"start": v(-10.8, -14.13) * mm, "mid": v(-10.9, -14.27) * mm, "end": v(-10.74, -14.37) * mm});
            skArc(sketch, "E2768", {"start": v(-10.53, -14.33) * mm, "mid": v(-10.44, -14.18) * mm, "end": v(-10.59, -14.08) * mm});
            skLineSegment(sketch, "E2769", {"start": v(-10.77, -14.25) * mm, "end": v(-10.98, -14.31) * mm});
            skArc(sketch, "E2770", {"start": v(-11.01, -14.2) * mm, "mid": v(-11.1, -14.35) * mm, "end": v(-10.94, -14.43) * mm});
            skArc(sketch, "E2771", {"start": v(-10.73, -14.37) * mm, "mid": v(-10.65, -14.21) * mm, "end": v(-10.8, -14.13) * mm});
            skLineSegment(sketch, "E2772", {"start": v(-10.98, -14.31) * mm, "end": v(-11.18, -14.4) * mm});
            skArc(sketch, "E2773", {"start": v(-11.23, -14.28) * mm, "mid": v(-11.3, -14.45) * mm, "end": v(-11.13, -14.51) * mm});
            skArc(sketch, "E2774", {"start": v(-10.93, -14.43) * mm, "mid": v(-10.86, -14.26) * mm, "end": v(-11.03, -14.2) * mm});
            skLineSegment(sketch, "E2775", {"start": v(-11.18, -14.4) * mm, "end": v(-11.37, -14.5) * mm});
            skArc(sketch, "E2776", {"start": v(-11.43, -14.4) * mm, "mid": v(-11.48, -14.56) * mm, "end": v(-11.3, -14.61) * mm});
            skArc(sketch, "E2777", {"start": v(-11.12, -14.5) * mm, "mid": v(-11.07, -14.34) * mm, "end": v(-11.24, -14.29) * mm});
            skLineSegment(sketch, "E2778", {"start": v(-11.37, -14.5) * mm, "end": v(-11.55, -14.63) * mm});
            skArc(sketch, "E2779", {"start": v(-11.62, -14.52) * mm, "mid": v(-11.65, -14.7) * mm, "end": v(-11.48, -14.73) * mm});
            skArc(sketch, "E2780", {"start": v(-11.3, -14.6) * mm, "mid": v(-11.26, -14.43) * mm, "end": v(-11.44, -14.4) * mm});
            skLineSegment(sketch, "E2781", {"start": v(-11.55, -14.63) * mm, "end": v(-11.72, -14.77) * mm});
            skArc(sketch, "E2782", {"start": v(-11.8, -14.67) * mm, "mid": v(-11.82, -14.85) * mm, "end": v(-11.64, -14.87) * mm});
            skArc(sketch, "E2783", {"start": v(-11.47, -14.72) * mm, "mid": v(-11.45, -14.55) * mm, "end": v(-11.63, -14.53) * mm});
            skLineSegment(sketch, "E2784", {"start": v(-11.72, -14.77) * mm, "end": v(-11.88, -14.93) * mm});
            skArc(sketch, "E2785", {"start": v(-11.97, -14.84) * mm, "mid": v(-11.97, -15.02) * mm, "end": v(-11.8, -15.02) * mm});
            skArc(sketch, "E2786", {"start": v(-11.63, -14.86) * mm, "mid": v(-11.63, -14.68) * mm, "end": v(-11.81, -14.68) * mm});
            skLineSegment(sketch, "E2787", {"start": v(-11.88, -14.93) * mm, "end": v(-12.03, -15.12) * mm});
            skArc(sketch, "E2788", {"start": v(-12.13, -15.05) * mm, "mid": v(-12.11, -15.22) * mm, "end": v(-11.94, -15.2) * mm});
            skArc(sketch, "E2789", {"start": v(-11.78, -15) * mm, "mid": v(-11.8, -14.83) * mm, "end": v(-11.98, -14.85) * mm});
            skLineSegment(sketch, "E2790", {"start": v(-12.03, -15.12) * mm, "end": v(-14, -17.82) * mm});
            skArc(sketch, "E2791", {"start": v(-14.1, -17.74) * mm, "mid": v(-14.06, -17.92) * mm, "end": v(-13.89, -17.9) * mm});
            skArc(sketch, "E2792", {"start": v(-11.93, -15.2) * mm, "mid": v(-11.96, -15.02) * mm, "end": v(-12.14, -15.05) * mm});
            skLineSegment(sketch, "E2793", {"start": v(-14, -17.82) * mm, "end": v(-14.7, -20.04) * mm});
            skArc(sketch, "E2794", {"start": v(-14.83, -20) * mm, "mid": v(-14.75, -20.15) * mm, "end": v(-14.6, -20.07) * mm});
            skArc(sketch, "E2795", {"start": v(-13.87, -17.86) * mm, "mid": v(-13.95, -17.7) * mm, "end": v(-14.1, -17.78) * mm});
            skLineSegment(sketch, "E2796", {"start": v(-14.7, -20.04) * mm, "end": v(-14.77, -21.1) * mm});
            skArc(sketch, "E2797", {"start": v(-14.89, -21.08) * mm, "mid": v(-14.77, -21.21) * mm, "end": v(-14.64, -21.1) * mm});
            skArc(sketch, "E2798", {"start": v(-14.59, -20.04) * mm, "mid": v(-14.7, -19.91) * mm, "end": v(-14.83, -20.03) * mm});
            skLineSegment(sketch, "E2799", {"start": v(-14.77, -21.1) * mm, "end": v(-13.22, -22.21) * mm});
            skArc(sketch, "E2800", {"start": v(-13.3, -22.31) * mm, "mid": v(-13.12, -22.28) * mm, "end": v(-13.15, -22.1) * mm});
            skArc(sketch, "E2801", {"start": v(-14.7, -20.99) * mm, "mid": v(-14.87, -21.02) * mm, "end": v(-14.84, -21.2) * mm});
            skLineSegment(sketch, "E2802", {"start": v(-13.22, -22.21) * mm, "end": v(-12.24, -21.83) * mm});
            skArc(sketch, "E2803", {"start": v(-12.2, -21.95) * mm, "mid": v(-12.12, -21.79) * mm, "end": v(-12.28, -21.72) * mm});
            skArc(sketch, "E2804", {"start": v(-13.27, -22.1) * mm, "mid": v(-13.34, -22.26) * mm, "end": v(-13.18, -22.33) * mm});
            skLineSegment(sketch, "E2805", {"start": v(-12.24, -21.83) * mm, "end": v(-10.35, -20.46) * mm});
            skArc(sketch, "E2806", {"start": v(-10.28, -20.56) * mm, "mid": v(-10.25, -20.39) * mm, "end": v(-10.42, -20.36) * mm});
            skArc(sketch, "E2807", {"start": v(-12.31, -21.73) * mm, "mid": v(-12.34, -21.9) * mm, "end": v(-12.16, -21.93) * mm});
            skLineSegment(sketch, "E2808", {"start": v(-8.19, -15.41) * mm, "end": v(-9.85, -14.2) * mm});
            skArc(sketch, "E2809", {"start": v(-9.78, -14.1) * mm, "mid": v(-9.95, -14.13) * mm, "end": v(-9.93, -14.3) * mm});
            skArc(sketch, "E2810", {"start": v(-8.26, -15.51) * mm, "mid": v(-8.09, -15.49) * mm, "end": v(-8.11, -15.31) * mm});
            skLineSegment(sketch, "E2811", {"start": v(-7.96, -16.2) * mm, "end": v(-10.67, -14.23) * mm});
            skArc(sketch, "E2812", {"start": v(-10.6, -14.13) * mm, "mid": v(-10.77, -14.15) * mm, "end": v(-10.74, -14.33) * mm});
            skArc(sketch, "E2813", {"start": v(-8.03, -16.3) * mm, "mid": v(-7.86, -16.27) * mm, "end": v(-7.89, -16.1) * mm});
            skLineSegment(sketch, "E2814", {"start": v(-7.98, -16.8) * mm, "end": v(-11.24, -14.43) * mm});
            skArc(sketch, "E2815", {"start": v(-11.16, -14.33) * mm, "mid": v(-11.34, -14.36) * mm, "end": v(-11.31, -14.53) * mm});
            skArc(sketch, "E2816", {"start": v(-8.05, -16.9) * mm, "mid": v(-7.88, -16.87) * mm, "end": v(-7.9, -16.7) * mm});
            skLineSegment(sketch, "E2817", {"start": v(-8.13, -17.3) * mm, "end": v(-11.68, -14.73) * mm});
            skArc(sketch, "E2818", {"start": v(-11.6, -14.63) * mm, "mid": v(-11.78, -14.66) * mm, "end": v(-11.75, -14.83) * mm});
            skArc(sketch, "E2819", {"start": v(-8.2, -17.4) * mm, "mid": v(-8.03, -17.38) * mm, "end": v(-8.05, -17.2) * mm});
            skLineSegment(sketch, "E2820", {"start": v(-8.38, -17.74) * mm, "end": v(-12.02, -15.1) * mm});
            skArc(sketch, "E2821", {"start": v(-11.94, -15) * mm, "mid": v(-12.12, -15.03) * mm, "end": v(-12.09, -15.2) * mm});
            skArc(sketch, "E2822", {"start": v(-8.46, -17.84) * mm, "mid": v(-8.28, -17.81) * mm, "end": v(-8.31, -17.64) * mm});
            skLineSegment(sketch, "E2823", {"start": v(-8.68, -18.15) * mm, "end": v(-12.31, -15.5) * mm});
            skArc(sketch, "E2824", {"start": v(-12.24, -15.4) * mm, "mid": v(-12.41, -15.43) * mm, "end": v(-12.38, -15.6) * mm});
            skArc(sketch, "E2825", {"start": v(-8.75, -18.25) * mm, "mid": v(-8.58, -18.22) * mm, "end": v(-8.6, -18.04) * mm});
            skLineSegment(sketch, "E2826", {"start": v(-8.97, -18.55) * mm, "end": v(-12.6, -15.9) * mm});
            skArc(sketch, "E2827", {"start": v(-12.53, -15.8) * mm, "mid": v(-12.7, -15.84) * mm, "end": v(-12.68, -16.01) * mm});
            skArc(sketch, "E2828", {"start": v(-9.04, -18.65) * mm, "mid": v(-8.87, -18.62) * mm, "end": v(-8.9, -18.45) * mm});
            skLineSegment(sketch, "E2829", {"start": v(-9.26, -18.96) * mm, "end": v(-12.9, -16.31) * mm});
            skArc(sketch, "E2830", {"start": v(-12.82, -16.21) * mm, "mid": v(-13, -16.24) * mm, "end": v(-12.97, -16.42) * mm});
            skArc(sketch, "E2831", {"start": v(-9.34, -19.06) * mm, "mid": v(-9.16, -19.03) * mm, "end": v(-9.19, -18.85) * mm});
            skLineSegment(sketch, "E2832", {"start": v(-9.56, -19.36) * mm, "end": v(-13.2, -16.72) * mm});
            skArc(sketch, "E2833", {"start": v(-13.12, -16.62) * mm, "mid": v(-13.3, -16.65) * mm, "end": v(-13.27, -16.82) * mm});
            skArc(sketch, "E2834", {"start": v(-9.63, -19.46) * mm, "mid": v(-9.45, -19.43) * mm, "end": v(-9.48, -19.26) * mm});
            skLineSegment(sketch, "E2835", {"start": v(-9.85, -19.77) * mm, "end": v(-13.49, -17.12) * mm});
            skArc(sketch, "E2836", {"start": v(-13.41, -17.02) * mm, "mid": v(-13.59, -17.05) * mm, "end": v(-13.56, -17.22) * mm});
            skArc(sketch, "E2837", {"start": v(-9.92, -19.87) * mm, "mid": v(-9.75, -19.84) * mm, "end": v(-9.77, -19.67) * mm});
            skLineSegment(sketch, "E2838", {"start": v(-10.14, -20.17) * mm, "end": v(-13.78, -17.53) * mm});
            skArc(sketch, "E2839", {"start": v(-13.7, -17.43) * mm, "mid": v(-13.88, -17.45) * mm, "end": v(-13.85, -17.63) * mm});
            skArc(sketch, "E2840", {"start": v(-10.21, -20.27) * mm, "mid": v(-10.04, -20.25) * mm, "end": v(-10.07, -20.07) * mm});
            skLineSegment(sketch, "E2841", {"start": v(-10.47, -20.55) * mm, "end": v(-14.04, -17.96) * mm});
            skArc(sketch, "E2842", {"start": v(-13.96, -17.86) * mm, "mid": v(-14.14, -17.89) * mm, "end": v(-14.11, -18.06) * mm});
            skArc(sketch, "E2843", {"start": v(-10.54, -20.65) * mm, "mid": v(-10.37, -20.62) * mm, "end": v(-10.4, -20.45) * mm});
            skLineSegment(sketch, "E2844", {"start": v(-10.9, -20.86) * mm, "end": v(-14.2, -18.46) * mm});
            skArc(sketch, "E2845", {"start": v(-14.13, -18.36) * mm, "mid": v(-14.3, -18.39) * mm, "end": v(-14.27, -18.56) * mm});
            skArc(sketch, "E2846", {"start": v(-10.97, -20.96) * mm, "mid": v(-10.8, -20.93) * mm, "end": v(-10.82, -20.76) * mm});
            skLineSegment(sketch, "E2847", {"start": v(-11.32, -21.17) * mm, "end": v(-14.36, -18.96) * mm});
            skArc(sketch, "E2848", {"start": v(-14.29, -18.86) * mm, "mid": v(-14.46, -18.89) * mm, "end": v(-14.43, -19.06) * mm});
            skArc(sketch, "E2849", {"start": v(-11.4, -21.27) * mm, "mid": v(-11.22, -21.24) * mm, "end": v(-11.25, -21.07) * mm});
            skLineSegment(sketch, "E2850", {"start": v(-11.75, -21.48) * mm, "end": v(-14.52, -19.46) * mm});
            skArc(sketch, "E2851", {"start": v(-14.45, -19.36) * mm, "mid": v(-14.62, -19.39) * mm, "end": v(-14.6, -19.56) * mm});
            skArc(sketch, "E2852", {"start": v(-11.82, -21.58) * mm, "mid": v(-11.65, -21.55) * mm, "end": v(-11.67, -21.38) * mm});
            skLineSegment(sketch, "E2853", {"start": v(-12.17, -21.79) * mm, "end": v(-14.69, -19.96) * mm});
            skArc(sketch, "E2854", {"start": v(-14.61, -19.86) * mm, "mid": v(-14.79, -19.89) * mm, "end": v(-14.76, -20.06) * mm});
            skArc(sketch, "E2855", {"start": v(-12.25, -21.89) * mm, "mid": v(-12.07, -21.86) * mm, "end": v(-12.1, -21.68) * mm});
            skLineSegment(sketch, "E2856", {"start": v(-12.7, -22.01) * mm, "end": v(-14.74, -20.54) * mm});
            skArc(sketch, "E2857", {"start": v(-14.66, -20.44) * mm, "mid": v(-14.84, -20.47) * mm, "end": v(-14.8, -20.64) * mm});
            skArc(sketch, "E2858", {"start": v(-12.78, -22.11) * mm, "mid": v(-12.6, -22.09) * mm, "end": v(-12.64, -21.91) * mm});
            skLineSegment(sketch, "E2859", {"start": v(-16.1, -28.7) * mm, "end": v(-16.12, -28.55) * mm});
            skArc(sketch, "E2860", {"start": v(-16.07, -28.54) * mm, "mid": v(-16.13, -28.5) * mm, "end": v(-16.17, -28.56) * mm});
            skArc(sketch, "E2861", {"start": v(-16.15, -28.7) * mm, "mid": v(-16.1, -28.74) * mm, "end": v(-16.05, -28.68) * mm});
            skLineSegment(sketch, "E2862", {"start": v(-16.12, -28.55) * mm, "end": v(-16.17, -28.4) * mm});
            skArc(sketch, "E2863", {"start": v(-16.13, -28.39) * mm, "mid": v(-16.19, -28.36) * mm, "end": v(-16.22, -28.42) * mm});
            skArc(sketch, "E2864", {"start": v(-16.17, -28.57) * mm, "mid": v(-16.1, -28.6) * mm, "end": v(-16.08, -28.54) * mm});
            skLineSegment(sketch, "E2865", {"start": v(-16.17, -28.4) * mm, "end": v(-16.25, -28.27) * mm});
            skArc(sketch, "E2866", {"start": v(-16.2, -28.24) * mm, "mid": v(-16.27, -28.23) * mm, "end": v(-16.3, -28.3) * mm});
            skArc(sketch, "E2867", {"start": v(-16.22, -28.43) * mm, "mid": v(-16.15, -28.45) * mm, "end": v(-16.13, -28.38) * mm});
            skLineSegment(sketch, "E2868", {"start": v(-16.25, -28.27) * mm, "end": v(-16.35, -28.15) * mm});
            skArc(sketch, "E2869", {"start": v(-16.3, -28.11) * mm, "mid": v(-16.38, -28.1) * mm, "end": v(-16.39, -28.18) * mm});
            skArc(sketch, "E2870", {"start": v(-16.29, -28.3) * mm, "mid": v(-16.22, -28.3) * mm, "end": v(-16.2, -28.24) * mm});
            skLineSegment(sketch, "E2871", {"start": v(-16.35, -28.15) * mm, "end": v(-16.4, -28.1) * mm});
            skArc(sketch, "E2872", {"start": v(-16.37, -28.05) * mm, "mid": v(-16.44, -28.06) * mm, "end": v(-16.44, -28.13) * mm});
            skArc(sketch, "E2873", {"start": v(-16.38, -28.18) * mm, "mid": v(-16.31, -28.18) * mm, "end": v(-16.31, -28.1) * mm});
            skLineSegment(sketch, "E2874", {"start": v(-16.4, -28.1) * mm, "end": v(-19.45, -25.9) * mm});
            skArc(sketch, "E2875", {"start": v(-19.42, -25.85) * mm, "mid": v(-19.5, -25.86) * mm, "end": v(-19.48, -25.93) * mm});
            skArc(sketch, "E2876", {"start": v(-16.43, -28.13) * mm, "mid": v(-16.37, -28.12) * mm, "end": v(-16.38, -28.05) * mm});
            skLineSegment(sketch, "E2877", {"start": v(-19.45, -25.9) * mm, "end": v(-19.6, -25.84) * mm});
            skArc(sketch, "E2878", {"start": v(-19.58, -25.8) * mm, "mid": v(-19.64, -25.82) * mm, "end": v(-19.62, -25.89) * mm});
            skArc(sketch, "E2879", {"start": v(-19.47, -25.94) * mm, "mid": v(-19.4, -25.91) * mm, "end": v(-19.43, -25.85) * mm});
            skLineSegment(sketch, "E2880", {"start": v(-19.6, -25.84) * mm, "end": v(-19.75, -25.81) * mm});
            skArc(sketch, "E2881", {"start": v(-19.74, -25.76) * mm, "mid": v(-19.8, -25.8) * mm, "end": v(-19.76, -25.86) * mm});
            skArc(sketch, "E2882", {"start": v(-19.6, -25.89) * mm, "mid": v(-19.55, -25.85) * mm, "end": v(-19.59, -25.79) * mm});
            skLineSegment(sketch, "E2883", {"start": v(-19.75, -25.81) * mm, "end": v(-19.9, -25.8) * mm});
            skArc(sketch, "E2884", {"start": v(-19.9, -25.76) * mm, "mid": v(-19.96, -25.8) * mm, "end": v(-19.9, -25.86) * mm});
            skArc(sketch, "E2885", {"start": v(-19.75, -25.86) * mm, "mid": v(-19.7, -25.81) * mm, "end": v(-19.75, -25.76) * mm});
            skLineSegment(sketch, "E2886", {"start": v(-19.9, -25.8) * mm, "end": v(-20.04, -25.83) * mm});
            skArc(sketch, "E2887", {"start": v(-20.04, -25.78) * mm, "mid": v(-20.09, -25.84) * mm, "end": v(-20.03, -25.88) * mm});
            skArc(sketch, "E2888", {"start": v(-19.9, -25.86) * mm, "mid": v(-19.86, -25.8) * mm, "end": v(-19.91, -25.76) * mm});
            skLineSegment(sketch, "E2889", {"start": v(-20.04, -25.83) * mm, "end": v(-20.01, -25.97) * mm});
            skArc(sketch, "E2890", {"start": v(-20.06, -25.98) * mm, "mid": v(-20, -26.02) * mm, "end": v(-19.96, -25.96) * mm});
            skArc(sketch, "E2891", {"start": v(-19.99, -25.82) * mm, "mid": v(-20.04, -25.78) * mm, "end": v(-20.09, -25.84) * mm});
            skLineSegment(sketch, "E2892", {"start": v(-20.01, -25.97) * mm, "end": v(-19.96, -26.12) * mm});
            skArc(sketch, "E2893", {"start": v(-20, -26.13) * mm, "mid": v(-19.95, -26.16) * mm, "end": v(-19.92, -26.1) * mm});
            skArc(sketch, "E2894", {"start": v(-19.97, -25.95) * mm, "mid": v(-20.03, -25.92) * mm, "end": v(-20.06, -25.99) * mm});
            skLineSegment(sketch, "E2895", {"start": v(-19.96, -26.12) * mm, "end": v(-19.89, -26.25) * mm});
            skArc(sketch, "E2896", {"start": v(-19.93, -26.28) * mm, "mid": v(-19.86, -26.3) * mm, "end": v(-19.84, -26.23) * mm});
            skArc(sketch, "E2897", {"start": v(-19.92, -26.1) * mm, "mid": v(-19.99, -26.07) * mm, "end": v(-20, -26.14) * mm});
            skLineSegment(sketch, "E2898", {"start": v(-19.89, -26.25) * mm, "end": v(-19.79, -26.38) * mm});
            skArc(sketch, "E2899", {"start": v(-19.83, -26.4) * mm, "mid": v(-19.76, -26.42) * mm, "end": v(-19.75, -26.34) * mm});
            skArc(sketch, "E2900", {"start": v(-19.85, -26.22) * mm, "mid": v(-19.92, -26.21) * mm, "end": v(-19.93, -26.28) * mm});
            skLineSegment(sketch, "E2901", {"start": v(-19.79, -26.38) * mm, "end": v(-19.73, -26.43) * mm});
            skArc(sketch, "E2902", {"start": v(-19.76, -26.47) * mm, "mid": v(-19.7, -26.47) * mm, "end": v(-19.7, -26.4) * mm});
            skArc(sketch, "E2903", {"start": v(-19.75, -26.34) * mm, "mid": v(-19.82, -26.34) * mm, "end": v(-19.82, -26.41) * mm});
            skLineSegment(sketch, "E2904", {"start": v(-19.73, -26.43) * mm, "end": v(-16.69, -28.63) * mm});
            skArc(sketch, "E2905", {"start": v(-16.71, -28.67) * mm, "mid": v(-16.64, -28.66) * mm, "end": v(-16.66, -28.59) * mm});
            skArc(sketch, "E2906", {"start": v(-19.7, -26.4) * mm, "mid": v(-19.77, -26.4) * mm, "end": v(-19.76, -26.47) * mm});
            skLineSegment(sketch, "E2907", {"start": v(-16.69, -28.63) * mm, "end": v(-16.54, -28.68) * mm});
            skArc(sketch, "E2908", {"start": v(-16.55, -28.73) * mm, "mid": v(-16.5, -28.7) * mm, "end": v(-16.52, -28.64) * mm});
            skArc(sketch, "E2909", {"start": v(-16.67, -28.58) * mm, "mid": v(-16.73, -28.61) * mm, "end": v(-16.7, -28.68) * mm});
            skLineSegment(sketch, "E2910", {"start": v(-16.54, -28.68) * mm, "end": v(-16.38, -28.71) * mm});
            skArc(sketch, "E2911", {"start": v(-16.4, -28.76) * mm, "mid": v(-16.34, -28.72) * mm, "end": v(-16.38, -28.66) * mm});
            skArc(sketch, "E2912", {"start": v(-16.53, -28.63) * mm, "mid": v(-16.59, -28.67) * mm, "end": v(-16.55, -28.73) * mm});
            skLineSegment(sketch, "E2913", {"start": v(-16.38, -28.71) * mm, "end": v(-16.23, -28.71) * mm});
            skArc(sketch, "E2914", {"start": v(-16.23, -28.76) * mm, "mid": v(-16.18, -28.71) * mm, "end": v(-16.23, -28.66) * mm});
            skArc(sketch, "E2915", {"start": v(-16.38, -28.66) * mm, "mid": v(-16.43, -28.71) * mm, "end": v(-16.38, -28.76) * mm});
            skLineSegment(sketch, "E2916", {"start": v(-16.23, -28.71) * mm, "end": v(-16.1, -28.7) * mm});
            skArc(sketch, "E2917", {"start": v(-16.1, -28.74) * mm, "mid": v(-16.05, -28.68) * mm, "end": v(-16.1, -28.64) * mm});
            skArc(sketch, "E2918", {"start": v(-16.24, -28.66) * mm, "mid": v(-16.28, -28.72) * mm, "end": v(-16.22, -28.76) * mm});
            skLineSegment(sketch, "E2919", {"start": v(-16.18, -28.4) * mm, "end": v(-19.73, -25.82) * mm});
            skArc(sketch, "E2920", {"start": v(-19.7, -25.78) * mm, "mid": v(-19.77, -25.79) * mm, "end": v(-19.76, -25.86) * mm});
            skArc(sketch, "E2921", {"start": v(-16.2, -28.43) * mm, "mid": v(-16.14, -28.42) * mm, "end": v(-16.15, -28.35) * mm});
            skLineSegment(sketch, "E2922", {"start": v(-16.1, -28.7) * mm, "end": v(-20.03, -25.84) * mm});
            skArc(sketch, "E2923", {"start": v(-20, -25.8) * mm, "mid": v(-20.08, -25.8) * mm, "end": v(-20.06, -25.88) * mm});
            skArc(sketch, "E2924", {"start": v(-16.14, -28.73) * mm, "mid": v(-16.07, -28.72) * mm, "end": v(-16.08, -28.65) * mm});
            skLineSegment(sketch, "E2925", {"start": v(-16.43, -28.7) * mm, "end": v(-19.94, -26.15) * mm});
            skArc(sketch, "E2926", {"start": v(-19.91, -26.11) * mm, "mid": v(-19.98, -26.12) * mm, "end": v(-19.97, -26.2) * mm});
            skArc(sketch, "E2927", {"start": v(-16.46, -28.74) * mm, "mid": v(-16.4, -28.73) * mm, "end": v(-16.4, -28.66) * mm});
            skCircle(sketch, "E2928", {"center": v(-10.2, -16.42) * mm, "radius": 1.7 * mm});
            skArc(sketch, "E2929", {"start": v(-10.2, -17.3) * mm, "mid": v(-9.32, -16.42) * mm, "end": v(-10.2, -15.55) * mm});
            skArc(sketch, "E2930", {"start": v(-10.2, -15.55) * mm, "mid": v(-11.07, -16.42) * mm, "end": v(-10.2, -17.3) * mm});
            skCircle(sketch, "E2931", {"center": v(-16.07, -24.51) * mm, "radius": 1.7 * mm});
            skArc(sketch, "E2932", {"start": v(-16.07, -25.4) * mm, "mid": v(-15.2, -24.51) * mm, "end": v(-16.07, -23.64) * mm});
            skArc(sketch, "E2933", {"start": v(-16.07, -23.64) * mm, "mid": v(-16.95, -24.51) * mm, "end": v(-16.07, -25.4) * mm});
            skLineSegment(sketch, "E2934", {"start": v(4.19, 11.1) * mm, "end": v(4.19, 11.14) * mm});
            skArc(sketch, "E2935", {"start": v(4.21, 11.14) * mm, "mid": v(4.19, 11.17) * mm, "end": v(4.16, 11.14) * mm});
            skArc(sketch, "E2936", {"start": v(4.16, 11.1) * mm, "mid": v(4.19, 11.07) * mm, "end": v(4.21, 11.1) * mm});
            skLineSegment(sketch, "E2937", {"start": v(4.19, 11.14) * mm, "end": v(3.69, 11.3) * mm});
            skArc(sketch, "E2938", {"start": v(3.7, 11.32) * mm, "mid": v(3.66, 11.3) * mm, "end": v(3.68, 11.27) * mm});
            skArc(sketch, "E2939", {"start": v(4.18, 11.12) * mm, "mid": v(4.21, 11.13) * mm, "end": v(4.2, 11.17) * mm});
            skLineSegment(sketch, "E2940", {"start": v(3.69, 11.3) * mm, "end": v(3.19, 11.3) * mm});
            skArc(sketch, "E2941", {"start": v(3.19, 11.32) * mm, "mid": v(3.16, 11.3) * mm, "end": v(3.19, 11.27) * mm});
            skArc(sketch, "E2942", {"start": v(3.69, 11.27) * mm, "mid": v(3.71, 11.3) * mm, "end": v(3.69, 11.32) * mm});
            skLineSegment(sketch, "E2943", {"start": v(3.19, 11.3) * mm, "end": v(3.19, 11.1) * mm});
            skArc(sketch, "E2944", {"start": v(3.16, 11.1) * mm, "mid": v(3.19, 11.07) * mm, "end": v(3.21, 11.1) * mm});
            skArc(sketch, "E2945", {"start": v(3.21, 11.3) * mm, "mid": v(3.19, 11.32) * mm, "end": v(3.16, 11.3) * mm});
            skLineSegment(sketch, "E2946", {"start": v(3.19, 11.1) * mm, "end": v(4.19, 11.1) * mm});
            skArc(sketch, "E2947", {"start": v(4.19, 11.07) * mm, "mid": v(4.21, 11.1) * mm, "end": v(4.19, 11.12) * mm});
            skArc(sketch, "E2948", {"start": v(3.19, 11.12) * mm, "mid": v(3.16, 11.1) * mm, "end": v(3.19, 11.07) * mm});
            skLineSegment(sketch, "E2949", {"start": v(4.02, 11.2) * mm, "end": v(3.19, 11.2) * mm});
            skArc(sketch, "E2950", {"start": v(3.19, 11.22) * mm, "mid": v(3.16, 11.2) * mm, "end": v(3.19, 11.17) * mm});
            skArc(sketch, "E2951", {"start": v(4.02, 11.17) * mm, "mid": v(4.05, 11.2) * mm, "end": v(4.02, 11.22) * mm});
            skLineSegment(sketch, "E2952", {"start": v(-4.21, 11.1) * mm, "end": v(-4.21, 11.14) * mm});
            skArc(sketch, "E2953", {"start": v(-4.19, 11.14) * mm, "mid": v(-4.21, 11.17) * mm, "end": v(-4.24, 11.14) * mm});
            skArc(sketch, "E2954", {"start": v(-4.24, 11.1) * mm, "mid": v(-4.21, 11.07) * mm, "end": v(-4.19, 11.1) * mm});
            skLineSegment(sketch, "E2955", {"start": v(-4.21, 11.14) * mm, "end": v(-3.71, 11.3) * mm});
            skArc(sketch, "E2956", {"start": v(-3.7, 11.27) * mm, "mid": v(-3.69, 11.3) * mm, "end": v(-3.72, 11.32) * mm});
            skArc(sketch, "E2957", {"start": v(-4.22, 11.17) * mm, "mid": v(-4.24, 11.13) * mm, "end": v(-4.2, 11.12) * mm});
            skLineSegment(sketch, "E2958", {"start": v(-3.71, 11.3) * mm, "end": v(-3.21, 11.3) * mm});
            skArc(sketch, "E2959", {"start": v(-3.21, 11.27) * mm, "mid": v(-3.19, 11.3) * mm, "end": v(-3.21, 11.32) * mm});
            skArc(sketch, "E2960", {"start": v(-3.71, 11.32) * mm, "mid": v(-3.74, 11.3) * mm, "end": v(-3.71, 11.27) * mm});
            skLineSegment(sketch, "E2961", {"start": v(-3.21, 11.3) * mm, "end": v(-3.21, 11.1) * mm});
            skArc(sketch, "E2962", {"start": v(-3.24, 11.1) * mm, "mid": v(-3.21, 11.07) * mm, "end": v(-3.19, 11.1) * mm});
            skArc(sketch, "E2963", {"start": v(-3.19, 11.3) * mm, "mid": v(-3.21, 11.32) * mm, "end": v(-3.24, 11.3) * mm});
            skLineSegment(sketch, "E2964", {"start": v(-3.21, 11.1) * mm, "end": v(-4.21, 11.1) * mm});
            skArc(sketch, "E2965", {"start": v(-4.21, 11.12) * mm, "mid": v(-4.24, 11.1) * mm, "end": v(-4.21, 11.07) * mm});
            skArc(sketch, "E2966", {"start": v(-3.21, 11.07) * mm, "mid": v(-3.19, 11.1) * mm, "end": v(-3.21, 11.12) * mm});
            skLineSegment(sketch, "E2967", {"start": v(-3.21, 11.3) * mm, "end": v(-3.71, 11.3) * mm});
            skLineSegment(sketch, "E2968", {"start": v(-3.21, 11.2) * mm, "end": v(-4.05, 11.2) * mm});
            skArc(sketch, "E2969", {"start": v(-4.05, 11.22) * mm, "mid": v(-4.07, 11.2) * mm, "end": v(-4.05, 11.17) * mm});
            skArc(sketch, "E2970", {"start": v(-3.21, 11.17) * mm, "mid": v(-3.19, 11.2) * mm, "end": v(-3.21, 11.22) * mm});
            skCircle(sketch, "E2971", {"center": v(1.49, 9.1) * mm, "radius": 0.45 * mm});
            skArc(sketch, "E2972", {"start": v(1.49, 8.84) * mm, "mid": v(1.74, 9.1) * mm, "end": v(1.49, 9.34) * mm});
            skArc(sketch, "E2973", {"start": v(1.49, 9.34) * mm, "mid": v(1.24, 9.1) * mm, "end": v(1.49, 8.84) * mm});
            skCircle(sketch, "E2974", {"center": v(-1.51, 9.1) * mm, "radius": 0.45 * mm});
            skArc(sketch, "E2975", {"start": v(-1.51, 8.84) * mm, "mid": v(-1.26, 9.1) * mm, "end": v(-1.51, 9.34) * mm});
            skArc(sketch, "E2976", {"start": v(-1.51, 9.34) * mm, "mid": v(-1.76, 9.1) * mm, "end": v(-1.51, 8.84) * mm});
            skLineSegment(sketch, "E2977", {"start": v(2.68, 5.86) * mm, "end": v(2.68, 7.22) * mm});
            skArc(sketch, "E2978", {"start": v(2.68, 7.22) * mm, "mid": v(2.66, 7.26) * mm, "end": v(2.62, 7.28) * mm});
            skLineSegment(sketch, "E2979", {"start": v(2.62, 7.28) * mm, "end": v(2.06, 7.28) * mm});
            skArc(sketch, "E2980", {"start": v(2.06, 7.28) * mm, "mid": v(2.01, 7.26) * mm, "end": v(2, 7.22) * mm});
            skLineSegment(sketch, "E2981", {"start": v(2, 7.22) * mm, "end": v(2, 5.86) * mm});
            skArc(sketch, "E2982", {"start": v(2, 5.86) * mm, "mid": v(2.01, 5.82) * mm, "end": v(2.06, 5.8) * mm});
            skLineSegment(sketch, "E2983", {"start": v(2.06, 5.8) * mm, "end": v(2.62, 5.8) * mm});
            skArc(sketch, "E2984", {"start": v(2.62, 5.8) * mm, "mid": v(2.66, 5.82) * mm, "end": v(2.68, 5.86) * mm});
            skLineSegment(sketch, "E2985", {"start": v(-0.42, 5.86) * mm, "end": v(-0.42, 7.22) * mm});
            skArc(sketch, "E2986", {"start": v(-0.42, 7.22) * mm, "mid": v(-0.44, 7.26) * mm, "end": v(-0.48, 7.28) * mm});
            skLineSegment(sketch, "E2987", {"start": v(-0.48, 7.28) * mm, "end": v(-1.04, 7.28) * mm});
            skArc(sketch, "E2988", {"start": v(-1.04, 7.28) * mm, "mid": v(-1.09, 7.26) * mm, "end": v(-1.1, 7.22) * mm});
            skLineSegment(sketch, "E2989", {"start": v(-1.1, 7.22) * mm, "end": v(-1.1, 5.86) * mm});
            skArc(sketch, "E2990", {"start": v(-1.1, 5.86) * mm, "mid": v(-1.09, 5.82) * mm, "end": v(-1.04, 5.8) * mm});
            skLineSegment(sketch, "E2991", {"start": v(-1.04, 5.8) * mm, "end": v(-0.48, 5.8) * mm});
            skArc(sketch, "E2992", {"start": v(-0.48, 5.8) * mm, "mid": v(-0.44, 5.82) * mm, "end": v(-0.42, 5.86) * mm});
            skLineSegment(sketch, "E2993", {"start": v(-1.92, 5.86) * mm, "end": v(-1.92, 7.22) * mm});
            skArc(sketch, "E2994", {"start": v(-1.92, 7.22) * mm, "mid": v(-1.94, 7.26) * mm, "end": v(-1.98, 7.28) * mm});
            skLineSegment(sketch, "E2995", {"start": v(-1.98, 7.28) * mm, "end": v(-2.54, 7.28) * mm});
            skArc(sketch, "E2996", {"start": v(-2.54, 7.28) * mm, "mid": v(-2.59, 7.26) * mm, "end": v(-2.6, 7.22) * mm});
            skLineSegment(sketch, "E2997", {"start": v(-2.6, 7.22) * mm, "end": v(-2.6, 5.86) * mm});
            skArc(sketch, "E2998", {"start": v(-2.6, 5.86) * mm, "mid": v(-2.59, 5.82) * mm, "end": v(-2.54, 5.8) * mm});
            skLineSegment(sketch, "E2999", {"start": v(-2.54, 5.8) * mm, "end": v(-1.98, 5.8) * mm});
            skArc(sketch, "E3000", {"start": v(-1.98, 5.8) * mm, "mid": v(-1.94, 5.82) * mm, "end": v(-1.92, 5.86) * mm});
            skLineSegment(sketch, "E3001", {"start": v(2.58, 10.96) * mm, "end": v(2.58, 12.32) * mm});
            skArc(sketch, "E3002", {"start": v(2.58, 12.32) * mm, "mid": v(2.56, 12.36) * mm, "end": v(2.52, 12.38) * mm});
            skLineSegment(sketch, "E3003", {"start": v(2.52, 12.38) * mm, "end": v(1.96, 12.38) * mm});
            skArc(sketch, "E3004", {"start": v(1.96, 12.38) * mm, "mid": v(1.91, 12.36) * mm, "end": v(1.9, 12.32) * mm});
            skLineSegment(sketch, "E3005", {"start": v(1.9, 12.32) * mm, "end": v(1.9, 10.96) * mm});
            skArc(sketch, "E3006", {"start": v(1.9, 10.96) * mm, "mid": v(1.91, 10.92) * mm, "end": v(1.96, 10.9) * mm});
            skLineSegment(sketch, "E3007", {"start": v(1.96, 10.9) * mm, "end": v(2.52, 10.9) * mm});
            skArc(sketch, "E3008", {"start": v(2.52, 10.9) * mm, "mid": v(2.56, 10.92) * mm, "end": v(2.58, 10.96) * mm});
            skLineSegment(sketch, "E3009", {"start": v(-0.42, 10.96) * mm, "end": v(-0.42, 12.32) * mm});
            skArc(sketch, "E3010", {"start": v(-0.42, 12.32) * mm, "mid": v(-0.44, 12.36) * mm, "end": v(-0.48, 12.38) * mm});
            skLineSegment(sketch, "E3011", {"start": v(-0.48, 12.38) * mm, "end": v(-1.04, 12.38) * mm});
            skArc(sketch, "E3012", {"start": v(-1.04, 12.38) * mm, "mid": v(-1.09, 12.36) * mm, "end": v(-1.1, 12.32) * mm});
            skLineSegment(sketch, "E3013", {"start": v(-1.1, 12.32) * mm, "end": v(-1.1, 10.96) * mm});
            skArc(sketch, "E3014", {"start": v(-1.1, 10.96) * mm, "mid": v(-1.09, 10.92) * mm, "end": v(-1.04, 10.9) * mm});
            skLineSegment(sketch, "E3015", {"start": v(-1.04, 10.9) * mm, "end": v(-0.48, 10.9) * mm});
            skArc(sketch, "E3016", {"start": v(-0.48, 10.9) * mm, "mid": v(-0.44, 10.92) * mm, "end": v(-0.42, 10.96) * mm});
            skLineSegment(sketch, "E3017", {"start": v(-1.92, 10.96) * mm, "end": v(-1.92, 12.32) * mm});
            skArc(sketch, "E3018", {"start": v(-1.92, 12.32) * mm, "mid": v(-1.94, 12.36) * mm, "end": v(-1.98, 12.38) * mm});
            skLineSegment(sketch, "E3019", {"start": v(-1.98, 12.38) * mm, "end": v(-2.54, 12.38) * mm});
            skArc(sketch, "E3020", {"start": v(-2.54, 12.38) * mm, "mid": v(-2.59, 12.36) * mm, "end": v(-2.6, 12.32) * mm});
            skLineSegment(sketch, "E3021", {"start": v(-2.6, 12.32) * mm, "end": v(-2.6, 10.96) * mm});
            skArc(sketch, "E3022", {"start": v(-2.6, 10.96) * mm, "mid": v(-2.59, 10.92) * mm, "end": v(-2.54, 10.9) * mm});
            skLineSegment(sketch, "E3023", {"start": v(-2.54, 10.9) * mm, "end": v(-1.98, 10.9) * mm});
            skArc(sketch, "E3024", {"start": v(-1.98, 10.9) * mm, "mid": v(-1.94, 10.92) * mm, "end": v(-1.92, 10.96) * mm});
            skLineSegment(sketch, "E3025", {"start": v(3.2, 7.6) * mm, "end": v(3.2, 6.98) * mm});
            skArc(sketch, "E3026", {"start": v(3.2, 6.98) * mm, "mid": v(3.22, 6.93) * mm, "end": v(3.27, 6.9) * mm});
            skLineSegment(sketch, "E3027", {"start": v(3.27, 6.9) * mm, "end": v(4.1, 6.9) * mm});
            skArc(sketch, "E3028", {"start": v(4.1, 6.9) * mm, "mid": v(4.15, 6.93) * mm, "end": v(4.17, 6.98) * mm});
            skLineSegment(sketch, "E3029", {"start": v(4.17, 6.98) * mm, "end": v(4.17, 7.6) * mm});
            skArc(sketch, "E3030", {"start": v(4.17, 7.6) * mm, "mid": v(4.15, 7.65) * mm, "end": v(4.1, 7.67) * mm});
            skLineSegment(sketch, "E3031", {"start": v(4.1, 7.67) * mm, "end": v(3.27, 7.67) * mm});
            skArc(sketch, "E3032", {"start": v(3.27, 7.67) * mm, "mid": v(3.22, 7.65) * mm, "end": v(3.2, 7.6) * mm});
            skLineSegment(sketch, "E3033", {"start": v(3.19, 11.04) * mm, "end": v(3.19, 10.55) * mm});
            skArc(sketch, "E3034", {"start": v(3.19, 10.55) * mm, "mid": v(3.2, 10.5) * mm, "end": v(3.24, 10.5) * mm});
            skLineSegment(sketch, "E3035", {"start": v(3.24, 10.5) * mm, "end": v(4.13, 10.5) * mm});
            skArc(sketch, "E3036", {"start": v(4.13, 10.5) * mm, "mid": v(4.17, 10.5) * mm, "end": v(4.19, 10.55) * mm});
            skLineSegment(sketch, "E3037", {"start": v(4.19, 10.55) * mm, "end": v(4.19, 11.04) * mm});
            skArc(sketch, "E3038", {"start": v(4.19, 11.04) * mm, "mid": v(4.17, 11.07) * mm, "end": v(4.13, 11.09) * mm});
            skLineSegment(sketch, "E3039", {"start": v(4.13, 11.09) * mm, "end": v(3.24, 11.09) * mm});
            skArc(sketch, "E3040", {"start": v(3.24, 11.09) * mm, "mid": v(3.2, 11.07) * mm, "end": v(3.19, 11.04) * mm});
            skLineSegment(sketch, "E3041", {"start": v(-4.2, 7.6) * mm, "end": v(-4.2, 6.98) * mm});
            skArc(sketch, "E3042", {"start": v(-4.2, 6.98) * mm, "mid": v(-4.18, 6.93) * mm, "end": v(-4.13, 6.9) * mm});
            skLineSegment(sketch, "E3043", {"start": v(-4.13, 6.9) * mm, "end": v(-3.3, 6.9) * mm});
            skArc(sketch, "E3044", {"start": v(-3.3, 6.9) * mm, "mid": v(-3.25, 6.93) * mm, "end": v(-3.23, 6.98) * mm});
            skLineSegment(sketch, "E3045", {"start": v(-3.23, 6.98) * mm, "end": v(-3.23, 7.6) * mm});
            skArc(sketch, "E3046", {"start": v(-3.23, 7.6) * mm, "mid": v(-3.25, 7.65) * mm, "end": v(-3.3, 7.67) * mm});
            skLineSegment(sketch, "E3047", {"start": v(-3.3, 7.67) * mm, "end": v(-4.13, 7.67) * mm});
            skArc(sketch, "E3048", {"start": v(-4.13, 7.67) * mm, "mid": v(-4.18, 7.65) * mm, "end": v(-4.2, 7.6) * mm});
            skLineSegment(sketch, "E3049", {"start": v(-4.21, 11.04) * mm, "end": v(-4.21, 10.55) * mm});
            skArc(sketch, "E3050", {"start": v(-4.21, 10.55) * mm, "mid": v(-4.2, 10.5) * mm, "end": v(-4.16, 10.5) * mm});
            skLineSegment(sketch, "E3051", {"start": v(-4.16, 10.5) * mm, "end": v(-3.27, 10.5) * mm});
            skArc(sketch, "E3052", {"start": v(-3.27, 10.5) * mm, "mid": v(-3.23, 10.5) * mm, "end": v(-3.21, 10.55) * mm});
            skLineSegment(sketch, "E3053", {"start": v(-3.21, 10.55) * mm, "end": v(-3.21, 11.04) * mm});
            skArc(sketch, "E3054", {"start": v(-3.21, 11.04) * mm, "mid": v(-3.23, 11.07) * mm, "end": v(-3.27, 11.09) * mm});
            skLineSegment(sketch, "E3055", {"start": v(-3.27, 11.09) * mm, "end": v(-4.16, 11.09) * mm});
            skArc(sketch, "E3056", {"start": v(-4.16, 11.09) * mm, "mid": v(-4.2, 11.07) * mm, "end": v(-4.21, 11.04) * mm});
            skLineSegment(sketch, "E3057", {"start": v(-1.48, -12.76) * mm, "end": v(-1.48, -14.14) * mm});
            skArc(sketch, "E3058", {"start": v(-1.48, -14.14) * mm, "mid": v(-1.46, -14.18) * mm, "end": v(-1.42, -14.2) * mm});
            skLineSegment(sketch, "E3059", {"start": v(-1.42, -14.2) * mm, "end": v(-1.18, -14.2) * mm});
            skArc(sketch, "E3060", {"start": v(-1.18, -14.2) * mm, "mid": v(-1.14, -14.18) * mm, "end": v(-1.12, -14.14) * mm});
            skLineSegment(sketch, "E3061", {"start": v(-1.12, -14.14) * mm, "end": v(-1.12, -12.76) * mm});
            skArc(sketch, "E3062", {"start": v(-1.12, -12.76) * mm, "mid": v(-1.14, -12.71) * mm, "end": v(-1.18, -12.7) * mm});
            skLineSegment(sketch, "E3063", {"start": v(-1.18, -12.7) * mm, "end": v(-1.42, -12.7) * mm});
            skArc(sketch, "E3064", {"start": v(-1.42, -12.7) * mm, "mid": v(-1.46, -12.71) * mm, "end": v(-1.48, -12.76) * mm});
            skLineSegment(sketch, "E3065", {"start": v(-0.83, -12.76) * mm, "end": v(-0.83, -14.14) * mm});
            skArc(sketch, "E3066", {"start": v(-0.83, -14.14) * mm, "mid": v(-0.81, -14.18) * mm, "end": v(-0.77, -14.2) * mm});
            skLineSegment(sketch, "E3067", {"start": v(-0.77, -14.2) * mm, "end": v(-0.53, -14.2) * mm});
            skArc(sketch, "E3068", {"start": v(-0.53, -14.2) * mm, "mid": v(-0.49, -14.18) * mm, "end": v(-0.47, -14.14) * mm});
            skLineSegment(sketch, "E3069", {"start": v(-0.47, -14.14) * mm, "end": v(-0.47, -12.76) * mm});
            skArc(sketch, "E3070", {"start": v(-0.47, -12.76) * mm, "mid": v(-0.49, -12.71) * mm, "end": v(-0.53, -12.7) * mm});
            skLineSegment(sketch, "E3071", {"start": v(-0.53, -12.7) * mm, "end": v(-0.77, -12.7) * mm});
            skArc(sketch, "E3072", {"start": v(-0.77, -12.7) * mm, "mid": v(-0.81, -12.71) * mm, "end": v(-0.83, -12.76) * mm});
            skLineSegment(sketch, "E3073", {"start": v(-0.18, -12.76) * mm, "end": v(-0.18, -14.14) * mm});
            skArc(sketch, "E3074", {"start": v(-0.18, -14.14) * mm, "mid": v(-0.16, -14.18) * mm, "end": v(-0.12, -14.2) * mm});
            skLineSegment(sketch, "E3075", {"start": v(-0.12, -14.2) * mm, "end": v(0.12, -14.2) * mm});
            skArc(sketch, "E3076", {"start": v(0.12, -14.2) * mm, "mid": v(0.16, -14.18) * mm, "end": v(0.18, -14.14) * mm});
            skLineSegment(sketch, "E3077", {"start": v(0.18, -14.14) * mm, "end": v(0.18, -12.76) * mm});
            skArc(sketch, "E3078", {"start": v(0.18, -12.76) * mm, "mid": v(0.16, -12.71) * mm, "end": v(0.12, -12.7) * mm});
            skLineSegment(sketch, "E3079", {"start": v(0.12, -12.7) * mm, "end": v(-0.12, -12.7) * mm});
            skArc(sketch, "E3080", {"start": v(-0.12, -12.7) * mm, "mid": v(-0.16, -12.71) * mm, "end": v(-0.18, -12.76) * mm});
            skLineSegment(sketch, "E3081", {"start": v(0.47, -12.76) * mm, "end": v(0.47, -14.14) * mm});
            skArc(sketch, "E3082", {"start": v(0.47, -14.14) * mm, "mid": v(0.49, -14.18) * mm, "end": v(0.53, -14.2) * mm});
            skLineSegment(sketch, "E3083", {"start": v(0.53, -14.2) * mm, "end": v(0.77, -14.2) * mm});
            skArc(sketch, "E3084", {"start": v(0.77, -14.2) * mm, "mid": v(0.81, -14.18) * mm, "end": v(0.83, -14.14) * mm});
            skLineSegment(sketch, "E3085", {"start": v(0.83, -14.14) * mm, "end": v(0.83, -12.76) * mm});
            skArc(sketch, "E3086", {"start": v(0.83, -12.76) * mm, "mid": v(0.81, -12.71) * mm, "end": v(0.77, -12.7) * mm});
            skLineSegment(sketch, "E3087", {"start": v(0.77, -12.7) * mm, "end": v(0.53, -12.7) * mm});
            skArc(sketch, "E3088", {"start": v(0.53, -12.7) * mm, "mid": v(0.49, -12.71) * mm, "end": v(0.47, -12.76) * mm});
            skLineSegment(sketch, "E3089", {"start": v(1.12, -12.76) * mm, "end": v(1.12, -14.14) * mm});
            skArc(sketch, "E3090", {"start": v(1.12, -14.14) * mm, "mid": v(1.14, -14.18) * mm, "end": v(1.18, -14.2) * mm});
            skLineSegment(sketch, "E3091", {"start": v(1.18, -14.2) * mm, "end": v(1.42, -14.2) * mm});
            skArc(sketch, "E3092", {"start": v(1.42, -14.2) * mm, "mid": v(1.46, -14.18) * mm, "end": v(1.48, -14.14) * mm});
            skLineSegment(sketch, "E3093", {"start": v(1.48, -14.14) * mm, "end": v(1.48, -12.76) * mm});
            skArc(sketch, "E3094", {"start": v(1.48, -12.76) * mm, "mid": v(1.46, -12.71) * mm, "end": v(1.42, -12.7) * mm});
            skLineSegment(sketch, "E3095", {"start": v(1.42, -12.7) * mm, "end": v(1.18, -12.7) * mm});
            skArc(sketch, "E3096", {"start": v(1.18, -12.7) * mm, "mid": v(1.14, -12.71) * mm, "end": v(1.12, -12.76) * mm});
            skLineSegment(sketch, "E3097", {"start": v(-2.92, -13.06) * mm, "end": v(-3.88, -13.06) * mm});
            skArc(sketch, "E3098", {"start": v(-3.88, -13.06) * mm, "mid": v(-4, -13.12) * mm, "end": v(-4.06, -13.25) * mm});
            skLineSegment(sketch, "E3099", {"start": v(-4.06, -13.25) * mm, "end": v(-4.06, -14) * mm});
            skArc(sketch, "E3100", {"start": v(-4.06, -14) * mm, "mid": v(-4, -14.13) * mm, "end": v(-3.88, -14.19) * mm});
            skLineSegment(sketch, "E3101", {"start": v(-3.88, -14.19) * mm, "end": v(-2.92, -14.19) * mm});
            skArc(sketch, "E3102", {"start": v(-2.92, -14.19) * mm, "mid": v(-2.8, -14.13) * mm, "end": v(-2.74, -14) * mm});
            skLineSegment(sketch, "E3103", {"start": v(-2.74, -14) * mm, "end": v(-2.74, -13.25) * mm});
            skArc(sketch, "E3104", {"start": v(-2.74, -13.25) * mm, "mid": v(-2.8, -13.12) * mm, "end": v(-2.92, -13.06) * mm});
            skLineSegment(sketch, "E3105", {"start": v(-3.23, -16.93) * mm, "end": v(-3.23, -15.81) * mm});
            skArc(sketch, "E3106", {"start": v(-2.98, -15.81) * mm, "mid": v(-3.23, -15.56) * mm, "end": v(-3.48, -15.81) * mm});
            skArc(sketch, "E3107", {"start": v(-3.48, -16.93) * mm, "mid": v(-3.23, -17.18) * mm, "end": v(-2.98, -16.93) * mm});
            skLineSegment(sketch, "E3108", {"start": v(-0.4, -17.1) * mm, "end": v(-0.4, -16.3) * mm});
            skArc(sketch, "E3109", {"start": v(-0.4, -16.3) * mm, "mid": v(-0.46, -16.16) * mm, "end": v(-0.6, -16.1) * mm});
            skLineSegment(sketch, "E3110", {"start": v(-0.6, -16.1) * mm, "end": v(-1.4, -16.1) * mm});
            skArc(sketch, "E3111", {"start": v(-1.4, -16.1) * mm, "mid": v(-1.54, -16.16) * mm, "end": v(-1.6, -16.3) * mm});
            skLineSegment(sketch, "E3112", {"start": v(-1.6, -16.3) * mm, "end": v(-1.6, -17.1) * mm});
            skArc(sketch, "E3113", {"start": v(-1.6, -17.1) * mm, "mid": v(-1.54, -17.24) * mm, "end": v(-1.4, -17.3) * mm});
            skLineSegment(sketch, "E3114", {"start": v(-1.4, -17.3) * mm, "end": v(-0.6, -17.3) * mm});
            skArc(sketch, "E3115", {"start": v(-0.6, -17.3) * mm, "mid": v(-0.46, -17.24) * mm, "end": v(-0.4, -17.1) * mm});
            skLineSegment(sketch, "E3116", {"start": v(1.6, -17.1) * mm, "end": v(1.6, -16.3) * mm});
            skArc(sketch, "E3117", {"start": v(1.6, -16.3) * mm, "mid": v(1.54, -16.16) * mm, "end": v(1.4, -16.1) * mm});
            skLineSegment(sketch, "E3118", {"start": v(1.4, -16.1) * mm, "end": v(0.6, -16.1) * mm});
            skArc(sketch, "E3119", {"start": v(0.6, -16.1) * mm, "mid": v(0.46, -16.16) * mm, "end": v(0.4, -16.3) * mm});
            skLineSegment(sketch, "E3120", {"start": v(0.4, -16.3) * mm, "end": v(0.4, -17.1) * mm});
            skArc(sketch, "E3121", {"start": v(0.4, -17.1) * mm, "mid": v(0.46, -17.24) * mm, "end": v(0.6, -17.3) * mm});
            skLineSegment(sketch, "E3122", {"start": v(0.6, -17.3) * mm, "end": v(1.4, -17.3) * mm});
            skArc(sketch, "E3123", {"start": v(1.4, -17.3) * mm, "mid": v(1.54, -17.24) * mm, "end": v(1.6, -17.1) * mm});
            skLineSegment(sketch, "E3124", {"start": v(3.23, -16.93) * mm, "end": v(3.23, -15.81) * mm});
            skArc(sketch, "E3125", {"start": v(3.48, -15.81) * mm, "mid": v(3.23, -15.56) * mm, "end": v(2.98, -15.81) * mm});
            skArc(sketch, "E3126", {"start": v(2.98, -16.93) * mm, "mid": v(3.23, -17.18) * mm, "end": v(3.48, -16.93) * mm});
            skLineSegment(sketch, "E3127", {"start": v(3.88, -13.06) * mm, "end": v(2.92, -13.06) * mm});
            skArc(sketch, "E3128", {"start": v(2.92, -13.06) * mm, "mid": v(2.8, -13.12) * mm, "end": v(2.74, -13.25) * mm});
            skLineSegment(sketch, "E3129", {"start": v(2.74, -13.25) * mm, "end": v(2.74, -14) * mm});
            skArc(sketch, "E3130", {"start": v(2.74, -14) * mm, "mid": v(2.8, -14.13) * mm, "end": v(2.92, -14.19) * mm});
            skLineSegment(sketch, "E3131", {"start": v(2.92, -14.19) * mm, "end": v(3.88, -14.19) * mm});
            skArc(sketch, "E3132", {"start": v(3.88, -14.19) * mm, "mid": v(4, -14.13) * mm, "end": v(4.06, -14) * mm});
            skLineSegment(sketch, "E3133", {"start": v(4.06, -14) * mm, "end": v(4.06, -13.25) * mm});
            skArc(sketch, "E3134", {"start": v(4.06, -13.25) * mm, "mid": v(4, -13.12) * mm, "end": v(3.88, -13.06) * mm});
            skLineSegment(sketch, "E3135", {"start": v(0.86, -6.42) * mm, "end": v(0.86, -7.98) * mm});
            skArc(sketch, "E3136", {"start": v(0.86, -7.98) * mm, "mid": v(0.88, -8.02) * mm, "end": v(0.92, -8.04) * mm});
            skLineSegment(sketch, "E3137", {"start": v(0.92, -8.04) * mm, "end": v(1.48, -8.04) * mm});
            skArc(sketch, "E3138", {"start": v(1.48, -8.04) * mm, "mid": v(1.52, -8.02) * mm, "end": v(1.54, -7.98) * mm});
            skLineSegment(sketch, "E3139", {"start": v(1.54, -7.98) * mm, "end": v(1.54, -6.42) * mm});
            skArc(sketch, "E3140", {"start": v(1.54, -6.42) * mm, "mid": v(1.52, -6.37) * mm, "end": v(1.48, -6.36) * mm});
            skLineSegment(sketch, "E3141", {"start": v(1.48, -6.36) * mm, "end": v(0.92, -6.36) * mm});
            skArc(sketch, "E3142", {"start": v(0.92, -6.36) * mm, "mid": v(0.88, -6.37) * mm, "end": v(0.86, -6.42) * mm});
            skLineSegment(sketch, "E3143", {"start": v(-0.34, -6.42) * mm, "end": v(-0.34, -7.98) * mm});
            skArc(sketch, "E3144", {"start": v(-0.34, -7.98) * mm, "mid": v(-0.32, -8.02) * mm, "end": v(-0.28, -8.04) * mm});
            skLineSegment(sketch, "E3145", {"start": v(-0.28, -8.04) * mm, "end": v(0.28, -8.04) * mm});
            skArc(sketch, "E3146", {"start": v(0.28, -8.04) * mm, "mid": v(0.32, -8.02) * mm, "end": v(0.34, -7.98) * mm});
            skLineSegment(sketch, "E3147", {"start": v(0.34, -7.98) * mm, "end": v(0.34, -6.42) * mm});
            skArc(sketch, "E3148", {"start": v(0.34, -6.42) * mm, "mid": v(0.32, -6.37) * mm, "end": v(0.28, -6.36) * mm});
            skLineSegment(sketch, "E3149", {"start": v(0.28, -6.36) * mm, "end": v(-0.28, -6.36) * mm});
            skArc(sketch, "E3150", {"start": v(-0.28, -6.36) * mm, "mid": v(-0.32, -6.37) * mm, "end": v(-0.34, -6.42) * mm});
            skLineSegment(sketch, "E3151", {"start": v(-1.54, -6.42) * mm, "end": v(-1.54, -7.98) * mm});
            skArc(sketch, "E3152", {"start": v(-1.54, -7.98) * mm, "mid": v(-1.52, -8.02) * mm, "end": v(-1.48, -8.04) * mm});
            skLineSegment(sketch, "E3153", {"start": v(-1.48, -8.04) * mm, "end": v(-0.92, -8.04) * mm});
            skArc(sketch, "E3154", {"start": v(-0.92, -8.04) * mm, "mid": v(-0.88, -8.02) * mm, "end": v(-0.86, -7.98) * mm});
            skLineSegment(sketch, "E3155", {"start": v(-0.86, -7.98) * mm, "end": v(-0.86, -6.42) * mm});
            skArc(sketch, "E3156", {"start": v(-0.86, -6.42) * mm, "mid": v(-0.88, -6.37) * mm, "end": v(-0.92, -6.36) * mm});
            skLineSegment(sketch, "E3157", {"start": v(-0.92, -6.36) * mm, "end": v(-1.48, -6.36) * mm});
            skArc(sketch, "E3158", {"start": v(-1.48, -6.36) * mm, "mid": v(-1.52, -6.37) * mm, "end": v(-1.54, -6.42) * mm});
            skArc(sketch, "E3159", {"start": v(-5.6, -0.65) * mm, "mid": v(-5.35, -0.4) * mm, "end": v(-5.6, -0.15) * mm});
            skArc(sketch, "E3160", {"start": v(-5.6, -0.15) * mm, "mid": v(-5.85, -0.4) * mm, "end": v(-5.6, -0.65) * mm});
            skArc(sketch, "E3161", {"start": v(-5.6, -10.55) * mm, "mid": v(-5.35, -10.3) * mm, "end": v(-5.6, -10.05) * mm});
            skArc(sketch, "E3162", {"start": v(-5.6, -10.05) * mm, "mid": v(-5.85, -10.3) * mm, "end": v(-5.6, -10.55) * mm});
            skArc(sketch, "E3163", {"start": v(-5.6, -11.75) * mm, "mid": v(-5.35, -11.5) * mm, "end": v(-5.6, -11.25) * mm});
            skArc(sketch, "E3164", {"start": v(-5.6, -11.25) * mm, "mid": v(-5.85, -11.5) * mm, "end": v(-5.6, -11.75) * mm});
            skArc(sketch, "E3165", {"start": v(-4.5, -0.35) * mm, "mid": v(-4.25, -0.1) * mm, "end": v(-4.5, 0.15) * mm});
            skArc(sketch, "E3166", {"start": v(-4.5, 0.15) * mm, "mid": v(-4.75, -0.1) * mm, "end": v(-4.5, -0.35) * mm});
            skArc(sketch, "E3167", {"start": v(13.5, -2.75) * mm, "mid": v(13.75, -2.5) * mm, "end": v(13.5, -2.25) * mm});
            skArc(sketch, "E3168", {"start": v(13.5, -2.25) * mm, "mid": v(13.25, -2.5) * mm, "end": v(13.5, -2.75) * mm});
            skArc(sketch, "E3169", {"start": v(-13.4, -2.75) * mm, "mid": v(-13.15, -2.5) * mm, "end": v(-13.4, -2.25) * mm});
            skArc(sketch, "E3170", {"start": v(-13.4, -2.25) * mm, "mid": v(-13.65, -2.5) * mm, "end": v(-13.4, -2.75) * mm});
            skArc(sketch, "E3171", {"start": v(-12.3, -5.05) * mm, "mid": v(-12.05, -4.8) * mm, "end": v(-12.3, -4.55) * mm});
            skArc(sketch, "E3172", {"start": v(-12.3, -4.55) * mm, "mid": v(-12.55, -4.8) * mm, "end": v(-12.3, -5.05) * mm});
            skArc(sketch, "E3173", {"start": v(-2.38, -0.94) * mm, "mid": v(-2.13, -0.69) * mm, "end": v(-2.38, -0.44) * mm});
            skArc(sketch, "E3174", {"start": v(-2.38, -0.44) * mm, "mid": v(-2.63, -0.69) * mm, "end": v(-2.38, -0.94) * mm});
            skArc(sketch, "E3175", {"start": v(3.6, -6.75) * mm, "mid": v(3.85, -6.5) * mm, "end": v(3.6, -6.25) * mm});
            skArc(sketch, "E3176", {"start": v(3.6, -6.25) * mm, "mid": v(3.35, -6.5) * mm, "end": v(3.6, -6.75) * mm});
            skArc(sketch, "E3177", {"start": v(-3.45, 1.91) * mm, "mid": v(-3.2, 2.16) * mm, "end": v(-3.45, 2.41) * mm});
            skArc(sketch, "E3178", {"start": v(-3.45, 2.41) * mm, "mid": v(-3.7, 2.16) * mm, "end": v(-3.45, 1.91) * mm});
            skArc(sketch, "E3179", {"start": v(-6.8, -0.95) * mm, "mid": v(-6.55, -0.7) * mm, "end": v(-6.8, -0.45) * mm});
            skArc(sketch, "E3180", {"start": v(-6.8, -0.45) * mm, "mid": v(-7.05, -0.7) * mm, "end": v(-6.8, -0.95) * mm});
            skArc(sketch, "E3181", {"start": v(10.1, -8.45) * mm, "mid": v(10.35, -8.2) * mm, "end": v(10.1, -7.95) * mm});
            skArc(sketch, "E3182", {"start": v(10.1, -7.95) * mm, "mid": v(9.85, -8.2) * mm, "end": v(10.1, -8.45) * mm});
            skArc(sketch, "E3183", {"start": v(-9, 7.85) * mm, "mid": v(-8.75, 8.1) * mm, "end": v(-9, 8.35) * mm});
            skArc(sketch, "E3184", {"start": v(-9, 8.35) * mm, "mid": v(-9.25, 8.1) * mm, "end": v(-9, 7.85) * mm});
            skArc(sketch, "E3185", {"start": v(-10, -8.65) * mm, "mid": v(-9.75, -8.4) * mm, "end": v(-10, -8.15) * mm});
            skArc(sketch, "E3186", {"start": v(-10, -8.15) * mm, "mid": v(-10.25, -8.4) * mm, "end": v(-10, -8.65) * mm});
            skArc(sketch, "E3187", {"start": v(8.6, -9.9) * mm, "mid": v(8.85, -9.65) * mm, "end": v(8.6, -9.4) * mm});
            skArc(sketch, "E3188", {"start": v(8.6, -9.4) * mm, "mid": v(8.35, -9.65) * mm, "end": v(8.6, -9.9) * mm});
            skArc(sketch, "E3189", {"start": v(10.6, -6.35) * mm, "mid": v(10.85, -6.1) * mm, "end": v(10.6, -5.85) * mm});
            skArc(sketch, "E3190", {"start": v(10.6, -5.85) * mm, "mid": v(10.35, -6.1) * mm, "end": v(10.6, -6.35) * mm});
            skArc(sketch, "E3191", {"start": v(0.96, -2.22) * mm, "mid": v(1.2, -1.97) * mm, "end": v(0.96, -1.72) * mm});
            skArc(sketch, "E3192", {"start": v(0.96, -1.72) * mm, "mid": v(0.7, -1.97) * mm, "end": v(0.96, -2.22) * mm});
            skArc(sketch, "E3193", {"start": v(-0.24, -0.23) * mm, "mid": v(0, 0.02) * mm, "end": v(-0.24, 0.27) * mm});
            skArc(sketch, "E3194", {"start": v(-0.24, 0.27) * mm, "mid": v(-0.5, 0.02) * mm, "end": v(-0.24, -0.23) * mm});
            skArc(sketch, "E3195", {"start": v(-1.25, -2.14) * mm, "mid": v(-1, -1.89) * mm, "end": v(-1.25, -1.64) * mm});
            skArc(sketch, "E3196", {"start": v(-1.25, -1.64) * mm, "mid": v(-1.5, -1.89) * mm, "end": v(-1.25, -2.14) * mm});
            skArc(sketch, "E3197", {"start": v(-4.94, -13.4) * mm, "mid": v(-4.7, -13.14) * mm, "end": v(-4.94, -12.9) * mm});
            skArc(sketch, "E3198", {"start": v(-4.94, -12.9) * mm, "mid": v(-5.2, -13.14) * mm, "end": v(-4.94, -13.4) * mm});
            skArc(sketch, "E3199", {"start": v(4.95, -13.41) * mm, "mid": v(5.2, -13.16) * mm, "end": v(4.95, -12.91) * mm});
            skArc(sketch, "E3200", {"start": v(4.95, -12.91) * mm, "mid": v(4.7, -13.16) * mm, "end": v(4.95, -13.41) * mm});
            skArc(sketch, "E3201", {"start": v(-1.07, -9.25) * mm, "mid": v(-0.82, -9) * mm, "end": v(-1.07, -8.75) * mm});
            skArc(sketch, "E3202", {"start": v(-1.07, -8.75) * mm, "mid": v(-1.32, -9) * mm, "end": v(-1.07, -9.25) * mm});
            skArc(sketch, "E3203", {"start": v(2.3, -8.49) * mm, "mid": v(2.54, -8.24) * mm, "end": v(2.3, -7.99) * mm});
            skArc(sketch, "E3204", {"start": v(2.3, -7.99) * mm, "mid": v(2.04, -8.24) * mm, "end": v(2.3, -8.49) * mm});
            skArc(sketch, "E3205", {"start": v(-2.2, -15.55) * mm, "mid": v(-1.95, -15.3) * mm, "end": v(-2.2, -15.05) * mm});
            skArc(sketch, "E3206", {"start": v(-2.2, -15.05) * mm, "mid": v(-2.45, -15.3) * mm, "end": v(-2.2, -15.55) * mm});
            skArc(sketch, "E3207", {"start": v(2.2, -15.55) * mm, "mid": v(2.45, -15.3) * mm, "end": v(2.2, -15.05) * mm});
            skArc(sketch, "E3208", {"start": v(2.2, -15.05) * mm, "mid": v(1.95, -15.3) * mm, "end": v(2.2, -15.55) * mm});
            skArc(sketch, "E3209", {"start": v(1.15, 10.65) * mm, "mid": v(1.4, 10.9) * mm, "end": v(1.15, 11.15) * mm});
            skArc(sketch, "E3210", {"start": v(1.15, 11.15) * mm, "mid": v(0.9, 10.9) * mm, "end": v(1.15, 10.65) * mm});
            skArc(sketch, "E3211", {"start": v(2.93, 6.02) * mm, "mid": v(3.18, 6.27) * mm, "end": v(2.93, 6.52) * mm});
            skArc(sketch, "E3212", {"start": v(2.93, 6.52) * mm, "mid": v(2.68, 6.27) * mm, "end": v(2.93, 6.02) * mm});
            skArc(sketch, "E3213", {"start": v(-9.9, -6.55) * mm, "mid": v(-9.65, -6.3) * mm, "end": v(-9.9, -6.05) * mm});
            skArc(sketch, "E3214", {"start": v(-9.9, -6.05) * mm, "mid": v(-10.15, -6.3) * mm, "end": v(-9.9, -6.55) * mm});
            skArc(sketch, "E3215", {"start": v(-8.5, -4.75) * mm, "mid": v(-8.25, -4.5) * mm, "end": v(-8.5, -4.25) * mm});
            skArc(sketch, "E3216", {"start": v(-8.5, -4.25) * mm, "mid": v(-8.75, -4.5) * mm, "end": v(-8.5, -4.75) * mm});
            skArc(sketch, "E3217", {"start": v(10.1, 3.55) * mm, "mid": v(10.35, 3.8) * mm, "end": v(10.1, 4.05) * mm});
            skArc(sketch, "E3218", {"start": v(10.1, 4.05) * mm, "mid": v(9.85, 3.8) * mm, "end": v(10.1, 3.55) * mm});
            skArc(sketch, "E3219", {"start": v(8.09, -11.76) * mm, "mid": v(8.34, -11.5) * mm, "end": v(8.09, -11.26) * mm});
            skArc(sketch, "E3220", {"start": v(8.09, -11.26) * mm, "mid": v(7.84, -11.5) * mm, "end": v(8.09, -11.76) * mm});
            skArc(sketch, "E3221", {"start": v(-8.05, -11.76) * mm, "mid": v(-7.8, -11.5) * mm, "end": v(-8.05, -11.26) * mm});
            skArc(sketch, "E3222", {"start": v(-8.05, -11.26) * mm, "mid": v(-8.3, -11.5) * mm, "end": v(-8.05, -11.76) * mm});
            skArc(sketch, "E3223", {"start": v(-11, 0.97) * mm, "mid": v(-10.74, 1.22) * mm, "end": v(-11, 1.47) * mm});
            skArc(sketch, "E3224", {"start": v(-11, 1.47) * mm, "mid": v(-11.24, 1.22) * mm, "end": v(-11, 0.97) * mm});
            skArc(sketch, "E3225", {"start": v(-4.4, 9.63) * mm, "mid": v(-4.14, 9.88) * mm, "end": v(-4.4, 10.13) * mm});
            skArc(sketch, "E3226", {"start": v(-4.4, 10.13) * mm, "mid": v(-4.64, 9.88) * mm, "end": v(-4.4, 9.63) * mm});
            skArc(sketch, "E3227", {"start": v(2.22, -1.16) * mm, "mid": v(2.47, -0.9) * mm, "end": v(2.22, -0.66) * mm});
            skArc(sketch, "E3228", {"start": v(2.22, -0.66) * mm, "mid": v(1.97, -0.9) * mm, "end": v(2.22, -1.16) * mm});
            skArc(sketch, "E3229", {"start": v(5.72, 4.94) * mm, "mid": v(5.97, 5.19) * mm, "end": v(5.72, 5.44) * mm});
            skArc(sketch, "E3230", {"start": v(5.72, 5.44) * mm, "mid": v(5.47, 5.19) * mm, "end": v(5.72, 4.94) * mm});
            skArc(sketch, "E3231", {"start": v(1.3, -10.1) * mm, "mid": v(1.55, -9.84) * mm, "end": v(1.3, -9.6) * mm});
            skArc(sketch, "E3232", {"start": v(1.3, -9.6) * mm, "mid": v(1.05, -9.84) * mm, "end": v(1.3, -10.1) * mm});
            skArc(sketch, "E3233", {"start": v(-2.33, 7.2) * mm, "mid": v(-2.08, 7.45) * mm, "end": v(-2.33, 7.7) * mm});
            skArc(sketch, "E3234", {"start": v(-2.33, 7.7) * mm, "mid": v(-2.58, 7.45) * mm, "end": v(-2.33, 7.2) * mm});
            skArc(sketch, "E3235", {"start": v(-2.6, 8.27) * mm, "mid": v(-2.35, 8.52) * mm, "end": v(-2.6, 8.77) * mm});
            skArc(sketch, "E3236", {"start": v(-2.6, 8.77) * mm, "mid": v(-2.85, 8.52) * mm, "end": v(-2.6, 8.27) * mm});
            skArc(sketch, "E3237", {"start": v(-1.27, 2.3) * mm, "mid": v(-1.02, 2.54) * mm, "end": v(-1.27, 2.8) * mm});
            skArc(sketch, "E3238", {"start": v(-1.27, 2.8) * mm, "mid": v(-1.52, 2.54) * mm, "end": v(-1.27, 2.3) * mm});
            skArc(sketch, "E3239", {"start": v(-8.63, -0.99) * mm, "mid": v(-8.38, -0.74) * mm, "end": v(-8.63, -0.49) * mm});
            skArc(sketch, "E3240", {"start": v(-8.63, -0.49) * mm, "mid": v(-8.88, -0.74) * mm, "end": v(-8.63, -0.99) * mm});
            skArc(sketch, "E3241", {"start": v(-5.84, -5.99) * mm, "mid": v(-5.6, -5.74) * mm, "end": v(-5.84, -5.49) * mm});
            skArc(sketch, "E3242", {"start": v(-5.84, -5.49) * mm, "mid": v(-6.1, -5.74) * mm, "end": v(-5.84, -5.99) * mm});
            skArc(sketch, "E3243", {"start": v(-3, -11.75) * mm, "mid": v(-2.75, -11.5) * mm, "end": v(-3, -11.25) * mm});
            skArc(sketch, "E3244", {"start": v(-3, -11.25) * mm, "mid": v(-3.25, -11.5) * mm, "end": v(-3, -11.75) * mm});
            skArc(sketch, "E3245", {"start": v(0, -15.15) * mm, "mid": v(0.25, -14.9) * mm, "end": v(0, -14.65) * mm});
            skArc(sketch, "E3246", {"start": v(0, -14.65) * mm, "mid": v(-0.25, -14.9) * mm, "end": v(0, -15.15) * mm});
            skArc(sketch, "E3247", {"start": v(4.4, 1.7) * mm, "mid": v(4.65, 1.95) * mm, "end": v(4.4, 2.2) * mm});
            skArc(sketch, "E3248", {"start": v(4.4, 2.2) * mm, "mid": v(4.15, 1.95) * mm, "end": v(4.4, 1.7) * mm});
            skArc(sketch, "E3249", {"start": v(4.13, 3.8) * mm, "mid": v(4.38, 4.05) * mm, "end": v(4.13, 4.3) * mm});
            skArc(sketch, "E3250", {"start": v(4.13, 4.3) * mm, "mid": v(3.88, 4.05) * mm, "end": v(4.13, 3.8) * mm});
            skArc(sketch, "E3251", {"start": v(-10.57, 4.14) * mm, "mid": v(-10.32, 4.4) * mm, "end": v(-10.57, 4.64) * mm});
            skArc(sketch, "E3252", {"start": v(-10.57, 4.64) * mm, "mid": v(-10.82, 4.4) * mm, "end": v(-10.57, 4.14) * mm});
            skArc(sketch, "E3253", {"start": v(4.24, 5.99) * mm, "mid": v(4.5, 6.24) * mm, "end": v(4.24, 6.49) * mm});
            skArc(sketch, "E3254", {"start": v(4.24, 6.49) * mm, "mid": v(4, 6.24) * mm, "end": v(4.24, 5.99) * mm});
            skArc(sketch, "E3255", {"start": v(6.4, 1.65) * mm, "mid": v(6.65, 1.9) * mm, "end": v(6.4, 2.15) * mm});
            skArc(sketch, "E3256", {"start": v(6.4, 2.15) * mm, "mid": v(6.15, 1.9) * mm, "end": v(6.4, 1.65) * mm});
            skArc(sketch, "E3257", {"start": v(11.2, 4.8) * mm, "mid": v(11.45, 5.04) * mm, "end": v(11.2, 5.3) * mm});
            skArc(sketch, "E3258", {"start": v(11.2, 5.3) * mm, "mid": v(10.95, 5.04) * mm, "end": v(11.2, 4.8) * mm});
            skArc(sketch, "E3259", {"start": v(3.4, 1.25) * mm, "mid": v(3.65, 1.5) * mm, "end": v(3.4, 1.75) * mm});
            skArc(sketch, "E3260", {"start": v(3.4, 1.75) * mm, "mid": v(3.15, 1.5) * mm, "end": v(3.4, 1.25) * mm});
            skArc(sketch, "E3261", {"start": v(3.06, 3.76) * mm, "mid": v(3.31, 4) * mm, "end": v(3.06, 4.26) * mm});
            skArc(sketch, "E3262", {"start": v(3.06, 4.26) * mm, "mid": v(2.81, 4) * mm, "end": v(3.06, 3.76) * mm});
            skArc(sketch, "E3263", {"start": v(9.23, -2.53) * mm, "mid": v(9.48, -2.28) * mm, "end": v(9.23, -2.03) * mm});
            skArc(sketch, "E3264", {"start": v(9.23, -2.03) * mm, "mid": v(8.98, -2.28) * mm, "end": v(9.23, -2.53) * mm});
            skArc(sketch, "E3265", {"start": v(11.5, -8.55) * mm, "mid": v(11.75, -8.3) * mm, "end": v(11.5, -8.05) * mm});
            skArc(sketch, "E3266", {"start": v(11.5, -8.05) * mm, "mid": v(11.25, -8.3) * mm, "end": v(11.5, -8.55) * mm});
            skArc(sketch, "E3267", {"start": v(10.8, -11.37) * mm, "mid": v(11.05, -11.12) * mm, "end": v(10.8, -10.87) * mm});
            skArc(sketch, "E3268", {"start": v(10.8, -10.87) * mm, "mid": v(10.55, -11.12) * mm, "end": v(10.8, -11.37) * mm});
            skArc(sketch, "E3269", {"start": v(-3.35, -5.54) * mm, "mid": v(-3.1, -5.29) * mm, "end": v(-3.35, -5.04) * mm});
            skArc(sketch, "E3270", {"start": v(-3.35, -5.04) * mm, "mid": v(-3.6, -5.29) * mm, "end": v(-3.35, -5.54) * mm});
            skArc(sketch, "E3271", {"start": v(-10.68, -11.48) * mm, "mid": v(-10.43, -11.23) * mm, "end": v(-10.68, -10.98) * mm});
            skArc(sketch, "E3272", {"start": v(-10.68, -10.98) * mm, "mid": v(-10.93, -11.23) * mm, "end": v(-10.68, -11.48) * mm});
            skArc(sketch, "E3273", {"start": v(6.1, -11.35) * mm, "mid": v(6.35, -11.1) * mm, "end": v(6.1, -10.85) * mm});
            skArc(sketch, "E3274", {"start": v(6.1, -10.85) * mm, "mid": v(5.85, -11.1) * mm, "end": v(6.1, -11.35) * mm});
            skArc(sketch, "E3275", {"start": v(10.35, -0.85) * mm, "mid": v(10.6, -0.6) * mm, "end": v(10.35, -0.35) * mm});
            skArc(sketch, "E3276", {"start": v(10.35, -0.35) * mm, "mid": v(10.1, -0.6) * mm, "end": v(10.35, -0.85) * mm});
            skArc(sketch, "E3277", {"start": v(8.8, 1.65) * mm, "mid": v(9.05, 1.9) * mm, "end": v(8.8, 2.15) * mm});
            skArc(sketch, "E3278", {"start": v(8.8, 2.15) * mm, "mid": v(8.55, 1.9) * mm, "end": v(8.8, 1.65) * mm});
            skArc(sketch, "E3279", {"start": v(8.9, 3.85) * mm, "mid": v(9.16, 4.1) * mm, "end": v(8.9, 4.35) * mm});
            skArc(sketch, "E3280", {"start": v(8.9, 4.35) * mm, "mid": v(8.66, 4.1) * mm, "end": v(8.9, 3.85) * mm});
            skArc(sketch, "E3281", {"start": v(-0.74, 7.09) * mm, "mid": v(-0.5, 7.34) * mm, "end": v(-0.74, 7.59) * mm});
            skArc(sketch, "E3282", {"start": v(-0.74, 7.59) * mm, "mid": v(-1, 7.34) * mm, "end": v(-0.74, 7.09) * mm});
            skArc(sketch, "E3283", {"start": v(0, -4.49) * mm, "mid": v(0.26, -4.24) * mm, "end": v(0, -3.99) * mm});
            skArc(sketch, "E3284", {"start": v(0, -3.99) * mm, "mid": v(-0.24, -4.24) * mm, "end": v(0, -4.49) * mm});
            skArc(sketch, "E3285", {"start": v(0.85, -3.72) * mm, "mid": v(1.1, -3.47) * mm, "end": v(0.85, -3.22) * mm});
            skArc(sketch, "E3286", {"start": v(0.85, -3.22) * mm, "mid": v(0.6, -3.47) * mm, "end": v(0.85, -3.72) * mm});
            skArc(sketch, "E3287", {"start": v(1.73, -2.98) * mm, "mid": v(1.98, -2.73) * mm, "end": v(1.73, -2.48) * mm});
            skArc(sketch, "E3288", {"start": v(1.73, -2.48) * mm, "mid": v(1.48, -2.73) * mm, "end": v(1.73, -2.98) * mm});
            skArc(sketch, "E3289", {"start": v(2.3, -6.75) * mm, "mid": v(2.55, -6.5) * mm, "end": v(2.3, -6.25) * mm});
            skArc(sketch, "E3290", {"start": v(2.3, -6.25) * mm, "mid": v(2.05, -6.5) * mm, "end": v(2.3, -6.75) * mm});
            skArc(sketch, "E3291", {"start": v(9.65, 0) * mm, "mid": v(9.9, 0.25) * mm, "end": v(9.65, 0.5) * mm});
            skArc(sketch, "E3292", {"start": v(9.65, 0.5) * mm, "mid": v(9.4, 0.25) * mm, "end": v(9.65, 0) * mm});
            skArc(sketch, "E3293", {"start": v(7.9, 0) * mm, "mid": v(8.15, 0.25) * mm, "end": v(7.9, 0.5) * mm});
            skArc(sketch, "E3294", {"start": v(7.9, 0.5) * mm, "mid": v(7.65, 0.25) * mm, "end": v(7.9, 0) * mm});
            skArc(sketch, "E3295", {"start": v(-7.3, -6.05) * mm, "mid": v(-7.05, -5.8) * mm, "end": v(-7.3, -5.55) * mm});
            skArc(sketch, "E3296", {"start": v(-7.3, -5.55) * mm, "mid": v(-7.55, -5.8) * mm, "end": v(-7.3, -6.05) * mm});
            skArc(sketch, "E3297", {"start": v(-5.9, -8.35) * mm, "mid": v(-5.65, -8.1) * mm, "end": v(-5.9, -7.85) * mm});
            skArc(sketch, "E3298", {"start": v(-5.9, -7.85) * mm, "mid": v(-6.15, -8.1) * mm, "end": v(-5.9, -8.35) * mm});
            skArc(sketch, "E3299", {"start": v(-9.9, -2.95) * mm, "mid": v(-9.65, -2.7) * mm, "end": v(-9.9, -2.45) * mm});
            skArc(sketch, "E3300", {"start": v(-9.9, -2.45) * mm, "mid": v(-10.15, -2.7) * mm, "end": v(-9.9, -2.95) * mm});
            skArc(sketch, "E3301", {"start": v(-2.32, -3.23) * mm, "mid": v(-2.07, -2.98) * mm, "end": v(-2.32, -2.73) * mm});
            skArc(sketch, "E3302", {"start": v(-2.32, -2.73) * mm, "mid": v(-2.57, -2.98) * mm, "end": v(-2.32, -3.23) * mm});
            skArc(sketch, "E3303", {"start": v(2.62, -10.61) * mm, "mid": v(2.87, -10.36) * mm, "end": v(2.62, -10.11) * mm});
            skArc(sketch, "E3304", {"start": v(2.62, -10.11) * mm, "mid": v(2.37, -10.36) * mm, "end": v(2.62, -10.61) * mm});
            skArc(sketch, "E3305", {"start": v(-1.2, -10.53) * mm, "mid": v(-0.96, -10.28) * mm, "end": v(-1.2, -10.03) * mm});
            skArc(sketch, "E3306", {"start": v(-1.2, -10.03) * mm, "mid": v(-1.46, -10.28) * mm, "end": v(-1.2, -10.53) * mm});
            skArc(sketch, "E3307", {"start": v(-6.7, -7.45) * mm, "mid": v(-6.45, -7.2) * mm, "end": v(-6.7, -6.95) * mm});
            skArc(sketch, "E3308", {"start": v(-6.7, -6.95) * mm, "mid": v(-6.95, -7.2) * mm, "end": v(-6.7, -7.45) * mm});
            skArc(sketch, "E3309", {"start": v(-2.24, 0.23) * mm, "mid": v(-2, 0.48) * mm, "end": v(-2.24, 0.73) * mm});
            skArc(sketch, "E3310", {"start": v(-2.24, 0.73) * mm, "mid": v(-2.5, 0.48) * mm, "end": v(-2.24, 0.23) * mm});
            skArc(sketch, "E3311", {"start": v(9, 7.85) * mm, "mid": v(9.25, 8.1) * mm, "end": v(9, 8.35) * mm});
            skArc(sketch, "E3312", {"start": v(9, 8.35) * mm, "mid": v(8.75, 8.1) * mm, "end": v(9, 7.85) * mm});
            skArc(sketch, "E3313", {"start": v(3.95, 8.43) * mm, "mid": v(4.2, 8.68) * mm, "end": v(3.95, 8.93) * mm});
            skArc(sketch, "E3314", {"start": v(3.95, 8.93) * mm, "mid": v(3.7, 8.68) * mm, "end": v(3.95, 8.43) * mm});
            skArc(sketch, "E3315", {"start": v(0.84, 6.2) * mm, "mid": v(1.09, 6.45) * mm, "end": v(0.84, 6.7) * mm});
            skArc(sketch, "E3316", {"start": v(0.84, 6.7) * mm, "mid": v(0.59, 6.45) * mm, "end": v(0.84, 6.2) * mm});
            skSolve(sketch);
        }
        {
            var Q0;
            Q0=qCreatedBy(makeId("Top.planeOp"),FACE);
            var sketch = newSketch(context, id + "F1", { "sketchPlane" : qUnion([Q0])});
            skPoint(sketch, "E3317.0", {"position": v(-15, -2.36) * mm});
            skPoint(sketch, "E3318.0", {"position": v(-12, -11.35) * mm});
            skPoint(sketch, "E3319.0", {"position": v(15, -2.36) * mm});
            skPoint(sketch, "E3320.0", {"position": v(12.04, -11.28) * mm});
            skArc(sketch, "E3321", {"start": v(-15, -2.36) * mm, "mid": v(-14.22, -7.1) * mm, "end": v(-12, -11.35) * mm});
            skArc(sketch, "E3322", {"start": v(12.04, -11.28) * mm, "mid": v(14.24, -7.06) * mm, "end": v(15, -2.36) * mm});
            skPoint(sketch, "E3323.0", {"position": v(-12.44, 6) * mm});
            skPoint(sketch, "E3324.0", {"position": v(12.59, 5.8) * mm});
            skLineSegment(sketch, "E3325", {"start": v(-15, -2.36) * mm, "end": v(-12.44, 6) * mm});
            skLineSegment(sketch, "E3326", {"start": v(15, -2.36) * mm, "end": v(12.59, 5.8) * mm});
            skLineSegment(sketch, "E3327", {"start": v(12.04, -11.28) * mm, "end": v(-12, -11.35) * mm});
            skLineSegment(sketch, "E3328", {"start": v(-12.44, 6) * mm, "end": v(-5.84, 3.99) * mm});
            skLineSegment(sketch, "E3329", {"start": v(-5.84, 3.99) * mm, "end": v(-5.28, 5.8) * mm});
            skLineSegment(sketch, "E3330", {"start": v(-5.28, 5.8) * mm, "end": v(0, 5.8) * mm});
            skLineSegment(sketch, "E3331.MirrorCS", {"start": v(5.28, 5.8) * mm, "end": v(0, 5.8) * mm});
            skLineSegment(sketch, "E3332.MirrorCS", {"start": v(5.84, 3.99) * mm, "end": v(5.28, 5.8) * mm});
            skLineSegment(sketch, "E3333.MirrorCS", {"start": v(12.44, 6) * mm, "end": v(5.84, 3.99) * mm});
            skLineSegment(sketch, "E3334", {"start": v(12.59, 5.8) * mm, "end": v(12.44, 6) * mm});
            skArc(sketch, "E3335.0", {"start": v(-17, -2.37) * mm, "mid": v(-16.34, -7.04) * mm, "end": v(-14.42, -11.35) * mm});
            skArc(sketch, "E3336.0", {"start": v(14.46, -11.28) * mm, "mid": v(16.35, -7) * mm, "end": v(17, -2.37) * mm});
            skLineSegment(sketch, "E3337", {"start": v(15, -2.36) * mm, "end": v(17, -2.37) * mm});
            skLineSegment(sketch, "E3338", {"start": v(-15, -2.36) * mm, "end": v(-17, -2.37) * mm});
            skArc(sketch, "E3339.0", {"start": v(-15.5, -2.36) * mm, "mid": v(-14.76, -7.08) * mm, "end": v(-12.62, -11.34) * mm});
            skArc(sketch, "E3340.0", {"start": v(12.66, -11.28) * mm, "mid": v(14.77, -7.04) * mm, "end": v(15.5, -2.36) * mm});
            skLineSegment(sketch, "E3341", {"start": v(-12, -11.35) * mm, "end": v(-14.42, -11.35) * mm});
            skLineSegment(sketch, "E3342", {"start": v(-14.42, -11.35) * mm, "end": v(12.04, -11.28) * mm});
            skLineSegment(sketch, "E3343", {"start": v(12.04, -11.28) * mm, "end": v(14.46, -11.28) * mm});
            skSolve(sketch);
        }
        {
            var Q0;
            {var subQ0=sQuery(id+"F1.wireOp",EDGE,"E3335.0");Q0=makeQuery(id+"F1.imprint","IMPRINT",FACE,{"disambiguationData":[TD([[makeQuery(id+"F1.imprint","IMPRINT",EDGE,{"derivedFrom":subQ0}),1.0]])]});}
            var Q1;
            {var subQ5=sQuery(id+"F1.wireOp",EDGE,"E3339.0");Q1=makeQuery(id+"F1.imprint","IMPRINT",FACE,{"disambiguationData":[TD([[makeQuery(id+"F1.imprint","IMPRINT",EDGE,{"derivedFrom":subQ5}),1.0]])]});}
            var Q2;
            {var subQ4=sQuery(id+"F1.wireOp",EDGE,"E3322");Q2=makeQuery(id+"F1.imprint","IMPRINT",FACE,{"disambiguationData":[TD([[makeQuery(id+"F1.imprint","IMPRINT",EDGE,{"derivedFrom":subQ4}),1.0]])]});}
            var Q3;
            {var subQ0=sQuery(id+"F1.wireOp",EDGE,"E3322");Q3=makeQuery(id+"F1.imprint","IMPRINT",FACE,{"disambiguationData":[TD([[makeQuery(id+"F1.imprint","IMPRINT",EDGE,{"derivedFrom":subQ0}),-1.0]])]});}
            var Q4;
            {var subQ0=sQuery(id+"F1.wireOp",EDGE,"E3336.0");Q4=makeQuery(id+"F1.imprint","IMPRINT",FACE,{"disambiguationData":[TD([[makeQuery(id+"F1.imprint","IMPRINT",EDGE,{"derivedFrom":subQ0}),1.0]])]});}
            extrude(context, id + "F2", {"entities" : qUnion([Q0, Q1, Q2, Q3, Q4]), "depth" : 2 * mm});
        }
        {
            var Q0;
            Q0=makeQuery(id+"F2.opExtrude","CAP_FACE",FACE,{"disambiguationData":[OSD([sQuery(id+"F1.wireOp",EDGE,"E3325"),sQuery(id+"F1.wireOp",EDGE,"E3326"),sQuery(id+"F1.wireOp",EDGE,"E3328"),sQuery(id+"F1.wireOp",EDGE,"E3329"),sQuery(id+"F1.wireOp",EDGE,"E3330"),sQuery(id+"F1.wireOp",EDGE,"E3331.MirrorCS"),sQuery(id+"F1.wireOp",EDGE,"E3332.MirrorCS"),sQuery(id+"F1.wireOp",EDGE,"E3333.MirrorCS"),sQuery(id+"F1.wireOp",EDGE,"E3334"),sQuery(id+"F1.wireOp",EDGE,"E3335.0"),sQuery(id+"F1.wireOp",EDGE,"E3336.0"),sQuery(id+"F1.wireOp",EDGE,"E3337"),sQuery(id+"F1.wireOp",EDGE,"E3338"),sQuery(id+"F1.wireOp",EDGE,"E3342"),sQuery(id+"F1.wireOp",EDGE,"E3343")])],"isStart":false});
            var sketch = newSketch(context, id + "F3", { "sketchPlane" : qUnion([Q0])});
            skArc(sketch, "E3344.0", {"start": v(-15, -2.36) * mm, "mid": v(-14.22, -7.1) * mm, "end": v(-12, -11.35) * mm});
            skArc(sketch, "E3345.0", {"start": v(-17, -2.37) * mm, "mid": v(-16.34, -7.04) * mm, "end": v(-14.42, -11.35) * mm});
            skPoint(sketch, "E3346.0", {"position": v(-16, -2.37) * mm});
            skLineSegment(sketch, "E3347.0", {"start": v(-14.42, -11.35) * mm, "end": v(12.04, -11.28) * mm});
            skLineSegment(sketch, "E3348.0", {"start": v(12.04, -11.28) * mm, "end": v(14.46, -11.28) * mm});
            skArc(sketch, "E3349.0", {"start": v(14.46, -11.28) * mm, "mid": v(16.35, -7) * mm, "end": v(17, -2.37) * mm});
            skLineSegment(sketch, "E3350.0", {"start": v(15, -2.36) * mm, "end": v(17, -2.37) * mm});
            skArc(sketch, "E3351.0", {"start": v(12.04, -11.28) * mm, "mid": v(14.24, -7.06) * mm, "end": v(15, -2.36) * mm});
            skArc(sketch, "E3352.0", {"start": v(-15.5, -2.36) * mm, "mid": v(-14.76, -7.08) * mm, "end": v(-12.62, -11.34) * mm});
            skArc(sketch, "E3353.0", {"start": v(12.66, -11.28) * mm, "mid": v(14.77, -7.04) * mm, "end": v(15.5, -2.36) * mm});
            skSolve(sketch);
        }
        {
            var Q0;
            {var subQ0=sQuery(id+"F3.wireOp",EDGE,"E3345.0");Q0=makeQuery(id+"F3.imprint","IMPRINT",FACE,{"disambiguationData":[TD([[makeQuery(id+"F3.imprint","IMPRINT",EDGE,{"derivedFrom":subQ0}),1.0]])]});}
            var Q1;
            {var subQ0=sQuery(id+"F3.wireOp",EDGE,"E3349.0");Q1=makeQuery(id+"F3.imprint","IMPRINT",FACE,{"disambiguationData":[TD([[makeQuery(id+"F3.imprint","IMPRINT",EDGE,{"derivedFrom":subQ0}),1.0]])]});}
            extrude(context, id + "F4", {"entities" : qUnion([Q0, Q1]), "operationType" : NewBodyOperationType.ADD, "depth" : 2.75 * mm});
        }
        {
            var Q0;
            Q0=makeQuery(id+"F4.opExtrude","CAP_FACE",FACE,{"disambiguationData":[OSD([sQuery(id+"F1.wireOp",EDGE,"E3338"),sQuery(id+"F3.wireOp",EDGE,"E3344.0"),sQuery(id+"F3.wireOp",EDGE,"E3345.0"),sQuery(id+"F3.wireOp",EDGE,"E3347.0")])],"isStart":false});
            var sketch = newSketch(context, id + "F5", { "sketchPlane" : qUnion([Q0])});
            skArc(sketch, "E3354.0", {"start": v(-15, -2.36) * mm, "mid": v(-14.22, -7.1) * mm, "end": v(-12, -11.35) * mm});
            skLineSegment(sketch, "E3355.0", {"start": v(-15, -2.36) * mm, "end": v(-17, -2.37) * mm});
            skArc(sketch, "E3356.0", {"start": v(-17, -2.37) * mm, "mid": v(-16.34, -7.04) * mm, "end": v(-14.42, -11.35) * mm});
            skLineSegment(sketch, "E3357.0", {"start": v(-14.42, -11.35) * mm, "end": v(12.04, -11.28) * mm});
            skArc(sketch, "E3358.0", {"start": v(14.46, -11.28) * mm, "mid": v(16.35, -7) * mm, "end": v(17, -2.37) * mm});
            skLineSegment(sketch, "E3359.0", {"start": v(12.04, -11.28) * mm, "end": v(14.46, -11.28) * mm});
            skArc(sketch, "E3360.0", {"start": v(12.04, -11.28) * mm, "mid": v(14.24, -7.06) * mm, "end": v(15, -2.36) * mm});
            skLineSegment(sketch, "E3361.0", {"start": v(15, -2.36) * mm, "end": v(17, -2.37) * mm});
            skArc(sketch, "E3362.0", {"start": v(-13, -2.36) * mm, "mid": v(-12.06, -7.2) * mm, "end": v(-9.38, -11.34) * mm});
            skArc(sketch, "E3363.0", {"start": v(9.43, -11.3) * mm, "mid": v(12.07, -7.17) * mm, "end": v(13, -2.36) * mm});
            skLineSegment(sketch, "E3364", {"start": v(-13, -2.36) * mm, "end": v(-15, -2.36) * mm});
            skLineSegment(sketch, "E3365", {"start": v(13, -2.36) * mm, "end": v(15, -2.36) * mm});
            skSolve(sketch);
        }
        {
            var Q0;
            {var subQ0=sQuery(id+"F5.wireOp",EDGE,"E3355.0");Q0=makeQuery(id+"F5.imprint","IMPRINT",FACE,{"disambiguationData":[TD([[makeQuery(id+"F5.imprint","IMPRINT",EDGE,{"derivedFrom":subQ0}),1.0]])]});}
            var Q1;
            {var subQ4=sQuery(id+"F5.wireOp",EDGE,"E3362.0");Q1=makeQuery(id+"F5.imprint","IMPRINT",FACE,{"disambiguationData":[TD([[makeQuery(id+"F5.imprint","IMPRINT",EDGE,{"derivedFrom":subQ4}),-1.0]])]});}
            var Q2;
            {var subQ0=sQuery(id+"F5.wireOp",EDGE,"E3360.0");Q2=makeQuery(id+"F5.imprint","IMPRINT",FACE,{"disambiguationData":[TD([[makeQuery(id+"F5.imprint","IMPRINT",EDGE,{"derivedFrom":subQ0}),1.0]])]});}
            var Q3;
            Q3=makeQuery(id+"F5.imprint","IMPRINT",FACE,{"disambiguationData":[TD([[makeQuery(id+"F5.imprint","IMPRINT",EDGE,{"derivedFrom":sQuery(id+"F5.wireOp",EDGE,"E3358.0")}),1.0]])]});
            extrude(context, id + "F6", {"entities" : qUnion([Q0, Q1, Q2, Q3]), "operationType" : NewBodyOperationType.ADD, "depth" : 2 * mm});
        }
        {
            var Q0;
            Q0=makeQuery(id+"F6.opExtrude","CAP_EDGE",EDGE,{"disambiguationData":[OSD([sQuery(id+"F5.wireOp",EDGE,"E3362.0")])],"isStart":false});
            var Q1;
            Q1=makeQuery(id+"F6.opExtrude","CAP_EDGE",EDGE,{"disambiguationData":[OSD([sQuery(id+"F5.wireOp",EDGE,"E3363.0")])],"isStart":false});
            chamfer(context, id + "F7", {"entities" : qUnion([Q0, Q1]), "width" : 3 * mm, "tangentPropagation" : true});
        }
    });
